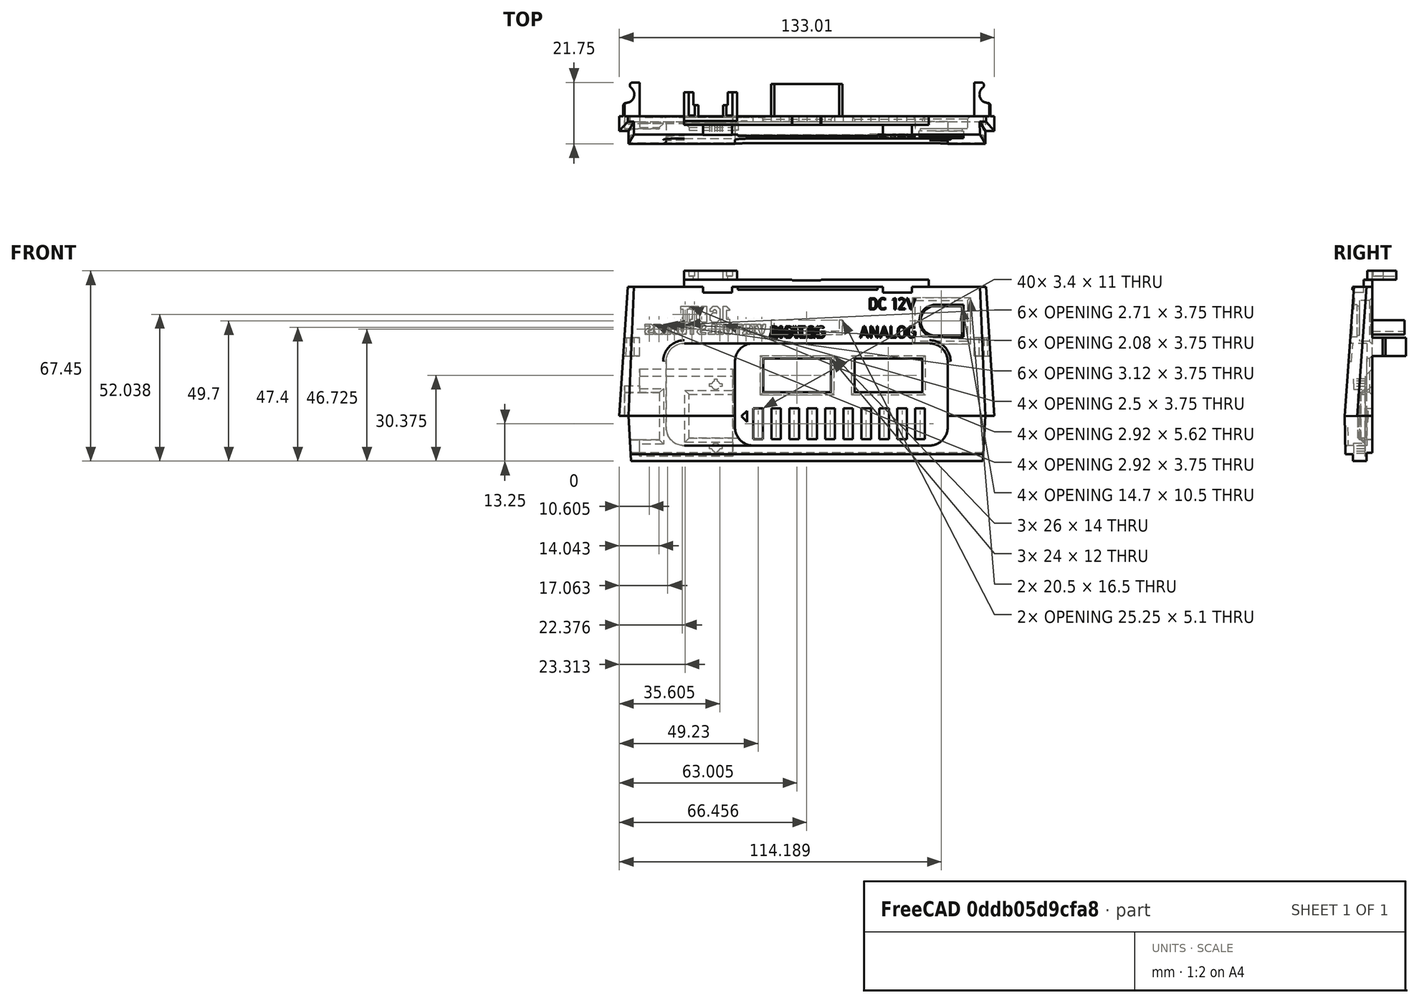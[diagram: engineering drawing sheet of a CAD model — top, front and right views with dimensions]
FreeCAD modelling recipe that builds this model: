
FCSTD DOCUMENT  (FreeCAD 1.0R39319 (Git))
Label: GameCube IO
License: Creative Commons Attribution-NonCommercial-ShareAlike 4.0
LicenseURL: https://creativecommons.org/licenses/by-nc-sa/4.0/
objects: PartDesign::Pocket×37, Sketcher::SketchObject×36, Part::Part2DObjectPython×13, PartDesign::Pad×12, PartDesign::Body×8, PartDesign::FeatureBase×7, PartDesign::Chamfer×3, PartDesign::Fillet×2, App::DocumentObjectGroup×2, PartDesign::LinearPattern×1, PartDesign::ShapeBinder×1
note: 272 computed .brp shape members not serialized (recipe doc carries the construction recipe); baked Part::Feature solids carry a one-line shape summary decoded from their .brp

FEATURE [Sketcher::SketchObject] Sketch
  ArcFitTolerance = 1e-06
  AttachmentSupport = -> [XZ_Plane]
  FullyConstrained = true
  MakeInternals = false
  MapMode = 5
  Placement = pos=(0,0,0) rot=(1,0,0;1.5708rad)
  sketch-geometry (11):
    g0: LineSegment StartX=0 StartY=0 StartZ=0 EndX=124.75 EndY=0 EndZ=0
    g1: LineSegment StartX=0 StartY=0 StartZ=0 EndX=-0.875 EndY=16 EndZ=0
    g2: LineSegment StartX=124.75 StartY=0 StartZ=0 EndX=125.625 EndY=16 EndZ=0
    g3: LineSegment [constr] StartX=-0.875 StartY=16 StartZ=0 EndX=125.625 EndY=16 EndZ=0
    g4: LineSegment [constr] StartX=62.375 StartY=0 StartZ=0 EndX=62.375 EndY=16 EndZ=0
    g5: LineSegment [constr] StartX=62.375 StartY=16 StartZ=0 EndX=62.375 EndY=61.75 EndZ=0
    g6: LineSegment StartX=-1.125 StartY=61.75 StartZ=0 EndX=125.875 EndY=61.75 EndZ=0
    g7: LineSegment StartX=-0.875 StartY=16 StartZ=0 EndX=-4.125 EndY=16 EndZ=0
    g8: LineSegment StartX=-4.125 StartY=16 StartZ=0 EndX=-1.125 EndY=61.75 EndZ=0
    g9: LineSegment StartX=125.625 StartY=16 StartZ=0 EndX=128.875 EndY=16 EndZ=0
    g10: LineSegment StartX=128.875 StartY=16 StartZ=0 EndX=125.875 EndY=61.75 EndZ=0
  constraints (29):
    c: Coincident(g0,g-1)
    c: PointOnObject(g0,g-1)
    c: Distance(g0) = 124.75
    c: Coincident(g1,g0)
    c: Coincident(g2,g0)
    c: Equal(g1,g2)
    c: Coincident(g3,g1)
    c: Distance(g3) = 126.5
    c: Vertical(g4)
    c: Symmetric(g0,g0,g4)
    c: Symmetric(g2,g1,g4)
    c: Coincident(g3,g2)
    c: Distance(g4) = 16
    c: Coincident(g5,g4)
    c: Vertical(g5)
    c: Distance(g5) = 45.75
    c: Horizontal(g6)
    c: Symmetric(g6,g6,g5)
    c: Coincident(g7,g1)
    c: Horizontal(g7)
    c: Coincident(g8,g7)
    c: Coincident(g8,g6)
    c: Coincident(g9,g2)
    c: Horizontal(g9)
    c: Coincident(g10,g9)
    c: Coincident(g10,g6)
    c: Equal(g8,g10)
    c: Distance(g9) = 3.25
    c: Distance(g6) = 127
FEATURE [PartDesign::Pad] Pad
  Direction = (0,-1,2e-16)
  Length = 3.1
  Length2 = 0.25
  Placement = pos=(0,0,0) rot=(1,0,0;1.5708rad)
  Profile = -> Sketch
  ReferenceAxis = -> Sketch [N_Axis]
  Refine = true
  Suppressed = false
  Type = 4
FEATURE [Sketcher::SketchObject] Sketch001
  ArcFitTolerance = 1e-06
  AttachmentSupport = -> [Pad]
  ExternalGeometry = -> [Pad]
  FullyConstrained = true
  MakeInternals = false
  MapMode = 5
  Placement = pos=(0,-3.1,0) rot=(1,0,0;1.5708rad)
  sketch-geometry (8):
    g0: LineSegment StartX=12.45 StartY=5.5 StartZ=0 EndX=112.3 EndY=5.5 EndZ=0
    g1: LineSegment StartX=112.3 StartY=5.5 StartZ=0 EndX=112.3 EndY=41.75 EndZ=0
    g2: LineSegment StartX=112.3 StartY=41.75 StartZ=0 EndX=12.45 EndY=41.75 EndZ=0
    g3: LineSegment StartX=12.45 StartY=41.75 StartZ=0 EndX=12.45 EndY=5.5 EndZ=0
    g4: GeomPoint [constr] X=62.375 Y=23.625 Z=0
    g5: LineSegment [constr] StartX=128.875 StartY=16 StartZ=0 EndX=112.3 EndY=16 EndZ=0
    g6: LineSegment [constr] StartX=-4.125 StartY=16 StartZ=0 EndX=12.45 EndY=16 EndZ=0
    g7: LineSegment [constr] StartX=12.45 StartY=5.5 StartZ=0 EndX=12.45 EndY=0 EndZ=0
  constraints (22):
    c: Coincident(g0,g1)
    c: Coincident(g1,g2)
    c: Coincident(g2,g3)
    c: Coincident(g3,g0)
    c: Horizontal(g0)
    c: Horizontal(g2)
    c: Vertical(g1)
    c: Vertical(g3)
    c: Symmetric(g2,g0,g4)
    c: Distance(g2) = 99.85
    c: Distance(g1) = 36.25
    c: Coincident(g5,g-4)
    c: PointOnObject(g5,g1)
    c: Horizontal(g5)
    c: Coincident(g6,g-3)
    c: PointOnObject(g6,g3)
    c: Horizontal(g6)
    c: Equal(g6,g5)
    c: Coincident(g7,g0)
    c: PointOnObject(g7,g-1)
    c: Vertical(g7)
    c: Distance(g7) = 5.5
FEATURE [PartDesign::Pocket] Pocket
  BaseFeature = -> Pad
  Direction = (0,1,-2e-16)
  Length = 0
  Length2 = 5
  Offset = -1.9
  Placement = pos=(0,0,0) rot=(1,0,0;1.5708rad)
  Profile = -> Sketch001
  ReferenceAxis = -> Sketch001 [N_Axis]
  Refine = true
  Suppressed = false
  Type = 3
  UpToFace = -> Pad [Face9]
FEATURE [Sketcher::SketchObject] Sketch002
  ArcFitTolerance = 1e-06
  AttachmentSupport = -> [Pocket]
  ExternalGeometry = -> [Pocket]
  FullyConstrained = true
  MakeInternals = false
  MapMode = 5
  Placement = pos=(0,-1.65,4e-16) rot=(1,0,0;1.5708rad)
  sketch-geometry (14):
    g0: LineSegment [constr] StartX=12.45 StartY=41.75 StartZ=0 EndX=112.3 EndY=41.75 EndZ=0
    g1: LineSegment [constr] StartX=112.3 StartY=5.5 StartZ=0 EndX=12.45 EndY=5.5 EndZ=0
    g2: ArcOfCircle CenterX=18.95 CenterY=35.25 CenterZ=0 NormalX=0 NormalY=0 NormalZ=1 AngleXU=0 Radius=6.5 StartAngle=1.5708 EndAngle=3.14159
    g3: ArcOfCircle CenterX=18.95 CenterY=12 CenterZ=0 NormalX=0 NormalY=0 NormalZ=1 AngleXU=0 Radius=6.5 StartAngle=3.14159 EndAngle=4.71239
    g4: ArcOfCircle CenterX=105.8 CenterY=35.25 CenterZ=0 NormalX=0 NormalY=0 NormalZ=1 AngleXU=0 Radius=6.5 StartAngle=-1.8e-15 EndAngle=1.5708
    g5: ArcOfCircle CenterX=105.8 CenterY=12 CenterZ=0 NormalX=0 NormalY=0 NormalZ=1 AngleXU=0 Radius=6.5 StartAngle=4.71239 EndAngle=6.28319
    g6: LineSegment StartX=105.8 StartY=41.75 StartZ=0 EndX=112.3 EndY=41.75 EndZ=0
    g7: LineSegment StartX=112.3 StartY=41.75 StartZ=0 EndX=112.3 EndY=35.25 EndZ=0
    g8: LineSegment StartX=112.3 StartY=12 StartZ=0 EndX=112.3 EndY=5.5 EndZ=0
    g9: LineSegment StartX=112.3 StartY=5.5 StartZ=0 EndX=105.8 EndY=5.5 EndZ=0
    g10: LineSegment StartX=18.95 StartY=5.5 StartZ=0 EndX=12.45 EndY=5.5 EndZ=0
    g11: LineSegment StartX=12.45 StartY=5.5 StartZ=0 EndX=12.45 EndY=12 EndZ=0
    g12: LineSegment StartX=12.45 StartY=35.25 StartZ=0 EndX=12.45 EndY=41.75 EndZ=0
    g13: LineSegment StartX=12.45 StartY=41.75 StartZ=0 EndX=18.95 EndY=41.75 EndZ=0
  constraints (32):
    c: Coincident(g0,g-3)
    c: Coincident(g0,g-4)
    c: Coincident(g1,g-4)
    c: Coincident(g1,g-3)
    c: PointOnObject(g2,g-3)
    c: PointOnObject(g2,g0)
    c: PointOnObject(g3,g-3)
    c: PointOnObject(g3,g1)
    c: PointOnObject(g4,g0)
    c: PointOnObject(g4,g-4)
    c: PointOnObject(g5,g-4)
    c: PointOnObject(g5,g1)
    c: Coincident(g6,g0)
    c: Coincident(g7,g0)
    c: Tangent(g7,g4) = 1.5708
    c: Coincident(g8,g1)
    c: Coincident(g9,g1)
    c: Tangent(g9,g5) = 1.5708
    c: Tangent(g10,g3) = 1.5708
    c: Coincident(g10,g1)
    c: Coincident(g11,g1)
    c: Tangent(g11,g3) = 1.5708
    c: Coincident(g12,g0)
    c: Coincident(g13,g0)
    c: Tangent(g13,g2) = 1.5708
    c: Tangent(g12,g2) = 1.5708
    c: Tangent(g8,g5) = 1.5708
    c: Tangent(g6,g4) = 1.5708
    c: Equal(g2,g3)
    c: Equal(g3,g5)
    c: Equal(g5,g4)
    c: Radius(g4) = 6.5
FEATURE [PartDesign::Pad] Pad001
  BaseFeature = -> Pocket
  Direction = (0,-1,2e-16)
  Length = 10
  Length2 = 10
  Placement = pos=(0,0,0) rot=(1,0,0;1.5708rad)
  Profile = -> Sketch002
  ReferenceAxis = -> Sketch002 [N_Axis]
  Refine = true
  Suppressed = false
  Type = 3
  UpToFace = -> Pocket [Face5]
FEATURE [PartDesign::Pad] Pad002
  BaseFeature = -> Pad001
  Direction = (0,-1,2e-16)
  Length = 10
  Length2 = 10
  Offset = -9.75
  Placement = pos=(0,0,0) rot=(1,0,0;1.5708rad)
  Profile = -> Pad001 [Face10]
  Refine = true
  Suppressed = false
  Type = 3
  UpToFace = -> Pad001 [Face4]
FEATURE [Sketcher::SketchObject] Sketch003
  ArcFitTolerance = 1e-06
  AttachmentSupport = -> [YZ_Plane]
  ExternalGeometry = -> [Pad002]
  FullyConstrained = true
  MakeInternals = false
  MapMode = 5
  Placement = pos=(0,0,0) rot=(0.57735,0.57735,0.57735;2.0944rad)
  sketch-geometry (13):
    g0: LineSegment [constr] StartX=0 StartY=0 StartZ=0 EndX=-6.5 EndY=0 EndZ=0
    g1: LineSegment StartX=-6.5 StartY=0 StartZ=0 EndX=-6.5 EndY=2.5 EndZ=0
    g2: LineSegment StartX=-6.5 StartY=2.5 StartZ=0 EndX=-9.25 EndY=2.5 EndZ=0
    g3: LineSegment StartX=-9.25 StartY=2.5 StartZ=0 EndX=-9.5 EndY=16 EndZ=0
    g4: LineSegment StartX=-9.5 StartY=16 StartZ=0 EndX=-6 EndY=64.25 EndZ=0
    g5: LineSegment StartX=-6 StartY=64.25 StartZ=0 EndX=-21.5 EndY=64.25 EndZ=0
    g6: LineSegment StartX=-21.5 StartY=64.25 StartZ=0 EndX=-21.5 EndY=0 EndZ=0
    g7: LineSegment StartX=-21.5 StartY=0 StartZ=0 EndX=-6.5 EndY=0 EndZ=0
    g8: LineSegment [constr] StartX=0.5 StartY=64.25 StartZ=0 EndX=-6 EndY=64.25 EndZ=0
    g9: LineSegment StartX=0.25 StartY=0 StartZ=0 EndX=0.25 EndY=3 EndZ=0
    g10: LineSegment StartX=0.25 StartY=3 StartZ=0 EndX=-1.75 EndY=3 EndZ=0
    g11: LineSegment StartX=-1.75 StartY=3 StartZ=0 EndX=-1.75 EndY=0 EndZ=0
    g12: LineSegment StartX=-1.75 StartY=0 StartZ=0 EndX=0.25 EndY=0 EndZ=0
  constraints (35):
    c: PointOnObject(g0,g-1)
    c: Coincident(g0,g1)
    c: Vertical(g1)
    c: Coincident(g1,g2)
    c: Horizontal(g2)
    c: Coincident(g2,g3)
    c: Coincident(g3,g4)
    c: Coincident(g4,g5)
    c: Horizontal(g5)
    c: Coincident(g5,g6)
    c: PointOnObject(g6,g-1)
    c: Vertical(g6)
    c: Coincident(g6,g7)
    c: Coincident(g7,g0)
    c: Coincident(g3,g-3)
    c: Coincident(g8,g-4)
    c: PointOnObject(g8,g-4)
    c: Coincident(g4,g8)
    c: Distance(g8) = 6.5
    c: Equal(g8,g0)
    c: Distance(g1) = 2.5
    c: Distance(g2) = 2.75
    c: Distance(g7) = 15
    c: Coincident(g9,g10)
    c: Coincident(g10,g11)
    c: Coincident(g11,g12)
    c: Coincident(g12,g9)
    c: Vertical(g9)
    c: Vertical(g11)
    c: Horizontal(g10)
    c: Horizontal(g12)
    c: Distance(g9) = 3
    c: Distance(g10) = 2
    c: Coincident(g-1,g0)
    c: Coincident(g-5,g9)
FEATURE [PartDesign::Pocket] Pocket001
  BaseFeature = -> Pad002
  Direction = (-1,0,0)
  Length = 150
  Length2 = 150
  Placement = pos=(0,0,0) rot=(1,0,0;1.5708rad)
  Profile = -> Sketch003
  ReferenceAxis = -> Sketch003 [N_Axis]
  Refine = true
  Suppressed = false
  Type = 4
FEATURE [Sketcher::SketchObject] Sketch004
  ArcFitTolerance = 1e-06
  AttachmentSupport = -> [Pocket001]
  ExternalGeometry = -> [Pocket001]
  FullyConstrained = true
  MakeInternals = false
  MapMode = 5
  Placement = pos=(0,-10.6048,0.769262) rot=(1,0,0;1.49838rad)
  sketch-geometry (16):
    g0: LineSegment [constr] StartX=128.917 StartY=14.0456 StartZ=0 EndX=125.677 EndY=14.0456 EndZ=0
    g1: LineSegment StartX=125.677 StartY=14.0456 StartZ=0 EndX=123.098 EndY=74.9911 EndZ=0
    g2: LineSegment [constr] StartX=123.098 StartY=74.9911 StartZ=0 EndX=126.338 EndY=74.9911 EndZ=0
    g3: LineSegment [constr] StartX=126.338 StartY=74.9911 StartZ=0 EndX=128.875 EndY=15.0447 EndZ=0
    g4: LineSegment [constr] StartX=-4.125 StartY=15.0447 StartZ=0 EndX=-1.58811 EndY=74.9911 EndZ=0
    g5: LineSegment [constr] StartX=-1.58811 StartY=74.9911 StartZ=0 EndX=1.65232 EndY=74.9911 EndZ=0
    g6: LineSegment StartX=1.65232 StartY=74.9911 StartZ=0 EndX=-0.926847 EndY=14.0456 EndZ=0
    g7: LineSegment [constr] StartX=-0.926847 StartY=14.0456 StartZ=0 EndX=-4.16728 EndY=14.0456 EndZ=0
    g8: LineSegment StartX=1.65232 StartY=74.9911 StartZ=0 EndX=-8.34768 EndY=74.9911 EndZ=0
    g9: LineSegment StartX=-8.34768 StartY=74.9911 StartZ=0 EndX=-10.9268 EndY=14.0456 EndZ=0
    g10: LineSegment StartX=-10.9268 StartY=14.0456 StartZ=0 EndX=-0.926847 EndY=14.0456 EndZ=0
    g11: LineSegment StartX=125.677 StartY=14.0456 StartZ=0 EndX=135.677 EndY=14.0456 EndZ=0
    g12: LineSegment StartX=135.677 StartY=14.0456 StartZ=0 EndX=133.098 EndY=74.9911 EndZ=0
    g13: LineSegment StartX=133.098 StartY=74.9911 StartZ=0 EndX=123.098 EndY=74.9911 EndZ=0
    g14: LineSegment [constr] StartX=128.875 StartY=15.0447 StartZ=0 EndX=128.917 EndY=14.0456 EndZ=0
    g15: LineSegment [constr] StartX=-4.125 StartY=15.0447 StartZ=0 EndX=-4.16728 EndY=14.0456 EndZ=0
  constraints (44):
    c: Horizontal(g0)
    c: Coincident(g1,g0)
    c: Coincident(g2,g1)
    c: Horizontal(g2)
    c: Coincident(g3,g2)
    c: PointOnObject(g-4,g3)
    c: Parallel(g1,g3)
    c: Distance(g3) = 60
    c: Coincident(g5,g4)
    c: Coincident(g6,g5)
    c: Coincident(g7,g6)
    c: Horizontal(g7)
    c: Horizontal(g5)
    c: Parallel(g4,g6)
    c: PointOnObject(g-3,g4)
    c: Equal(g5,g2)
    c: Equal(g3,g4)
    c: Coincident(g5,g8)
    c: Horizontal(g8)
    c: Coincident(g8,g9)
    c: Coincident(g9,g10)
    c: Coincident(g10,g6)
    c: Horizontal(g10)
    c: Coincident(g0,g11)
    c: Horizontal(g11)
    c: Coincident(g11,g12)
    c: Coincident(g12,g13)
    c: Coincident(g13,g1)
    c: Horizontal(g13)
    c: Parallel(g3,g12)
    c: Parallel(g6,g9)
    c: Equal(g10,g11)
    c: Distance(g11) = 10
    c: Coincident(g-4,g3)
    c: Coincident(g14,g3)
    c: Coincident(g14,g0)
    c: Parallel(g3,g14)
    c: PointOnObject(g-5,g1)
    c: Distance(g14) = 1
    c: Coincident(g4,g-3)
    c: Coincident(g15,g4)
    c: Coincident(g15,g7)
    c: Parallel(g4,g15)
    c: Equal(g15,g14)
FEATURE [PartDesign::Pocket] Pocket002
  BaseFeature = -> Pocket001
  Direction = (0,0.997379,-0.0723488)
  Length = 4.5
  Length2 = 5
  Placement = pos=(0,0,0) rot=(1,0,0;1.5708rad)
  Profile = -> Sketch004
  ReferenceAxis = -> Sketch004 [N_Axis]
  Refine = true
  Suppressed = false
  Type = 0
FEATURE [Sketcher::SketchObject] Sketch005
  ArcFitTolerance = 1e-06
  AttachmentSupport = -> [Pocket002]
  ExternalGeometry = -> [Pocket002]
  FullyConstrained = true
  MakeInternals = false
  MapMode = 5
  Placement = pos=(0,0,61.75) rot=(0,0,1;3.14159rad)
  sketch-geometry (6):
    g0: LineSegment StartX=-105.575 StartY=-0.25 StartZ=0 EndX=-18.875 EndY=-0.25 EndZ=0
    g1: LineSegment StartX=-18.875 StartY=-0.25 StartZ=0 EndX=-18.875 EndY=2.75 EndZ=0
    g2: LineSegment StartX=-18.875 StartY=2.75 StartZ=0 EndX=-105.575 EndY=2.75 EndZ=0
    g3: LineSegment StartX=-105.575 StartY=2.75 StartZ=0 EndX=-105.575 EndY=-0.25 EndZ=0
    g4: LineSegment [constr] StartX=-125.875 StartY=-0.25 StartZ=0 EndX=-105.575 EndY=-0.25 EndZ=0
    g5: LineSegment [constr] StartX=-18.875 StartY=-0.25 StartZ=0 EndX=1.125 EndY=-0.25 EndZ=0
  constraints (16):
    c: Coincident(g0,g1)
    c: Coincident(g1,g2)
    c: Coincident(g2,g3)
    c: Coincident(g3,g0)
    c: Horizontal(g0)
    c: Horizontal(g2)
    c: Vertical(g1)
    c: Vertical(g3)
    c: PointOnObject(g0,g-3)
    c: Coincident(g4,g-3)
    c: Coincident(g4,g0)
    c: Coincident(g5,g0)
    c: Coincident(g5,g-3)
    c: Distance(g5) = 20
    c: Distance(g4) = 20.3
    c: Distance(g1) = 3
FEATURE [PartDesign::Pad] Pad003
  BaseFeature = -> Pocket002
  Direction = (0,0,1)
  Length = 2.5
  Length2 = 10
  Placement = pos=(0,0,0) rot=(1,0,0;1.5708rad)
  Profile = -> Sketch005
  ReferenceAxis = -> Sketch005 [N_Axis]
  Refine = true
  Suppressed = false
  Type = 0
FEATURE [Sketcher::SketchObject] Sketch006
  ArcFitTolerance = 1e-06
  AttachmentSupport = -> [Pad003]
  FullyConstrained = true
  MakeInternals = false
  MapMode = 5
  Placement = pos=(0,-2.75,6e-16) rot=(1,0,0;1.5708rad)
  sketch-geometry (10):
    g0: LineSegment [constr] StartX=1.075 StartY=64.25 StartZ=0 EndX=25.575 EndY=64.25 EndZ=0
    g1: LineSegment [constr] StartX=123.675 StartY=64.25 StartZ=0 EndX=99.675 EndY=64.25 EndZ=0
    g2: LineSegment StartX=25.575 StartY=64.25 StartZ=0 EndX=25.575 EndY=59.75 EndZ=0
    g3: LineSegment StartX=25.575 StartY=59.75 StartZ=0 EndX=35.875 EndY=59.75 EndZ=0
    g4: LineSegment StartX=35.875 StartY=59.75 StartZ=0 EndX=35.875 EndY=64.25 EndZ=0
    g5: LineSegment StartX=35.875 StartY=64.25 StartZ=0 EndX=25.575 EndY=64.25 EndZ=0
    g6: LineSegment StartX=99.675 StartY=64.25 StartZ=0 EndX=89.375 EndY=64.25 EndZ=0
    g7: LineSegment StartX=89.375 StartY=64.25 StartZ=0 EndX=89.375 EndY=59.75 EndZ=0
    g8: LineSegment StartX=89.375 StartY=59.75 StartZ=0 EndX=99.675 EndY=59.75 EndZ=0
    g9: LineSegment StartX=99.675 StartY=59.75 StartZ=0 EndX=99.675 EndY=64.25 EndZ=0
  constraints (28):
    c: Coincident(g0,g-3)
    c: PointOnObject(g0,g-3)
    c: Coincident(g1,g-3)
    c: PointOnObject(g1,g-3)
    c: Coincident(g2,g3)
    c: Coincident(g3,g4)
    c: Coincident(g4,g5)
    c: Coincident(g5,g2)
    c: Vertical(g2)
    c: Vertical(g4)
    c: Horizontal(g3)
    c: Horizontal(g5)
    c: Coincident(g2,g0)
    c: Coincident(g6,g7)
    c: Coincident(g7,g8)
    c: Coincident(g8,g9)
    c: Coincident(g9,g6)
    c: Horizontal(g6)
    c: Horizontal(g8)
    c: Vertical(g7)
    c: Vertical(g9)
    c: Coincident(g6,g1)
    c: Distance(g0) = 24.5
    c: Distance(g5) = 10.3
    c: Equal(g5,g6)
    c: Equal(g7,g4)
    c: Distance(g2) = 4.5
    c: Distance(g1) = 24
FEATURE [PartDesign::Pocket] Pocket003
  BaseFeature = -> Pad003
  Direction = (0,1,-2e-16)
  Length = 5
  Length2 = 5
  Placement = pos=(0,0,0) rot=(1,0,0;1.5708rad)
  Profile = -> Sketch006
  ReferenceAxis = -> Sketch006 [N_Axis]
  Refine = true
  Reversed = true
  Suppressed = false
  Type = 1
FEATURE [Sketcher::SketchObject] Sketch007
  ArcFitTolerance = 1e-06
  AttachmentSupport = -> [Pocket003]
  ExternalGeometry = -> [Pocket003]
  FullyConstrained = true
  MakeInternals = false
  MapMode = 5
  Placement = pos=(0,-2.75,-5.1e-15) rot=(1,0,0;1.5708rad)
  sketch-geometry (6):
    g0: LineSegment [constr] StartX=35.875 StartY=61.75 StartZ=0 EndX=37.875 EndY=61.75 EndZ=0
    g1: LineSegment [constr] StartX=89.375 StartY=61.75 StartZ=0 EndX=87.375 EndY=61.75 EndZ=0
    g2: LineSegment StartX=37.875 StartY=61.75 StartZ=0 EndX=37.875 EndY=60.75 EndZ=0
    g3: LineSegment StartX=37.875 StartY=60.75 StartZ=0 EndX=87.375 EndY=60.75 EndZ=0
    g4: LineSegment StartX=87.375 StartY=60.75 StartZ=0 EndX=87.375 EndY=61.75 EndZ=0
    g5: LineSegment StartX=87.375 StartY=61.75 StartZ=0 EndX=37.875 EndY=61.75 EndZ=0
  constraints (16):
    c: Coincident(g2,g3)
    c: Coincident(g3,g4)
    c: Coincident(g4,g5)
    c: Coincident(g5,g2)
    c: Vertical(g2)
    c: Vertical(g4)
    c: Horizontal(g3)
    c: Coincident(g2,g0)
    c: Coincident(g4,g1)
    c: Equal(g1,g0)
    c: Distance(g0) = 2
    c: Distance(g2) = 1
    c: Coincident(g0,g-3)
    c: Coincident(g1,g-3)
    c: PointOnObject(g0,g-3)
    c: PointOnObject(g1,g-3)
FEATURE [PartDesign::Pad] Pad004
  BaseFeature = -> Pocket003
  Direction = (0,-1,-2.1e-15)
  Length = 10
  Length2 = 10
  Offset = 0.5
  Placement = pos=(0,0,0) rot=(1,0,0;1.5708rad)
  Profile = -> Sketch007
  ReferenceAxis = -> Sketch007 [N_Axis]
  Refine = true
  Suppressed = false
  Type = 3
  UpToFace = -> Pocket003 [Face11]
FEATURE [Sketcher::SketchObject] Sketch008
  ArcFitTolerance = 1e-06
  AttachmentSupport = -> [Pad004]
  FullyConstrained = true
  MakeInternals = false
  MapMode = 5
  Placement = pos=(0,-2.75,-5.1e-15) rot=(1,0,0;1.5708rad)
  sketch-geometry (7):
    g0: LineSegment [constr] StartX=17.925 StartY=64.75 StartZ=0 EndX=56.6 EndY=64.75 EndZ=0
    g1: LineSegment [constr] StartX=106.525 StartY=64.75 StartZ=0 EndX=67.85 EndY=64.75 EndZ=0
    g2: LineSegment StartX=56.6 StartY=64.75 StartZ=0 EndX=67.85 EndY=64.75 EndZ=0
    g3: LineSegment StartX=56.6 StartY=64.75 StartZ=0 EndX=57.225 EndY=64 EndZ=0
    g4: LineSegment StartX=57.225 StartY=64 StartZ=0 EndX=67.225 EndY=64 EndZ=0
    g5: LineSegment StartX=67.225 StartY=64 StartZ=0 EndX=67.85 EndY=64.75 EndZ=0
    g6: LineSegment [constr] StartX=57.225 StartY=64 StartZ=0 EndX=57.225 EndY=64.75 EndZ=0
  constraints (19):
    c: Coincident(g0,g-3)
    c: PointOnObject(g0,g-3)
    c: Coincident(g1,g-3)
    c: PointOnObject(g1,g-3)
    c: Coincident(g2,g0)
    c: Coincident(g2,g1)
    c: Distance(g2) = 11.25
    c: Equal(g1,g0)
    c: Coincident(g3,g0)
    c: Coincident(g4,g3)
    c: Coincident(g5,g4)
    c: Coincident(g5,g1)
    c: Horizontal(g4)
    c: Equal(g5,g3)
    c: Coincident(g6,g3)
    c: PointOnObject(g6,g2)
    c: Vertical(g6)
    c: Distance(g6) = 0.75
    c: Distance(g4) = 10
FEATURE [PartDesign::Pocket] Pocket004
  BaseFeature = -> Pad004
  Direction = (0,1,2.1e-15)
  Length = 5
  Length2 = 5
  Placement = pos=(0,0,0) rot=(1,0,0;1.5708rad)
  Profile = -> Sketch008
  ReferenceAxis = -> Sketch008 [N_Axis]
  Refine = true
  Suppressed = false
  Type = 1
FEATURE [Sketcher::SketchObject] Sketch009
  ArcFitTolerance = 1e-06
  AttachmentSupport = -> [Pocket004]
  ExternalGeometry = -> [Pocket004]
  FullyConstrained = true
  MakeInternals = false
  MapMode = 5
  Placement = pos=(0,0,64.25) rot=(0,0,1;3.14159rad)
  sketch-geometry (17):
    g0: LineSegment [constr] StartX=-18.875 StartY=-0.25 StartZ=0 EndX=-37.625 EndY=-0.25 EndZ=0
    g1: LineSegment StartX=-37.625 StartY=-0.25 StartZ=0 EndX=-37.625 EndY=-8.75 EndZ=0
    g2: LineSegment [constr] StartX=-37.625 StartY=-8.75 StartZ=0 EndX=-18.875 EndY=-8.75 EndZ=0
    g3: LineSegment StartX=-18.875 StartY=-8.75 StartZ=0 EndX=-18.875 EndY=-0.25 EndZ=0
    g4: LineSegment StartX=-37.625 StartY=-0.25 StartZ=0 EndX=-37.625 EndY=1.45 EndZ=0
    g5: LineSegment StartX=-37.625 StartY=1.45 StartZ=0 EndX=-18.875 EndY=1.45 EndZ=0
    g6: LineSegment StartX=-18.875 StartY=1.45 StartZ=0 EndX=-18.875 EndY=-0.25 EndZ=0
    g7: LineSegment [constr] StartX=-18.875 StartY=2.75 StartZ=0 EndX=-18.875 EndY=1.45 EndZ=0
    g8: LineSegment StartX=-37.625 StartY=-8.75 StartZ=0 EndX=-34.375 EndY=-8.75 EndZ=0
    g9: LineSegment StartX=-34.375 StartY=-8.75 StartZ=0 EndX=-34.375 EndY=-4.25 EndZ=0
    g10: LineSegment StartX=-34.375 StartY=-4.25 StartZ=0 EndX=-32.625 EndY=-4.25 EndZ=0
    g11: LineSegment StartX=-32.625 StartY=-4.25 StartZ=0 EndX=-32.625 EndY=-0.25 EndZ=0
    g12: LineSegment StartX=-32.625 StartY=-0.25 StartZ=0 EndX=-23.875 EndY=-0.25 EndZ=0
    g13: LineSegment StartX=-23.875 StartY=-0.25 StartZ=0 EndX=-23.875 EndY=-4.25 EndZ=0
    g14: LineSegment StartX=-23.875 StartY=-4.25 StartZ=0 EndX=-22.125 EndY=-4.25 EndZ=0
    g15: LineSegment StartX=-22.125 StartY=-4.25 StartZ=0 EndX=-22.125 EndY=-8.75 EndZ=0
    g16: LineSegment StartX=-22.125 StartY=-8.75 StartZ=0 EndX=-18.875 EndY=-8.75 EndZ=0
  constraints (47):
    c: Coincident(g0,g1)
    c: Coincident(g1,g2)
    c: Coincident(g2,g3)
    c: Coincident(g3,g0)
    c: Horizontal(g0)
    c: Horizontal(g2)
    c: Vertical(g1)
    c: Vertical(g3)
    c: Coincident(g0,g-3)
    c: Distance(g0) = 18.75
    c: Coincident(g0,g4)
    c: Vertical(g4)
    c: Coincident(g4,g5)
    c: Horizontal(g5)
    c: Coincident(g5,g6)
    c: Coincident(g6,g0)
    c: Vertical(g6)
    c: Coincident(g7,g5)
    c: Distance(g7) = 1.3
    c: Distance(g4,g1) = 10.2
    c: Coincident(g1,g8)
    c: PointOnObject(g8,g2)
    c: Coincident(g8,g9)
    c: Vertical(g9)
    c: Coincident(g9,g10)
    c: Horizontal(g10)
    c: Coincident(g10,g11)
    c: PointOnObject(g11,g0)
    c: Vertical(g11)
    c: Coincident(g11,g12)
    c: PointOnObject(g12,g0)
    c: Coincident(g12,g13)
    c: Vertical(g13)
    c: Coincident(g13,g14)
    c: Horizontal(g14)
    c: Coincident(g14,g15)
    c: PointOnObject(g15,g2)
    c: Vertical(g15)
    c: Coincident(g15,g16)
    c: Coincident(g16,g2)
    c: Equal(g8,g16)
    c: Equal(g14,g10)
    c: Distance(g8) = 3.25
    c: Distance(g9) = 4.5
    c: Distance(g10) = 1.75
    c: Equal(g9,g15)
    c: Coincident(g-4,g7)
FEATURE [PartDesign::Pad] Pad005
  BaseFeature = -> Pocket004
  Direction = (0,0,1)
  Length = 3.2
  Length2 = 10
  Placement = pos=(0,0,0) rot=(1,0,0;1.5708rad)
  Profile = -> Sketch009
  ReferenceAxis = -> Sketch009 [N_Axis]
  Refine = true
  Suppressed = false
  Type = 0
FEATURE [Sketcher::SketchObject] Sketch010
  ArcFitTolerance = 1e-06
  AttachmentSupport = -> [Pad005]
  ExternalGeometry = -> [Pad005]
  FullyConstrained = true
  MakeInternals = false
  MapMode = 5
  Placement = pos=(0,0,67.45) rot=(0,0,1;3.14159rad)
  sketch-geometry (12):
    g0: LineSegment [constr] StartX=-37.625 StartY=-8.75 StartZ=0 EndX=-36.025 EndY=-8.75 EndZ=0
    g1: LineSegment [constr] StartX=-18.875 StartY=-8.75 StartZ=0 EndX=-20.475 EndY=-8.75 EndZ=0
    g2: LineSegment [constr] StartX=-33.825 StartY=1.45 StartZ=0 EndX=-33.825 EndY=-0.55 EndZ=0
    g3: LineSegment [constr] StartX=-22.675 StartY=1.45 StartZ=0 EndX=-22.675 EndY=-0.55 EndZ=0
    g4: LineSegment StartX=-36.025 StartY=-8.75 StartZ=0 EndX=-33.825 EndY=-8.75 EndZ=0
    g5: LineSegment StartX=-33.825 StartY=-8.75 StartZ=0 EndX=-33.825 EndY=-0.55 EndZ=0
    g6: LineSegment StartX=-33.825 StartY=-0.55 StartZ=0 EndX=-36.025 EndY=-0.55 EndZ=0
    g7: LineSegment StartX=-36.025 StartY=-0.55 StartZ=0 EndX=-36.025 EndY=-8.75 EndZ=0
    g8: LineSegment StartX=-20.475 StartY=-8.75 StartZ=0 EndX=-20.475 EndY=-0.55 EndZ=0
    g9: LineSegment StartX=-20.475 StartY=-0.55 StartZ=0 EndX=-22.675 EndY=-0.55 EndZ=0
    g10: LineSegment StartX=-22.675 StartY=-0.55 StartZ=0 EndX=-22.675 EndY=-8.75 EndZ=0
    g11: LineSegment StartX=-22.675 StartY=-8.75 StartZ=0 EndX=-20.475 EndY=-8.75 EndZ=0
  constraints (34):
    c: Coincident(g0,g-3)
    c: PointOnObject(g0,g-3)
    c: Coincident(g1,g-4)
    c: PointOnObject(g1,g-4)
    c: Equal(g0,g1)
    c: PointOnObject(g2,g-5)
    c: Vertical(g2)
    c: PointOnObject(g3,g-5)
    c: Vertical(g3)
    c: Coincident(g4,g5)
    c: Coincident(g5,g6)
    c: Coincident(g6,g7)
    c: Coincident(g7,g4)
    c: Horizontal(g4)
    c: Horizontal(g6)
    c: Vertical(g5)
    c: Vertical(g7)
    c: Coincident(g4,g0)
    c: Coincident(g5,g2)
    c: Coincident(g8,g9)
    c: Coincident(g9,g10)
    c: Coincident(g10,g11)
    c: Coincident(g11,g8)
    c: Vertical(g8)
    c: Vertical(g10)
    c: Horizontal(g9)
    c: Horizontal(g11)
    c: Coincident(g8,g1)
    c: Coincident(g9,g3)
    c: Equal(g2,g3)
    c: Equal(g11,g4)
    c: Distance(g0) = 1.6
    c: Distance(g2) = 2
    c: Distance(g6) = 2.2
FEATURE [PartDesign::Pocket] Pocket005
  BaseFeature = -> Pad005
  Direction = (0,0,-1)
  Length = 0
  Length2 = 5
  Offset = 1.3
  Placement = pos=(0,0,0) rot=(1,0,0;1.5708rad)
  Profile = -> Sketch010
  ReferenceAxis = -> Sketch010 [N_Axis]
  Refine = true
  Suppressed = false
  Type = 3
  UpToFace = -> Pad005 [Face48]
FEATURE [Sketcher::SketchObject] Sketch011
  ArcFitTolerance = 1e-06
  AttachmentSupport = -> [Pocket005]
  ExternalGeometry = -> [Pocket005]
  FullyConstrained = true
  MakeInternals = false
  MapMode = 5
  Placement = pos=(0,0.25,-1e-16) rot=(-1,0,0;1.5708rad)
  sketch-geometry (14):
    g0: LineSegment StartX=49.7012 StartY=-49.95 StartZ=0 EndX=49.7012 EndY=-44.85 EndZ=0
    g1: LineSegment StartX=49.7012 StartY=-44.85 StartZ=0 EndX=74.9512 EndY=-44.85 EndZ=0
    g2: LineSegment StartX=74.9512 StartY=-44.85 StartZ=0 EndX=74.9512 EndY=-49.95 EndZ=0
    g3: LineSegment StartX=74.9512 StartY=-49.95 StartZ=0 EndX=73.8512 EndY=-49.95 EndZ=0
    g4: LineSegment StartX=73.8512 StartY=-49.95 StartZ=0 EndX=73.8512 EndY=-45.95 EndZ=0
    g5: LineSegment StartX=73.8512 StartY=-45.95 StartZ=0 EndX=50.8012 EndY=-45.95 EndZ=0
    g6: LineSegment StartX=50.8012 StartY=-45.95 StartZ=0 EndX=50.8012 EndY=-49.95 EndZ=0
    g7: LineSegment StartX=50.8012 StartY=-49.95 StartZ=0 EndX=49.7012 EndY=-49.95 EndZ=0
    g8: LineSegment [constr] StartX=50.8012 StartY=-49.95 StartZ=0 EndX=73.8512 EndY=-49.95 EndZ=0
    g9: LineSegment [constr] StartX=50.8012 StartY=-45.95 StartZ=0 EndX=50.8012 EndY=-44.85 EndZ=0
    g10: LineSegment [constr] StartX=57.0167 StartY=-64.25 StartZ=0 EndX=57.0167 EndY=-49.95 EndZ=0
    g11: LineSegment [constr] StartX=49.7012 StartY=-44.85 StartZ=0 EndX=49.7012 EndY=0 EndZ=0
    g12: LineSegment [constr] StartX=50.8012 StartY=-49.95 StartZ=0 EndX=-1.89877 EndY=-49.95 EndZ=0
    g13: LineSegment [constr] StartX=73.8512 StartY=-49.95 StartZ=0 EndX=126.649 EndY=-49.95 EndZ=0
  constraints (41):
    c: Vertical(g0)
    c: Coincident(g0,g1)
    c: Horizontal(g1)
    c: Coincident(g1,g2)
    c: Vertical(g2)
    c: Coincident(g2,g3)
    c: Horizontal(g3)
    c: Coincident(g3,g4)
    c: Vertical(g4)
    c: Coincident(g4,g5)
    c: Horizontal(g5)
    c: Coincident(g5,g6)
    c: Vertical(g6)
    c: Coincident(g6,g7)
    c: Coincident(g7,g0)
    c: Horizontal(g7)
    c: Coincident(g6,g8)
    c: Coincident(g8,g3)
    c: Horizontal(g8)
    c: Coincident(g9,g5)
    c: PointOnObject(g9,g1)
    c: Vertical(g9)
    c: Distance(g9) = 1.1
    c: Equal(g9,g7)
    c: Equal(g7,g3)
    c: Distance(g1) = 25.25
    c: Distance(g2) = 5.1
    c: Coincident(g10,g-3)
    c: PointOnObject(g10,g8)
    c: Vertical(g10)
    c: Coincident(g11,g0)
    c: PointOnObject(g11,g-4)
    c: Vertical(g11)
    c: Distance(g11) = 44.85
    c: Coincident(g12,g6)
    c: PointOnObject(g12,g-5)
    c: Horizontal(g12)
    c: Coincident(g13,g3)
    c: PointOnObject(g13,g-6)
    c: Horizontal(g13)
    c: Distance(g12) = 52.7
FEATURE [PartDesign::Pad] Pad006
  BaseFeature = -> Pocket005
  Direction = (0,1,2e-16)
  Length = 11.5
  Length2 = 10
  Placement = pos=(0,0,0) rot=(1,0,0;1.5708rad)
  Profile = -> Sketch011
  ReferenceAxis = -> Sketch011 [N_Axis]
  Refine = true
  Suppressed = false
  Type = 0
FEATURE [Sketcher::SketchObject] Sketch012
  ArcFitTolerance = 1e-06
  AttachmentSupport = -> [Pad006]
  FullyConstrained = true
  MakeInternals = false
  MapMode = 5
  Placement = pos=(0,-1.65,4e-16) rot=(1,0,0;1.5708rad)
  sketch-geometry (8):
    g0: LineSegment StartX=47.4 StartY=36.1 StartZ=0 EndX=47.4 EndY=24.65 EndZ=0
    g1: LineSegment StartX=47.4 StartY=24.65 StartZ=0 EndX=70.35 EndY=24.65 EndZ=0
    g2: LineSegment StartX=70.35 StartY=24.65 StartZ=0 EndX=70.35 EndY=36.1 EndZ=0
    g3: LineSegment StartX=70.35 StartY=36.1 StartZ=0 EndX=47.4 EndY=36.1 EndZ=0
    g4: LineSegment [constr] StartX=47.4 StartY=36.1 StartZ=0 EndX=112.3 EndY=36.1 EndZ=0
    g5: LineSegment [constr] StartX=70.35 StartY=24.65 StartZ=0 EndX=12.45 EndY=24.65 EndZ=0
    g6: LineSegment [constr] StartX=47.4 StartY=36.1 StartZ=0 EndX=47.4 EndY=5.5 EndZ=0
    g7: LineSegment [constr] StartX=70.35 StartY=24.65 StartZ=0 EndX=70.35 EndY=41.75 EndZ=0
  constraints (24):
    c: Coincident(g0,g1)
    c: Coincident(g1,g2)
    c: Coincident(g2,g3)
    c: Coincident(g3,g0)
    c: Vertical(g0)
    c: Vertical(g2)
    c: Horizontal(g1)
    c: Horizontal(g3)
    c: Coincident(g4,g0)
    c: PointOnObject(g4,g-5)
    c: Coincident(g5,g1)
    c: Horizontal(g5)
    c: Coincident(g6,g0)
    c: PointOnObject(g6,g-6)
    c: Vertical(g6)
    c: Horizontal(g4)
    c: Distance(g4) = 64.9
    c: Distance(g6) = 30.6
    c: Distance(g5) = 57.9
    c: Coincident(g7,g1)
    c: PointOnObject(g7,g-3)
    c: Vertical(g7)
    c: PointOnObject(g5,g-4)
    c: Distance(g7) = 17.1
FEATURE [PartDesign::Pocket] Pocket006
  BaseFeature = -> Pad006
  Direction = (0,1,-2e-16)
  Length = 5
  Length2 = 5
  Placement = pos=(0,0,0) rot=(1,0,0;1.5708rad)
  Profile = -> Sketch012
  ReferenceAxis = -> Sketch012 [N_Axis]
  Refine = true
  Suppressed = false
  Type = 1
FEATURE [Sketcher::SketchObject] Sketch013
  ArcFitTolerance = 1e-06
  AttachmentSupport = -> [Pocket006]
  ExternalGeometry = -> [Pocket006]
  FullyConstrained = true
  MakeInternals = false
  MapMode = 5
  Placement = pos=(0,0.25,-1e-16) rot=(-1,0,0;1.5708rad)
  sketch-geometry (20):
    g0: LineSegment [constr] StartX=107.959 StartY=-54.95 StartZ=0 EndX=117.409 EndY=-54.95 EndZ=0
    g1: LineSegment [constr] StartX=107.959 StartY=-44.45 StartZ=0 EndX=117.409 EndY=-44.45 EndZ=0
    g2: LineSegment [constr] StartX=102.709 StartY=-49.7 StartZ=0 EndX=117.409 EndY=-49.7 EndZ=0
    g3: LineSegment [constr] StartX=117.409 StartY=-44.45 StartZ=0 EndX=117.409 EndY=-54.95 EndZ=0
    g4: ArcOfCircle [constr] CenterX=107.959 CenterY=-49.7 CenterZ=0 NormalX=0 NormalY=0 NormalZ=1 AngleXU=0 Radius=5.25 StartAngle=1.5708 EndAngle=4.71239
    g5: LineSegment [constr] StartX=117.409 StartY=-44.45 StartZ=0 EndX=127.009 EndY=-44.45 EndZ=0
    g6: LineSegment [constr] StartX=117.409 StartY=-44.45 StartZ=0 EndX=117.909 EndY=-44.45 EndZ=0
    g7: LineSegment [constr] StartX=117.909 StartY=-44.45 StartZ=0 EndX=117.909 EndY=-43.95 EndZ=0
    g8: LineSegment [constr] StartX=117.909 StartY=-43.95 StartZ=0 EndX=117.409 EndY=-43.95 EndZ=0
    g9: LineSegment [constr] StartX=117.409 StartY=-43.95 StartZ=0 EndX=117.409 EndY=-44.45 EndZ=0
    g10: LineSegment [constr] StartX=102.709 StartY=-49.7 StartZ=0 EndX=102.209 EndY=-49.7 EndZ=0
    g11: LineSegment StartX=117.909 StartY=-43.95 StartZ=0 EndX=117.909 EndY=-55.45 EndZ=0
    g12: LineSegment StartX=117.909 StartY=-55.45 StartZ=0 EndX=107.959 EndY=-55.45 EndZ=0
    g13: LineSegment StartX=117.909 StartY=-43.95 StartZ=0 EndX=107.959 EndY=-43.95 EndZ=0
    g14: ArcOfCircle CenterX=107.959 CenterY=-49.7 CenterZ=0 NormalX=0 NormalY=0 NormalZ=1 AngleXU=0 Radius=5.75 StartAngle=1.5708 EndAngle=4.71239
    g15: LineSegment [constr] StartX=117.409 StartY=-54.95 StartZ=0 EndX=117.409 EndY=-55.45 EndZ=0
    g16: LineSegment [constr] StartX=117.409 StartY=-55.45 StartZ=0 EndX=117.909 EndY=-55.45 EndZ=0
    g17: LineSegment [constr] StartX=117.909 StartY=-55.45 StartZ=0 EndX=117.909 EndY=-54.95 EndZ=0
    g18: LineSegment [constr] StartX=117.909 StartY=-54.95 StartZ=0 EndX=117.409 EndY=-54.95 EndZ=0
    g19: LineSegment [constr] StartX=117.409 StartY=-54.95 StartZ=0 EndX=117.409 EndY=-61.75 EndZ=0
  constraints (54):
    c: Horizontal(g0)
    c: Horizontal(g1)
    c: Distance(g2) = 14.7
    c: Coincident(g3,g1)
    c: Symmetric(g1,g0,g2)
    c: PointOnObject(g2,g4)
    c: Tangent(g4,g1) = 1.5708
    c: Tangent(g4,g0) = -1.5708
    c: Perpendicular(g4,g2)
    c: Vertical(g3)
    c: Distance(g3) = 10.5
    c: Coincident(g5,g1)
    c: PointOnObject(g5,g-4)
    c: Horizontal(g5)
    c: Distance(g5) = 9.6
    c: Coincident(g6,g7)
    c: Coincident(g7,g8)
    c: Coincident(g8,g9)
    c: Coincident(g9,g6)
    c: Horizontal(g6)
    c: Horizontal(g8)
    c: Vertical(g7)
    c: Vertical(g9)
    c: Coincident(g6,g1)
    c: Equal(g8,g7)
    c: Coincident(g10,g2)
    c: Horizontal(g10)
    c: Equal(g8,g10)
    c: Coincident(g11,g7)
    c: Horizontal(g12)
    c: Coincident(g13,g7)
    c: Horizontal(g13)
    c: PointOnObject(g10,g14)
    c: Tangent(g14,g13) = -1.5708
    c: Tangent(g14,g12) = 1.5708
    c: Distance(g10) = 0.5
    c: Coincident(g12,g11)
    c: Coincident(g15,g16)
    c: Coincident(g16,g17)
    c: Coincident(g17,g18)
    c: Coincident(g18,g15)
    c: Vertical(g15)
    c: Vertical(g17)
    c: Horizontal(g16)
    c: Horizontal(g18)
    c: Coincident(g15,g0)
    c: Coincident(g16,g11)
    c: Equal(g9,g18)
    c: Equal(g18,g15)
    c: Coincident(g19,g3)
    c: PointOnObject(g19,g-3)
    c: Vertical(g19)
    c: Distance(g19) = 6.8
    c: Coincident(g3,g0)
FEATURE [PartDesign::Pocket] Pocket007
  BaseFeature = -> Pocket006
  Direction = (0,-1,-2e-16)
  Length = 5
  Length2 = 5
  Placement = pos=(0,0,0) rot=(1,0,0;1.5708rad)
  Profile = -> Sketch013
  ReferenceAxis = -> Sketch013 [N_Axis]
  Refine = true
  Suppressed = false
  Type = 1
FEATURE [Sketcher::SketchObject] Sketch014
  ArcFitTolerance = 1e-06
  AttachmentSupport = -> [Pocket007]
  ExternalGeometry = -> [Pocket007]
  FullyConstrained = true
  MakeInternals = false
  MapMode = 5
  Placement = pos=(0,0.25,-1e-16) rot=(-1,0,0;1.5708rad)
  sketch-geometry (17):
    g0: ArcOfCircle CenterX=107.959 CenterY=-49.7 CenterZ=0 NormalX=0 NormalY=0 NormalZ=1 AngleXU=0 Radius=5.25 StartAngle=1.5708 EndAngle=4.71239
    g1: LineSegment StartX=107.959 StartY=-44.45 StartZ=0 EndX=117.409 EndY=-44.45 EndZ=0
    g2: LineSegment StartX=117.409 StartY=-44.45 StartZ=0 EndX=117.409 EndY=-54.95 EndZ=0
    g3: LineSegment StartX=117.409 StartY=-54.95 StartZ=0 EndX=107.959 EndY=-54.95 EndZ=0
    g4: LineSegment [constr] StartX=117.909 StartY=-43.95 StartZ=0 EndX=117.409 EndY=-43.95 EndZ=0
    g5: LineSegment [constr] StartX=117.409 StartY=-43.95 StartZ=0 EndX=117.409 EndY=-44.45 EndZ=0
    g6: LineSegment [constr] StartX=117.409 StartY=-44.45 StartZ=0 EndX=117.909 EndY=-44.45 EndZ=0
    g7: LineSegment [constr] StartX=117.909 StartY=-44.45 StartZ=0 EndX=117.909 EndY=-43.95 EndZ=0
    g8: LineSegment [constr] StartX=117.909 StartY=-55.45 StartZ=0 EndX=117.909 EndY=-54.95 EndZ=0
    g9: LineSegment [constr] StartX=117.909 StartY=-54.95 StartZ=0 EndX=117.409 EndY=-54.95 EndZ=0
    g10: LineSegment [constr] StartX=117.409 StartY=-54.95 StartZ=0 EndX=117.409 EndY=-55.45 EndZ=0
    g11: LineSegment [constr] StartX=117.409 StartY=-55.45 StartZ=0 EndX=117.909 EndY=-55.45 EndZ=0
    g12: LineSegment [constr] StartX=102.209 StartY=-49.7 StartZ=0 EndX=102.709 EndY=-49.7 EndZ=0
    g13: ArcOfCircle CenterX=107.959 CenterY=-49.7 CenterZ=0 NormalX=0 NormalY=0 NormalZ=1 AngleXU=0 Radius=5.75 StartAngle=1.5708 EndAngle=4.71239
    g14: LineSegment StartX=107.959 StartY=-43.95 StartZ=0 EndX=117.909 EndY=-43.95 EndZ=0
    g15: LineSegment StartX=117.909 StartY=-43.95 StartZ=0 EndX=117.909 EndY=-55.45 EndZ=0
    g16: LineSegment StartX=117.909 StartY=-55.45 StartZ=0 EndX=107.959 EndY=-55.45 EndZ=0
  constraints (44):
    c: Horizontal(g1)
    c: Coincident(g2,g1)
    c: Vertical(g2)
    c: Coincident(g3,g2)
    c: Horizontal(g3)
    c: Tangent(g1,g0) = 1.5708
    c: Tangent(g3,g0) = 1.5708
    c: Coincident(g4,g5)
    c: Coincident(g5,g6)
    c: Coincident(g6,g7)
    c: Coincident(g7,g4)
    c: Horizontal(g4)
    c: Horizontal(g6)
    c: Vertical(g5)
    c: Vertical(g7)
    c: Coincident(g4,g-3)
    c: Coincident(g5,g1)
    c: Coincident(g8,g9)
    c: Coincident(g9,g10)
    c: Coincident(g10,g11)
    c: Coincident(g11,g8)
    c: Vertical(g8)
    c: Vertical(g10)
    c: Horizontal(g9)
    c: Horizontal(g11)
    c: Coincident(g8,g-3)
    c: Coincident(g9,g2)
    c: Equal(g5,g6)
    c: Equal(g9,g10)
    c: PointOnObject(g12,g-4)
    c: PointOnObject(g12,g0)
    c: Horizontal(g12)
    c: Coincident(g13,g-4)
    c: Coincident(g13,g-4)
    c: PointOnObject(g12,g13)
    c: Coincident(g14,g13)
    c: Coincident(g14,g4)
    c: Equal(g12,g6)
    c: Coincident(g15,g4)
    c: Coincident(g15,g8)
    c: Coincident(g16,g8)
    c: Coincident(g16,g13)
    c: Distance(g12) = 0.5
    c: Perpendicular(g0,g12)
FEATURE [PartDesign::Pad] Pad007
  BaseFeature = -> Pocket007
  Direction = (0,1,2e-16)
  Length = 5.26
  Length2 = 10
  Placement = pos=(0,0,0) rot=(1,0,0;1.5708rad)
  Profile = -> Sketch014
  ReferenceAxis = -> Sketch014 [N_Axis]
  Refine = true
  Reversed = true
  Suppressed = false
  Type = 0
FEATURE [Sketcher::SketchObject] Sketch015
  ArcFitTolerance = 1e-06
  AttachmentSupport = -> [Pad007]
  ExternalGeometry = -> [Pad007]
  FullyConstrained = true
  MakeInternals = false
  MapMode = 5
  Placement = pos=(0,0.25,-1e-16) rot=(-1,0,0;1.5708rad)
  sketch-geometry (8):
    g0: LineSegment StartX=100.809 StartY=-42.45 StartZ=0 EndX=100.809 EndY=-56.95 EndZ=0
    g1: LineSegment StartX=100.809 StartY=-56.95 StartZ=0 EndX=119.309 EndY=-56.95 EndZ=0
    g2: LineSegment StartX=119.309 StartY=-56.95 StartZ=0 EndX=119.309 EndY=-42.45 EndZ=0
    g3: LineSegment StartX=119.309 StartY=-42.45 StartZ=0 EndX=100.809 EndY=-42.45 EndZ=0
    g4: LineSegment [constr] StartX=102.709 StartY=-49.7 StartZ=0 EndX=100.809 EndY=-49.7 EndZ=0
    g5: LineSegment [constr] StartX=117.409 StartY=-44.45 StartZ=0 EndX=117.409 EndY=-42.45 EndZ=0
    g6: LineSegment [constr] StartX=117.409 StartY=-54.95 StartZ=0 EndX=117.409 EndY=-56.95 EndZ=0
    g7: LineSegment [constr] StartX=117.409 StartY=-54.95 StartZ=0 EndX=119.309 EndY=-54.95 EndZ=0
  constraints (25):
    c: Coincident(g0,g1)
    c: Coincident(g1,g2)
    c: Coincident(g2,g3)
    c: Coincident(g3,g0)
    c: Vertical(g0)
    c: Vertical(g2)
    c: Horizontal(g1)
    c: Horizontal(g3)
    c: PointOnObject(g4,g-4)
    c: PointOnObject(g4,g0)
    c: Horizontal(g4)
    c: Coincident(g5,g-3)
    c: PointOnObject(g5,g3)
    c: Vertical(g5)
    c: Coincident(g6,g-3)
    c: PointOnObject(g6,g1)
    c: Vertical(g6)
    c: Coincident(g7,g6)
    c: PointOnObject(g7,g2)
    c: Horizontal(g7)
    c: Distance(g3) = 18.5
    c: Distance(g2) = 14.5
    c: Equal(g5,g6)
    c: Equal(g7,g4)
    c: Perpendicular(g-4,g4)
FEATURE [PartDesign::Pocket] Pocket008
  BaseFeature = -> Pad007
  Direction = (0,-1,-2e-16)
  Length = 4.5
  Length2 = 5
  Placement = pos=(0,0,0) rot=(1,0,0;1.5708rad)
  Profile = -> Sketch015
  ReferenceAxis = -> Sketch015 [N_Axis]
  Refine = true
  Suppressed = false
  Type = 0
FEATURE [Sketcher::SketchObject] Sketch016
  ArcFitTolerance = 1e-06
  AttachmentSupport = -> [Pocket008]
  ExternalGeometry = -> [Pocket008]
  FullyConstrained = true
  MakeInternals = false
  MapMode = 5
  Placement = pos=(0,0.25,-1e-16) rot=(-1,0,0;1.5708rad)
  sketch-geometry (12):
    g0: LineSegment StartX=46.875 StartY=-24.375 StartZ=0 EndX=46.875 EndY=-36.375 EndZ=0
    g1: LineSegment StartX=46.875 StartY=-36.375 StartZ=0 EndX=70.875 EndY=-36.375 EndZ=0
    g2: LineSegment StartX=70.875 StartY=-36.375 StartZ=0 EndX=70.875 EndY=-24.375 EndZ=0
    g3: LineSegment StartX=70.875 StartY=-24.375 StartZ=0 EndX=46.875 EndY=-24.375 EndZ=0
    g4: LineSegment [constr] StartX=47.4 StartY=-24.65 StartZ=0 EndX=47.4 EndY=-24.375 EndZ=0
    g5: LineSegment [constr] StartX=47.4 StartY=-24.375 StartZ=0 EndX=46.875 EndY=-24.375 EndZ=0
    g6: LineSegment [constr] StartX=46.875 StartY=-24.375 StartZ=0 EndX=46.875 EndY=-24.65 EndZ=0
    g7: LineSegment [constr] StartX=46.875 StartY=-24.65 StartZ=0 EndX=47.4 EndY=-24.65 EndZ=0
    g8: LineSegment [constr] StartX=70.35 StartY=-36.1 StartZ=0 EndX=70.35 EndY=-36.375 EndZ=0
    g9: LineSegment [constr] StartX=70.35 StartY=-36.375 StartZ=0 EndX=70.875 EndY=-36.375 EndZ=0
    g10: LineSegment [constr] StartX=70.875 StartY=-36.375 StartZ=0 EndX=70.875 EndY=-36.1 EndZ=0
    g11: LineSegment [constr] StartX=70.875 StartY=-36.1 StartZ=0 EndX=70.35 EndY=-36.1 EndZ=0
  constraints (32):
    c: Coincident(g0,g1)
    c: Coincident(g1,g2)
    c: Coincident(g2,g3)
    c: Coincident(g3,g0)
    c: Vertical(g0)
    c: Vertical(g2)
    c: Horizontal(g1)
    c: Horizontal(g3)
    c: Coincident(g4,g5)
    c: Coincident(g5,g6)
    c: Coincident(g6,g7)
    c: Coincident(g7,g4)
    c: Vertical(g4)
    c: Vertical(g6)
    c: Horizontal(g5)
    c: Horizontal(g7)
    c: Coincident(g4,g-3)
    c: Coincident(g5,g0)
    c: Coincident(g8,g9)
    c: Coincident(g9,g10)
    c: Coincident(g10,g11)
    c: Coincident(g11,g8)
    c: Vertical(g8)
    c: Vertical(g10)
    c: Horizontal(g9)
    c: Horizontal(g11)
    c: Coincident(g8,g-4)
    c: Coincident(g9,g1)
    c: Equal(g8,g4)
    c: Equal(g7,g11)
    c: Distance(g2) = 12
    c: Distance(g1) = 24
FEATURE [PartDesign::Pocket] Pocket009
  BaseFeature = -> Pocket008
  Direction = (0,-1,-2e-16)
  Length = 5
  Length2 = 5
  Placement = pos=(0,0,0) rot=(1,0,0;1.5708rad)
  Profile = -> Sketch016
  ReferenceAxis = -> Sketch016 [N_Axis]
  Refine = true
  Suppressed = false
  Type = 1
FEATURE [Sketcher::SketchObject] Sketch017
  ArcFitTolerance = 1e-06
  AttachmentSupport = -> [Pocket009]
  FullyConstrained = true
  MakeInternals = false
  MapMode = 5
  Placement = pos=(0,-1.65,4e-16) rot=(1,0,0;1.5708rad)
  sketch-geometry (6):
    g0: LineSegment StartX=100.8 StartY=7.75 StartZ=0 EndX=104.2 EndY=7.75 EndZ=0
    g1: LineSegment StartX=104.2 StartY=7.75 StartZ=0 EndX=104.2 EndY=18.75 EndZ=0
    g2: LineSegment StartX=104.2 StartY=18.75 StartZ=0 EndX=100.8 EndY=18.75 EndZ=0
    g3: LineSegment StartX=100.8 StartY=18.75 StartZ=0 EndX=100.8 EndY=7.75 EndZ=0
    g4: LineSegment [constr] StartX=104.2 StartY=18.75 StartZ=0 EndX=112.3 EndY=18.75 EndZ=0
    g5: LineSegment [constr] StartX=100.8 StartY=7.75 StartZ=0 EndX=100.8 EndY=5.5 EndZ=0
  constraints (18):
    c: Coincident(g0,g1)
    c: Coincident(g1,g2)
    c: Coincident(g2,g3)
    c: Coincident(g3,g0)
    c: Horizontal(g0)
    c: Horizontal(g2)
    c: Vertical(g1)
    c: Vertical(g3)
    c: Coincident(g4,g1)
    c: PointOnObject(g4,g-4)
    c: Horizontal(g4)
    c: Coincident(g5,g0)
    c: PointOnObject(g5,g-3)
    c: Vertical(g5)
    c: Distance(g2,g5) = 13.25
    c: Distance(g2,g4) = 11.5
    c: Distance(g2) = 3.4
    c: Distance(g1) = 11
FEATURE [PartDesign::Pocket] Pocket010
  BaseFeature = -> Pocket009
  Direction = (0,1,-2e-16)
  Length = 5
  Length2 = 5
  Placement = pos=(0,0,0) rot=(1,0,0;1.5708rad)
  Profile = -> Sketch017
  ReferenceAxis = -> Sketch017 [N_Axis]
  Refine = true
  Suppressed = false
  Type = 1
FEATURE [PartDesign::LinearPattern] LinearPattern
  BaseFeature = -> Pocket010
  Direction = -> Sketch017 [H_Axis]
  Length = 57.4
  Mode = 0
  Occurrences = 10
  Offset = 6.37778
  Originals = -> [Pocket010]
  Placement = pos=(0,0,0) rot=(1,0,0;1.5708rad)
  Refine = true
  Reversed = true
  Suppressed = false
  TransformMode = 0
FEATURE [Sketcher::SketchObject] Sketch018
  ArcFitTolerance = 1e-06
  AttachmentSupport = -> [LinearPattern]
  ExternalGeometry = -> [LinearPattern]
  FullyConstrained = true
  MakeInternals = false
  MapMode = 5
  Placement = pos=(0,0.25,-1e-16) rot=(-1,0,0;1.5708rad)
  sketch-geometry (5):
    g0: LineSegment [constr] StartX=70.875 StartY=-36.375 StartZ=0 EndX=79.275 EndY=-36.375 EndZ=0
    g1: LineSegment StartX=79.275 StartY=-36.375 StartZ=0 EndX=103.275 EndY=-36.375 EndZ=0
    g2: LineSegment StartX=103.275 StartY=-36.375 StartZ=0 EndX=103.275 EndY=-24.375 EndZ=0
    g3: LineSegment StartX=103.275 StartY=-24.375 StartZ=0 EndX=79.275 EndY=-24.375 EndZ=0
    g4: LineSegment StartX=79.275 StartY=-24.375 StartZ=0 EndX=79.275 EndY=-36.375 EndZ=0
  constraints (14):
    c: Coincident(g0,g-3)
    c: Horizontal(g0)
    c: Distance(g0) = 8.4
    c: Coincident(g1,g2)
    c: Coincident(g2,g3)
    c: Coincident(g3,g4)
    c: Coincident(g4,g1)
    c: Horizontal(g1)
    c: Horizontal(g3)
    c: Vertical(g2)
    c: Vertical(g4)
    c: Coincident(g1,g0)
    c: Equal(g4,g-3)
    c: Equal(g3,g-4)
FEATURE [PartDesign::Pocket] Pocket011
  BaseFeature = -> LinearPattern
  Direction = (0,-1,-2e-16)
  Length = 5
  Length2 = 5
  Placement = pos=(0,0,0) rot=(1,0,0;1.5708rad)
  Profile = -> Sketch018
  ReferenceAxis = -> Sketch018 [N_Axis]
  Refine = true
  Suppressed = false
  Type = 1
FEATURE [Sketcher::SketchObject] Sketch019
  ArcFitTolerance = 1e-06
  AttachmentSupport = -> [Pocket011]
  ExternalGeometry = -> [Pocket011]
  FullyConstrained = true
  MakeInternals = false
  MapMode = 5
  Placement = pos=(0,0,61.75) rot=(0,0,1;3.14159rad)
  sketch-geometry (11):
    g0: LineSegment StartX=-128.875 StartY=-0.25 StartZ=0 EndX=-128.875 EndY=-12.25 EndZ=0
    g1: LineSegment StartX=-128.875 StartY=-12.25 StartZ=0 EndX=-121.701 EndY=-12.25 EndZ=0
    g2: LineSegment StartX=-121.701 StartY=-12.25 StartZ=0 EndX=-121.701 EndY=-0.25 EndZ=0
    g3: LineSegment StartX=-121.701 StartY=-0.25 StartZ=0 EndX=-128.875 EndY=-0.25 EndZ=0
    g4: LineSegment StartX=4.125 StartY=-0.25 StartZ=0 EndX=-3.04877 EndY=-0.25 EndZ=0
    g5: LineSegment StartX=-3.04877 StartY=-0.25 StartZ=0 EndX=-3.04877 EndY=-12.25 EndZ=0
    g6: LineSegment StartX=-3.04877 StartY=-12.25 StartZ=0 EndX=4.125 EndY=-12.25 EndZ=0
    g7: LineSegment StartX=4.125 StartY=-12.25 StartZ=0 EndX=4.125 EndY=-0.25 EndZ=0
    g8: LineSegment [constr] StartX=-121.701 StartY=-12.25 StartZ=0 EndX=-3.04877 EndY=-12.25 EndZ=0
    g9: LineSegment [constr] StartX=-128.875 StartY=7.13851 StartZ=0 EndX=-121.701 EndY=-0.25 EndZ=0
    g10: LineSegment [constr] StartX=-3.04877 StartY=-0.25 StartZ=0 EndX=4.125 EndY=7.13851 EndZ=0
  constraints (30):
    c: Coincident(g0,g1)
    c: Coincident(g1,g2)
    c: Coincident(g2,g3)
    c: Vertical(g0)
    c: Vertical(g2)
    c: Horizontal(g1)
    c: Horizontal(g3)
    c: Coincident(g4,g5)
    c: Coincident(g5,g6)
    c: Coincident(g6,g7)
    c: Horizontal(g4)
    c: Horizontal(g6)
    c: Vertical(g5)
    c: Vertical(g7)
    c: Coincident(g8,g1)
    c: Coincident(g8,g5)
    c: Horizontal(g8)
    c: Distance(g2) = 12
    c: Distance(g-8,g2) = 72
    c: Coincident(g9,g-4)
    c: Coincident(g9,g2)
    c: Coincident(g10,g4)
    c: Coincident(g10,g-5)
    c: Equal(g9,g10)
    c: Coincident(g4,g7)
    c: PointOnObject(g4,g-5)
    c: PointOnObject(g4,g-3)
    c: Coincident(g3,g0)
    c: PointOnObject(g0,g-4)
    c: PointOnObject(g-6,g3)
FEATURE [PartDesign::Pad] Pad008
  BaseFeature = -> Pocket011
  Direction = (0,0,1)
  Length = 24.5
  Length2 = -18
  Placement = pos=(0,0,0) rot=(1,0,0;1.5708rad)
  Profile = -> Sketch019
  ReferenceAxis = -> Sketch019 [N_Axis]
  Refine = true
  Reversed = true
  Suppressed = false
  Type = 4
FEATURE [PartDesign::ShapeBinder] ShapeBinder
  Support = -> [Pad008]
  TraceSupport = false
FEATURE [PartDesign::Pocket] Pocket012
  BaseFeature = -> Pad008
  Direction = (0,1,0)
  Length = 5
  Length2 = 5
  Placement = pos=(0,0,0) rot=(1,0,0;1.5708rad)
  Profile = -> ShapeBinder
  Refine = true
  Suppressed = false
  Type = 1
FEATURE [Sketcher::SketchObject] Sketch020
  ArcFitTolerance = 1e-06
  AttachmentSupport = -> [Pocket012]
  ExternalGeometry = -> [Pocket012]
  FullyConstrained = true
  MakeInternals = false
  MapMode = 5
  Placement = pos=(0,0,43.75) rot=(0,0,1;3.14159rad)
  sketch-geometry (21):
    g0: LineSegment [constr] StartX=-126.551 StartY=-12.25 StartZ=0 EndX=-126.551 EndY=-5 EndZ=0
    g1: ArcOfCircle CenterX=-126.551 CenterY=-8 CenterZ=0 NormalX=0 NormalY=0 NormalZ=1 AngleXU=0 Radius=3 StartAngle=-3.6e-15 EndAngle=2.83362
    g2: LineSegment [constr] StartX=-123.551 StartY=-8 StartZ=0 EndX=-121.701 EndY=-8 EndZ=0
    g3: LineSegment [constr] StartX=-121.701 StartY=-12.25 StartZ=0 EndX=-123.551 EndY=-12.25 EndZ=0
    g4: LineSegment [constr] StartX=-123.551 StartY=-8 StartZ=0 EndX=-123.551 EndY=-12.25 EndZ=0
    g5: LineSegment [constr] StartX=-123.551 StartY=-12.25 StartZ=0 EndX=-131.051 EndY=-12.25 EndZ=0
    g6: LineSegment StartX=-131.051 StartY=-12.25 StartZ=0 EndX=-129.41 EndY=-7.09063 EndZ=0
    g7: LineSegment [constr] StartX=-121.701 StartY=-8 StartZ=0 EndX=-3.04877 EndY=-8 EndZ=0
    g8: LineSegment [constr] StartX=-3.04877 StartY=-12.25 StartZ=0 EndX=-1.19877 EndY=-12.25 EndZ=0
    g9: LineSegment [constr] StartX=-3.04877 StartY=-8 StartZ=0 EndX=-1.19877 EndY=-8 EndZ=0
    g10: LineSegment [constr] StartX=-126.551 StartY=-5 StartZ=0 EndX=1.80124 EndY=-5 EndZ=0
    g11: LineSegment [constr] StartX=-1.19877 StartY=-12.25 StartZ=0 EndX=6.30123 EndY=-12.25 EndZ=0
    g12: ArcOfCircle CenterX=1.80124 CenterY=-8.00001 CenterZ=0 NormalX=0 NormalY=0 NormalZ=1 AngleXU=0 Radius=3.00001 StartAngle=0.307967 EndAngle=3.14159
    g13: LineSegment [constr] StartX=-1.19877 StartY=-8 StartZ=0 EndX=-1.19877 EndY=-12.25 EndZ=0
    g14: LineSegment StartX=4.6601 StartY=-7.09064 StartZ=0 EndX=6.30123 EndY=-12.25 EndZ=0
    g15: ArcOfCircle CenterX=-126.551 CenterY=-8 CenterZ=0 NormalX=0 NormalY=0 NormalZ=1 AngleXU=0 Radius=3 StartAngle=5.49952 EndAngle=6.28319
    g16: LineSegment StartX=-124.426 StartY=-10.1176 StartZ=0 EndX=-126.551 EndY=-12.25 EndZ=0
    g17: LineSegment StartX=-126.551 StartY=-12.25 StartZ=0 EndX=-131.051 EndY=-12.25 EndZ=0
    g18: ArcOfCircle CenterX=1.80124 CenterY=-8.00001 CenterZ=0 NormalX=0 NormalY=0 NormalZ=1 AngleXU=0 Radius=3.00001 StartAngle=3.14159 EndAngle=3.92526
    g19: LineSegment StartX=-0.323748 StartY=-10.1177 StartZ=0 EndX=1.80123 EndY=-12.25 EndZ=0
    g20: LineSegment StartX=1.80123 StartY=-12.25 StartZ=0 EndX=6.30123 EndY=-12.25 EndZ=0
  constraints (54):
    c: PointOnObject(g0,g-3)
    c: Vertical(g0)
    c: Distance(g0) = 7.25
    c: PointOnObject(g0,g1)
    c: Perpendicular(g1,g0)
    c: Coincident(g2,g1)
    c: PointOnObject(g2,g-4)
    c: Horizontal(g2)
    c: Distance(g2) = 1.85
    c: Coincident(g3,g-4)
    c: PointOnObject(g3,g-3)
    c: Distance(g3) = 1.85
    c: Coincident(g4,g3)
    c: Tangent(g4,g1) = 1.5708
    c: Coincident(g5,g3)
    c: Horizontal(g5)
    c: Distance(g5) = 7.5
    c: Coincident(g6,g5)
    c: Tangent(g6,g1) = 1.5708
    c: Diameter(g1) = 6
    c: Coincident(g7,g2)
    c: PointOnObject(g7,g-5)
    c: Horizontal(g7)
    c: Coincident(g8,g-6)
    c: PointOnObject(g8,g-6)
    c: Coincident(g9,g7)
    c: Horizontal(g9)
    c: Equal(g9,g2)
    c: Equal(g3,g8)
    c: Coincident(g10,g0)
    c: Horizontal(g10)
    c: Equal(g11,g5)
    c: Coincident(g12,g9)
    c: Tangent(g10,g12) = 1.5708
    c: Coincident(g13,g9)
    c: Coincident(g13,g11)
    c: Coincident(g11,g8)
    c: Tangent(g12,g13)
    c: Coincident(g14,g11)
    c: Horizontal(g11)
    c: Tangent(g12,g14) = 1.5708
    c: Coincident(g15,g1)
    c: Coincident(g15,g1)
    c: Coincident(g17,g5)
    c: Coincident(g18,g12)
    c: Coincident(g18,g9)
    c: Coincident(g20,g11)
    c: Tangent(g16,g15) = 1.5708
    c: Coincident(g16,g0)
    c: Coincident(g17,g0)
    c: Equal(g20,g17)
    c: Tangent(g18,g19) = -1.5708
    c: Coincident(g19,g20)
    c: Horizontal(g20)
FEATURE [PartDesign::Pocket] Pocket013
  BaseFeature = -> Pocket012
  Direction = (0,0,-1)
  Length = 5
  Length2 = 5
  Placement = pos=(0,0,0) rot=(1,0,0;1.5708rad)
  Profile = -> Sketch020
  ReferenceAxis = -> Sketch020 [N_Axis]
  Refine = true
  Suppressed = false
  Type = 1
FEATURE [PartDesign::Chamfer] Chamfer
  Angle = 45
  Base = -> Pocket013 [Edge225,Edge224,Edge226,Edge227,Edge166,Edge163,Edge168,Edge170,Edge122,Edge120,Edge115,Edge118]
  BaseFeature = -> Pocket013
  ChamferType = 0
  FlipDirection = false
  Placement = pos=(0,0,0) rot=(1,0,0;1.5708rad)
  Refine = true
  Size = 1
  Size2 = 1
  SupportTransform = false
  Suppressed = false
  UseAllEdges = false
FEATURE [PartDesign::Fillet] Fillet
  Base = -> Chamfer [Edge175,Edge159,Edge394,Edge432,Edge246,Edge316]
  BaseFeature = -> Chamfer
  Placement = pos=(0,0,0) rot=(1,0,0;1.5708rad)
  Radius = 1
  Refine = true
  SupportTransform = false
  Suppressed = false
  UseAllEdges = false
FEATURE [PartDesign::Body] Body  label="GameCube IO DOL-001"
  AllowCompound = false
  Group = -> [Sketch,Pad,Sketch001,Pocket,Sketch002,Pad001,Pad002,Sketch003,Pocket001,Sketch004,Pocket002,Sketch005,Pad003,Sketch006,Pocket003,Sketch007,Pad004,Sketch008,Pocket004,Sketch009,Pad005,Sketch010,Pocket005,Sketch011,Pad006,Sketch012,Pocket006,Sketch013,Pocket007,Sketch014,Pad007,Sketch015,Pocket008,Sketch016,Pocket009,Sketch017,Pocket010,LinearPattern,Sketch018,Pocket011,Sketch019,Pad008,ShapeBinder,+5 more]
  Origin = -> Origin
  Tip = -> Fillet
FEATURE [PartDesign::FeatureBase] Clone
  BaseFeature = -> Body
  Suppressed = false
FEATURE [Sketcher::SketchObject] Sketch021
  ArcFitTolerance = 1e-06
  AttachmentSupport = -> [Clone]
  ExternalGeometry = -> [Clone]
  FullyConstrained = true
  MakeInternals = false
  MapMode = 5
  Placement = pos=(0,0.25,-1e-16) rot=(0,0.707107,0.707107;3.14159rad)
  sketch-geometry (4):
    g0: LineSegment StartX=-104.275 StartY=23.375 StartZ=0 EndX=-104.275 EndY=37.375 EndZ=0
    g1: LineSegment StartX=-104.275 StartY=37.375 StartZ=0 EndX=-78.275 EndY=37.375 EndZ=0
    g2: LineSegment StartX=-78.275 StartY=37.375 StartZ=0 EndX=-78.275 EndY=23.375 EndZ=0
    g3: LineSegment StartX=-78.275 StartY=23.375 StartZ=0 EndX=-104.275 EndY=23.375 EndZ=0
  constraints (10):
    c: Coincident(g0,g1)
    c: Coincident(g1,g2)
    c: Coincident(g2,g3)
    c: Coincident(g3,g0)
    c: Vertical(g0)
    c: Vertical(g2)
    c: Horizontal(g1)
    c: Horizontal(g3)
    c: Coincident(g0,g-3)
    c: Coincident(g1,g-4)
FEATURE [PartDesign::Pad] Pad009
  BaseFeature = -> Clone
  Direction = (0,1,-2e-16)
  Length = 10
  Length2 = 10
  Profile = -> Sketch021
  ReferenceAxis = -> Sketch021 [N_Axis]
  Refine = true
  Suppressed = false
  Type = 3
  UpToFace = -> Clone [Face4]
FEATURE [PartDesign::Body] Body001  label="GameCube IO DOL-101"
  AllowCompound = false
  Group = -> [Clone,Sketch021,Pad009]
  Origin = -> Origin001
  Tip = -> Pad009
FEATURE [PartDesign::FeatureBase] Clone001
  BaseFeature = -> Body
  Suppressed = false
FEATURE [Sketcher::SketchObject] Sketch022
  ArcFitTolerance = 1e-06
  AttachmentSupport = -> [Clone001]
  ExternalGeometry = -> [Clone001]
  FullyConstrained = true
  MakeInternals = false
  MapMode = 5
  Placement = pos=(0,-1.65,0) rot=(1,0,0;1.5708rad)
  sketch-geometry (16):
    g0: LineSegment StartX=11.45 StartY=42.8223 StartZ=0 EndX=11.45 EndY=4.48148 EndZ=0
    g1: LineSegment StartX=11.45 StartY=4.48148 StartZ=0 EndX=113.3 EndY=4.48148 EndZ=0
    g2: LineSegment StartX=113.3 StartY=4.48148 StartZ=0 EndX=113.3 EndY=42.8223 EndZ=0
    g3: LineSegment StartX=113.3 StartY=42.8223 StartZ=0 EndX=11.45 EndY=42.8223 EndZ=0
    g4: LineSegment [constr] StartX=36.875 StartY=41.75 StartZ=0 EndX=36.875 EndY=5.5 EndZ=0
    g5: LineSegment [constr] StartX=36.875 StartY=5.5 StartZ=0 EndX=105.8 EndY=5.5 EndZ=0
    g6: LineSegment [constr] StartX=105.8 StartY=41.75 StartZ=0 EndX=36.875 EndY=41.75 EndZ=0
    g7: LineSegment [constr] StartX=46.875 StartY=36.375 StartZ=0 EndX=36.875 EndY=36.375 EndZ=0
    g8: ArcOfCircle CenterX=105.8 CenterY=35.25 CenterZ=0 NormalX=0 NormalY=0 NormalZ=1 AngleXU=0 Radius=6.5 StartAngle=9.7762e-12 EndAngle=1.5708
    g9: ArcOfCircle CenterX=105.8 CenterY=12 CenterZ=0 NormalX=0 NormalY=0 NormalZ=1 AngleXU=0 Radius=6.5 StartAngle=4.71239 EndAngle=6.28319
    g10: LineSegment StartX=112.3 StartY=35.25 StartZ=0 EndX=112.3 EndY=12 EndZ=0
    g11: ArcOfCircle CenterX=43.375 CenterY=35.25 CenterZ=0 NormalX=0 NormalY=0 NormalZ=1 AngleXU=0 Radius=6.5 StartAngle=1.5708 EndAngle=3.14159
    g12: ArcOfCircle CenterX=43.375 CenterY=12 CenterZ=0 NormalX=0 NormalY=0 NormalZ=1 AngleXU=0 Radius=6.5 StartAngle=3.14159 EndAngle=4.71239
    g13: LineSegment StartX=43.375 StartY=5.5 StartZ=0 EndX=105.8 EndY=5.5 EndZ=0
    g14: LineSegment StartX=36.875 StartY=12 StartZ=0 EndX=36.875 EndY=35.25 EndZ=0
    g15: LineSegment StartX=43.375 StartY=41.75 StartZ=0 EndX=105.8 EndY=41.75 EndZ=0
  constraints (41):
    c: Coincident(g0,g1)
    c: Coincident(g1,g2)
    c: Coincident(g2,g3)
    c: Coincident(g3,g0)
    c: Vertical(g0)
    c: Vertical(g2)
    c: Horizontal(g1)
    c: Horizontal(g3)
    c: Coincident(g4,g5)
    c: Coincident(g6,g4)
    c: Vertical(g4)
    c: Horizontal(g5)
    c: PointOnObject(g-5,g3)
    c: PointOnObject(g-3,g0)
    c: PointOnObject(g-6,g1)
    c: PointOnObject(g4,g-7)
    c: Coincident(g7,g-10)
    c: PointOnObject(g7,g4)
    c: Horizontal(g7)
    c: Distance(g7,g7) = 10
    c: Coincident(g-7,g6)
    c: Coincident(g5,g-8)
    c: PointOnObject(g-4,g2)
    c: Coincident(g8,g-9) = -1.5708
    c: Coincident(g10,g8)
    c: Vertical(g10)
    c: Tangent(g10,g9) = 1.5708
    c: Tangent(g9,g5) = -1.5708
    c: Tangent(g8,g6) = -1.5708
    c: Equal(g11,g8)
    c: Equal(g9,g12)
    c: Tangent(g11,g6) = -1.5708
    c: Tangent(g12,g4) = -1.5708
    c: Tangent(g12,g5) = -1.5708
    c: Coincident(g13,g12)
    c: Coincident(g13,g5)
    c: Coincident(g14,g12)
    c: Tangent(g14,g11) = 1.5708
    c: Vertical(g14)
    c: Coincident(g11,g15)
    c: Coincident(g15,g6)
FEATURE [PartDesign::Pad] Pad010
  BaseFeature = -> Clone001
  Direction = (0,-1,2e-16)
  Length = 10
  Length2 = 10
  Profile = -> Sketch022
  ReferenceAxis = -> Sketch022 [N_Axis]
  Refine = true
  Suppressed = false
  Type = 0
FEATURE [PartDesign::Pocket] Pocket014
  BaseFeature = -> Pad010
  Direction = (1,0,0)
  Length = 5
  Length2 = 5
  Profile = -> Pad010 [Face54]
  Refine = true
  Suppressed = false
  Type = 1
FEATURE [PartDesign::Pocket] Pocket015
  BaseFeature = -> Pocket014
  Direction = (0,-2e-16,-1)
  Length = 0
  Length2 = 5
  Profile = -> Pocket014 [Face158]
  Refine = true
  Suppressed = false
  Type = 3
  UpToFace = -> Pocket014 [Face124]
FEATURE [Sketcher::SketchObject] Sketch023
  ArcFitTolerance = 1e-06
  AttachmentSupport = -> [Pocket015]
  FullyConstrained = true
  MakeInternals = false
  MapMode = 5
  Placement = pos=(0,0.25,-1e-16) rot=(0,0.707107,0.707107;3.14159rad)
  sketch-geometry (9):
    g0: LineSegment [constr] StartX=-46.875 StartY=24.375 StartZ=0 EndX=-46.875 EndY=23.375 EndZ=0
    g1: LineSegment [constr] StartX=-36.875 StartY=23.375 StartZ=0 EndX=-36.075 EndY=23.375 EndZ=0
    g2: LineSegment [constr] StartX=-36.075 StartY=23.375 StartZ=0 EndX=-36.075 EndY=8.375 EndZ=0
    g3: GeomPoint [constr] X=-36.075 Y=15.875 Z=0
    g4: LineSegment StartX=-36.075 StartY=30.125 StartZ=0 EndX=-36.075 EndY=1.625 EndZ=0
    g5: LineSegment StartX=-36.075 StartY=1.625 StartZ=0 EndX=-3.075 EndY=1.625 EndZ=0
    g6: LineSegment StartX=-3.075 StartY=1.625 StartZ=0 EndX=-3.075 EndY=30.125 EndZ=0
    g7: LineSegment StartX=-3.075 StartY=30.125 StartZ=0 EndX=-36.075 EndY=30.125 EndZ=0
    g8: LineSegment [constr] StartX=-46.875 StartY=23.375 StartZ=0 EndX=-36.875 EndY=23.375 EndZ=0
  constraints (24):
    c: Distance(g0) = 1
    c: Coincident(g0,g-4)
    c: Vertical(g0)
    c: Horizontal(g1)
    c: Coincident(g2,g1)
    c: Vertical(g2)
    c: DistanceY(g2,g2) = 15
    c: Symmetric(g1,g2,g3)
    c: Coincident(g4,g5)
    c: Coincident(g5,g6)
    c: Coincident(g6,g7)
    c: Coincident(g7,g4)
    c: Vertical(g4)
    c: Vertical(g6)
    c: Horizontal(g5)
    c: Horizontal(g7)
    c: DistanceY(g4,g4) = 28.5
    c: Symmetric(g4,g4,g3)
    c: DistanceX(g7,g7) = 33
    c: DistanceX(g1,g1) = 0.8
    c: PointOnObject(g1,g-3)
    c: Coincident(g8,g0)
    c: Coincident(g8,g1)
    c: Horizontal(g8)
FEATURE [PartDesign::Pocket] Pocket016
  BaseFeature = -> Pocket015
  Direction = (0,-1,2e-16)
  Length = 2.5
  Length2 = 5
  Profile = -> Sketch023
  ReferenceAxis = -> Sketch023 [N_Axis]
  Refine = true
  Suppressed = false
  Type = 0
FEATURE [Sketcher::SketchObject] Sketch024
  ArcFitTolerance = 1e-06
  AttachmentSupport = -> [Pocket016]
  ExternalGeometry = -> [Sketch023]
  FullyConstrained = true
  MakeInternals = false
  MapMode = 5
  Placement = pos=(0,-2.25,0) rot=(0,0.707107,0.707107;3.14159rad)
  sketch-geometry (5):
    g0: GeomPoint X=-36.075 Y=15.875 Z=0
    g1: LineSegment StartX=-36.075 StartY=23.625 StartZ=0 EndX=-36.075 EndY=8.125 EndZ=0
    g2: LineSegment StartX=-36.075 StartY=8.125 StartZ=0 EndX=-20.575 EndY=8.125 EndZ=0
    g3: LineSegment StartX=-20.575 StartY=8.125 StartZ=0 EndX=-20.575 EndY=23.625 EndZ=0
    g4: LineSegment StartX=-20.575 StartY=23.625 StartZ=0 EndX=-36.075 EndY=23.625 EndZ=0
  constraints (12):
    c: Symmetric(g-3,g-3,g0)
    c: Coincident(g1,g2)
    c: Coincident(g2,g3)
    c: Coincident(g3,g4)
    c: Coincident(g4,g1)
    c: Vertical(g1)
    c: Vertical(g3)
    c: Horizontal(g2)
    c: Horizontal(g4)
    c: Symmetric(g1,g1,g0)
    c: Distance(g1,g1) = 15.5
    c: Equal(g4,g1)
FEATURE [PartDesign::Pocket] Pocket017
  BaseFeature = -> Pocket016
  Direction = (0,-1,2e-16)
  Length = 2.5
  Length2 = 5
  Profile = -> Sketch024
  ReferenceAxis = -> Sketch024 [N_Axis]
  Refine = true
  Suppressed = false
  Type = 0
FEATURE [Sketcher::SketchObject] Sketch025
  ArcFitTolerance = 1e-06
  AttachmentSupport = -> [Pocket017]
  ExternalGeometry = -> [Pocket017]
  FullyConstrained = true
  MakeInternals = false
  MapMode = 5
  Placement = pos=(36.075,4.91e-14,0) rot=(0.57735,-0.57735,-0.57735;2.0944rad)
  sketch-geometry (4):
    g0: LineSegment StartX=2.25 StartY=23.625 StartZ=0 EndX=2.25 EndY=8.125 EndZ=0
    g1: LineSegment StartX=2.25 StartY=8.125 StartZ=0 EndX=4.75 EndY=8.125 EndZ=0
    g2: LineSegment StartX=4.75 StartY=8.125 StartZ=0 EndX=4.75 EndY=23.625 EndZ=0
    g3: LineSegment StartX=4.75 StartY=23.625 StartZ=0 EndX=2.25 EndY=23.625 EndZ=0
  constraints (10):
    c: Coincident(g0,g1)
    c: Coincident(g1,g2)
    c: Coincident(g2,g3)
    c: Coincident(g3,g0)
    c: Vertical(g0)
    c: Vertical(g2)
    c: Horizontal(g1)
    c: Horizontal(g3)
    c: Coincident(g0,g-4)
    c: Coincident(g1,g-3)
FEATURE [PartDesign::Pocket] Pocket018
  BaseFeature = -> Pocket017
  Direction = (1,1.3e-15,0)
  Length = 5
  Length2 = 5
  Profile = -> Sketch025
  ReferenceAxis = -> Sketch025 [N_Axis]
  Refine = true
  Suppressed = false
  Type = 0
FEATURE [Sketcher::SketchObject] Sketch026
  ArcFitTolerance = 1e-06
  AttachmentSupport = -> [Pocket018]
  ExternalGeometry = -> [Pocket018]
  FullyConstrained = true
  MakeInternals = false
  MapMode = 5
  Placement = pos=(0,0.25,-1e-16) rot=(0,0.707107,0.707107;3.14159rad)
  sketch-geometry (8):
    g0: GeomPoint X=-3.075 Y=15.875 Z=0
    g1: LineSegment StartX=-10.075 StartY=24.25 StartZ=0 EndX=-10.075 EndY=7.5 EndZ=0
    g2: LineSegment StartX=-10.075 StartY=7.5 StartZ=0 EndX=2.255 EndY=7.5 EndZ=0
    g3: LineSegment StartX=2.255 StartY=7.5 StartZ=0 EndX=2.255 EndY=24.25 EndZ=0
    g4: LineSegment StartX=2.255 StartY=24.25 StartZ=0 EndX=-10.075 EndY=24.25 EndZ=0
    g5: LineSegment [constr] StartX=-3.075 StartY=24.25 StartZ=0 EndX=-3.075 EndY=7.5 EndZ=0
    g6: LineSegment [constr] StartX=-3.075 StartY=15.875 StartZ=0 EndX=-10.075 EndY=15.875 EndZ=0
    g7: LineSegment [constr] StartX=-3.075 StartY=15.875 StartZ=0 EndX=2.255 EndY=15.875 EndZ=0
  constraints (20):
    c: Symmetric(g-3,g-3,g0)
    c: Coincident(g1,g2)
    c: Coincident(g2,g3)
    c: Coincident(g3,g4)
    c: Coincident(g4,g1)
    c: Vertical(g1)
    c: Vertical(g3)
    c: Horizontal(g2)
    c: Horizontal(g4)
    c: PointOnObject(g5,g4)
    c: PointOnObject(g5,g2)
    c: Vertical(g5)
    c: Symmetric(g5,g5,g0)
    c: DistanceY(g1,g1) = 16.75
    c: Coincident(g6,g0)
    c: Symmetric(g1,g1,g6)
    c: DistanceX(g6,g6) = 7
    c: Coincident(g7,g0)
    c: Symmetric(g3,g3,g7)
    c: Distance(g7,g7) = 5.33
FEATURE [PartDesign::Pocket] Pocket019
  BaseFeature = -> Pocket018
  Direction = (0,-1,2e-16)
  Length = 0
  Length2 = 5
  Offset = 2
  Profile = -> Sketch026
  ReferenceAxis = -> Sketch026 [N_Axis]
  Refine = true
  Suppressed = false
  Type = 3
  UpToFace = -> Pocket018 [Face101]
FEATURE [Sketcher::SketchObject] Sketch027
  ArcFitTolerance = 1e-06
  AttachmentSupport = -> [Pocket019]
  ExternalGeometry = -> [Pocket019]
  FullyConstrained = true
  MakeInternals = false
  MapMode = 5
  Placement = pos=(0,-2.25,0) rot=(0,0.707107,0.707107;3.14159rad)
  sketch-geometry (4):
    g0: Circle CenterX=-30.075 CenterY=4.825 CenterZ=0 NormalX=0 NormalY=0 NormalZ=1 AngleXU=0 Radius=1.5
    g1: Circle CenterX=-30.075 CenterY=26.925 CenterZ=0 NormalX=0 NormalY=0 NormalZ=1 AngleXU=0 Radius=1.5
    g2: LineSegment [constr] StartX=-30.075 StartY=26.925 StartZ=0 EndX=-30.075 EndY=4.825 EndZ=0
    g3: LineSegment [constr] StartX=-30.075 StartY=15.875 StartZ=0 EndX=-36.075 EndY=15.875 EndZ=0
  constraints (10):
    c: Coincident(g2,g1)
    c: Coincident(g2,g0)
    c: Vertical(g2)
    c: Symmetric(g2,g2,g3)
    c: Horizontal(g3)
    c: Symmetric(g-3,g-4,g3)
    c: Distance(g3,g3) = 6
    c: DistanceY(g2,g2) = 22.1
    c: Diameter(g1) = 3
    c: Equal(g1,g0)
FEATURE [PartDesign::Pocket] Pocket020
  BaseFeature = -> Pocket019
  Direction = (0,-1,2e-16)
  Length = 4
  Length2 = 5
  Profile = -> Sketch027
  ReferenceAxis = -> Sketch027 [N_Axis]
  Refine = true
  Suppressed = false
  Type = 0
FEATURE [PartDesign::Chamfer] Chamfer001
  Angle = 45
  Base = -> Pocket020 [Edge279,Edge277]
  BaseFeature = -> Pocket020
  ChamferType = 0
  FlipDirection = false
  Refine = true
  Size = 2.49
  Size2 = 1
  SupportTransform = false
  Suppressed = false
  UseAllEdges = false
FEATURE [PartDesign::Fillet] Fillet001
  Base = -> Chamfer001 [Edge396]
  BaseFeature = -> Chamfer001
  Radius = 1
  Refine = true
  SupportTransform = false
  Suppressed = false
  UseAllEdges = false
FEATURE [PartDesign::Chamfer] Chamfer002
  Angle = 45
  Base = -> Chamfer001 [Edge20,Edge22,Edge24,Edge17,Edge18,Edge19]
  BaseFeature = -> Chamfer001
  ChamferType = 0
  FlipDirection = false
  Refine = true
  Size = 1.49
  Size2 = 1
  SupportTransform = false
  Suppressed = false
  UseAllEdges = false
FEATURE [Sketcher::SketchObject] Sketch029
  ArcFitTolerance = 1e-06
  AttachmentSupport = -> [Chamfer002]
  ExternalGeometry = -> [Chamfer002]
  FullyConstrained = true
  MakeInternals = false
  MapMode = 5
  Placement = pos=(0,-2.25,0) rot=(0,0.707107,0.707107;3.14159rad)
  sketch-geometry (24):
    g0: LineSegment StartX=-32.2392 StartY=27.425 StartZ=0 EndX=-32.2392 EndY=26.425 EndZ=0
    g1: LineSegment StartX=-32.2392 StartY=26.425 StartZ=0 EndX=-31.4892 EndY=26.425 EndZ=0
    g2: LineSegment StartX=-31.4892 StartY=26.425 StartZ=0 EndX=-31.4892 EndY=27.425 EndZ=0
    g3: LineSegment StartX=-31.4892 StartY=27.425 StartZ=0 EndX=-32.2392 EndY=27.425 EndZ=0
    g4: LineSegment StartX=-30.575 StartY=29.0892 StartZ=0 EndX=-30.575 EndY=28.3392 EndZ=0
    g5: LineSegment StartX=-30.575 StartY=28.3392 StartZ=0 EndX=-29.575 EndY=28.3392 EndZ=0
    g6: LineSegment StartX=-29.575 StartY=28.3392 StartZ=0 EndX=-29.575 EndY=29.0892 EndZ=0
    g7: LineSegment StartX=-29.575 StartY=29.0892 StartZ=0 EndX=-30.575 EndY=29.0892 EndZ=0
    g8: LineSegment StartX=-27.9108 StartY=27.425 StartZ=0 EndX=-28.6608 EndY=27.425 EndZ=0
    g9: LineSegment StartX=-28.6608 StartY=27.425 StartZ=0 EndX=-28.6608 EndY=26.425 EndZ=0
    g10: LineSegment StartX=-28.6608 StartY=26.425 StartZ=0 EndX=-27.9108 EndY=26.425 EndZ=0
    g11: LineSegment StartX=-27.9108 StartY=26.425 StartZ=0 EndX=-27.9108 EndY=27.425 EndZ=0
    g12: LineSegment StartX=-28.6608 StartY=5.325 StartZ=0 EndX=-28.6608 EndY=4.325 EndZ=0
    g13: LineSegment StartX=-28.6608 StartY=4.325 StartZ=0 EndX=-27.9108 EndY=4.325 EndZ=0
    g14: LineSegment StartX=-27.9108 StartY=4.325 StartZ=0 EndX=-27.9108 EndY=5.325 EndZ=0
    g15: LineSegment StartX=-27.9108 StartY=5.325 StartZ=0 EndX=-28.6608 EndY=5.325 EndZ=0
    g16: LineSegment StartX=-29.575 StartY=3.41079 StartZ=0 EndX=-30.575 EndY=3.41079 EndZ=0
    g17: LineSegment StartX=-30.575 StartY=3.41079 StartZ=0 EndX=-30.575 EndY=2.66079 EndZ=0
    g18: LineSegment StartX=-30.575 StartY=2.66079 StartZ=0 EndX=-29.575 EndY=2.66079 EndZ=0
    g19: LineSegment StartX=-29.575 StartY=2.66079 StartZ=0 EndX=-29.575 EndY=3.41079 EndZ=0
    g20: LineSegment StartX=-31.4892 StartY=4.325 StartZ=0 EndX=-31.4892 EndY=5.325 EndZ=0
    g21: LineSegment StartX=-31.4892 StartY=5.325 StartZ=0 EndX=-32.2392 EndY=5.325 EndZ=0
    g22: LineSegment StartX=-32.2392 StartY=5.325 StartZ=0 EndX=-32.2392 EndY=4.325 EndZ=0
    g23: LineSegment StartX=-32.2392 StartY=4.325 StartZ=0 EndX=-31.4892 EndY=4.325 EndZ=0
  constraints (72):
    c: Coincident(g0,g1)
    c: Coincident(g1,g2)
    c: Coincident(g2,g3)
    c: Coincident(g3,g0)
    c: Vertical(g0)
    c: Vertical(g2)
    c: Horizontal(g1)
    c: Horizontal(g3)
    c: PointOnObject(g1,g-3)
    c: Coincident(g4,g5)
    c: Coincident(g5,g6)
    c: Coincident(g6,g7)
    c: Coincident(g7,g4)
    c: Vertical(g4)
    c: Vertical(g6)
    c: Horizontal(g5)
    c: Horizontal(g7)
    c: PointOnObject(g5,g-3)
    c: Coincident(g8,g9)
    c: Coincident(g9,g10)
    c: Coincident(g10,g11)
    c: Coincident(g11,g8)
    c: Horizontal(g8)
    c: Horizontal(g10)
    c: Vertical(g9)
    c: Vertical(g11)
    c: PointOnObject(g9,g-3)
    c: PointOnObject(g8,g-3)
    c: PointOnObject(g2,g-3)
    c: PointOnObject(g4,g-3)
    c: Equal(g4,g3)
    c: Equal(g6,g8)
    c: Equal(g9,g5)
    c: Equal(g7,g2)
    c: Distance(g5,g5) = 1
    c: Distance(g3,g3) = 0.75
    c: Coincident(g12,g13)
    c: Coincident(g13,g14)
    c: Coincident(g14,g15)
    c: Coincident(g15,g12)
    c: Vertical(g12)
    c: Vertical(g14)
    c: Horizontal(g13)
    c: Horizontal(g15)
    c: PointOnObject(g12,g-4)
    c: Coincident(g16,g17)
    c: Coincident(g17,g18)
    c: Coincident(g18,g19)
    c: Coincident(g19,g16)
    c: Horizontal(g16)
    c: Horizontal(g18)
    c: Vertical(g17)
    c: Vertical(g19)
    c: PointOnObject(g16,g-4)
    c: Coincident(g20,g21)
    c: Coincident(g21,g22)
    c: Coincident(g22,g23)
    c: Coincident(g23,g20)
    c: Vertical(g20)
    c: Vertical(g22)
    c: Horizontal(g21)
    c: Horizontal(g23)
    c: PointOnObject(g20,g-4)
    c: PointOnObject(g20,g-4)
    c: PointOnObject(g12,g-4)
    c: PointOnObject(g16,g-4)
    c: Equal(g23,g17)
    c: Equal(g19,g13)
    c: Equal(g20,g16)
    c: Equal(g18,g12)
    c: Equal(g14,g11)
    c: Equal(g15,g10)
FEATURE [PartDesign::Pocket] Pocket021
  BaseFeature = -> Chamfer002
  Direction = (0,-1,2e-16)
  Length = 4
  Length2 = 5
  Profile = -> Sketch029
  ReferenceAxis = -> Sketch029 [N_Axis]
  Refine = true
  Suppressed = false
  Type = 0
FEATURE [Part::Part2DObjectPython] ShapeString  label="ANALOG"  # Draft 2D object (typed FeaturePython)
  FontFile = <userpath>/Documents/FreeCad/Font/Gidole-Regular.ttf
  Fuse = false
  Justification = 6
  JustificationReference = 0
  KeepLeftMargin = false
  MakeFace = true
  ObliqueAngle = 0
  Placement = pos=(81.15,-22,44.8) rot=(1,0,0;1.49836rad)
  ScaleToSize = true
  Size = 4
  String = ANALOG
  Tracking = 0
FEATURE [Part::Part2DObjectPython] ShapeString001  label="DIGITAL"  # Draft 2D object (typed FeaturePython)
  FontFile = <userpath>/Documents/FreeCad/Font/Gidole-Regular.ttf
  Fuse = false
  Justification = 6
  JustificationReference = 0
  KeepLeftMargin = false
  MakeFace = true
  ObliqueAngle = 0
  Placement = pos=(49.755,-22,44.8) rot=(1,0,0;1.49836rad)
  ScaleToSize = true
  Size = 4
  String = DIGITAL
  Tracking = 0
FEATURE [Part::Part2DObjectPython] ShapeString002  label="DC"  # Draft 2D object (typed FeaturePython)
  FontFile = <userpath>/Documents/FreeCad/Font/Gidole-Regular.ttf
  Fuse = false
  Justification = 6
  JustificationReference = 0
  KeepLeftMargin = false
  MakeFace = true
  ObliqueAngle = 0
  Placement = pos=(84.6,-15,53.75) rot=(1,0,0;1.5708rad)
  ScaleToSize = true
  Size = 4
  String = DC 12V
  Tracking = 0
FEATURE [Part::Part2DObjectPython] ShapeString003  label="DC001"  # Draft 2D object (typed FeaturePython)
  FontFile = <userpath>/Documents/FreeCad/Font/Gidole-Regular.ttf
  Fuse = false
  Justification = 6
  JustificationReference = 0
  KeepLeftMargin = false
  MakeFace = true
  ObliqueAngle = 0
  Placement = pos=(84.6,-15,53.75) rot=(1,0,0;1.5708rad)
  ScaleToSize = true
  Size = 4
  String = DC 12V
  Tracking = 0
FEATURE [Part::Part2DObjectPython] ShapeString004  label="ANALOG001"  # Draft 2D object (typed FeaturePython)
  FontFile = <userpath>/Documents/FreeCad/Font/Gidole-Regular.ttf
  Fuse = false
  Justification = 6
  JustificationReference = 0
  KeepLeftMargin = false
  MakeFace = true
  ObliqueAngle = 0
  Placement = pos=(81.15,-22,44.8) rot=(1,0,0;1.49836rad)
  ScaleToSize = true
  Size = 4
  String = ANALOG
  Tracking = 0
FEATURE [Part::Part2DObjectPython] ShapeString005  label="DIGITAL001"  # Draft 2D object (typed FeaturePython)
  FontFile = <userpath>/Documents/FreeCad/Font/Gidole-Regular.ttf
  Fuse = false
  Justification = 6
  JustificationReference = 0
  KeepLeftMargin = false
  MakeFace = true
  ObliqueAngle = 0
  Placement = pos=(49.755,-22,44.8) rot=(1,0,0;1.49836rad)
  ScaleToSize = true
  Size = 4
  String = DIGITAL
  Tracking = 0
FEATURE [Sketcher::SketchObject] Sketch030
  ArcFitTolerance = 1e-06
  AttachmentSupport = -> [Pocket021]
  ExternalGeometry = -> [Pocket021]
  FullyConstrained = true
  MakeInternals = false
  MapMode = 5
  Placement = pos=(0,-1.65,0) rot=(1,0,0;1.5708rad)
  sketch-geometry (7):
    g0: LineSegment [constr] StartX=36.075 StartY=15.875 StartZ=0 EndX=36.875 EndY=15.875 EndZ=0
    g1: LineSegment [constr] StartX=36.875 StartY=15.875 StartZ=0 EndX=43.4 EndY=15.875 EndZ=0
    g2: LineSegment StartX=39.1375 StartY=15.875 StartZ=0 EndX=41.1375 EndY=17.875 EndZ=0
    g3: LineSegment StartX=41.1375 StartY=17.875 StartZ=0 EndX=41.1375 EndY=13.875 EndZ=0
    g4: LineSegment StartX=41.1375 StartY=13.875 StartZ=0 EndX=39.1375 EndY=15.875 EndZ=0
    g5: GeomPoint X=40.1375 Y=15.875 Z=0
    g6: GeomPoint X=41.1375 Y=15.875 Z=0
  constraints (16):
    c: Symmetric(g-3,g-3,g0)
    c: PointOnObject(g0,g-5)
    c: Horizontal(g0)
    c: Coincident(g1,g0)
    c: PointOnObject(g1,g-4)
    c: Horizontal(g1)
    c: Coincident(g2,g3)
    c: Coincident(g3,g4)
    c: Coincident(g4,g2)
    c: Symmetric(g3,g3,g6)
    c: Symmetric(g2,g6,g5)
    c: Symmetric(g1,g0,g5)
    c: PointOnObject(g2,g1)
    c: Vertical(g3)
    c: DistanceY(g3,g3) = 4
    c: DistanceX(g2,g2) = 2
FEATURE [PartDesign::Pocket] Pocket025
  BaseFeature = -> Pocket021
  Direction = (0,1,-2e-16)
  Length = 0.4
  Length2 = 5
  Profile = -> Sketch030
  ReferenceAxis = -> Sketch030 [N_Axis]
  Refine = true
  Suppressed = false
  Type = 0
FEATURE [PartDesign::Body] Body002  label="SD Card IO DOL-001"
  AllowCompound = false
  Group = -> [Clone001,Sketch022,Pad010,Pocket014,Sketch023,Pocket015,Pocket016,Sketch024,Pocket017,Sketch025,Pocket018,Sketch026,Pocket019,Sketch027,Pocket020,Chamfer001,Fillet001,Chamfer002,Sketch029,Pocket021,Sketch030,Pocket025]
  Origin = -> Origin002
  Tip = -> Pocket025
FEATURE [PartDesign::FeatureBase] Clone002
  BaseFeature = -> Body002
  Suppressed = false
FEATURE [Sketcher::SketchObject] Sketch028
  ArcFitTolerance = 1e-06
  AttachmentSupport = -> [Clone002]
  ExternalGeometry = -> [Clone002]
  FullyConstrained = true
  MakeInternals = false
  MapMode = 5
  Placement = pos=(0,0.25,-1e-16) rot=(0,0.707107,0.707107;3.14159rad)
  sketch-geometry (4):
    g0: LineSegment StartX=-104.275 StartY=37.375 StartZ=0 EndX=-104.275 EndY=23.375 EndZ=0
    g1: LineSegment StartX=-104.275 StartY=23.375 StartZ=0 EndX=-78.275 EndY=23.375 EndZ=0
    g2: LineSegment StartX=-78.275 StartY=23.375 StartZ=0 EndX=-78.275 EndY=37.375 EndZ=0
    g3: LineSegment StartX=-78.275 StartY=37.375 StartZ=0 EndX=-104.275 EndY=37.375 EndZ=0
  constraints (10):
    c: Coincident(g0,g1)
    c: Coincident(g1,g2)
    c: Coincident(g2,g3)
    c: Coincident(g3,g0)
    c: Vertical(g0)
    c: Vertical(g2)
    c: Horizontal(g1)
    c: Horizontal(g3)
    c: Coincident(g0,g-3)
    c: Coincident(g1,g-4)
FEATURE [PartDesign::Pad] Pad011
  BaseFeature = -> Clone002
  Direction = (0,1,-2e-16)
  Length = 10
  Length2 = 10
  Profile = -> Sketch028
  ReferenceAxis = -> Sketch028 [N_Axis]
  Refine = true
  Suppressed = false
  Type = 3
  UpToFace = -> Clone002 [Face144]
FEATURE [PartDesign::Body] Body003  label="SD Card IO DOL-101"
  AllowCompound = false
  Group = -> [Clone002,Sketch028,Pad011]
  Origin = -> Origin003
  Tip = -> Pad011
FEATURE [App::DocumentObjectGroup] Group  label="Template"
  Group = -> [Body002,Body,Body003,Body001]
FEATURE [PartDesign::FeatureBase] Clone003
  BaseFeature = -> Body002
  Suppressed = false
FEATURE [PartDesign::Pocket] Pocket022
  BaseFeature = -> Clone003
  Direction = (0,1,-2e-16)
  Length = 0
  Length2 = 5
  Offset = 0.4
  Profile = -> ShapeString003
  ReferenceAxis = -> ShapeString003 [N_Axis]
  Refine = true
  Suppressed = false
  Type = 3
  UpToFace = -> Clone003 [Face146]
FEATURE [PartDesign::Pocket] Pocket023
  BaseFeature = -> Pocket022
  Direction = (0,0.997378,-0.0723678)
  Length = 0
  Length2 = 5
  Offset = 0.4
  Profile = -> ShapeString004
  ReferenceAxis = -> ShapeString004 [N_Axis]
  Refine = true
  Suppressed = false
  Type = 3
  UpToFace = -> Pocket022 [Face146]
FEATURE [PartDesign::Pocket] Pocket024
  BaseFeature = -> Pocket023
  Direction = (0,0.997378,-0.0723678)
  Length = 0
  Length2 = 5
  Offset = 0.4
  Profile = -> ShapeString005
  ReferenceAxis = -> ShapeString005 [N_Axis]
  Refine = true
  Suppressed = false
  Type = 3
  UpToFace = -> Pocket023 [Face146]
FEATURE [PartDesign::FeatureBase] Clone004
  BaseFeature = -> Body
  Suppressed = false
FEATURE [Part::Part2DObjectPython] ShapeString006  label="ANALOG002"  # Draft 2D object (typed FeaturePython)
  FontFile = <userpath>/Documents/FreeCad/Font/Gidole-Regular.ttf
  Fuse = false
  Justification = 6
  JustificationReference = 0
  KeepLeftMargin = false
  MakeFace = true
  ObliqueAngle = 0
  Placement = pos=(81.15,-22,44.8) rot=(1,0,0;1.49836rad)
  ScaleToSize = true
  Size = 4
  String = ANALOG
  Tracking = 0
FEATURE [Part::Part2DObjectPython] ShapeString007  label="DIGITAL002"  # Draft 2D object (typed FeaturePython)
  FontFile = <userpath>/Documents/FreeCad/Font/Gidole-Regular.ttf
  Fuse = false
  Justification = 6
  JustificationReference = 0
  KeepLeftMargin = false
  MakeFace = true
  ObliqueAngle = 0
  Placement = pos=(49.755,-22,44.8) rot=(1,0,0;1.49836rad)
  ScaleToSize = true
  Size = 4
  String = DIGITAL
  Tracking = 0
FEATURE [Part::Part2DObjectPython] ShapeString008  label="DC002"  # Draft 2D object (typed FeaturePython)
  FontFile = <userpath>/Documents/FreeCad/Font/Gidole-Regular.ttf
  Fuse = false
  Justification = 6
  JustificationReference = 0
  KeepLeftMargin = false
  MakeFace = true
  ObliqueAngle = 0
  Placement = pos=(84.6,-15,53.75) rot=(1,0,0;1.5708rad)
  ScaleToSize = true
  Size = 4
  String = DC 12V
  Tracking = 0
FEATURE [PartDesign::Pocket] Pocket026
  BaseFeature = -> Clone004
  Direction = (0,0.997378,-0.0723678)
  Length = 0
  Length2 = 5
  Offset = 0.4
  Profile = -> ShapeString006
  ReferenceAxis = -> ShapeString006 [N_Axis]
  Refine = true
  Suppressed = false
  Type = 3
  UpToFace = -> Clone004 [Face64]
FEATURE [PartDesign::Pocket] Pocket027
  BaseFeature = -> Pocket026
  Direction = (0,0.997378,-0.0723678)
  Length = 0
  Length2 = 5
  Offset = 0.4
  Profile = -> ShapeString007
  ReferenceAxis = -> ShapeString007 [N_Axis]
  Refine = true
  Suppressed = false
  Type = 3
  UpToFace = -> Pocket026 [Face64]
FEATURE [PartDesign::Pocket] Pocket028
  BaseFeature = -> Pocket027
  Direction = (0,1,-2e-16)
  Length = 0
  Length2 = 5
  Offset = 0.4
  Profile = -> ShapeString008
  ReferenceAxis = -> ShapeString008 [N_Axis]
  Refine = true
  Suppressed = false
  Type = 3
  UpToFace = -> Pocket027 [Face64]
FEATURE [PartDesign::FeatureBase] Clone005
  BaseFeature = -> Body003
  Suppressed = false
FEATURE [Part::Part2DObjectPython] ShapeString009  label="ANALOG003"  # Draft 2D object (typed FeaturePython)
  FontFile = <userpath>/Documents/FreeCad/Font/Gidole-Regular.ttf
  Fuse = false
  Justification = 6
  JustificationReference = 0
  KeepLeftMargin = false
  MakeFace = true
  ObliqueAngle = 0
  Placement = pos=(49.01,-22,44.8) rot=(1,0,0;1.49836rad)
  ScaleToSize = true
  Size = 4
  String = ANALOG
  Tracking = 0
FEATURE [Part::Part2DObjectPython] ShapeString011  label="DC003"  # Draft 2D object (typed FeaturePython)
  FontFile = <userpath>/Documents/FreeCad/Font/Gidole-Regular.ttf
  Fuse = false
  Justification = 6
  JustificationReference = 0
  KeepLeftMargin = false
  MakeFace = true
  ObliqueAngle = 0
  Placement = pos=(84.6,-15,53.75) rot=(1,0,0;1.5708rad)
  ScaleToSize = true
  Size = 4
  String = DC 12V
  Tracking = 0
FEATURE [PartDesign::Pocket] Pocket029
  BaseFeature = -> Clone005
  Direction = (0,0.997378,-0.0723678)
  Length = 0
  Length2 = 5
  Offset = 0.4
  Profile = -> ShapeString009
  ReferenceAxis = -> ShapeString009 [N_Axis]
  Refine = true
  Suppressed = false
  Type = 3
  UpToFace = -> Clone005 [Face94]
FEATURE [PartDesign::Pocket] Pocket031
  BaseFeature = -> Pocket029
  Direction = (0,1,-2e-16)
  Length = 0
  Length2 = 5
  Offset = 0.4
  Profile = -> ShapeString011
  ReferenceAxis = -> ShapeString011 [N_Axis]
  Refine = true
  Suppressed = false
  Type = 3
  UpToFace = -> Pocket029 [Face105]
FEATURE [PartDesign::FeatureBase] Clone006
  BaseFeature = -> Body001
  Suppressed = false
FEATURE [Part::Part2DObjectPython] ShapeString012  label="ANALOG004"  # Draft 2D object (typed FeaturePython)
  FontFile = <userpath>/Documents/FreeCad/Font/Gidole-Regular.ttf
  Fuse = false
  Justification = 6
  JustificationReference = 0
  KeepLeftMargin = false
  MakeFace = true
  ObliqueAngle = 0
  Placement = pos=(49.01,-22,44.8) rot=(1,0,0;1.49836rad)
  ScaleToSize = true
  Size = 4
  String = ANALOG
  Tracking = 0
FEATURE [Part::Part2DObjectPython] ShapeString014  label="DC004"  # Draft 2D object (typed FeaturePython)
  FontFile = <userpath>/Documents/FreeCad/Font/Gidole-Regular.ttf
  Fuse = false
  Justification = 6
  JustificationReference = 0
  KeepLeftMargin = false
  MakeFace = true
  ObliqueAngle = 0
  Placement = pos=(84.6,-15,53.75) rot=(1,0,0;1.5708rad)
  ScaleToSize = true
  Size = 4
  String = DC 12V
  Tracking = 0
FEATURE [PartDesign::Pocket] Pocket032
  BaseFeature = -> Clone006
  Direction = (0,0.997378,-0.0723678)
  Length = 0
  Length2 = 5
  Offset = 0.4
  Profile = -> ShapeString012
  ReferenceAxis = -> ShapeString012 [N_Axis]
  Refine = true
  Suppressed = false
  Type = 3
  UpToFace = -> Clone006 [Face24]
FEATURE [PartDesign::Pocket] Pocket033
  BaseFeature = -> Pocket032
  Direction = (0,1,-2e-16)
  Length = 0
  Length2 = 5
  Offset = 0.4
  Profile = -> ShapeString014
  ReferenceAxis = -> ShapeString014 [N_Axis]
  Refine = true
  Suppressed = false
  Type = 3
  UpToFace = -> Pocket032 [Face106]
FEATURE [Sketcher::SketchObject] Sketch031  label="VS"
  ArcFitTolerance = 1e-06
  FullyConstrained = false
  MakeInternals = false
  Placement = pos=(48.725,7,55.85) rot=(0,1,1;3.14159rad)
  sketch-geometry (860):
    g0: BSplineCurve PolesCount=2 KnotsCount=2 Degree=1 IsPeriodic=0
    g1: BSplineCurve PolesCount=2 KnotsCount=2 Degree=1 IsPeriodic=0
    g2: BSplineCurve PolesCount=2 KnotsCount=2 Degree=1 IsPeriodic=0
    g3: BSplineCurve PolesCount=2 KnotsCount=2 Degree=1 IsPeriodic=0
    g4: BSplineCurve PolesCount=2 KnotsCount=2 Degree=1 IsPeriodic=0
    g5: BSplineCurve PolesCount=2 KnotsCount=2 Degree=1 IsPeriodic=0
    g6: BSplineCurve PolesCount=2 KnotsCount=2 Degree=1 IsPeriodic=0
    g7: BSplineCurve PolesCount=2 KnotsCount=2 Degree=1 IsPeriodic=0
    g8: BSplineCurve PolesCount=2 KnotsCount=2 Degree=1 IsPeriodic=0
    g9: BSplineCurve PolesCount=2 KnotsCount=2 Degree=1 IsPeriodic=0
    g10: BSplineCurve PolesCount=2 KnotsCount=2 Degree=1 IsPeriodic=0
    g11: BSplineCurve PolesCount=2 KnotsCount=2 Degree=1 IsPeriodic=0
    g12: BSplineCurve PolesCount=2 KnotsCount=2 Degree=1 IsPeriodic=0
    g13: BSplineCurve PolesCount=2 KnotsCount=2 Degree=1 IsPeriodic=0
    g14: BSplineCurve PolesCount=2 KnotsCount=2 Degree=1 IsPeriodic=0
    g15: BSplineCurve PolesCount=2 KnotsCount=2 Degree=1 IsPeriodic=0
    g16: BSplineCurve PolesCount=2 KnotsCount=2 Degree=1 IsPeriodic=0
    g17: BSplineCurve PolesCount=2 KnotsCount=2 Degree=1 IsPeriodic=0
    g18: BSplineCurve PolesCount=2 KnotsCount=2 Degree=1 IsPeriodic=0
    g19: BSplineCurve PolesCount=2 KnotsCount=2 Degree=1 IsPeriodic=0
    g20: BSplineCurve PolesCount=2 KnotsCount=2 Degree=1 IsPeriodic=0
    g21: BSplineCurve PolesCount=2 KnotsCount=2 Degree=1 IsPeriodic=0
    g22: BSplineCurve PolesCount=2 KnotsCount=2 Degree=1 IsPeriodic=0
    g23: BSplineCurve PolesCount=2 KnotsCount=2 Degree=1 IsPeriodic=0
    g24: BSplineCurve PolesCount=2 KnotsCount=2 Degree=1 IsPeriodic=0
    g25: BSplineCurve PolesCount=2 KnotsCount=2 Degree=1 IsPeriodic=0
    g26: BSplineCurve PolesCount=2 KnotsCount=2 Degree=1 IsPeriodic=0
    g27: BSplineCurve PolesCount=2 KnotsCount=2 Degree=1 IsPeriodic=0
    g28: BSplineCurve PolesCount=2 KnotsCount=2 Degree=1 IsPeriodic=0
    g29: BSplineCurve PolesCount=2 KnotsCount=2 Degree=1 IsPeriodic=0
    g30: BSplineCurve PolesCount=2 KnotsCount=2 Degree=1 IsPeriodic=0
    g31: BSplineCurve PolesCount=2 KnotsCount=2 Degree=1 IsPeriodic=0
    g32: BSplineCurve PolesCount=2 KnotsCount=2 Degree=1 IsPeriodic=0
    g33: BSplineCurve PolesCount=2 KnotsCount=2 Degree=1 IsPeriodic=0
    g34: BSplineCurve PolesCount=2 KnotsCount=2 Degree=1 IsPeriodic=0
    g35: BSplineCurve PolesCount=2 KnotsCount=2 Degree=1 IsPeriodic=0
    g36: BSplineCurve PolesCount=2 KnotsCount=2 Degree=1 IsPeriodic=0
    g37: BSplineCurve PolesCount=2 KnotsCount=2 Degree=1 IsPeriodic=0
    g38: BSplineCurve PolesCount=2 KnotsCount=2 Degree=1 IsPeriodic=0
    g39: BSplineCurve PolesCount=2 KnotsCount=2 Degree=1 IsPeriodic=0
    g40: BSplineCurve PolesCount=2 KnotsCount=2 Degree=1 IsPeriodic=0
    g41: BSplineCurve PolesCount=2 KnotsCount=2 Degree=1 IsPeriodic=0
    g42: BSplineCurve PolesCount=2 KnotsCount=2 Degree=1 IsPeriodic=0
    g43: BSplineCurve PolesCount=2 KnotsCount=2 Degree=1 IsPeriodic=0
    g44: BSplineCurve PolesCount=2 KnotsCount=2 Degree=1 IsPeriodic=0
    g45: BSplineCurve PolesCount=2 KnotsCount=2 Degree=1 IsPeriodic=0
    g46: BSplineCurve PolesCount=2 KnotsCount=2 Degree=1 IsPeriodic=0
    g47: BSplineCurve PolesCount=2 KnotsCount=2 Degree=1 IsPeriodic=0
    g48: BSplineCurve PolesCount=2 KnotsCount=2 Degree=1 IsPeriodic=0
    g49: BSplineCurve PolesCount=2 KnotsCount=2 Degree=1 IsPeriodic=0
    g50: BSplineCurve PolesCount=2 KnotsCount=2 Degree=1 IsPeriodic=0
    g51: BSplineCurve PolesCount=2 KnotsCount=2 Degree=1 IsPeriodic=0
    g52: BSplineCurve PolesCount=2 KnotsCount=2 Degree=1 IsPeriodic=0
    g53: BSplineCurve PolesCount=2 KnotsCount=2 Degree=1 IsPeriodic=0
    g54: BSplineCurve PolesCount=2 KnotsCount=2 Degree=1 IsPeriodic=0
    g55: BSplineCurve PolesCount=2 KnotsCount=2 Degree=1 IsPeriodic=0
    g56: BSplineCurve PolesCount=2 KnotsCount=2 Degree=1 IsPeriodic=0
    g57: BSplineCurve PolesCount=2 KnotsCount=2 Degree=1 IsPeriodic=0
    g58: BSplineCurve PolesCount=2 KnotsCount=2 Degree=1 IsPeriodic=0
    g59: BSplineCurve PolesCount=2 KnotsCount=2 Degree=1 IsPeriodic=0
    g60: BSplineCurve PolesCount=2 KnotsCount=2 Degree=1 IsPeriodic=0
    g61: BSplineCurve PolesCount=2 KnotsCount=2 Degree=1 IsPeriodic=0
    g62: BSplineCurve PolesCount=2 KnotsCount=2 Degree=1 IsPeriodic=0
    g63: BSplineCurve PolesCount=2 KnotsCount=2 Degree=1 IsPeriodic=0
    g64: BSplineCurve PolesCount=2 KnotsCount=2 Degree=1 IsPeriodic=0
    g65: BSplineCurve PolesCount=2 KnotsCount=2 Degree=1 IsPeriodic=0
    g66: BSplineCurve PolesCount=2 KnotsCount=2 Degree=1 IsPeriodic=0
    g67: BSplineCurve PolesCount=2 KnotsCount=2 Degree=1 IsPeriodic=0
    g68: BSplineCurve PolesCount=2 KnotsCount=2 Degree=1 IsPeriodic=0
    g69: BSplineCurve PolesCount=2 KnotsCount=2 Degree=1 IsPeriodic=0
    g70: BSplineCurve PolesCount=2 KnotsCount=2 Degree=1 IsPeriodic=0
    g71: BSplineCurve PolesCount=2 KnotsCount=2 Degree=1 IsPeriodic=0
    g72: BSplineCurve PolesCount=2 KnotsCount=2 Degree=1 IsPeriodic=0
    g73: BSplineCurve PolesCount=2 KnotsCount=2 Degree=1 IsPeriodic=0
    g74: BSplineCurve PolesCount=2 KnotsCount=2 Degree=1 IsPeriodic=0
    g75: BSplineCurve PolesCount=2 KnotsCount=2 Degree=1 IsPeriodic=0
    g76: BSplineCurve PolesCount=2 KnotsCount=2 Degree=1 IsPeriodic=0
    g77: BSplineCurve PolesCount=2 KnotsCount=2 Degree=1 IsPeriodic=0
    g78: BSplineCurve PolesCount=2 KnotsCount=2 Degree=1 IsPeriodic=0
    g79: BSplineCurve PolesCount=2 KnotsCount=2 Degree=1 IsPeriodic=0
    g80: BSplineCurve PolesCount=2 KnotsCount=2 Degree=1 IsPeriodic=0
    g81: BSplineCurve PolesCount=2 KnotsCount=2 Degree=1 IsPeriodic=0
    g82: BSplineCurve PolesCount=2 KnotsCount=2 Degree=1 IsPeriodic=0
    g83: BSplineCurve PolesCount=2 KnotsCount=2 Degree=1 IsPeriodic=0
    g84: BSplineCurve PolesCount=2 KnotsCount=2 Degree=1 IsPeriodic=0
    g85: BSplineCurve PolesCount=2 KnotsCount=2 Degree=1 IsPeriodic=0
    g86: BSplineCurve PolesCount=2 KnotsCount=2 Degree=1 IsPeriodic=0
    g87: BSplineCurve PolesCount=2 KnotsCount=2 Degree=1 IsPeriodic=0
    g88: BSplineCurve PolesCount=2 KnotsCount=2 Degree=1 IsPeriodic=0
    g89: BSplineCurve PolesCount=2 KnotsCount=2 Degree=1 IsPeriodic=0
    g90: BSplineCurve PolesCount=2 KnotsCount=2 Degree=1 IsPeriodic=0
    g91: BSplineCurve PolesCount=2 KnotsCount=2 Degree=1 IsPeriodic=0
    g92: BSplineCurve PolesCount=2 KnotsCount=2 Degree=1 IsPeriodic=0
    g93: BSplineCurve PolesCount=2 KnotsCount=2 Degree=1 IsPeriodic=0
    g94: BSplineCurve PolesCount=2 KnotsCount=2 Degree=1 IsPeriodic=0
    g95: BSplineCurve PolesCount=2 KnotsCount=2 Degree=1 IsPeriodic=0
    g96: BSplineCurve PolesCount=2 KnotsCount=2 Degree=1 IsPeriodic=0
    g97: BSplineCurve PolesCount=2 KnotsCount=2 Degree=1 IsPeriodic=0
    g98: BSplineCurve PolesCount=2 KnotsCount=2 Degree=1 IsPeriodic=0
    g99: BSplineCurve PolesCount=2 KnotsCount=2 Degree=1 IsPeriodic=0
    g100: BSplineCurve PolesCount=2 KnotsCount=2 Degree=1 IsPeriodic=0
    g101: BSplineCurve PolesCount=2 KnotsCount=2 Degree=1 IsPeriodic=0
    g102: BSplineCurve PolesCount=2 KnotsCount=2 Degree=1 IsPeriodic=0
    g103: BSplineCurve PolesCount=2 KnotsCount=2 Degree=1 IsPeriodic=0
    g104: BSplineCurve PolesCount=2 KnotsCount=2 Degree=1 IsPeriodic=0
    g105: BSplineCurve PolesCount=2 KnotsCount=2 Degree=1 IsPeriodic=0
    g106: BSplineCurve PolesCount=2 KnotsCount=2 Degree=1 IsPeriodic=0
    g107: BSplineCurve PolesCount=2 KnotsCount=2 Degree=1 IsPeriodic=0
    g108: BSplineCurve PolesCount=2 KnotsCount=2 Degree=1 IsPeriodic=0
    g109: BSplineCurve PolesCount=2 KnotsCount=2 Degree=1 IsPeriodic=0
    g110: BSplineCurve PolesCount=2 KnotsCount=2 Degree=1 IsPeriodic=0
    g111: BSplineCurve PolesCount=2 KnotsCount=2 Degree=1 IsPeriodic=0
    g112: BSplineCurve PolesCount=2 KnotsCount=2 Degree=1 IsPeriodic=0
    g113: BSplineCurve PolesCount=2 KnotsCount=2 Degree=1 IsPeriodic=0
    g114: BSplineCurve PolesCount=2 KnotsCount=2 Degree=1 IsPeriodic=0
    g115: BSplineCurve PolesCount=2 KnotsCount=2 Degree=1 IsPeriodic=0
    g116: BSplineCurve PolesCount=2 KnotsCount=2 Degree=1 IsPeriodic=0
    g117: BSplineCurve PolesCount=2 KnotsCount=2 Degree=1 IsPeriodic=0
    g118: BSplineCurve PolesCount=2 KnotsCount=2 Degree=1 IsPeriodic=0
    g119: BSplineCurve PolesCount=2 KnotsCount=2 Degree=1 IsPeriodic=0
    g120: BSplineCurve PolesCount=2 KnotsCount=2 Degree=1 IsPeriodic=0
    g121: BSplineCurve PolesCount=2 KnotsCount=2 Degree=1 IsPeriodic=0
    g122: BSplineCurve PolesCount=2 KnotsCount=2 Degree=1 IsPeriodic=0
    g123: BSplineCurve PolesCount=2 KnotsCount=2 Degree=1 IsPeriodic=0
    g124: BSplineCurve PolesCount=2 KnotsCount=2 Degree=1 IsPeriodic=0
    g125: BSplineCurve PolesCount=2 KnotsCount=2 Degree=1 IsPeriodic=0
    g126: BSplineCurve PolesCount=2 KnotsCount=2 Degree=1 IsPeriodic=0
    g127: BSplineCurve PolesCount=2 KnotsCount=2 Degree=1 IsPeriodic=0
    g128: BSplineCurve PolesCount=2 KnotsCount=2 Degree=1 IsPeriodic=0
    g129: BSplineCurve PolesCount=2 KnotsCount=2 Degree=1 IsPeriodic=0
    g130: BSplineCurve PolesCount=2 KnotsCount=2 Degree=1 IsPeriodic=0
    g131: BSplineCurve PolesCount=2 KnotsCount=2 Degree=1 IsPeriodic=0
    g132: BSplineCurve PolesCount=2 KnotsCount=2 Degree=1 IsPeriodic=0
    g133: BSplineCurve PolesCount=2 KnotsCount=2 Degree=1 IsPeriodic=0
    g134: BSplineCurve PolesCount=2 KnotsCount=2 Degree=1 IsPeriodic=0
    g135: BSplineCurve PolesCount=2 KnotsCount=2 Degree=1 IsPeriodic=0
    g136: BSplineCurve PolesCount=2 KnotsCount=2 Degree=1 IsPeriodic=0
    g137: BSplineCurve PolesCount=2 KnotsCount=2 Degree=1 IsPeriodic=0
    g138: BSplineCurve PolesCount=2 KnotsCount=2 Degree=1 IsPeriodic=0
    g139: BSplineCurve PolesCount=2 KnotsCount=2 Degree=1 IsPeriodic=0
    g140: BSplineCurve PolesCount=2 KnotsCount=2 Degree=1 IsPeriodic=0
    g141: BSplineCurve PolesCount=2 KnotsCount=2 Degree=1 IsPeriodic=0
    g142: BSplineCurve PolesCount=2 KnotsCount=2 Degree=1 IsPeriodic=0
    g143: BSplineCurve PolesCount=2 KnotsCount=2 Degree=1 IsPeriodic=0
    g144: BSplineCurve PolesCount=2 KnotsCount=2 Degree=1 IsPeriodic=0
    g145: BSplineCurve PolesCount=2 KnotsCount=2 Degree=1 IsPeriodic=0
    g146: BSplineCurve PolesCount=2 KnotsCount=2 Degree=1 IsPeriodic=0
    g147: BSplineCurve PolesCount=2 KnotsCount=2 Degree=1 IsPeriodic=0
    g148: BSplineCurve PolesCount=2 KnotsCount=2 Degree=1 IsPeriodic=0
    g149: BSplineCurve PolesCount=2 KnotsCount=2 Degree=1 IsPeriodic=0
    g150: BSplineCurve PolesCount=2 KnotsCount=2 Degree=1 IsPeriodic=0
    g151: BSplineCurve PolesCount=2 KnotsCount=2 Degree=1 IsPeriodic=0
    g152: BSplineCurve PolesCount=2 KnotsCount=2 Degree=1 IsPeriodic=0
    g153: BSplineCurve PolesCount=2 KnotsCount=2 Degree=1 IsPeriodic=0
    g154: BSplineCurve PolesCount=2 KnotsCount=2 Degree=1 IsPeriodic=0
    g155: BSplineCurve PolesCount=2 KnotsCount=2 Degree=1 IsPeriodic=0
    g156: BSplineCurve PolesCount=2 KnotsCount=2 Degree=1 IsPeriodic=0
    g157: BSplineCurve PolesCount=2 KnotsCount=2 Degree=1 IsPeriodic=0
    g158: BSplineCurve PolesCount=2 KnotsCount=2 Degree=1 IsPeriodic=0
    g159: BSplineCurve PolesCount=2 KnotsCount=2 Degree=1 IsPeriodic=0
    g160: BSplineCurve PolesCount=2 KnotsCount=2 Degree=1 IsPeriodic=0
    g161: BSplineCurve PolesCount=2 KnotsCount=2 Degree=1 IsPeriodic=0
    g162: BSplineCurve PolesCount=2 KnotsCount=2 Degree=1 IsPeriodic=0
    g163: BSplineCurve PolesCount=2 KnotsCount=2 Degree=1 IsPeriodic=0
    g164: BSplineCurve PolesCount=2 KnotsCount=2 Degree=1 IsPeriodic=0
    g165: BSplineCurve PolesCount=2 KnotsCount=2 Degree=1 IsPeriodic=0
    g166: BSplineCurve PolesCount=2 KnotsCount=2 Degree=1 IsPeriodic=0
    g167: BSplineCurve PolesCount=2 KnotsCount=2 Degree=1 IsPeriodic=0
    g168: BSplineCurve PolesCount=2 KnotsCount=2 Degree=1 IsPeriodic=0
    g169: BSplineCurve PolesCount=2 KnotsCount=2 Degree=1 IsPeriodic=0
    g170: BSplineCurve PolesCount=2 KnotsCount=2 Degree=1 IsPeriodic=0
    g171: BSplineCurve PolesCount=2 KnotsCount=2 Degree=1 IsPeriodic=0
    g172: BSplineCurve PolesCount=2 KnotsCount=2 Degree=1 IsPeriodic=0
    g173: BSplineCurve PolesCount=2 KnotsCount=2 Degree=1 IsPeriodic=0
    g174: BSplineCurve PolesCount=2 KnotsCount=2 Degree=1 IsPeriodic=0
    g175: BSplineCurve PolesCount=2 KnotsCount=2 Degree=1 IsPeriodic=0
    g176: BSplineCurve PolesCount=2 KnotsCount=2 Degree=1 IsPeriodic=0
    g177: BSplineCurve PolesCount=2 KnotsCount=2 Degree=1 IsPeriodic=0
    g178: BSplineCurve PolesCount=2 KnotsCount=2 Degree=1 IsPeriodic=0
    g179: BSplineCurve PolesCount=2 KnotsCount=2 Degree=1 IsPeriodic=0
    g180: BSplineCurve PolesCount=2 KnotsCount=2 Degree=1 IsPeriodic=0
    g181: BSplineCurve PolesCount=2 KnotsCount=2 Degree=1 IsPeriodic=0
    g182: BSplineCurve PolesCount=2 KnotsCount=2 Degree=1 IsPeriodic=0
    g183: BSplineCurve PolesCount=2 KnotsCount=2 Degree=1 IsPeriodic=0
    g184: BSplineCurve PolesCount=2 KnotsCount=2 Degree=1 IsPeriodic=0
    g185: BSplineCurve PolesCount=2 KnotsCount=2 Degree=1 IsPeriodic=0
    g186: BSplineCurve PolesCount=2 KnotsCount=2 Degree=1 IsPeriodic=0
    g187: BSplineCurve PolesCount=2 KnotsCount=2 Degree=1 IsPeriodic=0
    g188: BSplineCurve PolesCount=2 KnotsCount=2 Degree=1 IsPeriodic=0
    g189: BSplineCurve PolesCount=2 KnotsCount=2 Degree=1 IsPeriodic=0
    g190: BSplineCurve PolesCount=2 KnotsCount=2 Degree=1 IsPeriodic=0
    g191: BSplineCurve PolesCount=2 KnotsCount=2 Degree=1 IsPeriodic=0
    g192: BSplineCurve PolesCount=2 KnotsCount=2 Degree=1 IsPeriodic=0
    g193: BSplineCurve PolesCount=2 KnotsCount=2 Degree=1 IsPeriodic=0
    g194: BSplineCurve PolesCount=2 KnotsCount=2 Degree=1 IsPeriodic=0
    g195: BSplineCurve PolesCount=2 KnotsCount=2 Degree=1 IsPeriodic=0
    g196: BSplineCurve PolesCount=2 KnotsCount=2 Degree=1 IsPeriodic=0
    g197: BSplineCurve PolesCount=2 KnotsCount=2 Degree=1 IsPeriodic=0
    g198: BSplineCurve PolesCount=2 KnotsCount=2 Degree=1 IsPeriodic=0
    g199: BSplineCurve PolesCount=2 KnotsCount=2 Degree=1 IsPeriodic=0
    g200: BSplineCurve PolesCount=2 KnotsCount=2 Degree=1 IsPeriodic=0
    g201: BSplineCurve PolesCount=2 KnotsCount=2 Degree=1 IsPeriodic=0
    g202: BSplineCurve PolesCount=2 KnotsCount=2 Degree=1 IsPeriodic=0
    g203: BSplineCurve PolesCount=2 KnotsCount=2 Degree=1 IsPeriodic=0
    g204: BSplineCurve PolesCount=2 KnotsCount=2 Degree=1 IsPeriodic=0
    g205: BSplineCurve PolesCount=2 KnotsCount=2 Degree=1 IsPeriodic=0
    g206: BSplineCurve PolesCount=2 KnotsCount=2 Degree=1 IsPeriodic=0
    g207: BSplineCurve PolesCount=2 KnotsCount=2 Degree=1 IsPeriodic=0
    g208: BSplineCurve PolesCount=2 KnotsCount=2 Degree=1 IsPeriodic=0
    g209: BSplineCurve PolesCount=2 KnotsCount=2 Degree=1 IsPeriodic=0
    g210: BSplineCurve PolesCount=2 KnotsCount=2 Degree=1 IsPeriodic=0
    g211: BSplineCurve PolesCount=2 KnotsCount=2 Degree=1 IsPeriodic=0
    g212: BSplineCurve PolesCount=2 KnotsCount=2 Degree=1 IsPeriodic=0
    g213: BSplineCurve PolesCount=2 KnotsCount=2 Degree=1 IsPeriodic=0
    g214: BSplineCurve PolesCount=2 KnotsCount=2 Degree=1 IsPeriodic=0
    g215: BSplineCurve PolesCount=2 KnotsCount=2 Degree=1 IsPeriodic=0
    g216: BSplineCurve PolesCount=2 KnotsCount=2 Degree=1 IsPeriodic=0
    g217: BSplineCurve PolesCount=2 KnotsCount=2 Degree=1 IsPeriodic=0
    g218: BSplineCurve PolesCount=2 KnotsCount=2 Degree=1 IsPeriodic=0
    g219: BSplineCurve PolesCount=2 KnotsCount=2 Degree=1 IsPeriodic=0
    g220: BSplineCurve PolesCount=2 KnotsCount=2 Degree=1 IsPeriodic=0
    g221: BSplineCurve PolesCount=2 KnotsCount=2 Degree=1 IsPeriodic=0
    g222: BSplineCurve PolesCount=2 KnotsCount=2 Degree=1 IsPeriodic=0
    g223: BSplineCurve PolesCount=2 KnotsCount=2 Degree=1 IsPeriodic=0
    g224: BSplineCurve PolesCount=2 KnotsCount=2 Degree=1 IsPeriodic=0
    g225: BSplineCurve PolesCount=2 KnotsCount=2 Degree=1 IsPeriodic=0
    g226: BSplineCurve PolesCount=2 KnotsCount=2 Degree=1 IsPeriodic=0
    g227: BSplineCurve PolesCount=2 KnotsCount=2 Degree=1 IsPeriodic=0
    g228: BSplineCurve PolesCount=2 KnotsCount=2 Degree=1 IsPeriodic=0
    g229: BSplineCurve PolesCount=2 KnotsCount=2 Degree=1 IsPeriodic=0
    g230: BSplineCurve PolesCount=2 KnotsCount=2 Degree=1 IsPeriodic=0
    g231: BSplineCurve PolesCount=2 KnotsCount=2 Degree=1 IsPeriodic=0
    g232: BSplineCurve PolesCount=2 KnotsCount=2 Degree=1 IsPeriodic=0
    g233: BSplineCurve PolesCount=2 KnotsCount=2 Degree=1 IsPeriodic=0
    g234: BSplineCurve PolesCount=2 KnotsCount=2 Degree=1 IsPeriodic=0
    g235: BSplineCurve PolesCount=2 KnotsCount=2 Degree=1 IsPeriodic=0
    g236: BSplineCurve PolesCount=2 KnotsCount=2 Degree=1 IsPeriodic=0
    g237: BSplineCurve PolesCount=2 KnotsCount=2 Degree=1 IsPeriodic=0
    g238: BSplineCurve PolesCount=2 KnotsCount=2 Degree=1 IsPeriodic=0
    g239: BSplineCurve PolesCount=2 KnotsCount=2 Degree=1 IsPeriodic=0
    g240: BSplineCurve PolesCount=2 KnotsCount=2 Degree=1 IsPeriodic=0
    g241: BSplineCurve PolesCount=2 KnotsCount=2 Degree=1 IsPeriodic=0
    g242: BSplineCurve PolesCount=2 KnotsCount=2 Degree=1 IsPeriodic=0
    g243: BSplineCurve PolesCount=2 KnotsCount=2 Degree=1 IsPeriodic=0
    g244: BSplineCurve PolesCount=2 KnotsCount=2 Degree=1 IsPeriodic=0
    g245: BSplineCurve PolesCount=2 KnotsCount=2 Degree=1 IsPeriodic=0
    g246: BSplineCurve PolesCount=2 KnotsCount=2 Degree=1 IsPeriodic=0
    g247: BSplineCurve PolesCount=2 KnotsCount=2 Degree=1 IsPeriodic=0
    g248: BSplineCurve PolesCount=2 KnotsCount=2 Degree=1 IsPeriodic=0
    g249: BSplineCurve PolesCount=2 KnotsCount=2 Degree=1 IsPeriodic=0
    g250: BSplineCurve PolesCount=2 KnotsCount=2 Degree=1 IsPeriodic=0
    g251: BSplineCurve PolesCount=2 KnotsCount=2 Degree=1 IsPeriodic=0
    g252: BSplineCurve PolesCount=2 KnotsCount=2 Degree=1 IsPeriodic=0
    g253: BSplineCurve PolesCount=2 KnotsCount=2 Degree=1 IsPeriodic=0
    g254: BSplineCurve PolesCount=2 KnotsCount=2 Degree=1 IsPeriodic=0
    g255: BSplineCurve PolesCount=2 KnotsCount=2 Degree=1 IsPeriodic=0
    g256: BSplineCurve PolesCount=2 KnotsCount=2 Degree=1 IsPeriodic=0
    g257: BSplineCurve PolesCount=2 KnotsCount=2 Degree=1 IsPeriodic=0
    g258: BSplineCurve PolesCount=2 KnotsCount=2 Degree=1 IsPeriodic=0
    g259: BSplineCurve PolesCount=2 KnotsCount=2 Degree=1 IsPeriodic=0
    g260: BSplineCurve PolesCount=2 KnotsCount=2 Degree=1 IsPeriodic=0
    g261: BSplineCurve PolesCount=2 KnotsCount=2 Degree=1 IsPeriodic=0
    g262: BSplineCurve PolesCount=2 KnotsCount=2 Degree=1 IsPeriodic=0
    g263: BSplineCurve PolesCount=2 KnotsCount=2 Degree=1 IsPeriodic=0
    g264: BSplineCurve PolesCount=2 KnotsCount=2 Degree=1 IsPeriodic=0
    g265: BSplineCurve PolesCount=2 KnotsCount=2 Degree=1 IsPeriodic=0
    g266: BSplineCurve PolesCount=2 KnotsCount=2 Degree=1 IsPeriodic=0
    g267: BSplineCurve PolesCount=2 KnotsCount=2 Degree=1 IsPeriodic=0
    g268: BSplineCurve PolesCount=2 KnotsCount=2 Degree=1 IsPeriodic=0
    g269: BSplineCurve PolesCount=2 KnotsCount=2 Degree=1 IsPeriodic=0
    g270: BSplineCurve PolesCount=2 KnotsCount=2 Degree=1 IsPeriodic=0
    g271: BSplineCurve PolesCount=2 KnotsCount=2 Degree=1 IsPeriodic=0
    g272: BSplineCurve PolesCount=2 KnotsCount=2 Degree=1 IsPeriodic=0
    g273: BSplineCurve PolesCount=2 KnotsCount=2 Degree=1 IsPeriodic=0
    g274: BSplineCurve PolesCount=2 KnotsCount=2 Degree=1 IsPeriodic=0
    g275: BSplineCurve PolesCount=2 KnotsCount=2 Degree=1 IsPeriodic=0
    g276: BSplineCurve PolesCount=2 KnotsCount=2 Degree=1 IsPeriodic=0
    g277: BSplineCurve PolesCount=2 KnotsCount=2 Degree=1 IsPeriodic=0
    g278: BSplineCurve PolesCount=2 KnotsCount=2 Degree=1 IsPeriodic=0
    g279: BSplineCurve PolesCount=2 KnotsCount=2 Degree=1 IsPeriodic=0
    g280: BSplineCurve PolesCount=2 KnotsCount=2 Degree=1 IsPeriodic=0
    g281: BSplineCurve PolesCount=2 KnotsCount=2 Degree=1 IsPeriodic=0
    g282: BSplineCurve PolesCount=2 KnotsCount=2 Degree=1 IsPeriodic=0
    g283: BSplineCurve PolesCount=2 KnotsCount=2 Degree=1 IsPeriodic=0
    g284: BSplineCurve PolesCount=2 KnotsCount=2 Degree=1 IsPeriodic=0
    g285: BSplineCurve PolesCount=2 KnotsCount=2 Degree=1 IsPeriodic=0
    g286: BSplineCurve PolesCount=2 KnotsCount=2 Degree=1 IsPeriodic=0
    g287: BSplineCurve PolesCount=2 KnotsCount=2 Degree=1 IsPeriodic=0
    g288: BSplineCurve PolesCount=2 KnotsCount=2 Degree=1 IsPeriodic=0
    g289: BSplineCurve PolesCount=2 KnotsCount=2 Degree=1 IsPeriodic=0
    g290: BSplineCurve PolesCount=2 KnotsCount=2 Degree=1 IsPeriodic=0
    g291: BSplineCurve PolesCount=2 KnotsCount=2 Degree=1 IsPeriodic=0
    g292: BSplineCurve PolesCount=2 KnotsCount=2 Degree=1 IsPeriodic=0
    g293: BSplineCurve PolesCount=2 KnotsCount=2 Degree=1 IsPeriodic=0
    g294: BSplineCurve PolesCount=2 KnotsCount=2 Degree=1 IsPeriodic=0
    g295: BSplineCurve PolesCount=2 KnotsCount=2 Degree=1 IsPeriodic=0
    g296: BSplineCurve PolesCount=2 KnotsCount=2 Degree=1 IsPeriodic=0
    g297: BSplineCurve PolesCount=2 KnotsCount=2 Degree=1 IsPeriodic=0
    g298: BSplineCurve PolesCount=2 KnotsCount=2 Degree=1 IsPeriodic=0
    g299: BSplineCurve PolesCount=2 KnotsCount=2 Degree=1 IsPeriodic=0
    g300: BSplineCurve PolesCount=2 KnotsCount=2 Degree=1 IsPeriodic=0
    g301: BSplineCurve PolesCount=2 KnotsCount=2 Degree=1 IsPeriodic=0
    g302: BSplineCurve PolesCount=2 KnotsCount=2 Degree=1 IsPeriodic=0
    g303: BSplineCurve PolesCount=2 KnotsCount=2 Degree=1 IsPeriodic=0
    g304: BSplineCurve PolesCount=2 KnotsCount=2 Degree=1 IsPeriodic=0
    g305: BSplineCurve PolesCount=2 KnotsCount=2 Degree=1 IsPeriodic=0
    g306: BSplineCurve PolesCount=2 KnotsCount=2 Degree=1 IsPeriodic=0
    g307: BSplineCurve PolesCount=2 KnotsCount=2 Degree=1 IsPeriodic=0
    g308: BSplineCurve PolesCount=2 KnotsCount=2 Degree=1 IsPeriodic=0
    g309: BSplineCurve PolesCount=2 KnotsCount=2 Degree=1 IsPeriodic=0
    g310: BSplineCurve PolesCount=2 KnotsCount=2 Degree=1 IsPeriodic=0
    g311: BSplineCurve PolesCount=2 KnotsCount=2 Degree=1 IsPeriodic=0
    g312: BSplineCurve PolesCount=2 KnotsCount=2 Degree=1 IsPeriodic=0
    g313: BSplineCurve PolesCount=2 KnotsCount=2 Degree=1 IsPeriodic=0
    g314: BSplineCurve PolesCount=2 KnotsCount=2 Degree=1 IsPeriodic=0
    g315: BSplineCurve PolesCount=2 KnotsCount=2 Degree=1 IsPeriodic=0
    g316: BSplineCurve PolesCount=2 KnotsCount=2 Degree=1 IsPeriodic=0
    g317: BSplineCurve PolesCount=2 KnotsCount=2 Degree=1 IsPeriodic=0
    g318: BSplineCurve PolesCount=2 KnotsCount=2 Degree=1 IsPeriodic=0
    g319: BSplineCurve PolesCount=2 KnotsCount=2 Degree=1 IsPeriodic=0
    g320: BSplineCurve PolesCount=2 KnotsCount=2 Degree=1 IsPeriodic=0
    g321: BSplineCurve PolesCount=2 KnotsCount=2 Degree=1 IsPeriodic=0
    g322: BSplineCurve PolesCount=2 KnotsCount=2 Degree=1 IsPeriodic=0
    g323: BSplineCurve PolesCount=2 KnotsCount=2 Degree=1 IsPeriodic=0
    g324: BSplineCurve PolesCount=2 KnotsCount=2 Degree=1 IsPeriodic=0
    g325: BSplineCurve PolesCount=2 KnotsCount=2 Degree=1 IsPeriodic=0
    g326: BSplineCurve PolesCount=2 KnotsCount=2 Degree=1 IsPeriodic=0
    g327: BSplineCurve PolesCount=2 KnotsCount=2 Degree=1 IsPeriodic=0
    g328: BSplineCurve PolesCount=2 KnotsCount=2 Degree=1 IsPeriodic=0
    g329: BSplineCurve PolesCount=2 KnotsCount=2 Degree=1 IsPeriodic=0
    g330: BSplineCurve PolesCount=2 KnotsCount=2 Degree=1 IsPeriodic=0
    g331: BSplineCurve PolesCount=2 KnotsCount=2 Degree=1 IsPeriodic=0
    g332: BSplineCurve PolesCount=2 KnotsCount=2 Degree=1 IsPeriodic=0
    g333: BSplineCurve PolesCount=2 KnotsCount=2 Degree=1 IsPeriodic=0
    g334: BSplineCurve PolesCount=2 KnotsCount=2 Degree=1 IsPeriodic=0
    g335: BSplineCurve PolesCount=2 KnotsCount=2 Degree=1 IsPeriodic=0
    g336: BSplineCurve PolesCount=2 KnotsCount=2 Degree=1 IsPeriodic=0
    g337: BSplineCurve PolesCount=2 KnotsCount=2 Degree=1 IsPeriodic=0
    g338: BSplineCurve PolesCount=2 KnotsCount=2 Degree=1 IsPeriodic=0
    g339: BSplineCurve PolesCount=2 KnotsCount=2 Degree=1 IsPeriodic=0
    g340: BSplineCurve PolesCount=2 KnotsCount=2 Degree=1 IsPeriodic=0
    g341: BSplineCurve PolesCount=2 KnotsCount=2 Degree=1 IsPeriodic=0
    g342: BSplineCurve PolesCount=2 KnotsCount=2 Degree=1 IsPeriodic=0
    g343: BSplineCurve PolesCount=2 KnotsCount=2 Degree=1 IsPeriodic=0
    g344: BSplineCurve PolesCount=2 KnotsCount=2 Degree=1 IsPeriodic=0
    g345: BSplineCurve PolesCount=2 KnotsCount=2 Degree=1 IsPeriodic=0
    g346: BSplineCurve PolesCount=2 KnotsCount=2 Degree=1 IsPeriodic=0
    g347: BSplineCurve PolesCount=2 KnotsCount=2 Degree=1 IsPeriodic=0
    g348: BSplineCurve PolesCount=2 KnotsCount=2 Degree=1 IsPeriodic=0
    g349: BSplineCurve PolesCount=2 KnotsCount=2 Degree=1 IsPeriodic=0
    g350: BSplineCurve PolesCount=2 KnotsCount=2 Degree=1 IsPeriodic=0
    g351: BSplineCurve PolesCount=2 KnotsCount=2 Degree=1 IsPeriodic=0
    g352: BSplineCurve PolesCount=2 KnotsCount=2 Degree=1 IsPeriodic=0
    g353: BSplineCurve PolesCount=2 KnotsCount=2 Degree=1 IsPeriodic=0
    g354: BSplineCurve PolesCount=2 KnotsCount=2 Degree=1 IsPeriodic=0
    g355: BSplineCurve PolesCount=2 KnotsCount=2 Degree=1 IsPeriodic=0
    g356: BSplineCurve PolesCount=2 KnotsCount=2 Degree=1 IsPeriodic=0
    g357: BSplineCurve PolesCount=2 KnotsCount=2 Degree=1 IsPeriodic=0
    g358: BSplineCurve PolesCount=2 KnotsCount=2 Degree=1 IsPeriodic=0
    g359: BSplineCurve PolesCount=2 KnotsCount=2 Degree=1 IsPeriodic=0
    g360: BSplineCurve PolesCount=2 KnotsCount=2 Degree=1 IsPeriodic=0
    g361: BSplineCurve PolesCount=2 KnotsCount=2 Degree=1 IsPeriodic=0
    g362: BSplineCurve PolesCount=2 KnotsCount=2 Degree=1 IsPeriodic=0
    g363: BSplineCurve PolesCount=2 KnotsCount=2 Degree=1 IsPeriodic=0
    g364: BSplineCurve PolesCount=2 KnotsCount=2 Degree=1 IsPeriodic=0
    g365: BSplineCurve PolesCount=2 KnotsCount=2 Degree=1 IsPeriodic=0
    g366: BSplineCurve PolesCount=2 KnotsCount=2 Degree=1 IsPeriodic=0
    g367: BSplineCurve PolesCount=2 KnotsCount=2 Degree=1 IsPeriodic=0
    g368: BSplineCurve PolesCount=2 KnotsCount=2 Degree=1 IsPeriodic=0
    g369: BSplineCurve PolesCount=2 KnotsCount=2 Degree=1 IsPeriodic=0
    g370: BSplineCurve PolesCount=2 KnotsCount=2 Degree=1 IsPeriodic=0
    g371: BSplineCurve PolesCount=2 KnotsCount=2 Degree=1 IsPeriodic=0
    g372: BSplineCurve PolesCount=2 KnotsCount=2 Degree=1 IsPeriodic=0
    g373: BSplineCurve PolesCount=2 KnotsCount=2 Degree=1 IsPeriodic=0
    g374: BSplineCurve PolesCount=2 KnotsCount=2 Degree=1 IsPeriodic=0
    g375: BSplineCurve PolesCount=2 KnotsCount=2 Degree=1 IsPeriodic=0
    g376: BSplineCurve PolesCount=2 KnotsCount=2 Degree=1 IsPeriodic=0
    g377: BSplineCurve PolesCount=2 KnotsCount=2 Degree=1 IsPeriodic=0
    g378: BSplineCurve PolesCount=2 KnotsCount=2 Degree=1 IsPeriodic=0
    g379: BSplineCurve PolesCount=2 KnotsCount=2 Degree=1 IsPeriodic=0
    g380: BSplineCurve PolesCount=2 KnotsCount=2 Degree=1 IsPeriodic=0
    g381: BSplineCurve PolesCount=2 KnotsCount=2 Degree=1 IsPeriodic=0
    g382: BSplineCurve PolesCount=2 KnotsCount=2 Degree=1 IsPeriodic=0
    g383: BSplineCurve PolesCount=2 KnotsCount=2 Degree=1 IsPeriodic=0
    g384: BSplineCurve PolesCount=2 KnotsCount=2 Degree=1 IsPeriodic=0
    g385: BSplineCurve PolesCount=2 KnotsCount=2 Degree=1 IsPeriodic=0
    g386: BSplineCurve PolesCount=2 KnotsCount=2 Degree=1 IsPeriodic=0
    g387: BSplineCurve PolesCount=2 KnotsCount=2 Degree=1 IsPeriodic=0
    g388: BSplineCurve PolesCount=2 KnotsCount=2 Degree=1 IsPeriodic=0
    g389: BSplineCurve PolesCount=2 KnotsCount=2 Degree=1 IsPeriodic=0
    g390: BSplineCurve PolesCount=2 KnotsCount=2 Degree=1 IsPeriodic=0
    g391: BSplineCurve PolesCount=2 KnotsCount=2 Degree=1 IsPeriodic=0
    g392: BSplineCurve PolesCount=2 KnotsCount=2 Degree=1 IsPeriodic=0
    g393: BSplineCurve PolesCount=2 KnotsCount=2 Degree=1 IsPeriodic=0
    g394: BSplineCurve PolesCount=2 KnotsCount=2 Degree=1 IsPeriodic=0
    g395: BSplineCurve PolesCount=2 KnotsCount=2 Degree=1 IsPeriodic=0
    g396: BSplineCurve PolesCount=2 KnotsCount=2 Degree=1 IsPeriodic=0
    g397: BSplineCurve PolesCount=2 KnotsCount=2 Degree=1 IsPeriodic=0
    g398: BSplineCurve PolesCount=2 KnotsCount=2 Degree=1 IsPeriodic=0
    g399: BSplineCurve PolesCount=2 KnotsCount=2 Degree=1 IsPeriodic=0
    ... +460 more geometry lines
  constraints (860):
    c: Coincident(g0,g1)
    c: Coincident(g1,g2)
    c: Coincident(g2,g3)
    c: Coincident(g3,g4)
    c: Coincident(g4,g5)
    c: Coincident(g5,g6)
    c: Coincident(g6,g7)
    c: Coincident(g7,g8)
    c: Coincident(g8,g9)
    c: Coincident(g9,g10)
    c: Coincident(g10,g11)
    c: Coincident(g11,g12)
    c: Coincident(g12,g13)
    c: Coincident(g13,g14)
    c: Coincident(g14,g15)
    c: Coincident(g15,g16)
    c: Coincident(g16,g17)
    c: Coincident(g17,g18)
    c: Coincident(g18,g19)
    c: Coincident(g19,g20)
    c: Coincident(g20,g21)
    c: Coincident(g21,g22)
    c: Coincident(g22,g23)
    c: Coincident(g23,g24)
    c: Coincident(g24,g25)
    c: Coincident(g25,g26)
    c: Coincident(g26,g27)
    c: Coincident(g27,g28)
    c: Coincident(g28,g29)
    c: Coincident(g29,g30)
    c: Coincident(g30,g31)
    c: Coincident(g31,g32)
    c: Coincident(g32,g33)
    c: Coincident(g33,g34)
    c: Coincident(g34,g35)
    c: Coincident(g35,g36)
    c: Coincident(g36,g37)
    c: Coincident(g37,g38)
    c: Coincident(g38,g39)
    c: Coincident(g39,g40)
    c: Coincident(g40,g41)
    c: Coincident(g41,g42)
    c: Coincident(g42,g43)
    c: Coincident(g43,g44)
    c: Coincident(g44,g45)
    c: Coincident(g45,g46)
    c: Coincident(g46,g47)
    c: Coincident(g47,g48)
    c: Coincident(g48,g49)
    c: Coincident(g49,g50)
    c: Coincident(g50,g51)
    c: Coincident(g51,g52)
    c: Coincident(g52,g53)
    c: Coincident(g53,g54)
    c: Coincident(g54,g55)
    c: Coincident(g55,g56)
    c: Coincident(g56,g57)
    c: Coincident(g57,g58)
    c: Coincident(g58,g59)
    c: Coincident(g59,g60)
    c: Coincident(g60,g61)
    c: Coincident(g61,g62)
    c: Coincident(g62,g63)
    c: Coincident(g63,g64)
    c: Coincident(g64,g65)
    c: Coincident(g65,g66)
    c: Coincident(g66,g67)
    c: Coincident(g67,g68)
    c: Coincident(g68,g69)
    c: Coincident(g69,g70)
    c: Coincident(g70,g71)
    c: Coincident(g71,g72)
    c: Coincident(g72,g73)
    c: Coincident(g73,g74)
    c: Coincident(g74,g75)
    c: Coincident(g75,g76)
    c: Coincident(g76,g77)
    c: Coincident(g77,g78)
    c: Coincident(g78,g79)
    c: Coincident(g79,g80)
    c: Coincident(g80,g81)
    c: Coincident(g81,g82)
    c: Coincident(g82,g83)
    c: Coincident(g83,g84)
    c: Coincident(g84,g85)
    c: Coincident(g85,g86)
    c: Coincident(g86,g87)
    c: Coincident(g87,g0)
    c: Coincident(g88,g89)
    c: Coincident(g89,g90)
    c: Coincident(g90,g91)
    c: Coincident(g91,g92)
    c: Coincident(g92,g93)
    c: Coincident(g93,g94)
    c: Coincident(g94,g95)
    c: Coincident(g95,g96)
    c: Coincident(g96,g97)
    c: Coincident(g97,g98)
    c: Coincident(g98,g99)
    c: Coincident(g99,g100)
    c: Coincident(g100,g101)
    c: Coincident(g101,g102)
    c: Coincident(g102,g103)
    c: Coincident(g103,g104)
    c: Coincident(g104,g105)
    c: Coincident(g105,g106)
    c: Coincident(g106,g107)
    c: Coincident(g107,g108)
    c: Coincident(g108,g109)
    c: Coincident(g109,g110)
    c: Coincident(g110,g111)
    c: Coincident(g111,g112)
    c: Coincident(g112,g113)
    c: Coincident(g113,g114)
    c: Coincident(g114,g115)
    c: Coincident(g115,g116)
    c: Coincident(g116,g117)
    c: Coincident(g117,g118)
    c: Coincident(g118,g119)
    c: Coincident(g119,g120)
    c: Coincident(g120,g121)
    c: Coincident(g121,g122)
    c: Coincident(g122,g123)
    c: Coincident(g123,g124)
    c: Coincident(g124,g125)
    c: Coincident(g125,g126)
    c: Coincident(g126,g127)
    c: Coincident(g127,g88)
    c: Coincident(g128,g129)
    c: Coincident(g129,g130)
    c: Coincident(g130,g131)
    c: Coincident(g131,g132)
    c: Coincident(g132,g133)
    c: Coincident(g133,g134)
    c: Coincident(g134,g135)
    c: Coincident(g135,g136)
    c: Coincident(g136,g137)
    c: Coincident(g137,g138)
    c: Coincident(g138,g139)
    c: Coincident(g139,g140)
    c: Coincident(g140,g141)
    c: Coincident(g141,g142)
    c: Coincident(g142,g143)
    c: Coincident(g143,g144)
    c: Coincident(g144,g145)
    c: Coincident(g145,g146)
    c: Coincident(g146,g147)
    c: Coincident(g147,g148)
    c: Coincident(g148,g149)
    c: Coincident(g149,g150)
    c: Coincident(g150,g151)
    c: Coincident(g151,g152)
    c: Coincident(g152,g153)
    c: Coincident(g153,g154)
    c: Coincident(g154,g155)
    c: Coincident(g155,g156)
    c: Coincident(g156,g157)
    c: Coincident(g157,g158)
    c: Coincident(g158,g159)
    c: Coincident(g159,g160)
    c: Coincident(g160,g161)
    c: Coincident(g161,g162)
    c: Coincident(g162,g163)
    c: Coincident(g163,g164)
    c: Coincident(g164,g165)
    c: Coincident(g165,g166)
    c: Coincident(g166,g167)
    c: Coincident(g167,g168)
    c: Coincident(g168,g169)
    c: Coincident(g169,g170)
    c: Coincident(g170,g171)
    c: Coincident(g171,g172)
    c: Coincident(g172,g173)
    c: Coincident(g173,g174)
    c: Coincident(g174,g175)
    c: Coincident(g175,g176)
    c: Coincident(g176,g177)
    c: Coincident(g177,g178)
    c: Coincident(g178,g179)
    c: Coincident(g179,g180)
    c: Coincident(g180,g181)
    c: Coincident(g181,g182)
    c: Coincident(g182,g183)
    c: Coincident(g183,g184)
    c: Coincident(g184,g185)
    c: Coincident(g185,g186)
    c: Coincident(g186,g187)
    c: Coincident(g187,g188)
    c: Coincident(g188,g189)
    c: Coincident(g189,g190)
    c: Coincident(g190,g191)
    c: Coincident(g191,g192)
    c: Coincident(g192,g193)
    c: Coincident(g193,g194)
    c: Coincident(g194,g195)
    c: Coincident(g195,g196)
    c: Coincident(g196,g197)
    c: Coincident(g197,g198)
    c: Coincident(g198,g199)
    c: Coincident(g199,g200)
    c: Coincident(g200,g201)
    c: Coincident(g201,g202)
    c: Coincident(g202,g203)
    c: Coincident(g203,g204)
    c: Coincident(g204,g205)
    c: Coincident(g205,g206)
    c: Coincident(g206,g207)
    c: Coincident(g207,g208)
    c: Coincident(g208,g209)
    c: Coincident(g209,g210)
    c: Coincident(g210,g211)
    c: Coincident(g211,g212)
    c: Coincident(g212,g213)
    c: Coincident(g213,g214)
    c: Coincident(g214,g215)
    c: Coincident(g215,g216)
    c: Coincident(g216,g217)
    c: Coincident(g217,g218)
    c: Coincident(g218,g219)
    c: Coincident(g219,g220)
    c: Coincident(g220,g221)
    c: Coincident(g221,g222)
    c: Coincident(g222,g223)
    c: Coincident(g223,g224)
    c: Coincident(g224,g225)
    c: Coincident(g225,g226)
    c: Coincident(g226,g227)
    c: Coincident(g227,g228)
    c: Coincident(g228,g229)
    c: Coincident(g229,g230)
    c: Coincident(g230,g231)
    c: Coincident(g231,g232)
    c: Coincident(g232,g233)
    c: Coincident(g233,g234)
    c: Coincident(g234,g235)
    c: Coincident(g235,g236)
    c: Coincident(g236,g237)
    c: Coincident(g237,g238)
    c: Coincident(g238,g239)
    c: Coincident(g239,g128)
    c: Coincident(g240,g241)
    c: Coincident(g241,g242)
    c: Coincident(g242,g243)
    c: Coincident(g243,g244)
    c: Coincident(g244,g245)
    c: Coincident(g245,g246)
    c: Coincident(g246,g247)
    c: Coincident(g247,g248)
    c: Coincident(g248,g249)
    c: Coincident(g249,g250)
    c: Coincident(g250,g251)
    c: Coincident(g251,g252)
    c: Coincident(g252,g253)
    c: Coincident(g253,g254)
    c: Coincident(g254,g255)
    c: Coincident(g255,g256)
    c: Coincident(g256,g257)
    c: Coincident(g257,g258)
    c: Coincident(g258,g259)
    c: Coincident(g259,g260)
    c: Coincident(g260,g261)
    c: Coincident(g261,g262)
    c: Coincident(g262,g263)
    c: Coincident(g263,g264)
    c: Coincident(g264,g265)
    c: Coincident(g265,g266)
    c: Coincident(g266,g267)
    c: Coincident(g267,g268)
    c: Coincident(g268,g269)
    c: Coincident(g269,g270)
    c: Coincident(g270,g271)
    c: Coincident(g271,g272)
    c: Coincident(g272,g273)
    c: Coincident(g273,g274)
    c: Coincident(g274,g275)
    c: Coincident(g275,g276)
    c: Coincident(g276,g277)
    c: Coincident(g277,g278)
    c: Coincident(g278,g279)
    c: Coincident(g279,g280)
    c: Coincident(g280,g281)
    c: Coincident(g281,g282)
    c: Coincident(g282,g283)
    c: Coincident(g283,g284)
    c: Coincident(g284,g285)
    c: Coincident(g285,g286)
    c: Coincident(g286,g287)
    c: Coincident(g287,g240)
    c: Coincident(g288,g289)
    c: Coincident(g289,g290)
    c: Coincident(g290,g291)
    c: Coincident(g291,g292)
    c: Coincident(g292,g293)
    c: Coincident(g293,g294)
    c: Coincident(g294,g295)
    c: Coincident(g295,g296)
    c: Coincident(g296,g297)
    c: Coincident(g297,g298)
    c: Coincident(g298,g299)
    c: Coincident(g299,g300)
    c: Coincident(g300,g301)
    c: Coincident(g301,g302)
    c: Coincident(g302,g303)
    c: Coincident(g303,g304)
    c: Coincident(g304,g305)
    c: Coincident(g305,g306)
    c: Coincident(g306,g307)
    c: Coincident(g307,g308)
    c: Coincident(g308,g309)
    c: Coincident(g309,g310)
    c: Coincident(g310,g311)
    c: Coincident(g311,g288)
    c: Coincident(g312,g313)
    c: Coincident(g313,g314)
    c: Coincident(g314,g315)
    c: Coincident(g315,g316)
    c: Coincident(g316,g317)
    c: Coincident(g317,g318)
    c: Coincident(g318,g319)
    c: Coincident(g319,g320)
    c: Coincident(g320,g321)
    c: Coincident(g321,g322)
    c: Coincident(g322,g323)
    c: Coincident(g323,g324)
    c: Coincident(g324,g325)
    c: Coincident(g325,g326)
    c: Coincident(g326,g327)
    c: Coincident(g327,g312)
    c: Coincident(g328,g329)
    c: Coincident(g329,g330)
    c: Coincident(g330,g331)
    c: Coincident(g331,g332)
    c: Coincident(g332,g333)
    c: Coincident(g333,g334)
    c: Coincident(g334,g335)
    c: Coincident(g335,g336)
    c: Coincident(g336,g337)
    c: Coincident(g337,g338)
    c: Coincident(g338,g339)
    c: Coincident(g339,g340)
    c: Coincident(g340,g341)
    c: Coincident(g341,g342)
    c: Coincident(g342,g343)
    c: Coincident(g343,g344)
    c: Coincident(g344,g345)
    c: Coincident(g345,g346)
    c: Coincident(g346,g347)
    c: Coincident(g347,g348)
    c: Coincident(g348,g349)
    c: Coincident(g349,g350)
    c: Coincident(g350,g351)
    c: Coincident(g351,g352)
    c: Coincident(g352,g353)
    c: Coincident(g353,g354)
    c: Coincident(g354,g355)
    c: Coincident(g355,g356)
    c: Coincident(g356,g357)
    c: Coincident(g357,g358)
    c: Coincident(g358,g359)
    c: Coincident(g359,g360)
    c: Coincident(g360,g361)
    c: Coincident(g361,g362)
    c: Coincident(g362,g363)
    c: Coincident(g363,g364)
    c: Coincident(g364,g365)
    c: Coincident(g365,g366)
    c: Coincident(g366,g367)
    c: Coincident(g367,g368)
    c: Coincident(g368,g369)
    c: Coincident(g369,g370)
    c: Coincident(g370,g371)
    c: Coincident(g371,g372)
    c: Coincident(g372,g373)
    c: Coincident(g373,g374)
    c: Coincident(g374,g375)
    c: Coincident(g375,g376)
    c: Coincident(g376,g377)
    c: Coincident(g377,g378)
    c: Coincident(g378,g379)
    c: Coincident(g379,g380)
    c: Coincident(g380,g381)
    c: Coincident(g381,g382)
    c: Coincident(g382,g383)
    c: Coincident(g383,g384)
    c: Coincident(g384,g385)
    c: Coincident(g385,g386)
    c: Coincident(g386,g387)
    c: Coincident(g387,g388)
    c: Coincident(g388,g389)
    c: Coincident(g389,g390)
    c: Coincident(g390,g391)
    c: Coincident(g391,g392)
    c: Coincident(g392,g393)
    c: Coincident(g393,g394)
    c: Coincident(g394,g395)
    c: Coincident(g395,g396)
    c: Coincident(g396,g397)
    c: Coincident(g397,g398)
    c: Coincident(g398,g399)
    c: Coincident(g399,g328)
    c: Coincident(g400,g401)
    c: Coincident(g401,g402)
    c: Coincident(g402,g403)
    c: Coincident(g403,g404)
    c: Coincident(g404,g405)
    c: Coincident(g405,g406)
    c: Coincident(g406,g407)
    c: Coincident(g407,g408)
    c: Coincident(g408,g409)
    c: Coincident(g409,g410)
    c: Coincident(g410,g411)
    c: Coincident(g411,g412)
    c: Coincident(g412,g413)
    c: Coincident(g413,g414)
    c: Coincident(g414,g415)
    c: Coincident(g415,g416)
    c: Coincident(g416,g417)
    c: Coincident(g417,g418)
    c: Coincident(g418,g419)
    c: Coincident(g419,g420)
    c: Coincident(g420,g421)
    c: Coincident(g421,g422)
    c: Coincident(g422,g423)
    c: Coincident(g423,g400)
    c: Coincident(g424,g425)
    c: Coincident(g425,g426)
    c: Coincident(g426,g427)
    c: Coincident(g427,g428)
    c: Coincident(g428,g429)
    c: Coincident(g429,g430)
    c: Coincident(g430,g431)
    c: Coincident(g431,g432)
    c: Coincident(g432,g433)
    c: Coincident(g433,g434)
    c: Coincident(g434,g435)
    c: Coincident(g435,g436)
    c: Coincident(g436,g437)
    c: Coincident(g437,g438)
    c: Coincident(g438,g439)
    c: Coincident(g439,g440)
    c: Coincident(g440,g441)
    c: Coincident(g441,g442)
    c: Coincident(g442,g443)
    c: Coincident(g443,g444)
    c: Coincident(g444,g445)
    c: Coincident(g445,g446)
    c: Coincident(g446,g447)
    c: Coincident(g447,g448)
    c: Coincident(g448,g449)
    c: Coincident(g449,g450)
    c: Coincident(g450,g451)
    c: Coincident(g451,g452)
    c: Coincident(g452,g453)
    c: Coincident(g453,g454)
    c: Coincident(g454,g455)
    c: Coincident(g455,g456)
    c: Coincident(g456,g457)
    c: Coincident(g457,g458)
    c: Coincident(g458,g459)
    c: Coincident(g459,g460)
    c: Coincident(g460,g461)
    c: Coincident(g461,g462)
    c: Coincident(g462,g463)
    c: Coincident(g463,g464)
    c: Coincident(g464,g465)
    c: Coincident(g465,g466)
    c: Coincident(g466,g467)
    c: Coincident(g467,g468)
    c: Coincident(g468,g469)
    c: Coincident(g469,g470)
    c: Coincident(g470,g471)
    c: Coincident(g471,g472)
    c: Coincident(g472,g473)
    c: Coincident(g473,g474)
    c: Coincident(g474,g475)
    c: Coincident(g475,g476)
    c: Coincident(g476,g477)
    c: Coincident(g477,g478)
    c: Coincident(g478,g479)
    c: Coincident(g479,g424)
    c: Coincident(g480,g481)
    c: Coincident(g481,g482)
    c: Coincident(g482,g483)
    c: Coincident(g483,g484)
    c: Coincident(g484,g485)
    c: Coincident(g485,g486)
    c: Coincident(g486,g487)
    c: Coincident(g487,g488)
    c: Coincident(g488,g489)
    c: Coincident(g489,g490)
    c: Coincident(g490,g491)
    c: Coincident(g491,g492)
    c: Coincident(g492,g493)
    c: Coincident(g493,g494)
    c: Coincident(g494,g495)
    c: Coincident(g495,g480)
    c: Coincident(g496,g497)
    c: Coincident(g497,g498)
    c: Coincident(g498,g499)
    c: Coincident(g499,g500)
    c: Coincident(g500,g501)
    c: Coincident(g501,g502)
    c: Coincident(g502,g503)
    c: Coincident(g503,g504)
    c: Coincident(g504,g505)
    c: Coincident(g505,g506)
    c: Coincident(g506,g507)
    c: Coincident(g507,g508)
    c: Coincident(g508,g509)
    c: Coincident(g509,g510)
    c: Coincident(g510,g511)
    c: Coincident(g511,g512)
    c: Coincident(g512,g513)
    c: Coincident(g513,g514)
    c: Coincident(g514,g515)
    c: Coincident(g515,g516)
    c: Coincident(g516,g517)
    c: Coincident(g517,g518)
    c: Coincident(g518,g519)
    c: Coincident(g519,g520)
    c: Coincident(g520,g521)
    c: Coincident(g521,g522)
    c: Coincident(g522,g523)
    c: Coincident(g523,g524)
    c: Coincident(g524,g525)
    c: Coincident(g525,g526)
    c: Coincident(g526,g527)
    c: Coincident(g527,g528)
    c: Coincident(g528,g529)
    c: Coincident(g529,g530)
    c: Coincident(g530,g531)
    c: Coincident(g531,g532)
    c: Coincident(g532,g533)
    c: Coincident(g533,g534)
    c: Coincident(g534,g535)
    c: Coincident(g535,g496)
    c: Coincident(g536,g537)
    c: Coincident(g537,g538)
    c: Coincident(g538,g539)
    c: Coincident(g539,g540)
    c: Coincident(g540,g541)
    c: Coincident(g541,g542)
    c: Coincident(g542,g543)
    c: Coincident(g543,g544)
    c: Coincident(g544,g545)
    c: Coincident(g545,g546)
    c: Coincident(g546,g547)
    c: Coincident(g547,g548)
    c: Coincident(g548,g549)
    c: Coincident(g549,g550)
    c: Coincident(g550,g551)
    c: Coincident(g551,g552)
    c: Coincident(g552,g553)
    c: Coincident(g553,g554)
    c: Coincident(g554,g555)
    c: Coincident(g555,g556)
    c: Coincident(g556,g557)
    c: Coincident(g557,g558)
    c: Coincident(g558,g559)
    c: Coincident(g559,g560)
    c: Coincident(g560,g561)
    c: Coincident(g561,g562)
    c: Coincident(g562,g563)
    c: Coincident(g563,g564)
    c: Coincident(g564,g565)
    c: Coincident(g565,g566)
    c: Coincident(g566,g567)
    c: Coincident(g567,g568)
    c: Coincident(g568,g569)
    c: Coincident(g569,g570)
    c: Coincident(g570,g571)
    c: Coincident(g571,g572)
    c: Coincident(g572,g573)
    c: Coincident(g573,g574)
    c: Coincident(g574,g575)
    c: Coincident(g575,g536)
    c: Coincident(g576,g577)
    c: Coincident(g577,g578)
    c: Coincident(g578,g579)
    c: Coincident(g579,g580)
    c: Coincident(g580,g581)
    c: Coincident(g581,g582)
    c: Coincident(g582,g583)
    c: Coincident(g583,g584)
    c: Coincident(g584,g585)
    c: Coincident(g585,g586)
    c: Coincident(g586,g587)
    c: Coincident(g587,g576)
    c: Coincident(g588,g589)
    c: Coincident(g589,g590)
    c: Coincident(g590,g591)
    c: Coincident(g591,g592)
    c: Coincident(g592,g593)
    c: Coincident(g593,g594)
    c: Coincident(g594,g595)
    c: Coincident(g595,g596)
    c: Coincident(g596,g597)
    c: Coincident(g597,g598)
    c: Coincident(g598,g599)
    c: Coincident(g599,g600)
    c: Coincident(g600,g601)
    c: Coincident(g601,g602)
    c: Coincident(g602,g603)
    c: Coincident(g603,g604)
    c: Coincident(g604,g605)
    c: Coincident(g605,g606)
    c: Coincident(g606,g607)
    c: Coincident(g607,g608)
    c: Coincident(g608,g609)
    c: Coincident(g609,g610)
    c: Coincident(g610,g611)
    c: Coincident(g611,g612)
    c: Coincident(g612,g613)
    c: Coincident(g613,g614)
    c: Coincident(g614,g615)
    c: Coincident(g615,g616)
    c: Coincident(g616,g617)
    c: Coincident(g617,g618)
    c: Coincident(g618,g619)
    c: Coincident(g619,g620)
    c: Coincident(g620,g621)
    c: Coincident(g621,g622)
    c: Coincident(g622,g623)
    c: Coincident(g623,g624)
    c: Coincident(g624,g625)
    c: Coincident(g625,g626)
    c: Coincident(g626,g627)
    c: Coincident(g627,g628)
    c: Coincident(g628,g629)
    c: Coincident(g629,g630)
    c: Coincident(g630,g631)
    c: Coincident(g631,g632)
    c: Coincident(g632,g633)
    c: Coincident(g633,g634)
    c: Coincident(g634,g635)
    c: Coincident(g635,g636)
    c: Coincident(g636,g637)
    c: Coincident(g637,g638)
    c: Coincident(g638,g639)
    c: Coincident(g639,g640)
    c: Coincident(g640,g641)
    c: Coincident(g641,g642)
    c: Coincident(g642,g643)
    c: Coincident(g643,g644)
    c: Coincident(g644,g645)
    c: Coincident(g645,g646)
    c: Coincident(g646,g647)
    c: Coincident(g647,g648)
    c: Coincident(g648,g649)
    c: Coincident(g649,g650)
    c: Coincident(g650,g651)
    c: Coincident(g651,g652)
    c: Coincident(g652,g653)
    c: Coincident(g653,g654)
    c: Coincident(g654,g655)
    c: Coincident(g655,g656)
    c: Coincident(g656,g657)
    c: Coincident(g657,g658)
    c: Coincident(g658,g659)
    c: Coincident(g659,g660)
    c: Coincident(g660,g661)
    c: Coincident(g661,g662)
    c: Coincident(g662,g663)
    c: Coincident(g663,g664)
    c: Coincident(g664,g665)
    c: Coincident(g665,g666)
    c: Coincident(g666,g667)
    c: Coincident(g667,g668)
    c: Coincident(g668,g669)
    c: Coincident(g669,g670)
    c: Coincident(g670,g671)
    c: Coincident(g671,g672)
    c: Coincident(g672,g673)
    c: Coincident(g673,g674)
    c: Coincident(g674,g675)
    c: Coincident(g675,g588)
    c: Coincident(g676,g677)
    c: Coincident(g677,g678)
    c: Coincident(g678,g679)
    c: Coincident(g679,g680)
    c: Coincident(g680,g681)
    c: Coincident(g681,g682)
    c: Coincident(g682,g683)
    c: Coincident(g683,g684)
    c: Coincident(g684,g685)
    c: Coincident(g685,g686)
    c: Coincident(g686,g687)
    c: Coincident(g687,g688)
    c: Coincident(g688,g689)
    c: Coincident(g689,g690)
    c: Coincident(g690,g691)
    c: Coincident(g691,g676)
    c: Coincident(g692,g693)
    c: Coincident(g693,g694)
    c: Coincident(g694,g695)
    c: Coincident(g695,g696)
    c: Coincident(g696,g697)
    c: Coincident(g697,g698)
    c: Coincident(g698,g699)
    c: Coincident(g699,g700)
    c: Coincident(g700,g701)
    c: Coincident(g701,g702)
    c: Coincident(g702,g703)
    c: Coincident(g703,g704)
    c: Coincident(g704,g705)
    c: Coincident(g705,g706)
    c: Coincident(g706,g707)
    c: Coincident(g707,g708)
    c: Coincident(g708,g709)
    c: Coincident(g709,g710)
    c: Coincident(g710,g711)
    c: Coincident(g711,g712)
    c: Coincident(g712,g713)
    c: Coincident(g713,g714)
    c: Coincident(g714,g715)
    c: Coincident(g715,g716)
    c: Coincident(g716,g717)
    c: Coincident(g717,g718)
    c: Coincident(g718,g719)
    c: Coincident(g719,g720)
    c: Coincident(g720,g721)
    c: Coincident(g721,g722)
    c: Coincident(g722,g723)
    c: Coincident(g723,g724)
    c: Coincident(g724,g725)
    c: Coincident(g725,g726)
    c: Coincident(g726,g727)
    c: Coincident(g727,g728)
    c: Coincident(g728,g729)
    c: Coincident(g729,g730)
    c: Coincident(g730,g731)
    c: Coincident(g731,g692)
    c: Coincident(g732,g733)
    c: Coincident(g733,g734)
    c: Coincident(g734,g735)
    c: Coincident(g735,g736)
    c: Coincident(g736,g737)
    c: Coincident(g737,g738)
    c: Coincident(g738,g739)
    c: Coincident(g739,g740)
    c: Coincident(g740,g741)
    c: Coincident(g741,g742)
    c: Coincident(g742,g743)
    c: Coincident(g743,g744)
    c: Coincident(g744,g745)
    c: Coincident(g745,g746)
    c: Coincident(g746,g747)
    c: Coincident(g747,g748)
    c: Coincident(g748,g749)
    c: Coincident(g749,g750)
    c: Coincident(g750,g751)
    c: Coincident(g751,g752)
    c: Coincident(g752,g753)
    c: Coincident(g753,g754)
    c: Coincident(g754,g755)
    c: Coincident(g755,g756)
    c: Coincident(g756,g757)
    c: Coincident(g757,g758)
    c: Coincident(g758,g759)
    c: Coincident(g759,g760)
    c: Coincident(g760,g761)
    c: Coincident(g761,g762)
    c: Coincident(g762,g763)
    c: Coincident(g763,g732)
    c: Coincident(g764,g765)
    c: Coincident(g765,g766)
    c: Coincident(g766,g767)
    c: Coincident(g767,g768)
    c: Coincident(g768,g769)
    c: Coincident(g769,g770)
    c: Coincident(g770,g771)
    c: Coincident(g771,g772)
    c: Coincident(g772,g773)
    c: Coincident(g773,g774)
    c: Coincident(g774,g775)
    c: Coincident(g775,g776)
    c: Coincident(g776,g777)
    c: Coincident(g777,g778)
    c: Coincident(g778,g779)
    c: Coincident(g779,g780)
    c: Coincident(g780,g781)
    c: Coincident(g781,g782)
    c: Coincident(g782,g783)
    c: Coincident(g783,g784)
    c: Coincident(g784,g785)
    c: Coincident(g785,g786)
    c: Coincident(g786,g787)
    c: Coincident(g787,g764)
    c: Coincident(g788,g789)
    c: Coincident(g789,g790)
    c: Coincident(g790,g791)
    c: Coincident(g791,g792)
    c: Coincident(g792,g793)
    c: Coincident(g793,g794)
    c: Coincident(g794,g795)
    c: Coincident(g795,g796)
    c: Coincident(g796,g797)
    c: Coincident(g797,g798)
    c: Coincident(g798,g799)
    c: Coincident(g799,g800)
    c: Coincident(g800,g801)
    c: Coincident(g801,g802)
    c: Coincident(g802,g803)
    c: Coincident(g803,g804)
    c: Coincident(g804,g805)
    c: Coincident(g805,g806)
    c: Coincident(g806,g807)
    c: Coincident(g807,g808)
    c: Coincident(g808,g809)
    c: Coincident(g809,g810)
    c: Coincident(g810,g811)
    c: Coincident(g811,g812)
    c: Coincident(g812,g813)
    c: Coincident(g813,g814)
    c: Coincident(g814,g815)
    c: Coincident(g815,g816)
    c: Coincident(g816,g817)
    c: Coincident(g817,g818)
    c: Coincident(g818,g819)
    c: Coincident(g819,g820)
    c: Coincident(g820,g821)
    c: Coincident(g821,g822)
    c: Coincident(g822,g823)
    c: Coincident(g823,g824)
    c: Coincident(g824,g825)
    c: Coincident(g825,g826)
    c: Coincident(g826,g827)
    c: Coincident(g827,g828)
    c: Coincident(g828,g829)
    c: Coincident(g829,g830)
    c: Coincident(g830,g831)
    c: Coincident(g831,g832)
    c: Coincident(g832,g833)
    c: Coincident(g833,g834)
    c: Coincident(g834,g835)
    c: Coincident(g835,g836)
    c: Coincident(g836,g837)
    c: Coincident(g837,g838)
    c: Coincident(g838,g839)
    c: Coincident(g839,g840)
    c: Coincident(g840,g841)
    c: Coincident(g841,g842)
    c: Coincident(g842,g843)
    c: Coincident(g843,g844)
    c: Coincident(g844,g845)
    c: Coincident(g845,g846)
    c: Coincident(g846,g847)
    c: Coincident(g847,g848)
    c: Coincident(g848,g849)
    c: Coincident(g849,g850)
    c: Coincident(g850,g851)
    c: Coincident(g851,g852)
    c: Coincident(g852,g853)
    c: Coincident(g853,g854)
    c: Coincident(g854,g855)
    c: Coincident(g855,g856)
    c: Coincident(g856,g857)
    c: Coincident(g857,g858)
    c: Coincident(g858,g859)
    c: Coincident(g859,g788)
FEATURE [Sketcher::SketchObject] Sketch032  label="VS001"
  ArcFitTolerance = 1e-06
  FullyConstrained = false
  MakeInternals = false
  Placement = pos=(48.725,7,55.85) rot=(0,1,1;3.14159rad)
  sketch-geometry (860):
    g0: BSplineCurve PolesCount=2 KnotsCount=2 Degree=1 IsPeriodic=0
    g1: BSplineCurve PolesCount=2 KnotsCount=2 Degree=1 IsPeriodic=0
    g2: BSplineCurve PolesCount=2 KnotsCount=2 Degree=1 IsPeriodic=0
    g3: BSplineCurve PolesCount=2 KnotsCount=2 Degree=1 IsPeriodic=0
    g4: BSplineCurve PolesCount=2 KnotsCount=2 Degree=1 IsPeriodic=0
    g5: BSplineCurve PolesCount=2 KnotsCount=2 Degree=1 IsPeriodic=0
    g6: BSplineCurve PolesCount=2 KnotsCount=2 Degree=1 IsPeriodic=0
    g7: BSplineCurve PolesCount=2 KnotsCount=2 Degree=1 IsPeriodic=0
    g8: BSplineCurve PolesCount=2 KnotsCount=2 Degree=1 IsPeriodic=0
    g9: BSplineCurve PolesCount=2 KnotsCount=2 Degree=1 IsPeriodic=0
    g10: BSplineCurve PolesCount=2 KnotsCount=2 Degree=1 IsPeriodic=0
    g11: BSplineCurve PolesCount=2 KnotsCount=2 Degree=1 IsPeriodic=0
    g12: BSplineCurve PolesCount=2 KnotsCount=2 Degree=1 IsPeriodic=0
    g13: BSplineCurve PolesCount=2 KnotsCount=2 Degree=1 IsPeriodic=0
    g14: BSplineCurve PolesCount=2 KnotsCount=2 Degree=1 IsPeriodic=0
    g15: BSplineCurve PolesCount=2 KnotsCount=2 Degree=1 IsPeriodic=0
    g16: BSplineCurve PolesCount=2 KnotsCount=2 Degree=1 IsPeriodic=0
    g17: BSplineCurve PolesCount=2 KnotsCount=2 Degree=1 IsPeriodic=0
    g18: BSplineCurve PolesCount=2 KnotsCount=2 Degree=1 IsPeriodic=0
    g19: BSplineCurve PolesCount=2 KnotsCount=2 Degree=1 IsPeriodic=0
    g20: BSplineCurve PolesCount=2 KnotsCount=2 Degree=1 IsPeriodic=0
    g21: BSplineCurve PolesCount=2 KnotsCount=2 Degree=1 IsPeriodic=0
    g22: BSplineCurve PolesCount=2 KnotsCount=2 Degree=1 IsPeriodic=0
    g23: BSplineCurve PolesCount=2 KnotsCount=2 Degree=1 IsPeriodic=0
    g24: BSplineCurve PolesCount=2 KnotsCount=2 Degree=1 IsPeriodic=0
    g25: BSplineCurve PolesCount=2 KnotsCount=2 Degree=1 IsPeriodic=0
    g26: BSplineCurve PolesCount=2 KnotsCount=2 Degree=1 IsPeriodic=0
    g27: BSplineCurve PolesCount=2 KnotsCount=2 Degree=1 IsPeriodic=0
    g28: BSplineCurve PolesCount=2 KnotsCount=2 Degree=1 IsPeriodic=0
    g29: BSplineCurve PolesCount=2 KnotsCount=2 Degree=1 IsPeriodic=0
    g30: BSplineCurve PolesCount=2 KnotsCount=2 Degree=1 IsPeriodic=0
    g31: BSplineCurve PolesCount=2 KnotsCount=2 Degree=1 IsPeriodic=0
    g32: BSplineCurve PolesCount=2 KnotsCount=2 Degree=1 IsPeriodic=0
    g33: BSplineCurve PolesCount=2 KnotsCount=2 Degree=1 IsPeriodic=0
    g34: BSplineCurve PolesCount=2 KnotsCount=2 Degree=1 IsPeriodic=0
    g35: BSplineCurve PolesCount=2 KnotsCount=2 Degree=1 IsPeriodic=0
    g36: BSplineCurve PolesCount=2 KnotsCount=2 Degree=1 IsPeriodic=0
    g37: BSplineCurve PolesCount=2 KnotsCount=2 Degree=1 IsPeriodic=0
    g38: BSplineCurve PolesCount=2 KnotsCount=2 Degree=1 IsPeriodic=0
    g39: BSplineCurve PolesCount=2 KnotsCount=2 Degree=1 IsPeriodic=0
    g40: BSplineCurve PolesCount=2 KnotsCount=2 Degree=1 IsPeriodic=0
    g41: BSplineCurve PolesCount=2 KnotsCount=2 Degree=1 IsPeriodic=0
    g42: BSplineCurve PolesCount=2 KnotsCount=2 Degree=1 IsPeriodic=0
    g43: BSplineCurve PolesCount=2 KnotsCount=2 Degree=1 IsPeriodic=0
    g44: BSplineCurve PolesCount=2 KnotsCount=2 Degree=1 IsPeriodic=0
    g45: BSplineCurve PolesCount=2 KnotsCount=2 Degree=1 IsPeriodic=0
    g46: BSplineCurve PolesCount=2 KnotsCount=2 Degree=1 IsPeriodic=0
    g47: BSplineCurve PolesCount=2 KnotsCount=2 Degree=1 IsPeriodic=0
    g48: BSplineCurve PolesCount=2 KnotsCount=2 Degree=1 IsPeriodic=0
    g49: BSplineCurve PolesCount=2 KnotsCount=2 Degree=1 IsPeriodic=0
    g50: BSplineCurve PolesCount=2 KnotsCount=2 Degree=1 IsPeriodic=0
    g51: BSplineCurve PolesCount=2 KnotsCount=2 Degree=1 IsPeriodic=0
    g52: BSplineCurve PolesCount=2 KnotsCount=2 Degree=1 IsPeriodic=0
    g53: BSplineCurve PolesCount=2 KnotsCount=2 Degree=1 IsPeriodic=0
    g54: BSplineCurve PolesCount=2 KnotsCount=2 Degree=1 IsPeriodic=0
    g55: BSplineCurve PolesCount=2 KnotsCount=2 Degree=1 IsPeriodic=0
    g56: BSplineCurve PolesCount=2 KnotsCount=2 Degree=1 IsPeriodic=0
    g57: BSplineCurve PolesCount=2 KnotsCount=2 Degree=1 IsPeriodic=0
    g58: BSplineCurve PolesCount=2 KnotsCount=2 Degree=1 IsPeriodic=0
    g59: BSplineCurve PolesCount=2 KnotsCount=2 Degree=1 IsPeriodic=0
    g60: BSplineCurve PolesCount=2 KnotsCount=2 Degree=1 IsPeriodic=0
    g61: BSplineCurve PolesCount=2 KnotsCount=2 Degree=1 IsPeriodic=0
    g62: BSplineCurve PolesCount=2 KnotsCount=2 Degree=1 IsPeriodic=0
    g63: BSplineCurve PolesCount=2 KnotsCount=2 Degree=1 IsPeriodic=0
    g64: BSplineCurve PolesCount=2 KnotsCount=2 Degree=1 IsPeriodic=0
    g65: BSplineCurve PolesCount=2 KnotsCount=2 Degree=1 IsPeriodic=0
    g66: BSplineCurve PolesCount=2 KnotsCount=2 Degree=1 IsPeriodic=0
    g67: BSplineCurve PolesCount=2 KnotsCount=2 Degree=1 IsPeriodic=0
    g68: BSplineCurve PolesCount=2 KnotsCount=2 Degree=1 IsPeriodic=0
    g69: BSplineCurve PolesCount=2 KnotsCount=2 Degree=1 IsPeriodic=0
    g70: BSplineCurve PolesCount=2 KnotsCount=2 Degree=1 IsPeriodic=0
    g71: BSplineCurve PolesCount=2 KnotsCount=2 Degree=1 IsPeriodic=0
    g72: BSplineCurve PolesCount=2 KnotsCount=2 Degree=1 IsPeriodic=0
    g73: BSplineCurve PolesCount=2 KnotsCount=2 Degree=1 IsPeriodic=0
    g74: BSplineCurve PolesCount=2 KnotsCount=2 Degree=1 IsPeriodic=0
    g75: BSplineCurve PolesCount=2 KnotsCount=2 Degree=1 IsPeriodic=0
    g76: BSplineCurve PolesCount=2 KnotsCount=2 Degree=1 IsPeriodic=0
    g77: BSplineCurve PolesCount=2 KnotsCount=2 Degree=1 IsPeriodic=0
    g78: BSplineCurve PolesCount=2 KnotsCount=2 Degree=1 IsPeriodic=0
    g79: BSplineCurve PolesCount=2 KnotsCount=2 Degree=1 IsPeriodic=0
    g80: BSplineCurve PolesCount=2 KnotsCount=2 Degree=1 IsPeriodic=0
    g81: BSplineCurve PolesCount=2 KnotsCount=2 Degree=1 IsPeriodic=0
    g82: BSplineCurve PolesCount=2 KnotsCount=2 Degree=1 IsPeriodic=0
    g83: BSplineCurve PolesCount=2 KnotsCount=2 Degree=1 IsPeriodic=0
    g84: BSplineCurve PolesCount=2 KnotsCount=2 Degree=1 IsPeriodic=0
    g85: BSplineCurve PolesCount=2 KnotsCount=2 Degree=1 IsPeriodic=0
    g86: BSplineCurve PolesCount=2 KnotsCount=2 Degree=1 IsPeriodic=0
    g87: BSplineCurve PolesCount=2 KnotsCount=2 Degree=1 IsPeriodic=0
    g88: BSplineCurve PolesCount=2 KnotsCount=2 Degree=1 IsPeriodic=0
    g89: BSplineCurve PolesCount=2 KnotsCount=2 Degree=1 IsPeriodic=0
    g90: BSplineCurve PolesCount=2 KnotsCount=2 Degree=1 IsPeriodic=0
    g91: BSplineCurve PolesCount=2 KnotsCount=2 Degree=1 IsPeriodic=0
    g92: BSplineCurve PolesCount=2 KnotsCount=2 Degree=1 IsPeriodic=0
    g93: BSplineCurve PolesCount=2 KnotsCount=2 Degree=1 IsPeriodic=0
    g94: BSplineCurve PolesCount=2 KnotsCount=2 Degree=1 IsPeriodic=0
    g95: BSplineCurve PolesCount=2 KnotsCount=2 Degree=1 IsPeriodic=0
    g96: BSplineCurve PolesCount=2 KnotsCount=2 Degree=1 IsPeriodic=0
    g97: BSplineCurve PolesCount=2 KnotsCount=2 Degree=1 IsPeriodic=0
    g98: BSplineCurve PolesCount=2 KnotsCount=2 Degree=1 IsPeriodic=0
    g99: BSplineCurve PolesCount=2 KnotsCount=2 Degree=1 IsPeriodic=0
    g100: BSplineCurve PolesCount=2 KnotsCount=2 Degree=1 IsPeriodic=0
    g101: BSplineCurve PolesCount=2 KnotsCount=2 Degree=1 IsPeriodic=0
    g102: BSplineCurve PolesCount=2 KnotsCount=2 Degree=1 IsPeriodic=0
    g103: BSplineCurve PolesCount=2 KnotsCount=2 Degree=1 IsPeriodic=0
    g104: BSplineCurve PolesCount=2 KnotsCount=2 Degree=1 IsPeriodic=0
    g105: BSplineCurve PolesCount=2 KnotsCount=2 Degree=1 IsPeriodic=0
    g106: BSplineCurve PolesCount=2 KnotsCount=2 Degree=1 IsPeriodic=0
    g107: BSplineCurve PolesCount=2 KnotsCount=2 Degree=1 IsPeriodic=0
    g108: BSplineCurve PolesCount=2 KnotsCount=2 Degree=1 IsPeriodic=0
    g109: BSplineCurve PolesCount=2 KnotsCount=2 Degree=1 IsPeriodic=0
    g110: BSplineCurve PolesCount=2 KnotsCount=2 Degree=1 IsPeriodic=0
    g111: BSplineCurve PolesCount=2 KnotsCount=2 Degree=1 IsPeriodic=0
    g112: BSplineCurve PolesCount=2 KnotsCount=2 Degree=1 IsPeriodic=0
    g113: BSplineCurve PolesCount=2 KnotsCount=2 Degree=1 IsPeriodic=0
    g114: BSplineCurve PolesCount=2 KnotsCount=2 Degree=1 IsPeriodic=0
    g115: BSplineCurve PolesCount=2 KnotsCount=2 Degree=1 IsPeriodic=0
    g116: BSplineCurve PolesCount=2 KnotsCount=2 Degree=1 IsPeriodic=0
    g117: BSplineCurve PolesCount=2 KnotsCount=2 Degree=1 IsPeriodic=0
    g118: BSplineCurve PolesCount=2 KnotsCount=2 Degree=1 IsPeriodic=0
    g119: BSplineCurve PolesCount=2 KnotsCount=2 Degree=1 IsPeriodic=0
    g120: BSplineCurve PolesCount=2 KnotsCount=2 Degree=1 IsPeriodic=0
    g121: BSplineCurve PolesCount=2 KnotsCount=2 Degree=1 IsPeriodic=0
    g122: BSplineCurve PolesCount=2 KnotsCount=2 Degree=1 IsPeriodic=0
    g123: BSplineCurve PolesCount=2 KnotsCount=2 Degree=1 IsPeriodic=0
    g124: BSplineCurve PolesCount=2 KnotsCount=2 Degree=1 IsPeriodic=0
    g125: BSplineCurve PolesCount=2 KnotsCount=2 Degree=1 IsPeriodic=0
    g126: BSplineCurve PolesCount=2 KnotsCount=2 Degree=1 IsPeriodic=0
    g127: BSplineCurve PolesCount=2 KnotsCount=2 Degree=1 IsPeriodic=0
    g128: BSplineCurve PolesCount=2 KnotsCount=2 Degree=1 IsPeriodic=0
    g129: BSplineCurve PolesCount=2 KnotsCount=2 Degree=1 IsPeriodic=0
    g130: BSplineCurve PolesCount=2 KnotsCount=2 Degree=1 IsPeriodic=0
    g131: BSplineCurve PolesCount=2 KnotsCount=2 Degree=1 IsPeriodic=0
    g132: BSplineCurve PolesCount=2 KnotsCount=2 Degree=1 IsPeriodic=0
    g133: BSplineCurve PolesCount=2 KnotsCount=2 Degree=1 IsPeriodic=0
    g134: BSplineCurve PolesCount=2 KnotsCount=2 Degree=1 IsPeriodic=0
    g135: BSplineCurve PolesCount=2 KnotsCount=2 Degree=1 IsPeriodic=0
    g136: BSplineCurve PolesCount=2 KnotsCount=2 Degree=1 IsPeriodic=0
    g137: BSplineCurve PolesCount=2 KnotsCount=2 Degree=1 IsPeriodic=0
    g138: BSplineCurve PolesCount=2 KnotsCount=2 Degree=1 IsPeriodic=0
    g139: BSplineCurve PolesCount=2 KnotsCount=2 Degree=1 IsPeriodic=0
    g140: BSplineCurve PolesCount=2 KnotsCount=2 Degree=1 IsPeriodic=0
    g141: BSplineCurve PolesCount=2 KnotsCount=2 Degree=1 IsPeriodic=0
    g142: BSplineCurve PolesCount=2 KnotsCount=2 Degree=1 IsPeriodic=0
    g143: BSplineCurve PolesCount=2 KnotsCount=2 Degree=1 IsPeriodic=0
    g144: BSplineCurve PolesCount=2 KnotsCount=2 Degree=1 IsPeriodic=0
    g145: BSplineCurve PolesCount=2 KnotsCount=2 Degree=1 IsPeriodic=0
    g146: BSplineCurve PolesCount=2 KnotsCount=2 Degree=1 IsPeriodic=0
    g147: BSplineCurve PolesCount=2 KnotsCount=2 Degree=1 IsPeriodic=0
    g148: BSplineCurve PolesCount=2 KnotsCount=2 Degree=1 IsPeriodic=0
    g149: BSplineCurve PolesCount=2 KnotsCount=2 Degree=1 IsPeriodic=0
    g150: BSplineCurve PolesCount=2 KnotsCount=2 Degree=1 IsPeriodic=0
    g151: BSplineCurve PolesCount=2 KnotsCount=2 Degree=1 IsPeriodic=0
    g152: BSplineCurve PolesCount=2 KnotsCount=2 Degree=1 IsPeriodic=0
    g153: BSplineCurve PolesCount=2 KnotsCount=2 Degree=1 IsPeriodic=0
    g154: BSplineCurve PolesCount=2 KnotsCount=2 Degree=1 IsPeriodic=0
    g155: BSplineCurve PolesCount=2 KnotsCount=2 Degree=1 IsPeriodic=0
    g156: BSplineCurve PolesCount=2 KnotsCount=2 Degree=1 IsPeriodic=0
    g157: BSplineCurve PolesCount=2 KnotsCount=2 Degree=1 IsPeriodic=0
    g158: BSplineCurve PolesCount=2 KnotsCount=2 Degree=1 IsPeriodic=0
    g159: BSplineCurve PolesCount=2 KnotsCount=2 Degree=1 IsPeriodic=0
    g160: BSplineCurve PolesCount=2 KnotsCount=2 Degree=1 IsPeriodic=0
    g161: BSplineCurve PolesCount=2 KnotsCount=2 Degree=1 IsPeriodic=0
    g162: BSplineCurve PolesCount=2 KnotsCount=2 Degree=1 IsPeriodic=0
    g163: BSplineCurve PolesCount=2 KnotsCount=2 Degree=1 IsPeriodic=0
    g164: BSplineCurve PolesCount=2 KnotsCount=2 Degree=1 IsPeriodic=0
    g165: BSplineCurve PolesCount=2 KnotsCount=2 Degree=1 IsPeriodic=0
    g166: BSplineCurve PolesCount=2 KnotsCount=2 Degree=1 IsPeriodic=0
    g167: BSplineCurve PolesCount=2 KnotsCount=2 Degree=1 IsPeriodic=0
    g168: BSplineCurve PolesCount=2 KnotsCount=2 Degree=1 IsPeriodic=0
    g169: BSplineCurve PolesCount=2 KnotsCount=2 Degree=1 IsPeriodic=0
    g170: BSplineCurve PolesCount=2 KnotsCount=2 Degree=1 IsPeriodic=0
    g171: BSplineCurve PolesCount=2 KnotsCount=2 Degree=1 IsPeriodic=0
    g172: BSplineCurve PolesCount=2 KnotsCount=2 Degree=1 IsPeriodic=0
    g173: BSplineCurve PolesCount=2 KnotsCount=2 Degree=1 IsPeriodic=0
    g174: BSplineCurve PolesCount=2 KnotsCount=2 Degree=1 IsPeriodic=0
    g175: BSplineCurve PolesCount=2 KnotsCount=2 Degree=1 IsPeriodic=0
    g176: BSplineCurve PolesCount=2 KnotsCount=2 Degree=1 IsPeriodic=0
    g177: BSplineCurve PolesCount=2 KnotsCount=2 Degree=1 IsPeriodic=0
    g178: BSplineCurve PolesCount=2 KnotsCount=2 Degree=1 IsPeriodic=0
    g179: BSplineCurve PolesCount=2 KnotsCount=2 Degree=1 IsPeriodic=0
    g180: BSplineCurve PolesCount=2 KnotsCount=2 Degree=1 IsPeriodic=0
    g181: BSplineCurve PolesCount=2 KnotsCount=2 Degree=1 IsPeriodic=0
    g182: BSplineCurve PolesCount=2 KnotsCount=2 Degree=1 IsPeriodic=0
    g183: BSplineCurve PolesCount=2 KnotsCount=2 Degree=1 IsPeriodic=0
    g184: BSplineCurve PolesCount=2 KnotsCount=2 Degree=1 IsPeriodic=0
    g185: BSplineCurve PolesCount=2 KnotsCount=2 Degree=1 IsPeriodic=0
    g186: BSplineCurve PolesCount=2 KnotsCount=2 Degree=1 IsPeriodic=0
    g187: BSplineCurve PolesCount=2 KnotsCount=2 Degree=1 IsPeriodic=0
    g188: BSplineCurve PolesCount=2 KnotsCount=2 Degree=1 IsPeriodic=0
    g189: BSplineCurve PolesCount=2 KnotsCount=2 Degree=1 IsPeriodic=0
    g190: BSplineCurve PolesCount=2 KnotsCount=2 Degree=1 IsPeriodic=0
    g191: BSplineCurve PolesCount=2 KnotsCount=2 Degree=1 IsPeriodic=0
    g192: BSplineCurve PolesCount=2 KnotsCount=2 Degree=1 IsPeriodic=0
    g193: BSplineCurve PolesCount=2 KnotsCount=2 Degree=1 IsPeriodic=0
    g194: BSplineCurve PolesCount=2 KnotsCount=2 Degree=1 IsPeriodic=0
    g195: BSplineCurve PolesCount=2 KnotsCount=2 Degree=1 IsPeriodic=0
    g196: BSplineCurve PolesCount=2 KnotsCount=2 Degree=1 IsPeriodic=0
    g197: BSplineCurve PolesCount=2 KnotsCount=2 Degree=1 IsPeriodic=0
    g198: BSplineCurve PolesCount=2 KnotsCount=2 Degree=1 IsPeriodic=0
    g199: BSplineCurve PolesCount=2 KnotsCount=2 Degree=1 IsPeriodic=0
    g200: BSplineCurve PolesCount=2 KnotsCount=2 Degree=1 IsPeriodic=0
    g201: BSplineCurve PolesCount=2 KnotsCount=2 Degree=1 IsPeriodic=0
    g202: BSplineCurve PolesCount=2 KnotsCount=2 Degree=1 IsPeriodic=0
    g203: BSplineCurve PolesCount=2 KnotsCount=2 Degree=1 IsPeriodic=0
    g204: BSplineCurve PolesCount=2 KnotsCount=2 Degree=1 IsPeriodic=0
    g205: BSplineCurve PolesCount=2 KnotsCount=2 Degree=1 IsPeriodic=0
    g206: BSplineCurve PolesCount=2 KnotsCount=2 Degree=1 IsPeriodic=0
    g207: BSplineCurve PolesCount=2 KnotsCount=2 Degree=1 IsPeriodic=0
    g208: BSplineCurve PolesCount=2 KnotsCount=2 Degree=1 IsPeriodic=0
    g209: BSplineCurve PolesCount=2 KnotsCount=2 Degree=1 IsPeriodic=0
    g210: BSplineCurve PolesCount=2 KnotsCount=2 Degree=1 IsPeriodic=0
    g211: BSplineCurve PolesCount=2 KnotsCount=2 Degree=1 IsPeriodic=0
    g212: BSplineCurve PolesCount=2 KnotsCount=2 Degree=1 IsPeriodic=0
    g213: BSplineCurve PolesCount=2 KnotsCount=2 Degree=1 IsPeriodic=0
    g214: BSplineCurve PolesCount=2 KnotsCount=2 Degree=1 IsPeriodic=0
    g215: BSplineCurve PolesCount=2 KnotsCount=2 Degree=1 IsPeriodic=0
    g216: BSplineCurve PolesCount=2 KnotsCount=2 Degree=1 IsPeriodic=0
    g217: BSplineCurve PolesCount=2 KnotsCount=2 Degree=1 IsPeriodic=0
    g218: BSplineCurve PolesCount=2 KnotsCount=2 Degree=1 IsPeriodic=0
    g219: BSplineCurve PolesCount=2 KnotsCount=2 Degree=1 IsPeriodic=0
    g220: BSplineCurve PolesCount=2 KnotsCount=2 Degree=1 IsPeriodic=0
    g221: BSplineCurve PolesCount=2 KnotsCount=2 Degree=1 IsPeriodic=0
    g222: BSplineCurve PolesCount=2 KnotsCount=2 Degree=1 IsPeriodic=0
    g223: BSplineCurve PolesCount=2 KnotsCount=2 Degree=1 IsPeriodic=0
    g224: BSplineCurve PolesCount=2 KnotsCount=2 Degree=1 IsPeriodic=0
    g225: BSplineCurve PolesCount=2 KnotsCount=2 Degree=1 IsPeriodic=0
    g226: BSplineCurve PolesCount=2 KnotsCount=2 Degree=1 IsPeriodic=0
    g227: BSplineCurve PolesCount=2 KnotsCount=2 Degree=1 IsPeriodic=0
    g228: BSplineCurve PolesCount=2 KnotsCount=2 Degree=1 IsPeriodic=0
    g229: BSplineCurve PolesCount=2 KnotsCount=2 Degree=1 IsPeriodic=0
    g230: BSplineCurve PolesCount=2 KnotsCount=2 Degree=1 IsPeriodic=0
    g231: BSplineCurve PolesCount=2 KnotsCount=2 Degree=1 IsPeriodic=0
    g232: BSplineCurve PolesCount=2 KnotsCount=2 Degree=1 IsPeriodic=0
    g233: BSplineCurve PolesCount=2 KnotsCount=2 Degree=1 IsPeriodic=0
    g234: BSplineCurve PolesCount=2 KnotsCount=2 Degree=1 IsPeriodic=0
    g235: BSplineCurve PolesCount=2 KnotsCount=2 Degree=1 IsPeriodic=0
    g236: BSplineCurve PolesCount=2 KnotsCount=2 Degree=1 IsPeriodic=0
    g237: BSplineCurve PolesCount=2 KnotsCount=2 Degree=1 IsPeriodic=0
    g238: BSplineCurve PolesCount=2 KnotsCount=2 Degree=1 IsPeriodic=0
    g239: BSplineCurve PolesCount=2 KnotsCount=2 Degree=1 IsPeriodic=0
    g240: BSplineCurve PolesCount=2 KnotsCount=2 Degree=1 IsPeriodic=0
    g241: BSplineCurve PolesCount=2 KnotsCount=2 Degree=1 IsPeriodic=0
    g242: BSplineCurve PolesCount=2 KnotsCount=2 Degree=1 IsPeriodic=0
    g243: BSplineCurve PolesCount=2 KnotsCount=2 Degree=1 IsPeriodic=0
    g244: BSplineCurve PolesCount=2 KnotsCount=2 Degree=1 IsPeriodic=0
    g245: BSplineCurve PolesCount=2 KnotsCount=2 Degree=1 IsPeriodic=0
    g246: BSplineCurve PolesCount=2 KnotsCount=2 Degree=1 IsPeriodic=0
    g247: BSplineCurve PolesCount=2 KnotsCount=2 Degree=1 IsPeriodic=0
    g248: BSplineCurve PolesCount=2 KnotsCount=2 Degree=1 IsPeriodic=0
    g249: BSplineCurve PolesCount=2 KnotsCount=2 Degree=1 IsPeriodic=0
    g250: BSplineCurve PolesCount=2 KnotsCount=2 Degree=1 IsPeriodic=0
    g251: BSplineCurve PolesCount=2 KnotsCount=2 Degree=1 IsPeriodic=0
    g252: BSplineCurve PolesCount=2 KnotsCount=2 Degree=1 IsPeriodic=0
    g253: BSplineCurve PolesCount=2 KnotsCount=2 Degree=1 IsPeriodic=0
    g254: BSplineCurve PolesCount=2 KnotsCount=2 Degree=1 IsPeriodic=0
    g255: BSplineCurve PolesCount=2 KnotsCount=2 Degree=1 IsPeriodic=0
    g256: BSplineCurve PolesCount=2 KnotsCount=2 Degree=1 IsPeriodic=0
    g257: BSplineCurve PolesCount=2 KnotsCount=2 Degree=1 IsPeriodic=0
    g258: BSplineCurve PolesCount=2 KnotsCount=2 Degree=1 IsPeriodic=0
    g259: BSplineCurve PolesCount=2 KnotsCount=2 Degree=1 IsPeriodic=0
    g260: BSplineCurve PolesCount=2 KnotsCount=2 Degree=1 IsPeriodic=0
    g261: BSplineCurve PolesCount=2 KnotsCount=2 Degree=1 IsPeriodic=0
    g262: BSplineCurve PolesCount=2 KnotsCount=2 Degree=1 IsPeriodic=0
    g263: BSplineCurve PolesCount=2 KnotsCount=2 Degree=1 IsPeriodic=0
    g264: BSplineCurve PolesCount=2 KnotsCount=2 Degree=1 IsPeriodic=0
    g265: BSplineCurve PolesCount=2 KnotsCount=2 Degree=1 IsPeriodic=0
    g266: BSplineCurve PolesCount=2 KnotsCount=2 Degree=1 IsPeriodic=0
    g267: BSplineCurve PolesCount=2 KnotsCount=2 Degree=1 IsPeriodic=0
    g268: BSplineCurve PolesCount=2 KnotsCount=2 Degree=1 IsPeriodic=0
    g269: BSplineCurve PolesCount=2 KnotsCount=2 Degree=1 IsPeriodic=0
    g270: BSplineCurve PolesCount=2 KnotsCount=2 Degree=1 IsPeriodic=0
    g271: BSplineCurve PolesCount=2 KnotsCount=2 Degree=1 IsPeriodic=0
    g272: BSplineCurve PolesCount=2 KnotsCount=2 Degree=1 IsPeriodic=0
    g273: BSplineCurve PolesCount=2 KnotsCount=2 Degree=1 IsPeriodic=0
    g274: BSplineCurve PolesCount=2 KnotsCount=2 Degree=1 IsPeriodic=0
    g275: BSplineCurve PolesCount=2 KnotsCount=2 Degree=1 IsPeriodic=0
    g276: BSplineCurve PolesCount=2 KnotsCount=2 Degree=1 IsPeriodic=0
    g277: BSplineCurve PolesCount=2 KnotsCount=2 Degree=1 IsPeriodic=0
    g278: BSplineCurve PolesCount=2 KnotsCount=2 Degree=1 IsPeriodic=0
    g279: BSplineCurve PolesCount=2 KnotsCount=2 Degree=1 IsPeriodic=0
    g280: BSplineCurve PolesCount=2 KnotsCount=2 Degree=1 IsPeriodic=0
    g281: BSplineCurve PolesCount=2 KnotsCount=2 Degree=1 IsPeriodic=0
    g282: BSplineCurve PolesCount=2 KnotsCount=2 Degree=1 IsPeriodic=0
    g283: BSplineCurve PolesCount=2 KnotsCount=2 Degree=1 IsPeriodic=0
    g284: BSplineCurve PolesCount=2 KnotsCount=2 Degree=1 IsPeriodic=0
    g285: BSplineCurve PolesCount=2 KnotsCount=2 Degree=1 IsPeriodic=0
    g286: BSplineCurve PolesCount=2 KnotsCount=2 Degree=1 IsPeriodic=0
    g287: BSplineCurve PolesCount=2 KnotsCount=2 Degree=1 IsPeriodic=0
    g288: BSplineCurve PolesCount=2 KnotsCount=2 Degree=1 IsPeriodic=0
    g289: BSplineCurve PolesCount=2 KnotsCount=2 Degree=1 IsPeriodic=0
    g290: BSplineCurve PolesCount=2 KnotsCount=2 Degree=1 IsPeriodic=0
    g291: BSplineCurve PolesCount=2 KnotsCount=2 Degree=1 IsPeriodic=0
    g292: BSplineCurve PolesCount=2 KnotsCount=2 Degree=1 IsPeriodic=0
    g293: BSplineCurve PolesCount=2 KnotsCount=2 Degree=1 IsPeriodic=0
    g294: BSplineCurve PolesCount=2 KnotsCount=2 Degree=1 IsPeriodic=0
    g295: BSplineCurve PolesCount=2 KnotsCount=2 Degree=1 IsPeriodic=0
    g296: BSplineCurve PolesCount=2 KnotsCount=2 Degree=1 IsPeriodic=0
    g297: BSplineCurve PolesCount=2 KnotsCount=2 Degree=1 IsPeriodic=0
    g298: BSplineCurve PolesCount=2 KnotsCount=2 Degree=1 IsPeriodic=0
    g299: BSplineCurve PolesCount=2 KnotsCount=2 Degree=1 IsPeriodic=0
    g300: BSplineCurve PolesCount=2 KnotsCount=2 Degree=1 IsPeriodic=0
    g301: BSplineCurve PolesCount=2 KnotsCount=2 Degree=1 IsPeriodic=0
    g302: BSplineCurve PolesCount=2 KnotsCount=2 Degree=1 IsPeriodic=0
    g303: BSplineCurve PolesCount=2 KnotsCount=2 Degree=1 IsPeriodic=0
    g304: BSplineCurve PolesCount=2 KnotsCount=2 Degree=1 IsPeriodic=0
    g305: BSplineCurve PolesCount=2 KnotsCount=2 Degree=1 IsPeriodic=0
    g306: BSplineCurve PolesCount=2 KnotsCount=2 Degree=1 IsPeriodic=0
    g307: BSplineCurve PolesCount=2 KnotsCount=2 Degree=1 IsPeriodic=0
    g308: BSplineCurve PolesCount=2 KnotsCount=2 Degree=1 IsPeriodic=0
    g309: BSplineCurve PolesCount=2 KnotsCount=2 Degree=1 IsPeriodic=0
    g310: BSplineCurve PolesCount=2 KnotsCount=2 Degree=1 IsPeriodic=0
    g311: BSplineCurve PolesCount=2 KnotsCount=2 Degree=1 IsPeriodic=0
    g312: BSplineCurve PolesCount=2 KnotsCount=2 Degree=1 IsPeriodic=0
    g313: BSplineCurve PolesCount=2 KnotsCount=2 Degree=1 IsPeriodic=0
    g314: BSplineCurve PolesCount=2 KnotsCount=2 Degree=1 IsPeriodic=0
    g315: BSplineCurve PolesCount=2 KnotsCount=2 Degree=1 IsPeriodic=0
    g316: BSplineCurve PolesCount=2 KnotsCount=2 Degree=1 IsPeriodic=0
    g317: BSplineCurve PolesCount=2 KnotsCount=2 Degree=1 IsPeriodic=0
    g318: BSplineCurve PolesCount=2 KnotsCount=2 Degree=1 IsPeriodic=0
    g319: BSplineCurve PolesCount=2 KnotsCount=2 Degree=1 IsPeriodic=0
    g320: BSplineCurve PolesCount=2 KnotsCount=2 Degree=1 IsPeriodic=0
    g321: BSplineCurve PolesCount=2 KnotsCount=2 Degree=1 IsPeriodic=0
    g322: BSplineCurve PolesCount=2 KnotsCount=2 Degree=1 IsPeriodic=0
    g323: BSplineCurve PolesCount=2 KnotsCount=2 Degree=1 IsPeriodic=0
    g324: BSplineCurve PolesCount=2 KnotsCount=2 Degree=1 IsPeriodic=0
    g325: BSplineCurve PolesCount=2 KnotsCount=2 Degree=1 IsPeriodic=0
    g326: BSplineCurve PolesCount=2 KnotsCount=2 Degree=1 IsPeriodic=0
    g327: BSplineCurve PolesCount=2 KnotsCount=2 Degree=1 IsPeriodic=0
    g328: BSplineCurve PolesCount=2 KnotsCount=2 Degree=1 IsPeriodic=0
    g329: BSplineCurve PolesCount=2 KnotsCount=2 Degree=1 IsPeriodic=0
    g330: BSplineCurve PolesCount=2 KnotsCount=2 Degree=1 IsPeriodic=0
    g331: BSplineCurve PolesCount=2 KnotsCount=2 Degree=1 IsPeriodic=0
    g332: BSplineCurve PolesCount=2 KnotsCount=2 Degree=1 IsPeriodic=0
    g333: BSplineCurve PolesCount=2 KnotsCount=2 Degree=1 IsPeriodic=0
    g334: BSplineCurve PolesCount=2 KnotsCount=2 Degree=1 IsPeriodic=0
    g335: BSplineCurve PolesCount=2 KnotsCount=2 Degree=1 IsPeriodic=0
    g336: BSplineCurve PolesCount=2 KnotsCount=2 Degree=1 IsPeriodic=0
    g337: BSplineCurve PolesCount=2 KnotsCount=2 Degree=1 IsPeriodic=0
    g338: BSplineCurve PolesCount=2 KnotsCount=2 Degree=1 IsPeriodic=0
    g339: BSplineCurve PolesCount=2 KnotsCount=2 Degree=1 IsPeriodic=0
    g340: BSplineCurve PolesCount=2 KnotsCount=2 Degree=1 IsPeriodic=0
    g341: BSplineCurve PolesCount=2 KnotsCount=2 Degree=1 IsPeriodic=0
    g342: BSplineCurve PolesCount=2 KnotsCount=2 Degree=1 IsPeriodic=0
    g343: BSplineCurve PolesCount=2 KnotsCount=2 Degree=1 IsPeriodic=0
    g344: BSplineCurve PolesCount=2 KnotsCount=2 Degree=1 IsPeriodic=0
    g345: BSplineCurve PolesCount=2 KnotsCount=2 Degree=1 IsPeriodic=0
    g346: BSplineCurve PolesCount=2 KnotsCount=2 Degree=1 IsPeriodic=0
    g347: BSplineCurve PolesCount=2 KnotsCount=2 Degree=1 IsPeriodic=0
    g348: BSplineCurve PolesCount=2 KnotsCount=2 Degree=1 IsPeriodic=0
    g349: BSplineCurve PolesCount=2 KnotsCount=2 Degree=1 IsPeriodic=0
    g350: BSplineCurve PolesCount=2 KnotsCount=2 Degree=1 IsPeriodic=0
    g351: BSplineCurve PolesCount=2 KnotsCount=2 Degree=1 IsPeriodic=0
    g352: BSplineCurve PolesCount=2 KnotsCount=2 Degree=1 IsPeriodic=0
    g353: BSplineCurve PolesCount=2 KnotsCount=2 Degree=1 IsPeriodic=0
    g354: BSplineCurve PolesCount=2 KnotsCount=2 Degree=1 IsPeriodic=0
    g355: BSplineCurve PolesCount=2 KnotsCount=2 Degree=1 IsPeriodic=0
    g356: BSplineCurve PolesCount=2 KnotsCount=2 Degree=1 IsPeriodic=0
    g357: BSplineCurve PolesCount=2 KnotsCount=2 Degree=1 IsPeriodic=0
    g358: BSplineCurve PolesCount=2 KnotsCount=2 Degree=1 IsPeriodic=0
    g359: BSplineCurve PolesCount=2 KnotsCount=2 Degree=1 IsPeriodic=0
    g360: BSplineCurve PolesCount=2 KnotsCount=2 Degree=1 IsPeriodic=0
    g361: BSplineCurve PolesCount=2 KnotsCount=2 Degree=1 IsPeriodic=0
    g362: BSplineCurve PolesCount=2 KnotsCount=2 Degree=1 IsPeriodic=0
    g363: BSplineCurve PolesCount=2 KnotsCount=2 Degree=1 IsPeriodic=0
    g364: BSplineCurve PolesCount=2 KnotsCount=2 Degree=1 IsPeriodic=0
    g365: BSplineCurve PolesCount=2 KnotsCount=2 Degree=1 IsPeriodic=0
    g366: BSplineCurve PolesCount=2 KnotsCount=2 Degree=1 IsPeriodic=0
    g367: BSplineCurve PolesCount=2 KnotsCount=2 Degree=1 IsPeriodic=0
    g368: BSplineCurve PolesCount=2 KnotsCount=2 Degree=1 IsPeriodic=0
    g369: BSplineCurve PolesCount=2 KnotsCount=2 Degree=1 IsPeriodic=0
    g370: BSplineCurve PolesCount=2 KnotsCount=2 Degree=1 IsPeriodic=0
    g371: BSplineCurve PolesCount=2 KnotsCount=2 Degree=1 IsPeriodic=0
    g372: BSplineCurve PolesCount=2 KnotsCount=2 Degree=1 IsPeriodic=0
    g373: BSplineCurve PolesCount=2 KnotsCount=2 Degree=1 IsPeriodic=0
    g374: BSplineCurve PolesCount=2 KnotsCount=2 Degree=1 IsPeriodic=0
    g375: BSplineCurve PolesCount=2 KnotsCount=2 Degree=1 IsPeriodic=0
    g376: BSplineCurve PolesCount=2 KnotsCount=2 Degree=1 IsPeriodic=0
    g377: BSplineCurve PolesCount=2 KnotsCount=2 Degree=1 IsPeriodic=0
    g378: BSplineCurve PolesCount=2 KnotsCount=2 Degree=1 IsPeriodic=0
    g379: BSplineCurve PolesCount=2 KnotsCount=2 Degree=1 IsPeriodic=0
    g380: BSplineCurve PolesCount=2 KnotsCount=2 Degree=1 IsPeriodic=0
    g381: BSplineCurve PolesCount=2 KnotsCount=2 Degree=1 IsPeriodic=0
    g382: BSplineCurve PolesCount=2 KnotsCount=2 Degree=1 IsPeriodic=0
    g383: BSplineCurve PolesCount=2 KnotsCount=2 Degree=1 IsPeriodic=0
    g384: BSplineCurve PolesCount=2 KnotsCount=2 Degree=1 IsPeriodic=0
    g385: BSplineCurve PolesCount=2 KnotsCount=2 Degree=1 IsPeriodic=0
    g386: BSplineCurve PolesCount=2 KnotsCount=2 Degree=1 IsPeriodic=0
    g387: BSplineCurve PolesCount=2 KnotsCount=2 Degree=1 IsPeriodic=0
    g388: BSplineCurve PolesCount=2 KnotsCount=2 Degree=1 IsPeriodic=0
    g389: BSplineCurve PolesCount=2 KnotsCount=2 Degree=1 IsPeriodic=0
    g390: BSplineCurve PolesCount=2 KnotsCount=2 Degree=1 IsPeriodic=0
    g391: BSplineCurve PolesCount=2 KnotsCount=2 Degree=1 IsPeriodic=0
    g392: BSplineCurve PolesCount=2 KnotsCount=2 Degree=1 IsPeriodic=0
    g393: BSplineCurve PolesCount=2 KnotsCount=2 Degree=1 IsPeriodic=0
    g394: BSplineCurve PolesCount=2 KnotsCount=2 Degree=1 IsPeriodic=0
    g395: BSplineCurve PolesCount=2 KnotsCount=2 Degree=1 IsPeriodic=0
    g396: BSplineCurve PolesCount=2 KnotsCount=2 Degree=1 IsPeriodic=0
    g397: BSplineCurve PolesCount=2 KnotsCount=2 Degree=1 IsPeriodic=0
    g398: BSplineCurve PolesCount=2 KnotsCount=2 Degree=1 IsPeriodic=0
    g399: BSplineCurve PolesCount=2 KnotsCount=2 Degree=1 IsPeriodic=0
    ... +460 more geometry lines
  constraints (860):
    c: Coincident(g0,g1)
    c: Coincident(g1,g2)
    c: Coincident(g2,g3)
    c: Coincident(g3,g4)
    c: Coincident(g4,g5)
    c: Coincident(g5,g6)
    c: Coincident(g6,g7)
    c: Coincident(g7,g8)
    c: Coincident(g8,g9)
    c: Coincident(g9,g10)
    c: Coincident(g10,g11)
    c: Coincident(g11,g12)
    c: Coincident(g12,g13)
    c: Coincident(g13,g14)
    c: Coincident(g14,g15)
    c: Coincident(g15,g16)
    c: Coincident(g16,g17)
    c: Coincident(g17,g18)
    c: Coincident(g18,g19)
    c: Coincident(g19,g20)
    c: Coincident(g20,g21)
    c: Coincident(g21,g22)
    c: Coincident(g22,g23)
    c: Coincident(g23,g24)
    c: Coincident(g24,g25)
    c: Coincident(g25,g26)
    c: Coincident(g26,g27)
    c: Coincident(g27,g28)
    c: Coincident(g28,g29)
    c: Coincident(g29,g30)
    c: Coincident(g30,g31)
    c: Coincident(g31,g32)
    c: Coincident(g32,g33)
    c: Coincident(g33,g34)
    c: Coincident(g34,g35)
    c: Coincident(g35,g36)
    c: Coincident(g36,g37)
    c: Coincident(g37,g38)
    c: Coincident(g38,g39)
    c: Coincident(g39,g40)
    c: Coincident(g40,g41)
    c: Coincident(g41,g42)
    c: Coincident(g42,g43)
    c: Coincident(g43,g44)
    c: Coincident(g44,g45)
    c: Coincident(g45,g46)
    c: Coincident(g46,g47)
    c: Coincident(g47,g48)
    c: Coincident(g48,g49)
    c: Coincident(g49,g50)
    c: Coincident(g50,g51)
    c: Coincident(g51,g52)
    c: Coincident(g52,g53)
    c: Coincident(g53,g54)
    c: Coincident(g54,g55)
    c: Coincident(g55,g56)
    c: Coincident(g56,g57)
    c: Coincident(g57,g58)
    c: Coincident(g58,g59)
    c: Coincident(g59,g60)
    c: Coincident(g60,g61)
    c: Coincident(g61,g62)
    c: Coincident(g62,g63)
    c: Coincident(g63,g64)
    c: Coincident(g64,g65)
    c: Coincident(g65,g66)
    c: Coincident(g66,g67)
    c: Coincident(g67,g68)
    c: Coincident(g68,g69)
    c: Coincident(g69,g70)
    c: Coincident(g70,g71)
    c: Coincident(g71,g72)
    c: Coincident(g72,g73)
    c: Coincident(g73,g74)
    c: Coincident(g74,g75)
    c: Coincident(g75,g76)
    c: Coincident(g76,g77)
    c: Coincident(g77,g78)
    c: Coincident(g78,g79)
    c: Coincident(g79,g80)
    c: Coincident(g80,g81)
    c: Coincident(g81,g82)
    c: Coincident(g82,g83)
    c: Coincident(g83,g84)
    c: Coincident(g84,g85)
    c: Coincident(g85,g86)
    c: Coincident(g86,g87)
    c: Coincident(g87,g0)
    c: Coincident(g88,g89)
    c: Coincident(g89,g90)
    c: Coincident(g90,g91)
    c: Coincident(g91,g92)
    c: Coincident(g92,g93)
    c: Coincident(g93,g94)
    c: Coincident(g94,g95)
    c: Coincident(g95,g96)
    c: Coincident(g96,g97)
    c: Coincident(g97,g98)
    c: Coincident(g98,g99)
    c: Coincident(g99,g100)
    c: Coincident(g100,g101)
    c: Coincident(g101,g102)
    c: Coincident(g102,g103)
    c: Coincident(g103,g104)
    c: Coincident(g104,g105)
    c: Coincident(g105,g106)
    c: Coincident(g106,g107)
    c: Coincident(g107,g108)
    c: Coincident(g108,g109)
    c: Coincident(g109,g110)
    c: Coincident(g110,g111)
    c: Coincident(g111,g112)
    c: Coincident(g112,g113)
    c: Coincident(g113,g114)
    c: Coincident(g114,g115)
    c: Coincident(g115,g116)
    c: Coincident(g116,g117)
    c: Coincident(g117,g118)
    c: Coincident(g118,g119)
    c: Coincident(g119,g120)
    c: Coincident(g120,g121)
    c: Coincident(g121,g122)
    c: Coincident(g122,g123)
    c: Coincident(g123,g124)
    c: Coincident(g124,g125)
    c: Coincident(g125,g126)
    c: Coincident(g126,g127)
    c: Coincident(g127,g88)
    c: Coincident(g128,g129)
    c: Coincident(g129,g130)
    c: Coincident(g130,g131)
    c: Coincident(g131,g132)
    c: Coincident(g132,g133)
    c: Coincident(g133,g134)
    c: Coincident(g134,g135)
    c: Coincident(g135,g136)
    c: Coincident(g136,g137)
    c: Coincident(g137,g138)
    c: Coincident(g138,g139)
    c: Coincident(g139,g140)
    c: Coincident(g140,g141)
    c: Coincident(g141,g142)
    c: Coincident(g142,g143)
    c: Coincident(g143,g144)
    c: Coincident(g144,g145)
    c: Coincident(g145,g146)
    c: Coincident(g146,g147)
    c: Coincident(g147,g148)
    c: Coincident(g148,g149)
    c: Coincident(g149,g150)
    c: Coincident(g150,g151)
    c: Coincident(g151,g152)
    c: Coincident(g152,g153)
    c: Coincident(g153,g154)
    c: Coincident(g154,g155)
    c: Coincident(g155,g156)
    c: Coincident(g156,g157)
    c: Coincident(g157,g158)
    c: Coincident(g158,g159)
    c: Coincident(g159,g160)
    c: Coincident(g160,g161)
    c: Coincident(g161,g162)
    c: Coincident(g162,g163)
    c: Coincident(g163,g164)
    c: Coincident(g164,g165)
    c: Coincident(g165,g166)
    c: Coincident(g166,g167)
    c: Coincident(g167,g168)
    c: Coincident(g168,g169)
    c: Coincident(g169,g170)
    c: Coincident(g170,g171)
    c: Coincident(g171,g172)
    c: Coincident(g172,g173)
    c: Coincident(g173,g174)
    c: Coincident(g174,g175)
    c: Coincident(g175,g176)
    c: Coincident(g176,g177)
    c: Coincident(g177,g178)
    c: Coincident(g178,g179)
    c: Coincident(g179,g180)
    c: Coincident(g180,g181)
    c: Coincident(g181,g182)
    c: Coincident(g182,g183)
    c: Coincident(g183,g184)
    c: Coincident(g184,g185)
    c: Coincident(g185,g186)
    c: Coincident(g186,g187)
    c: Coincident(g187,g188)
    c: Coincident(g188,g189)
    c: Coincident(g189,g190)
    c: Coincident(g190,g191)
    c: Coincident(g191,g192)
    c: Coincident(g192,g193)
    c: Coincident(g193,g194)
    c: Coincident(g194,g195)
    c: Coincident(g195,g196)
    c: Coincident(g196,g197)
    c: Coincident(g197,g198)
    c: Coincident(g198,g199)
    c: Coincident(g199,g200)
    c: Coincident(g200,g201)
    c: Coincident(g201,g202)
    c: Coincident(g202,g203)
    c: Coincident(g203,g204)
    c: Coincident(g204,g205)
    c: Coincident(g205,g206)
    c: Coincident(g206,g207)
    c: Coincident(g207,g208)
    c: Coincident(g208,g209)
    c: Coincident(g209,g210)
    c: Coincident(g210,g211)
    c: Coincident(g211,g212)
    c: Coincident(g212,g213)
    c: Coincident(g213,g214)
    c: Coincident(g214,g215)
    c: Coincident(g215,g216)
    c: Coincident(g216,g217)
    c: Coincident(g217,g218)
    c: Coincident(g218,g219)
    c: Coincident(g219,g220)
    c: Coincident(g220,g221)
    c: Coincident(g221,g222)
    c: Coincident(g222,g223)
    c: Coincident(g223,g224)
    c: Coincident(g224,g225)
    c: Coincident(g225,g226)
    c: Coincident(g226,g227)
    c: Coincident(g227,g228)
    c: Coincident(g228,g229)
    c: Coincident(g229,g230)
    c: Coincident(g230,g231)
    c: Coincident(g231,g232)
    c: Coincident(g232,g233)
    c: Coincident(g233,g234)
    c: Coincident(g234,g235)
    c: Coincident(g235,g236)
    c: Coincident(g236,g237)
    c: Coincident(g237,g238)
    c: Coincident(g238,g239)
    c: Coincident(g239,g128)
    c: Coincident(g240,g241)
    c: Coincident(g241,g242)
    c: Coincident(g242,g243)
    c: Coincident(g243,g244)
    c: Coincident(g244,g245)
    c: Coincident(g245,g246)
    c: Coincident(g246,g247)
    c: Coincident(g247,g248)
    c: Coincident(g248,g249)
    c: Coincident(g249,g250)
    c: Coincident(g250,g251)
    c: Coincident(g251,g252)
    c: Coincident(g252,g253)
    c: Coincident(g253,g254)
    c: Coincident(g254,g255)
    c: Coincident(g255,g256)
    c: Coincident(g256,g257)
    c: Coincident(g257,g258)
    c: Coincident(g258,g259)
    c: Coincident(g259,g260)
    c: Coincident(g260,g261)
    c: Coincident(g261,g262)
    c: Coincident(g262,g263)
    c: Coincident(g263,g264)
    c: Coincident(g264,g265)
    c: Coincident(g265,g266)
    c: Coincident(g266,g267)
    c: Coincident(g267,g268)
    c: Coincident(g268,g269)
    c: Coincident(g269,g270)
    c: Coincident(g270,g271)
    c: Coincident(g271,g272)
    c: Coincident(g272,g273)
    c: Coincident(g273,g274)
    c: Coincident(g274,g275)
    c: Coincident(g275,g276)
    c: Coincident(g276,g277)
    c: Coincident(g277,g278)
    c: Coincident(g278,g279)
    c: Coincident(g279,g280)
    c: Coincident(g280,g281)
    c: Coincident(g281,g282)
    c: Coincident(g282,g283)
    c: Coincident(g283,g284)
    c: Coincident(g284,g285)
    c: Coincident(g285,g286)
    c: Coincident(g286,g287)
    c: Coincident(g287,g240)
    c: Coincident(g288,g289)
    c: Coincident(g289,g290)
    c: Coincident(g290,g291)
    c: Coincident(g291,g292)
    c: Coincident(g292,g293)
    c: Coincident(g293,g294)
    c: Coincident(g294,g295)
    c: Coincident(g295,g296)
    c: Coincident(g296,g297)
    c: Coincident(g297,g298)
    c: Coincident(g298,g299)
    c: Coincident(g299,g300)
    c: Coincident(g300,g301)
    c: Coincident(g301,g302)
    c: Coincident(g302,g303)
    c: Coincident(g303,g304)
    c: Coincident(g304,g305)
    c: Coincident(g305,g306)
    c: Coincident(g306,g307)
    c: Coincident(g307,g308)
    c: Coincident(g308,g309)
    c: Coincident(g309,g310)
    c: Coincident(g310,g311)
    c: Coincident(g311,g288)
    c: Coincident(g312,g313)
    c: Coincident(g313,g314)
    c: Coincident(g314,g315)
    c: Coincident(g315,g316)
    c: Coincident(g316,g317)
    c: Coincident(g317,g318)
    c: Coincident(g318,g319)
    c: Coincident(g319,g320)
    c: Coincident(g320,g321)
    c: Coincident(g321,g322)
    c: Coincident(g322,g323)
    c: Coincident(g323,g324)
    c: Coincident(g324,g325)
    c: Coincident(g325,g326)
    c: Coincident(g326,g327)
    c: Coincident(g327,g312)
    c: Coincident(g328,g329)
    c: Coincident(g329,g330)
    c: Coincident(g330,g331)
    c: Coincident(g331,g332)
    c: Coincident(g332,g333)
    c: Coincident(g333,g334)
    c: Coincident(g334,g335)
    c: Coincident(g335,g336)
    c: Coincident(g336,g337)
    c: Coincident(g337,g338)
    c: Coincident(g338,g339)
    c: Coincident(g339,g340)
    c: Coincident(g340,g341)
    c: Coincident(g341,g342)
    c: Coincident(g342,g343)
    c: Coincident(g343,g344)
    c: Coincident(g344,g345)
    c: Coincident(g345,g346)
    c: Coincident(g346,g347)
    c: Coincident(g347,g348)
    c: Coincident(g348,g349)
    c: Coincident(g349,g350)
    c: Coincident(g350,g351)
    c: Coincident(g351,g352)
    c: Coincident(g352,g353)
    c: Coincident(g353,g354)
    c: Coincident(g354,g355)
    c: Coincident(g355,g356)
    c: Coincident(g356,g357)
    c: Coincident(g357,g358)
    c: Coincident(g358,g359)
    c: Coincident(g359,g360)
    c: Coincident(g360,g361)
    c: Coincident(g361,g362)
    c: Coincident(g362,g363)
    c: Coincident(g363,g364)
    c: Coincident(g364,g365)
    c: Coincident(g365,g366)
    c: Coincident(g366,g367)
    c: Coincident(g367,g368)
    c: Coincident(g368,g369)
    c: Coincident(g369,g370)
    c: Coincident(g370,g371)
    c: Coincident(g371,g372)
    c: Coincident(g372,g373)
    c: Coincident(g373,g374)
    c: Coincident(g374,g375)
    c: Coincident(g375,g376)
    c: Coincident(g376,g377)
    c: Coincident(g377,g378)
    c: Coincident(g378,g379)
    c: Coincident(g379,g380)
    c: Coincident(g380,g381)
    c: Coincident(g381,g382)
    c: Coincident(g382,g383)
    c: Coincident(g383,g384)
    c: Coincident(g384,g385)
    c: Coincident(g385,g386)
    c: Coincident(g386,g387)
    c: Coincident(g387,g388)
    c: Coincident(g388,g389)
    c: Coincident(g389,g390)
    c: Coincident(g390,g391)
    c: Coincident(g391,g392)
    c: Coincident(g392,g393)
    c: Coincident(g393,g394)
    c: Coincident(g394,g395)
    c: Coincident(g395,g396)
    c: Coincident(g396,g397)
    c: Coincident(g397,g398)
    c: Coincident(g398,g399)
    c: Coincident(g399,g328)
    c: Coincident(g400,g401)
    c: Coincident(g401,g402)
    c: Coincident(g402,g403)
    c: Coincident(g403,g404)
    c: Coincident(g404,g405)
    c: Coincident(g405,g406)
    c: Coincident(g406,g407)
    c: Coincident(g407,g408)
    c: Coincident(g408,g409)
    c: Coincident(g409,g410)
    c: Coincident(g410,g411)
    c: Coincident(g411,g412)
    c: Coincident(g412,g413)
    c: Coincident(g413,g414)
    c: Coincident(g414,g415)
    c: Coincident(g415,g416)
    c: Coincident(g416,g417)
    c: Coincident(g417,g418)
    c: Coincident(g418,g419)
    c: Coincident(g419,g420)
    c: Coincident(g420,g421)
    c: Coincident(g421,g422)
    c: Coincident(g422,g423)
    c: Coincident(g423,g400)
    c: Coincident(g424,g425)
    c: Coincident(g425,g426)
    c: Coincident(g426,g427)
    c: Coincident(g427,g428)
    c: Coincident(g428,g429)
    c: Coincident(g429,g430)
    c: Coincident(g430,g431)
    c: Coincident(g431,g432)
    c: Coincident(g432,g433)
    c: Coincident(g433,g434)
    c: Coincident(g434,g435)
    c: Coincident(g435,g436)
    c: Coincident(g436,g437)
    c: Coincident(g437,g438)
    c: Coincident(g438,g439)
    c: Coincident(g439,g440)
    c: Coincident(g440,g441)
    c: Coincident(g441,g442)
    c: Coincident(g442,g443)
    c: Coincident(g443,g444)
    c: Coincident(g444,g445)
    c: Coincident(g445,g446)
    c: Coincident(g446,g447)
    c: Coincident(g447,g448)
    c: Coincident(g448,g449)
    c: Coincident(g449,g450)
    c: Coincident(g450,g451)
    c: Coincident(g451,g452)
    c: Coincident(g452,g453)
    c: Coincident(g453,g454)
    c: Coincident(g454,g455)
    c: Coincident(g455,g456)
    c: Coincident(g456,g457)
    c: Coincident(g457,g458)
    c: Coincident(g458,g459)
    c: Coincident(g459,g460)
    c: Coincident(g460,g461)
    c: Coincident(g461,g462)
    c: Coincident(g462,g463)
    c: Coincident(g463,g464)
    c: Coincident(g464,g465)
    c: Coincident(g465,g466)
    c: Coincident(g466,g467)
    c: Coincident(g467,g468)
    c: Coincident(g468,g469)
    c: Coincident(g469,g470)
    c: Coincident(g470,g471)
    c: Coincident(g471,g472)
    c: Coincident(g472,g473)
    c: Coincident(g473,g474)
    c: Coincident(g474,g475)
    c: Coincident(g475,g476)
    c: Coincident(g476,g477)
    c: Coincident(g477,g478)
    c: Coincident(g478,g479)
    c: Coincident(g479,g424)
    c: Coincident(g480,g481)
    c: Coincident(g481,g482)
    c: Coincident(g482,g483)
    c: Coincident(g483,g484)
    c: Coincident(g484,g485)
    c: Coincident(g485,g486)
    c: Coincident(g486,g487)
    c: Coincident(g487,g488)
    c: Coincident(g488,g489)
    c: Coincident(g489,g490)
    c: Coincident(g490,g491)
    c: Coincident(g491,g492)
    c: Coincident(g492,g493)
    c: Coincident(g493,g494)
    c: Coincident(g494,g495)
    c: Coincident(g495,g480)
    c: Coincident(g496,g497)
    c: Coincident(g497,g498)
    c: Coincident(g498,g499)
    c: Coincident(g499,g500)
    c: Coincident(g500,g501)
    c: Coincident(g501,g502)
    c: Coincident(g502,g503)
    c: Coincident(g503,g504)
    c: Coincident(g504,g505)
    c: Coincident(g505,g506)
    c: Coincident(g506,g507)
    c: Coincident(g507,g508)
    c: Coincident(g508,g509)
    c: Coincident(g509,g510)
    c: Coincident(g510,g511)
    c: Coincident(g511,g512)
    c: Coincident(g512,g513)
    c: Coincident(g513,g514)
    c: Coincident(g514,g515)
    c: Coincident(g515,g516)
    c: Coincident(g516,g517)
    c: Coincident(g517,g518)
    c: Coincident(g518,g519)
    c: Coincident(g519,g520)
    c: Coincident(g520,g521)
    c: Coincident(g521,g522)
    c: Coincident(g522,g523)
    c: Coincident(g523,g524)
    c: Coincident(g524,g525)
    c: Coincident(g525,g526)
    c: Coincident(g526,g527)
    c: Coincident(g527,g528)
    c: Coincident(g528,g529)
    c: Coincident(g529,g530)
    c: Coincident(g530,g531)
    c: Coincident(g531,g532)
    c: Coincident(g532,g533)
    c: Coincident(g533,g534)
    c: Coincident(g534,g535)
    c: Coincident(g535,g496)
    c: Coincident(g536,g537)
    c: Coincident(g537,g538)
    c: Coincident(g538,g539)
    c: Coincident(g539,g540)
    c: Coincident(g540,g541)
    c: Coincident(g541,g542)
    c: Coincident(g542,g543)
    c: Coincident(g543,g544)
    c: Coincident(g544,g545)
    c: Coincident(g545,g546)
    c: Coincident(g546,g547)
    c: Coincident(g547,g548)
    c: Coincident(g548,g549)
    c: Coincident(g549,g550)
    c: Coincident(g550,g551)
    c: Coincident(g551,g552)
    c: Coincident(g552,g553)
    c: Coincident(g553,g554)
    c: Coincident(g554,g555)
    c: Coincident(g555,g556)
    c: Coincident(g556,g557)
    c: Coincident(g557,g558)
    c: Coincident(g558,g559)
    c: Coincident(g559,g560)
    c: Coincident(g560,g561)
    c: Coincident(g561,g562)
    c: Coincident(g562,g563)
    c: Coincident(g563,g564)
    c: Coincident(g564,g565)
    c: Coincident(g565,g566)
    c: Coincident(g566,g567)
    c: Coincident(g567,g568)
    c: Coincident(g568,g569)
    c: Coincident(g569,g570)
    c: Coincident(g570,g571)
    c: Coincident(g571,g572)
    c: Coincident(g572,g573)
    c: Coincident(g573,g574)
    c: Coincident(g574,g575)
    c: Coincident(g575,g536)
    c: Coincident(g576,g577)
    c: Coincident(g577,g578)
    c: Coincident(g578,g579)
    c: Coincident(g579,g580)
    c: Coincident(g580,g581)
    c: Coincident(g581,g582)
    c: Coincident(g582,g583)
    c: Coincident(g583,g584)
    c: Coincident(g584,g585)
    c: Coincident(g585,g586)
    c: Coincident(g586,g587)
    c: Coincident(g587,g576)
    c: Coincident(g588,g589)
    c: Coincident(g589,g590)
    c: Coincident(g590,g591)
    c: Coincident(g591,g592)
    c: Coincident(g592,g593)
    c: Coincident(g593,g594)
    c: Coincident(g594,g595)
    c: Coincident(g595,g596)
    c: Coincident(g596,g597)
    c: Coincident(g597,g598)
    c: Coincident(g598,g599)
    c: Coincident(g599,g600)
    c: Coincident(g600,g601)
    c: Coincident(g601,g602)
    c: Coincident(g602,g603)
    c: Coincident(g603,g604)
    c: Coincident(g604,g605)
    c: Coincident(g605,g606)
    c: Coincident(g606,g607)
    c: Coincident(g607,g608)
    c: Coincident(g608,g609)
    c: Coincident(g609,g610)
    c: Coincident(g610,g611)
    c: Coincident(g611,g612)
    c: Coincident(g612,g613)
    c: Coincident(g613,g614)
    c: Coincident(g614,g615)
    c: Coincident(g615,g616)
    c: Coincident(g616,g617)
    c: Coincident(g617,g618)
    c: Coincident(g618,g619)
    c: Coincident(g619,g620)
    c: Coincident(g620,g621)
    c: Coincident(g621,g622)
    c: Coincident(g622,g623)
    c: Coincident(g623,g624)
    c: Coincident(g624,g625)
    c: Coincident(g625,g626)
    c: Coincident(g626,g627)
    c: Coincident(g627,g628)
    c: Coincident(g628,g629)
    c: Coincident(g629,g630)
    c: Coincident(g630,g631)
    c: Coincident(g631,g632)
    c: Coincident(g632,g633)
    c: Coincident(g633,g634)
    c: Coincident(g634,g635)
    c: Coincident(g635,g636)
    c: Coincident(g636,g637)
    c: Coincident(g637,g638)
    c: Coincident(g638,g639)
    c: Coincident(g639,g640)
    c: Coincident(g640,g641)
    c: Coincident(g641,g642)
    c: Coincident(g642,g643)
    c: Coincident(g643,g644)
    c: Coincident(g644,g645)
    c: Coincident(g645,g646)
    c: Coincident(g646,g647)
    c: Coincident(g647,g648)
    c: Coincident(g648,g649)
    c: Coincident(g649,g650)
    c: Coincident(g650,g651)
    c: Coincident(g651,g652)
    c: Coincident(g652,g653)
    c: Coincident(g653,g654)
    c: Coincident(g654,g655)
    c: Coincident(g655,g656)
    c: Coincident(g656,g657)
    c: Coincident(g657,g658)
    c: Coincident(g658,g659)
    c: Coincident(g659,g660)
    c: Coincident(g660,g661)
    c: Coincident(g661,g662)
    c: Coincident(g662,g663)
    c: Coincident(g663,g664)
    c: Coincident(g664,g665)
    c: Coincident(g665,g666)
    c: Coincident(g666,g667)
    c: Coincident(g667,g668)
    c: Coincident(g668,g669)
    c: Coincident(g669,g670)
    c: Coincident(g670,g671)
    c: Coincident(g671,g672)
    c: Coincident(g672,g673)
    c: Coincident(g673,g674)
    c: Coincident(g674,g675)
    c: Coincident(g675,g588)
    c: Coincident(g676,g677)
    c: Coincident(g677,g678)
    c: Coincident(g678,g679)
    c: Coincident(g679,g680)
    c: Coincident(g680,g681)
    c: Coincident(g681,g682)
    c: Coincident(g682,g683)
    c: Coincident(g683,g684)
    c: Coincident(g684,g685)
    c: Coincident(g685,g686)
    c: Coincident(g686,g687)
    c: Coincident(g687,g688)
    c: Coincident(g688,g689)
    c: Coincident(g689,g690)
    c: Coincident(g690,g691)
    c: Coincident(g691,g676)
    c: Coincident(g692,g693)
    c: Coincident(g693,g694)
    c: Coincident(g694,g695)
    c: Coincident(g695,g696)
    c: Coincident(g696,g697)
    c: Coincident(g697,g698)
    c: Coincident(g698,g699)
    c: Coincident(g699,g700)
    c: Coincident(g700,g701)
    c: Coincident(g701,g702)
    c: Coincident(g702,g703)
    c: Coincident(g703,g704)
    c: Coincident(g704,g705)
    c: Coincident(g705,g706)
    c: Coincident(g706,g707)
    c: Coincident(g707,g708)
    c: Coincident(g708,g709)
    c: Coincident(g709,g710)
    c: Coincident(g710,g711)
    c: Coincident(g711,g712)
    c: Coincident(g712,g713)
    c: Coincident(g713,g714)
    c: Coincident(g714,g715)
    c: Coincident(g715,g716)
    c: Coincident(g716,g717)
    c: Coincident(g717,g718)
    c: Coincident(g718,g719)
    c: Coincident(g719,g720)
    c: Coincident(g720,g721)
    c: Coincident(g721,g722)
    c: Coincident(g722,g723)
    c: Coincident(g723,g724)
    c: Coincident(g724,g725)
    c: Coincident(g725,g726)
    c: Coincident(g726,g727)
    c: Coincident(g727,g728)
    c: Coincident(g728,g729)
    c: Coincident(g729,g730)
    c: Coincident(g730,g731)
    c: Coincident(g731,g692)
    c: Coincident(g732,g733)
    c: Coincident(g733,g734)
    c: Coincident(g734,g735)
    c: Coincident(g735,g736)
    c: Coincident(g736,g737)
    c: Coincident(g737,g738)
    c: Coincident(g738,g739)
    c: Coincident(g739,g740)
    c: Coincident(g740,g741)
    c: Coincident(g741,g742)
    c: Coincident(g742,g743)
    c: Coincident(g743,g744)
    c: Coincident(g744,g745)
    c: Coincident(g745,g746)
    c: Coincident(g746,g747)
    c: Coincident(g747,g748)
    c: Coincident(g748,g749)
    c: Coincident(g749,g750)
    c: Coincident(g750,g751)
    c: Coincident(g751,g752)
    c: Coincident(g752,g753)
    c: Coincident(g753,g754)
    c: Coincident(g754,g755)
    c: Coincident(g755,g756)
    c: Coincident(g756,g757)
    c: Coincident(g757,g758)
    c: Coincident(g758,g759)
    c: Coincident(g759,g760)
    c: Coincident(g760,g761)
    c: Coincident(g761,g762)
    c: Coincident(g762,g763)
    c: Coincident(g763,g732)
    c: Coincident(g764,g765)
    c: Coincident(g765,g766)
    c: Coincident(g766,g767)
    c: Coincident(g767,g768)
    c: Coincident(g768,g769)
    c: Coincident(g769,g770)
    c: Coincident(g770,g771)
    c: Coincident(g771,g772)
    c: Coincident(g772,g773)
    c: Coincident(g773,g774)
    c: Coincident(g774,g775)
    c: Coincident(g775,g776)
    c: Coincident(g776,g777)
    c: Coincident(g777,g778)
    c: Coincident(g778,g779)
    c: Coincident(g779,g780)
    c: Coincident(g780,g781)
    c: Coincident(g781,g782)
    c: Coincident(g782,g783)
    c: Coincident(g783,g784)
    c: Coincident(g784,g785)
    c: Coincident(g785,g786)
    c: Coincident(g786,g787)
    c: Coincident(g787,g764)
    c: Coincident(g788,g789)
    c: Coincident(g789,g790)
    c: Coincident(g790,g791)
    c: Coincident(g791,g792)
    c: Coincident(g792,g793)
    c: Coincident(g793,g794)
    c: Coincident(g794,g795)
    c: Coincident(g795,g796)
    c: Coincident(g796,g797)
    c: Coincident(g797,g798)
    c: Coincident(g798,g799)
    c: Coincident(g799,g800)
    c: Coincident(g800,g801)
    c: Coincident(g801,g802)
    c: Coincident(g802,g803)
    c: Coincident(g803,g804)
    c: Coincident(g804,g805)
    c: Coincident(g805,g806)
    c: Coincident(g806,g807)
    c: Coincident(g807,g808)
    c: Coincident(g808,g809)
    c: Coincident(g809,g810)
    c: Coincident(g810,g811)
    c: Coincident(g811,g812)
    c: Coincident(g812,g813)
    c: Coincident(g813,g814)
    c: Coincident(g814,g815)
    c: Coincident(g815,g816)
    c: Coincident(g816,g817)
    c: Coincident(g817,g818)
    c: Coincident(g818,g819)
    c: Coincident(g819,g820)
    c: Coincident(g820,g821)
    c: Coincident(g821,g822)
    c: Coincident(g822,g823)
    c: Coincident(g823,g824)
    c: Coincident(g824,g825)
    c: Coincident(g825,g826)
    c: Coincident(g826,g827)
    c: Coincident(g827,g828)
    c: Coincident(g828,g829)
    c: Coincident(g829,g830)
    c: Coincident(g830,g831)
    c: Coincident(g831,g832)
    c: Coincident(g832,g833)
    c: Coincident(g833,g834)
    c: Coincident(g834,g835)
    c: Coincident(g835,g836)
    c: Coincident(g836,g837)
    c: Coincident(g837,g838)
    c: Coincident(g838,g839)
    c: Coincident(g839,g840)
    c: Coincident(g840,g841)
    c: Coincident(g841,g842)
    c: Coincident(g842,g843)
    c: Coincident(g843,g844)
    c: Coincident(g844,g845)
    c: Coincident(g845,g846)
    c: Coincident(g846,g847)
    c: Coincident(g847,g848)
    c: Coincident(g848,g849)
    c: Coincident(g849,g850)
    c: Coincident(g850,g851)
    c: Coincident(g851,g852)
    c: Coincident(g852,g853)
    c: Coincident(g853,g854)
    c: Coincident(g854,g855)
    c: Coincident(g855,g856)
    c: Coincident(g856,g857)
    c: Coincident(g857,g858)
    c: Coincident(g858,g859)
    c: Coincident(g859,g788)
FEATURE [Sketcher::SketchObject] Sketch033  label="VS002"
  ArcFitTolerance = 1e-06
  FullyConstrained = false
  MakeInternals = false
  Placement = pos=(48.725,7,55.85) rot=(0,1,1;3.14159rad)
  sketch-geometry (860):
    g0: BSplineCurve PolesCount=2 KnotsCount=2 Degree=1 IsPeriodic=0
    g1: BSplineCurve PolesCount=2 KnotsCount=2 Degree=1 IsPeriodic=0
    g2: BSplineCurve PolesCount=2 KnotsCount=2 Degree=1 IsPeriodic=0
    g3: BSplineCurve PolesCount=2 KnotsCount=2 Degree=1 IsPeriodic=0
    g4: BSplineCurve PolesCount=2 KnotsCount=2 Degree=1 IsPeriodic=0
    g5: BSplineCurve PolesCount=2 KnotsCount=2 Degree=1 IsPeriodic=0
    g6: BSplineCurve PolesCount=2 KnotsCount=2 Degree=1 IsPeriodic=0
    g7: BSplineCurve PolesCount=2 KnotsCount=2 Degree=1 IsPeriodic=0
    g8: BSplineCurve PolesCount=2 KnotsCount=2 Degree=1 IsPeriodic=0
    g9: BSplineCurve PolesCount=2 KnotsCount=2 Degree=1 IsPeriodic=0
    g10: BSplineCurve PolesCount=2 KnotsCount=2 Degree=1 IsPeriodic=0
    g11: BSplineCurve PolesCount=2 KnotsCount=2 Degree=1 IsPeriodic=0
    g12: BSplineCurve PolesCount=2 KnotsCount=2 Degree=1 IsPeriodic=0
    g13: BSplineCurve PolesCount=2 KnotsCount=2 Degree=1 IsPeriodic=0
    g14: BSplineCurve PolesCount=2 KnotsCount=2 Degree=1 IsPeriodic=0
    g15: BSplineCurve PolesCount=2 KnotsCount=2 Degree=1 IsPeriodic=0
    g16: BSplineCurve PolesCount=2 KnotsCount=2 Degree=1 IsPeriodic=0
    g17: BSplineCurve PolesCount=2 KnotsCount=2 Degree=1 IsPeriodic=0
    g18: BSplineCurve PolesCount=2 KnotsCount=2 Degree=1 IsPeriodic=0
    g19: BSplineCurve PolesCount=2 KnotsCount=2 Degree=1 IsPeriodic=0
    g20: BSplineCurve PolesCount=2 KnotsCount=2 Degree=1 IsPeriodic=0
    g21: BSplineCurve PolesCount=2 KnotsCount=2 Degree=1 IsPeriodic=0
    g22: BSplineCurve PolesCount=2 KnotsCount=2 Degree=1 IsPeriodic=0
    g23: BSplineCurve PolesCount=2 KnotsCount=2 Degree=1 IsPeriodic=0
    g24: BSplineCurve PolesCount=2 KnotsCount=2 Degree=1 IsPeriodic=0
    g25: BSplineCurve PolesCount=2 KnotsCount=2 Degree=1 IsPeriodic=0
    g26: BSplineCurve PolesCount=2 KnotsCount=2 Degree=1 IsPeriodic=0
    g27: BSplineCurve PolesCount=2 KnotsCount=2 Degree=1 IsPeriodic=0
    g28: BSplineCurve PolesCount=2 KnotsCount=2 Degree=1 IsPeriodic=0
    g29: BSplineCurve PolesCount=2 KnotsCount=2 Degree=1 IsPeriodic=0
    g30: BSplineCurve PolesCount=2 KnotsCount=2 Degree=1 IsPeriodic=0
    g31: BSplineCurve PolesCount=2 KnotsCount=2 Degree=1 IsPeriodic=0
    g32: BSplineCurve PolesCount=2 KnotsCount=2 Degree=1 IsPeriodic=0
    g33: BSplineCurve PolesCount=2 KnotsCount=2 Degree=1 IsPeriodic=0
    g34: BSplineCurve PolesCount=2 KnotsCount=2 Degree=1 IsPeriodic=0
    g35: BSplineCurve PolesCount=2 KnotsCount=2 Degree=1 IsPeriodic=0
    g36: BSplineCurve PolesCount=2 KnotsCount=2 Degree=1 IsPeriodic=0
    g37: BSplineCurve PolesCount=2 KnotsCount=2 Degree=1 IsPeriodic=0
    g38: BSplineCurve PolesCount=2 KnotsCount=2 Degree=1 IsPeriodic=0
    g39: BSplineCurve PolesCount=2 KnotsCount=2 Degree=1 IsPeriodic=0
    g40: BSplineCurve PolesCount=2 KnotsCount=2 Degree=1 IsPeriodic=0
    g41: BSplineCurve PolesCount=2 KnotsCount=2 Degree=1 IsPeriodic=0
    g42: BSplineCurve PolesCount=2 KnotsCount=2 Degree=1 IsPeriodic=0
    g43: BSplineCurve PolesCount=2 KnotsCount=2 Degree=1 IsPeriodic=0
    g44: BSplineCurve PolesCount=2 KnotsCount=2 Degree=1 IsPeriodic=0
    g45: BSplineCurve PolesCount=2 KnotsCount=2 Degree=1 IsPeriodic=0
    g46: BSplineCurve PolesCount=2 KnotsCount=2 Degree=1 IsPeriodic=0
    g47: BSplineCurve PolesCount=2 KnotsCount=2 Degree=1 IsPeriodic=0
    g48: BSplineCurve PolesCount=2 KnotsCount=2 Degree=1 IsPeriodic=0
    g49: BSplineCurve PolesCount=2 KnotsCount=2 Degree=1 IsPeriodic=0
    g50: BSplineCurve PolesCount=2 KnotsCount=2 Degree=1 IsPeriodic=0
    g51: BSplineCurve PolesCount=2 KnotsCount=2 Degree=1 IsPeriodic=0
    g52: BSplineCurve PolesCount=2 KnotsCount=2 Degree=1 IsPeriodic=0
    g53: BSplineCurve PolesCount=2 KnotsCount=2 Degree=1 IsPeriodic=0
    g54: BSplineCurve PolesCount=2 KnotsCount=2 Degree=1 IsPeriodic=0
    g55: BSplineCurve PolesCount=2 KnotsCount=2 Degree=1 IsPeriodic=0
    g56: BSplineCurve PolesCount=2 KnotsCount=2 Degree=1 IsPeriodic=0
    g57: BSplineCurve PolesCount=2 KnotsCount=2 Degree=1 IsPeriodic=0
    g58: BSplineCurve PolesCount=2 KnotsCount=2 Degree=1 IsPeriodic=0
    g59: BSplineCurve PolesCount=2 KnotsCount=2 Degree=1 IsPeriodic=0
    g60: BSplineCurve PolesCount=2 KnotsCount=2 Degree=1 IsPeriodic=0
    g61: BSplineCurve PolesCount=2 KnotsCount=2 Degree=1 IsPeriodic=0
    g62: BSplineCurve PolesCount=2 KnotsCount=2 Degree=1 IsPeriodic=0
    g63: BSplineCurve PolesCount=2 KnotsCount=2 Degree=1 IsPeriodic=0
    g64: BSplineCurve PolesCount=2 KnotsCount=2 Degree=1 IsPeriodic=0
    g65: BSplineCurve PolesCount=2 KnotsCount=2 Degree=1 IsPeriodic=0
    g66: BSplineCurve PolesCount=2 KnotsCount=2 Degree=1 IsPeriodic=0
    g67: BSplineCurve PolesCount=2 KnotsCount=2 Degree=1 IsPeriodic=0
    g68: BSplineCurve PolesCount=2 KnotsCount=2 Degree=1 IsPeriodic=0
    g69: BSplineCurve PolesCount=2 KnotsCount=2 Degree=1 IsPeriodic=0
    g70: BSplineCurve PolesCount=2 KnotsCount=2 Degree=1 IsPeriodic=0
    g71: BSplineCurve PolesCount=2 KnotsCount=2 Degree=1 IsPeriodic=0
    g72: BSplineCurve PolesCount=2 KnotsCount=2 Degree=1 IsPeriodic=0
    g73: BSplineCurve PolesCount=2 KnotsCount=2 Degree=1 IsPeriodic=0
    g74: BSplineCurve PolesCount=2 KnotsCount=2 Degree=1 IsPeriodic=0
    g75: BSplineCurve PolesCount=2 KnotsCount=2 Degree=1 IsPeriodic=0
    g76: BSplineCurve PolesCount=2 KnotsCount=2 Degree=1 IsPeriodic=0
    g77: BSplineCurve PolesCount=2 KnotsCount=2 Degree=1 IsPeriodic=0
    g78: BSplineCurve PolesCount=2 KnotsCount=2 Degree=1 IsPeriodic=0
    g79: BSplineCurve PolesCount=2 KnotsCount=2 Degree=1 IsPeriodic=0
    g80: BSplineCurve PolesCount=2 KnotsCount=2 Degree=1 IsPeriodic=0
    g81: BSplineCurve PolesCount=2 KnotsCount=2 Degree=1 IsPeriodic=0
    g82: BSplineCurve PolesCount=2 KnotsCount=2 Degree=1 IsPeriodic=0
    g83: BSplineCurve PolesCount=2 KnotsCount=2 Degree=1 IsPeriodic=0
    g84: BSplineCurve PolesCount=2 KnotsCount=2 Degree=1 IsPeriodic=0
    g85: BSplineCurve PolesCount=2 KnotsCount=2 Degree=1 IsPeriodic=0
    g86: BSplineCurve PolesCount=2 KnotsCount=2 Degree=1 IsPeriodic=0
    g87: BSplineCurve PolesCount=2 KnotsCount=2 Degree=1 IsPeriodic=0
    g88: BSplineCurve PolesCount=2 KnotsCount=2 Degree=1 IsPeriodic=0
    g89: BSplineCurve PolesCount=2 KnotsCount=2 Degree=1 IsPeriodic=0
    g90: BSplineCurve PolesCount=2 KnotsCount=2 Degree=1 IsPeriodic=0
    g91: BSplineCurve PolesCount=2 KnotsCount=2 Degree=1 IsPeriodic=0
    g92: BSplineCurve PolesCount=2 KnotsCount=2 Degree=1 IsPeriodic=0
    g93: BSplineCurve PolesCount=2 KnotsCount=2 Degree=1 IsPeriodic=0
    g94: BSplineCurve PolesCount=2 KnotsCount=2 Degree=1 IsPeriodic=0
    g95: BSplineCurve PolesCount=2 KnotsCount=2 Degree=1 IsPeriodic=0
    g96: BSplineCurve PolesCount=2 KnotsCount=2 Degree=1 IsPeriodic=0
    g97: BSplineCurve PolesCount=2 KnotsCount=2 Degree=1 IsPeriodic=0
    g98: BSplineCurve PolesCount=2 KnotsCount=2 Degree=1 IsPeriodic=0
    g99: BSplineCurve PolesCount=2 KnotsCount=2 Degree=1 IsPeriodic=0
    g100: BSplineCurve PolesCount=2 KnotsCount=2 Degree=1 IsPeriodic=0
    g101: BSplineCurve PolesCount=2 KnotsCount=2 Degree=1 IsPeriodic=0
    g102: BSplineCurve PolesCount=2 KnotsCount=2 Degree=1 IsPeriodic=0
    g103: BSplineCurve PolesCount=2 KnotsCount=2 Degree=1 IsPeriodic=0
    g104: BSplineCurve PolesCount=2 KnotsCount=2 Degree=1 IsPeriodic=0
    g105: BSplineCurve PolesCount=2 KnotsCount=2 Degree=1 IsPeriodic=0
    g106: BSplineCurve PolesCount=2 KnotsCount=2 Degree=1 IsPeriodic=0
    g107: BSplineCurve PolesCount=2 KnotsCount=2 Degree=1 IsPeriodic=0
    g108: BSplineCurve PolesCount=2 KnotsCount=2 Degree=1 IsPeriodic=0
    g109: BSplineCurve PolesCount=2 KnotsCount=2 Degree=1 IsPeriodic=0
    g110: BSplineCurve PolesCount=2 KnotsCount=2 Degree=1 IsPeriodic=0
    g111: BSplineCurve PolesCount=2 KnotsCount=2 Degree=1 IsPeriodic=0
    g112: BSplineCurve PolesCount=2 KnotsCount=2 Degree=1 IsPeriodic=0
    g113: BSplineCurve PolesCount=2 KnotsCount=2 Degree=1 IsPeriodic=0
    g114: BSplineCurve PolesCount=2 KnotsCount=2 Degree=1 IsPeriodic=0
    g115: BSplineCurve PolesCount=2 KnotsCount=2 Degree=1 IsPeriodic=0
    g116: BSplineCurve PolesCount=2 KnotsCount=2 Degree=1 IsPeriodic=0
    g117: BSplineCurve PolesCount=2 KnotsCount=2 Degree=1 IsPeriodic=0
    g118: BSplineCurve PolesCount=2 KnotsCount=2 Degree=1 IsPeriodic=0
    g119: BSplineCurve PolesCount=2 KnotsCount=2 Degree=1 IsPeriodic=0
    g120: BSplineCurve PolesCount=2 KnotsCount=2 Degree=1 IsPeriodic=0
    g121: BSplineCurve PolesCount=2 KnotsCount=2 Degree=1 IsPeriodic=0
    g122: BSplineCurve PolesCount=2 KnotsCount=2 Degree=1 IsPeriodic=0
    g123: BSplineCurve PolesCount=2 KnotsCount=2 Degree=1 IsPeriodic=0
    g124: BSplineCurve PolesCount=2 KnotsCount=2 Degree=1 IsPeriodic=0
    g125: BSplineCurve PolesCount=2 KnotsCount=2 Degree=1 IsPeriodic=0
    g126: BSplineCurve PolesCount=2 KnotsCount=2 Degree=1 IsPeriodic=0
    g127: BSplineCurve PolesCount=2 KnotsCount=2 Degree=1 IsPeriodic=0
    g128: BSplineCurve PolesCount=2 KnotsCount=2 Degree=1 IsPeriodic=0
    g129: BSplineCurve PolesCount=2 KnotsCount=2 Degree=1 IsPeriodic=0
    g130: BSplineCurve PolesCount=2 KnotsCount=2 Degree=1 IsPeriodic=0
    g131: BSplineCurve PolesCount=2 KnotsCount=2 Degree=1 IsPeriodic=0
    g132: BSplineCurve PolesCount=2 KnotsCount=2 Degree=1 IsPeriodic=0
    g133: BSplineCurve PolesCount=2 KnotsCount=2 Degree=1 IsPeriodic=0
    g134: BSplineCurve PolesCount=2 KnotsCount=2 Degree=1 IsPeriodic=0
    g135: BSplineCurve PolesCount=2 KnotsCount=2 Degree=1 IsPeriodic=0
    g136: BSplineCurve PolesCount=2 KnotsCount=2 Degree=1 IsPeriodic=0
    g137: BSplineCurve PolesCount=2 KnotsCount=2 Degree=1 IsPeriodic=0
    g138: BSplineCurve PolesCount=2 KnotsCount=2 Degree=1 IsPeriodic=0
    g139: BSplineCurve PolesCount=2 KnotsCount=2 Degree=1 IsPeriodic=0
    g140: BSplineCurve PolesCount=2 KnotsCount=2 Degree=1 IsPeriodic=0
    g141: BSplineCurve PolesCount=2 KnotsCount=2 Degree=1 IsPeriodic=0
    g142: BSplineCurve PolesCount=2 KnotsCount=2 Degree=1 IsPeriodic=0
    g143: BSplineCurve PolesCount=2 KnotsCount=2 Degree=1 IsPeriodic=0
    g144: BSplineCurve PolesCount=2 KnotsCount=2 Degree=1 IsPeriodic=0
    g145: BSplineCurve PolesCount=2 KnotsCount=2 Degree=1 IsPeriodic=0
    g146: BSplineCurve PolesCount=2 KnotsCount=2 Degree=1 IsPeriodic=0
    g147: BSplineCurve PolesCount=2 KnotsCount=2 Degree=1 IsPeriodic=0
    g148: BSplineCurve PolesCount=2 KnotsCount=2 Degree=1 IsPeriodic=0
    g149: BSplineCurve PolesCount=2 KnotsCount=2 Degree=1 IsPeriodic=0
    g150: BSplineCurve PolesCount=2 KnotsCount=2 Degree=1 IsPeriodic=0
    g151: BSplineCurve PolesCount=2 KnotsCount=2 Degree=1 IsPeriodic=0
    g152: BSplineCurve PolesCount=2 KnotsCount=2 Degree=1 IsPeriodic=0
    g153: BSplineCurve PolesCount=2 KnotsCount=2 Degree=1 IsPeriodic=0
    g154: BSplineCurve PolesCount=2 KnotsCount=2 Degree=1 IsPeriodic=0
    g155: BSplineCurve PolesCount=2 KnotsCount=2 Degree=1 IsPeriodic=0
    g156: BSplineCurve PolesCount=2 KnotsCount=2 Degree=1 IsPeriodic=0
    g157: BSplineCurve PolesCount=2 KnotsCount=2 Degree=1 IsPeriodic=0
    g158: BSplineCurve PolesCount=2 KnotsCount=2 Degree=1 IsPeriodic=0
    g159: BSplineCurve PolesCount=2 KnotsCount=2 Degree=1 IsPeriodic=0
    g160: BSplineCurve PolesCount=2 KnotsCount=2 Degree=1 IsPeriodic=0
    g161: BSplineCurve PolesCount=2 KnotsCount=2 Degree=1 IsPeriodic=0
    g162: BSplineCurve PolesCount=2 KnotsCount=2 Degree=1 IsPeriodic=0
    g163: BSplineCurve PolesCount=2 KnotsCount=2 Degree=1 IsPeriodic=0
    g164: BSplineCurve PolesCount=2 KnotsCount=2 Degree=1 IsPeriodic=0
    g165: BSplineCurve PolesCount=2 KnotsCount=2 Degree=1 IsPeriodic=0
    g166: BSplineCurve PolesCount=2 KnotsCount=2 Degree=1 IsPeriodic=0
    g167: BSplineCurve PolesCount=2 KnotsCount=2 Degree=1 IsPeriodic=0
    g168: BSplineCurve PolesCount=2 KnotsCount=2 Degree=1 IsPeriodic=0
    g169: BSplineCurve PolesCount=2 KnotsCount=2 Degree=1 IsPeriodic=0
    g170: BSplineCurve PolesCount=2 KnotsCount=2 Degree=1 IsPeriodic=0
    g171: BSplineCurve PolesCount=2 KnotsCount=2 Degree=1 IsPeriodic=0
    g172: BSplineCurve PolesCount=2 KnotsCount=2 Degree=1 IsPeriodic=0
    g173: BSplineCurve PolesCount=2 KnotsCount=2 Degree=1 IsPeriodic=0
    g174: BSplineCurve PolesCount=2 KnotsCount=2 Degree=1 IsPeriodic=0
    g175: BSplineCurve PolesCount=2 KnotsCount=2 Degree=1 IsPeriodic=0
    g176: BSplineCurve PolesCount=2 KnotsCount=2 Degree=1 IsPeriodic=0
    g177: BSplineCurve PolesCount=2 KnotsCount=2 Degree=1 IsPeriodic=0
    g178: BSplineCurve PolesCount=2 KnotsCount=2 Degree=1 IsPeriodic=0
    g179: BSplineCurve PolesCount=2 KnotsCount=2 Degree=1 IsPeriodic=0
    g180: BSplineCurve PolesCount=2 KnotsCount=2 Degree=1 IsPeriodic=0
    g181: BSplineCurve PolesCount=2 KnotsCount=2 Degree=1 IsPeriodic=0
    g182: BSplineCurve PolesCount=2 KnotsCount=2 Degree=1 IsPeriodic=0
    g183: BSplineCurve PolesCount=2 KnotsCount=2 Degree=1 IsPeriodic=0
    g184: BSplineCurve PolesCount=2 KnotsCount=2 Degree=1 IsPeriodic=0
    g185: BSplineCurve PolesCount=2 KnotsCount=2 Degree=1 IsPeriodic=0
    g186: BSplineCurve PolesCount=2 KnotsCount=2 Degree=1 IsPeriodic=0
    g187: BSplineCurve PolesCount=2 KnotsCount=2 Degree=1 IsPeriodic=0
    g188: BSplineCurve PolesCount=2 KnotsCount=2 Degree=1 IsPeriodic=0
    g189: BSplineCurve PolesCount=2 KnotsCount=2 Degree=1 IsPeriodic=0
    g190: BSplineCurve PolesCount=2 KnotsCount=2 Degree=1 IsPeriodic=0
    g191: BSplineCurve PolesCount=2 KnotsCount=2 Degree=1 IsPeriodic=0
    g192: BSplineCurve PolesCount=2 KnotsCount=2 Degree=1 IsPeriodic=0
    g193: BSplineCurve PolesCount=2 KnotsCount=2 Degree=1 IsPeriodic=0
    g194: BSplineCurve PolesCount=2 KnotsCount=2 Degree=1 IsPeriodic=0
    g195: BSplineCurve PolesCount=2 KnotsCount=2 Degree=1 IsPeriodic=0
    g196: BSplineCurve PolesCount=2 KnotsCount=2 Degree=1 IsPeriodic=0
    g197: BSplineCurve PolesCount=2 KnotsCount=2 Degree=1 IsPeriodic=0
    g198: BSplineCurve PolesCount=2 KnotsCount=2 Degree=1 IsPeriodic=0
    g199: BSplineCurve PolesCount=2 KnotsCount=2 Degree=1 IsPeriodic=0
    g200: BSplineCurve PolesCount=2 KnotsCount=2 Degree=1 IsPeriodic=0
    g201: BSplineCurve PolesCount=2 KnotsCount=2 Degree=1 IsPeriodic=0
    g202: BSplineCurve PolesCount=2 KnotsCount=2 Degree=1 IsPeriodic=0
    g203: BSplineCurve PolesCount=2 KnotsCount=2 Degree=1 IsPeriodic=0
    g204: BSplineCurve PolesCount=2 KnotsCount=2 Degree=1 IsPeriodic=0
    g205: BSplineCurve PolesCount=2 KnotsCount=2 Degree=1 IsPeriodic=0
    g206: BSplineCurve PolesCount=2 KnotsCount=2 Degree=1 IsPeriodic=0
    g207: BSplineCurve PolesCount=2 KnotsCount=2 Degree=1 IsPeriodic=0
    g208: BSplineCurve PolesCount=2 KnotsCount=2 Degree=1 IsPeriodic=0
    g209: BSplineCurve PolesCount=2 KnotsCount=2 Degree=1 IsPeriodic=0
    g210: BSplineCurve PolesCount=2 KnotsCount=2 Degree=1 IsPeriodic=0
    g211: BSplineCurve PolesCount=2 KnotsCount=2 Degree=1 IsPeriodic=0
    g212: BSplineCurve PolesCount=2 KnotsCount=2 Degree=1 IsPeriodic=0
    g213: BSplineCurve PolesCount=2 KnotsCount=2 Degree=1 IsPeriodic=0
    g214: BSplineCurve PolesCount=2 KnotsCount=2 Degree=1 IsPeriodic=0
    g215: BSplineCurve PolesCount=2 KnotsCount=2 Degree=1 IsPeriodic=0
    g216: BSplineCurve PolesCount=2 KnotsCount=2 Degree=1 IsPeriodic=0
    g217: BSplineCurve PolesCount=2 KnotsCount=2 Degree=1 IsPeriodic=0
    g218: BSplineCurve PolesCount=2 KnotsCount=2 Degree=1 IsPeriodic=0
    g219: BSplineCurve PolesCount=2 KnotsCount=2 Degree=1 IsPeriodic=0
    g220: BSplineCurve PolesCount=2 KnotsCount=2 Degree=1 IsPeriodic=0
    g221: BSplineCurve PolesCount=2 KnotsCount=2 Degree=1 IsPeriodic=0
    g222: BSplineCurve PolesCount=2 KnotsCount=2 Degree=1 IsPeriodic=0
    g223: BSplineCurve PolesCount=2 KnotsCount=2 Degree=1 IsPeriodic=0
    g224: BSplineCurve PolesCount=2 KnotsCount=2 Degree=1 IsPeriodic=0
    g225: BSplineCurve PolesCount=2 KnotsCount=2 Degree=1 IsPeriodic=0
    g226: BSplineCurve PolesCount=2 KnotsCount=2 Degree=1 IsPeriodic=0
    g227: BSplineCurve PolesCount=2 KnotsCount=2 Degree=1 IsPeriodic=0
    g228: BSplineCurve PolesCount=2 KnotsCount=2 Degree=1 IsPeriodic=0
    g229: BSplineCurve PolesCount=2 KnotsCount=2 Degree=1 IsPeriodic=0
    g230: BSplineCurve PolesCount=2 KnotsCount=2 Degree=1 IsPeriodic=0
    g231: BSplineCurve PolesCount=2 KnotsCount=2 Degree=1 IsPeriodic=0
    g232: BSplineCurve PolesCount=2 KnotsCount=2 Degree=1 IsPeriodic=0
    g233: BSplineCurve PolesCount=2 KnotsCount=2 Degree=1 IsPeriodic=0
    g234: BSplineCurve PolesCount=2 KnotsCount=2 Degree=1 IsPeriodic=0
    g235: BSplineCurve PolesCount=2 KnotsCount=2 Degree=1 IsPeriodic=0
    g236: BSplineCurve PolesCount=2 KnotsCount=2 Degree=1 IsPeriodic=0
    g237: BSplineCurve PolesCount=2 KnotsCount=2 Degree=1 IsPeriodic=0
    g238: BSplineCurve PolesCount=2 KnotsCount=2 Degree=1 IsPeriodic=0
    g239: BSplineCurve PolesCount=2 KnotsCount=2 Degree=1 IsPeriodic=0
    g240: BSplineCurve PolesCount=2 KnotsCount=2 Degree=1 IsPeriodic=0
    g241: BSplineCurve PolesCount=2 KnotsCount=2 Degree=1 IsPeriodic=0
    g242: BSplineCurve PolesCount=2 KnotsCount=2 Degree=1 IsPeriodic=0
    g243: BSplineCurve PolesCount=2 KnotsCount=2 Degree=1 IsPeriodic=0
    g244: BSplineCurve PolesCount=2 KnotsCount=2 Degree=1 IsPeriodic=0
    g245: BSplineCurve PolesCount=2 KnotsCount=2 Degree=1 IsPeriodic=0
    g246: BSplineCurve PolesCount=2 KnotsCount=2 Degree=1 IsPeriodic=0
    g247: BSplineCurve PolesCount=2 KnotsCount=2 Degree=1 IsPeriodic=0
    g248: BSplineCurve PolesCount=2 KnotsCount=2 Degree=1 IsPeriodic=0
    g249: BSplineCurve PolesCount=2 KnotsCount=2 Degree=1 IsPeriodic=0
    g250: BSplineCurve PolesCount=2 KnotsCount=2 Degree=1 IsPeriodic=0
    g251: BSplineCurve PolesCount=2 KnotsCount=2 Degree=1 IsPeriodic=0
    g252: BSplineCurve PolesCount=2 KnotsCount=2 Degree=1 IsPeriodic=0
    g253: BSplineCurve PolesCount=2 KnotsCount=2 Degree=1 IsPeriodic=0
    g254: BSplineCurve PolesCount=2 KnotsCount=2 Degree=1 IsPeriodic=0
    g255: BSplineCurve PolesCount=2 KnotsCount=2 Degree=1 IsPeriodic=0
    g256: BSplineCurve PolesCount=2 KnotsCount=2 Degree=1 IsPeriodic=0
    g257: BSplineCurve PolesCount=2 KnotsCount=2 Degree=1 IsPeriodic=0
    g258: BSplineCurve PolesCount=2 KnotsCount=2 Degree=1 IsPeriodic=0
    g259: BSplineCurve PolesCount=2 KnotsCount=2 Degree=1 IsPeriodic=0
    g260: BSplineCurve PolesCount=2 KnotsCount=2 Degree=1 IsPeriodic=0
    g261: BSplineCurve PolesCount=2 KnotsCount=2 Degree=1 IsPeriodic=0
    g262: BSplineCurve PolesCount=2 KnotsCount=2 Degree=1 IsPeriodic=0
    g263: BSplineCurve PolesCount=2 KnotsCount=2 Degree=1 IsPeriodic=0
    g264: BSplineCurve PolesCount=2 KnotsCount=2 Degree=1 IsPeriodic=0
    g265: BSplineCurve PolesCount=2 KnotsCount=2 Degree=1 IsPeriodic=0
    g266: BSplineCurve PolesCount=2 KnotsCount=2 Degree=1 IsPeriodic=0
    g267: BSplineCurve PolesCount=2 KnotsCount=2 Degree=1 IsPeriodic=0
    g268: BSplineCurve PolesCount=2 KnotsCount=2 Degree=1 IsPeriodic=0
    g269: BSplineCurve PolesCount=2 KnotsCount=2 Degree=1 IsPeriodic=0
    g270: BSplineCurve PolesCount=2 KnotsCount=2 Degree=1 IsPeriodic=0
    g271: BSplineCurve PolesCount=2 KnotsCount=2 Degree=1 IsPeriodic=0
    g272: BSplineCurve PolesCount=2 KnotsCount=2 Degree=1 IsPeriodic=0
    g273: BSplineCurve PolesCount=2 KnotsCount=2 Degree=1 IsPeriodic=0
    g274: BSplineCurve PolesCount=2 KnotsCount=2 Degree=1 IsPeriodic=0
    g275: BSplineCurve PolesCount=2 KnotsCount=2 Degree=1 IsPeriodic=0
    g276: BSplineCurve PolesCount=2 KnotsCount=2 Degree=1 IsPeriodic=0
    g277: BSplineCurve PolesCount=2 KnotsCount=2 Degree=1 IsPeriodic=0
    g278: BSplineCurve PolesCount=2 KnotsCount=2 Degree=1 IsPeriodic=0
    g279: BSplineCurve PolesCount=2 KnotsCount=2 Degree=1 IsPeriodic=0
    g280: BSplineCurve PolesCount=2 KnotsCount=2 Degree=1 IsPeriodic=0
    g281: BSplineCurve PolesCount=2 KnotsCount=2 Degree=1 IsPeriodic=0
    g282: BSplineCurve PolesCount=2 KnotsCount=2 Degree=1 IsPeriodic=0
    g283: BSplineCurve PolesCount=2 KnotsCount=2 Degree=1 IsPeriodic=0
    g284: BSplineCurve PolesCount=2 KnotsCount=2 Degree=1 IsPeriodic=0
    g285: BSplineCurve PolesCount=2 KnotsCount=2 Degree=1 IsPeriodic=0
    g286: BSplineCurve PolesCount=2 KnotsCount=2 Degree=1 IsPeriodic=0
    g287: BSplineCurve PolesCount=2 KnotsCount=2 Degree=1 IsPeriodic=0
    g288: BSplineCurve PolesCount=2 KnotsCount=2 Degree=1 IsPeriodic=0
    g289: BSplineCurve PolesCount=2 KnotsCount=2 Degree=1 IsPeriodic=0
    g290: BSplineCurve PolesCount=2 KnotsCount=2 Degree=1 IsPeriodic=0
    g291: BSplineCurve PolesCount=2 KnotsCount=2 Degree=1 IsPeriodic=0
    g292: BSplineCurve PolesCount=2 KnotsCount=2 Degree=1 IsPeriodic=0
    g293: BSplineCurve PolesCount=2 KnotsCount=2 Degree=1 IsPeriodic=0
    g294: BSplineCurve PolesCount=2 KnotsCount=2 Degree=1 IsPeriodic=0
    g295: BSplineCurve PolesCount=2 KnotsCount=2 Degree=1 IsPeriodic=0
    g296: BSplineCurve PolesCount=2 KnotsCount=2 Degree=1 IsPeriodic=0
    g297: BSplineCurve PolesCount=2 KnotsCount=2 Degree=1 IsPeriodic=0
    g298: BSplineCurve PolesCount=2 KnotsCount=2 Degree=1 IsPeriodic=0
    g299: BSplineCurve PolesCount=2 KnotsCount=2 Degree=1 IsPeriodic=0
    g300: BSplineCurve PolesCount=2 KnotsCount=2 Degree=1 IsPeriodic=0
    g301: BSplineCurve PolesCount=2 KnotsCount=2 Degree=1 IsPeriodic=0
    g302: BSplineCurve PolesCount=2 KnotsCount=2 Degree=1 IsPeriodic=0
    g303: BSplineCurve PolesCount=2 KnotsCount=2 Degree=1 IsPeriodic=0
    g304: BSplineCurve PolesCount=2 KnotsCount=2 Degree=1 IsPeriodic=0
    g305: BSplineCurve PolesCount=2 KnotsCount=2 Degree=1 IsPeriodic=0
    g306: BSplineCurve PolesCount=2 KnotsCount=2 Degree=1 IsPeriodic=0
    g307: BSplineCurve PolesCount=2 KnotsCount=2 Degree=1 IsPeriodic=0
    g308: BSplineCurve PolesCount=2 KnotsCount=2 Degree=1 IsPeriodic=0
    g309: BSplineCurve PolesCount=2 KnotsCount=2 Degree=1 IsPeriodic=0
    g310: BSplineCurve PolesCount=2 KnotsCount=2 Degree=1 IsPeriodic=0
    g311: BSplineCurve PolesCount=2 KnotsCount=2 Degree=1 IsPeriodic=0
    g312: BSplineCurve PolesCount=2 KnotsCount=2 Degree=1 IsPeriodic=0
    g313: BSplineCurve PolesCount=2 KnotsCount=2 Degree=1 IsPeriodic=0
    g314: BSplineCurve PolesCount=2 KnotsCount=2 Degree=1 IsPeriodic=0
    g315: BSplineCurve PolesCount=2 KnotsCount=2 Degree=1 IsPeriodic=0
    g316: BSplineCurve PolesCount=2 KnotsCount=2 Degree=1 IsPeriodic=0
    g317: BSplineCurve PolesCount=2 KnotsCount=2 Degree=1 IsPeriodic=0
    g318: BSplineCurve PolesCount=2 KnotsCount=2 Degree=1 IsPeriodic=0
    g319: BSplineCurve PolesCount=2 KnotsCount=2 Degree=1 IsPeriodic=0
    g320: BSplineCurve PolesCount=2 KnotsCount=2 Degree=1 IsPeriodic=0
    g321: BSplineCurve PolesCount=2 KnotsCount=2 Degree=1 IsPeriodic=0
    g322: BSplineCurve PolesCount=2 KnotsCount=2 Degree=1 IsPeriodic=0
    g323: BSplineCurve PolesCount=2 KnotsCount=2 Degree=1 IsPeriodic=0
    g324: BSplineCurve PolesCount=2 KnotsCount=2 Degree=1 IsPeriodic=0
    g325: BSplineCurve PolesCount=2 KnotsCount=2 Degree=1 IsPeriodic=0
    g326: BSplineCurve PolesCount=2 KnotsCount=2 Degree=1 IsPeriodic=0
    g327: BSplineCurve PolesCount=2 KnotsCount=2 Degree=1 IsPeriodic=0
    g328: BSplineCurve PolesCount=2 KnotsCount=2 Degree=1 IsPeriodic=0
    g329: BSplineCurve PolesCount=2 KnotsCount=2 Degree=1 IsPeriodic=0
    g330: BSplineCurve PolesCount=2 KnotsCount=2 Degree=1 IsPeriodic=0
    g331: BSplineCurve PolesCount=2 KnotsCount=2 Degree=1 IsPeriodic=0
    g332: BSplineCurve PolesCount=2 KnotsCount=2 Degree=1 IsPeriodic=0
    g333: BSplineCurve PolesCount=2 KnotsCount=2 Degree=1 IsPeriodic=0
    g334: BSplineCurve PolesCount=2 KnotsCount=2 Degree=1 IsPeriodic=0
    g335: BSplineCurve PolesCount=2 KnotsCount=2 Degree=1 IsPeriodic=0
    g336: BSplineCurve PolesCount=2 KnotsCount=2 Degree=1 IsPeriodic=0
    g337: BSplineCurve PolesCount=2 KnotsCount=2 Degree=1 IsPeriodic=0
    g338: BSplineCurve PolesCount=2 KnotsCount=2 Degree=1 IsPeriodic=0
    g339: BSplineCurve PolesCount=2 KnotsCount=2 Degree=1 IsPeriodic=0
    g340: BSplineCurve PolesCount=2 KnotsCount=2 Degree=1 IsPeriodic=0
    g341: BSplineCurve PolesCount=2 KnotsCount=2 Degree=1 IsPeriodic=0
    g342: BSplineCurve PolesCount=2 KnotsCount=2 Degree=1 IsPeriodic=0
    g343: BSplineCurve PolesCount=2 KnotsCount=2 Degree=1 IsPeriodic=0
    g344: BSplineCurve PolesCount=2 KnotsCount=2 Degree=1 IsPeriodic=0
    g345: BSplineCurve PolesCount=2 KnotsCount=2 Degree=1 IsPeriodic=0
    g346: BSplineCurve PolesCount=2 KnotsCount=2 Degree=1 IsPeriodic=0
    g347: BSplineCurve PolesCount=2 KnotsCount=2 Degree=1 IsPeriodic=0
    g348: BSplineCurve PolesCount=2 KnotsCount=2 Degree=1 IsPeriodic=0
    g349: BSplineCurve PolesCount=2 KnotsCount=2 Degree=1 IsPeriodic=0
    g350: BSplineCurve PolesCount=2 KnotsCount=2 Degree=1 IsPeriodic=0
    g351: BSplineCurve PolesCount=2 KnotsCount=2 Degree=1 IsPeriodic=0
    g352: BSplineCurve PolesCount=2 KnotsCount=2 Degree=1 IsPeriodic=0
    g353: BSplineCurve PolesCount=2 KnotsCount=2 Degree=1 IsPeriodic=0
    g354: BSplineCurve PolesCount=2 KnotsCount=2 Degree=1 IsPeriodic=0
    g355: BSplineCurve PolesCount=2 KnotsCount=2 Degree=1 IsPeriodic=0
    g356: BSplineCurve PolesCount=2 KnotsCount=2 Degree=1 IsPeriodic=0
    g357: BSplineCurve PolesCount=2 KnotsCount=2 Degree=1 IsPeriodic=0
    g358: BSplineCurve PolesCount=2 KnotsCount=2 Degree=1 IsPeriodic=0
    g359: BSplineCurve PolesCount=2 KnotsCount=2 Degree=1 IsPeriodic=0
    g360: BSplineCurve PolesCount=2 KnotsCount=2 Degree=1 IsPeriodic=0
    g361: BSplineCurve PolesCount=2 KnotsCount=2 Degree=1 IsPeriodic=0
    g362: BSplineCurve PolesCount=2 KnotsCount=2 Degree=1 IsPeriodic=0
    g363: BSplineCurve PolesCount=2 KnotsCount=2 Degree=1 IsPeriodic=0
    g364: BSplineCurve PolesCount=2 KnotsCount=2 Degree=1 IsPeriodic=0
    g365: BSplineCurve PolesCount=2 KnotsCount=2 Degree=1 IsPeriodic=0
    g366: BSplineCurve PolesCount=2 KnotsCount=2 Degree=1 IsPeriodic=0
    g367: BSplineCurve PolesCount=2 KnotsCount=2 Degree=1 IsPeriodic=0
    g368: BSplineCurve PolesCount=2 KnotsCount=2 Degree=1 IsPeriodic=0
    g369: BSplineCurve PolesCount=2 KnotsCount=2 Degree=1 IsPeriodic=0
    g370: BSplineCurve PolesCount=2 KnotsCount=2 Degree=1 IsPeriodic=0
    g371: BSplineCurve PolesCount=2 KnotsCount=2 Degree=1 IsPeriodic=0
    g372: BSplineCurve PolesCount=2 KnotsCount=2 Degree=1 IsPeriodic=0
    g373: BSplineCurve PolesCount=2 KnotsCount=2 Degree=1 IsPeriodic=0
    g374: BSplineCurve PolesCount=2 KnotsCount=2 Degree=1 IsPeriodic=0
    g375: BSplineCurve PolesCount=2 KnotsCount=2 Degree=1 IsPeriodic=0
    g376: BSplineCurve PolesCount=2 KnotsCount=2 Degree=1 IsPeriodic=0
    g377: BSplineCurve PolesCount=2 KnotsCount=2 Degree=1 IsPeriodic=0
    g378: BSplineCurve PolesCount=2 KnotsCount=2 Degree=1 IsPeriodic=0
    g379: BSplineCurve PolesCount=2 KnotsCount=2 Degree=1 IsPeriodic=0
    g380: BSplineCurve PolesCount=2 KnotsCount=2 Degree=1 IsPeriodic=0
    g381: BSplineCurve PolesCount=2 KnotsCount=2 Degree=1 IsPeriodic=0
    g382: BSplineCurve PolesCount=2 KnotsCount=2 Degree=1 IsPeriodic=0
    g383: BSplineCurve PolesCount=2 KnotsCount=2 Degree=1 IsPeriodic=0
    g384: BSplineCurve PolesCount=2 KnotsCount=2 Degree=1 IsPeriodic=0
    g385: BSplineCurve PolesCount=2 KnotsCount=2 Degree=1 IsPeriodic=0
    g386: BSplineCurve PolesCount=2 KnotsCount=2 Degree=1 IsPeriodic=0
    g387: BSplineCurve PolesCount=2 KnotsCount=2 Degree=1 IsPeriodic=0
    g388: BSplineCurve PolesCount=2 KnotsCount=2 Degree=1 IsPeriodic=0
    g389: BSplineCurve PolesCount=2 KnotsCount=2 Degree=1 IsPeriodic=0
    g390: BSplineCurve PolesCount=2 KnotsCount=2 Degree=1 IsPeriodic=0
    g391: BSplineCurve PolesCount=2 KnotsCount=2 Degree=1 IsPeriodic=0
    g392: BSplineCurve PolesCount=2 KnotsCount=2 Degree=1 IsPeriodic=0
    g393: BSplineCurve PolesCount=2 KnotsCount=2 Degree=1 IsPeriodic=0
    g394: BSplineCurve PolesCount=2 KnotsCount=2 Degree=1 IsPeriodic=0
    g395: BSplineCurve PolesCount=2 KnotsCount=2 Degree=1 IsPeriodic=0
    g396: BSplineCurve PolesCount=2 KnotsCount=2 Degree=1 IsPeriodic=0
    g397: BSplineCurve PolesCount=2 KnotsCount=2 Degree=1 IsPeriodic=0
    g398: BSplineCurve PolesCount=2 KnotsCount=2 Degree=1 IsPeriodic=0
    g399: BSplineCurve PolesCount=2 KnotsCount=2 Degree=1 IsPeriodic=0
    ... +460 more geometry lines
  constraints (860):
    c: Coincident(g0,g1)
    c: Coincident(g1,g2)
    c: Coincident(g2,g3)
    c: Coincident(g3,g4)
    c: Coincident(g4,g5)
    c: Coincident(g5,g6)
    c: Coincident(g6,g7)
    c: Coincident(g7,g8)
    c: Coincident(g8,g9)
    c: Coincident(g9,g10)
    c: Coincident(g10,g11)
    c: Coincident(g11,g12)
    c: Coincident(g12,g13)
    c: Coincident(g13,g14)
    c: Coincident(g14,g15)
    c: Coincident(g15,g16)
    c: Coincident(g16,g17)
    c: Coincident(g17,g18)
    c: Coincident(g18,g19)
    c: Coincident(g19,g20)
    c: Coincident(g20,g21)
    c: Coincident(g21,g22)
    c: Coincident(g22,g23)
    c: Coincident(g23,g24)
    c: Coincident(g24,g25)
    c: Coincident(g25,g26)
    c: Coincident(g26,g27)
    c: Coincident(g27,g28)
    c: Coincident(g28,g29)
    c: Coincident(g29,g30)
    c: Coincident(g30,g31)
    c: Coincident(g31,g32)
    c: Coincident(g32,g33)
    c: Coincident(g33,g34)
    c: Coincident(g34,g35)
    c: Coincident(g35,g36)
    c: Coincident(g36,g37)
    c: Coincident(g37,g38)
    c: Coincident(g38,g39)
    c: Coincident(g39,g40)
    c: Coincident(g40,g41)
    c: Coincident(g41,g42)
    c: Coincident(g42,g43)
    c: Coincident(g43,g44)
    c: Coincident(g44,g45)
    c: Coincident(g45,g46)
    c: Coincident(g46,g47)
    c: Coincident(g47,g48)
    c: Coincident(g48,g49)
    c: Coincident(g49,g50)
    c: Coincident(g50,g51)
    c: Coincident(g51,g52)
    c: Coincident(g52,g53)
    c: Coincident(g53,g54)
    c: Coincident(g54,g55)
    c: Coincident(g55,g56)
    c: Coincident(g56,g57)
    c: Coincident(g57,g58)
    c: Coincident(g58,g59)
    c: Coincident(g59,g60)
    c: Coincident(g60,g61)
    c: Coincident(g61,g62)
    c: Coincident(g62,g63)
    c: Coincident(g63,g64)
    c: Coincident(g64,g65)
    c: Coincident(g65,g66)
    c: Coincident(g66,g67)
    c: Coincident(g67,g68)
    c: Coincident(g68,g69)
    c: Coincident(g69,g70)
    c: Coincident(g70,g71)
    c: Coincident(g71,g72)
    c: Coincident(g72,g73)
    c: Coincident(g73,g74)
    c: Coincident(g74,g75)
    c: Coincident(g75,g76)
    c: Coincident(g76,g77)
    c: Coincident(g77,g78)
    c: Coincident(g78,g79)
    c: Coincident(g79,g80)
    c: Coincident(g80,g81)
    c: Coincident(g81,g82)
    c: Coincident(g82,g83)
    c: Coincident(g83,g84)
    c: Coincident(g84,g85)
    c: Coincident(g85,g86)
    c: Coincident(g86,g87)
    c: Coincident(g87,g0)
    c: Coincident(g88,g89)
    c: Coincident(g89,g90)
    c: Coincident(g90,g91)
    c: Coincident(g91,g92)
    c: Coincident(g92,g93)
    c: Coincident(g93,g94)
    c: Coincident(g94,g95)
    c: Coincident(g95,g96)
    c: Coincident(g96,g97)
    c: Coincident(g97,g98)
    c: Coincident(g98,g99)
    c: Coincident(g99,g100)
    c: Coincident(g100,g101)
    c: Coincident(g101,g102)
    c: Coincident(g102,g103)
    c: Coincident(g103,g104)
    c: Coincident(g104,g105)
    c: Coincident(g105,g106)
    c: Coincident(g106,g107)
    c: Coincident(g107,g108)
    c: Coincident(g108,g109)
    c: Coincident(g109,g110)
    c: Coincident(g110,g111)
    c: Coincident(g111,g112)
    c: Coincident(g112,g113)
    c: Coincident(g113,g114)
    c: Coincident(g114,g115)
    c: Coincident(g115,g116)
    c: Coincident(g116,g117)
    c: Coincident(g117,g118)
    c: Coincident(g118,g119)
    c: Coincident(g119,g120)
    c: Coincident(g120,g121)
    c: Coincident(g121,g122)
    c: Coincident(g122,g123)
    c: Coincident(g123,g124)
    c: Coincident(g124,g125)
    c: Coincident(g125,g126)
    c: Coincident(g126,g127)
    c: Coincident(g127,g88)
    c: Coincident(g128,g129)
    c: Coincident(g129,g130)
    c: Coincident(g130,g131)
    c: Coincident(g131,g132)
    c: Coincident(g132,g133)
    c: Coincident(g133,g134)
    c: Coincident(g134,g135)
    c: Coincident(g135,g136)
    c: Coincident(g136,g137)
    c: Coincident(g137,g138)
    c: Coincident(g138,g139)
    c: Coincident(g139,g140)
    c: Coincident(g140,g141)
    c: Coincident(g141,g142)
    c: Coincident(g142,g143)
    c: Coincident(g143,g144)
    c: Coincident(g144,g145)
    c: Coincident(g145,g146)
    c: Coincident(g146,g147)
    c: Coincident(g147,g148)
    c: Coincident(g148,g149)
    c: Coincident(g149,g150)
    c: Coincident(g150,g151)
    c: Coincident(g151,g152)
    c: Coincident(g152,g153)
    c: Coincident(g153,g154)
    c: Coincident(g154,g155)
    c: Coincident(g155,g156)
    c: Coincident(g156,g157)
    c: Coincident(g157,g158)
    c: Coincident(g158,g159)
    c: Coincident(g159,g160)
    c: Coincident(g160,g161)
    c: Coincident(g161,g162)
    c: Coincident(g162,g163)
    c: Coincident(g163,g164)
    c: Coincident(g164,g165)
    c: Coincident(g165,g166)
    c: Coincident(g166,g167)
    c: Coincident(g167,g168)
    c: Coincident(g168,g169)
    c: Coincident(g169,g170)
    c: Coincident(g170,g171)
    c: Coincident(g171,g172)
    c: Coincident(g172,g173)
    c: Coincident(g173,g174)
    c: Coincident(g174,g175)
    c: Coincident(g175,g176)
    c: Coincident(g176,g177)
    c: Coincident(g177,g178)
    c: Coincident(g178,g179)
    c: Coincident(g179,g180)
    c: Coincident(g180,g181)
    c: Coincident(g181,g182)
    c: Coincident(g182,g183)
    c: Coincident(g183,g184)
    c: Coincident(g184,g185)
    c: Coincident(g185,g186)
    c: Coincident(g186,g187)
    c: Coincident(g187,g188)
    c: Coincident(g188,g189)
    c: Coincident(g189,g190)
    c: Coincident(g190,g191)
    c: Coincident(g191,g192)
    c: Coincident(g192,g193)
    c: Coincident(g193,g194)
    c: Coincident(g194,g195)
    c: Coincident(g195,g196)
    c: Coincident(g196,g197)
    c: Coincident(g197,g198)
    c: Coincident(g198,g199)
    c: Coincident(g199,g200)
    c: Coincident(g200,g201)
    c: Coincident(g201,g202)
    c: Coincident(g202,g203)
    c: Coincident(g203,g204)
    c: Coincident(g204,g205)
    c: Coincident(g205,g206)
    c: Coincident(g206,g207)
    c: Coincident(g207,g208)
    c: Coincident(g208,g209)
    c: Coincident(g209,g210)
    c: Coincident(g210,g211)
    c: Coincident(g211,g212)
    c: Coincident(g212,g213)
    c: Coincident(g213,g214)
    c: Coincident(g214,g215)
    c: Coincident(g215,g216)
    c: Coincident(g216,g217)
    c: Coincident(g217,g218)
    c: Coincident(g218,g219)
    c: Coincident(g219,g220)
    c: Coincident(g220,g221)
    c: Coincident(g221,g222)
    c: Coincident(g222,g223)
    c: Coincident(g223,g224)
    c: Coincident(g224,g225)
    c: Coincident(g225,g226)
    c: Coincident(g226,g227)
    c: Coincident(g227,g228)
    c: Coincident(g228,g229)
    c: Coincident(g229,g230)
    c: Coincident(g230,g231)
    c: Coincident(g231,g232)
    c: Coincident(g232,g233)
    c: Coincident(g233,g234)
    c: Coincident(g234,g235)
    c: Coincident(g235,g236)
    c: Coincident(g236,g237)
    c: Coincident(g237,g238)
    c: Coincident(g238,g239)
    c: Coincident(g239,g128)
    c: Coincident(g240,g241)
    c: Coincident(g241,g242)
    c: Coincident(g242,g243)
    c: Coincident(g243,g244)
    c: Coincident(g244,g245)
    c: Coincident(g245,g246)
    c: Coincident(g246,g247)
    c: Coincident(g247,g248)
    c: Coincident(g248,g249)
    c: Coincident(g249,g250)
    c: Coincident(g250,g251)
    c: Coincident(g251,g252)
    c: Coincident(g252,g253)
    c: Coincident(g253,g254)
    c: Coincident(g254,g255)
    c: Coincident(g255,g256)
    c: Coincident(g256,g257)
    c: Coincident(g257,g258)
    c: Coincident(g258,g259)
    c: Coincident(g259,g260)
    c: Coincident(g260,g261)
    c: Coincident(g261,g262)
    c: Coincident(g262,g263)
    c: Coincident(g263,g264)
    c: Coincident(g264,g265)
    c: Coincident(g265,g266)
    c: Coincident(g266,g267)
    c: Coincident(g267,g268)
    c: Coincident(g268,g269)
    c: Coincident(g269,g270)
    c: Coincident(g270,g271)
    c: Coincident(g271,g272)
    c: Coincident(g272,g273)
    c: Coincident(g273,g274)
    c: Coincident(g274,g275)
    c: Coincident(g275,g276)
    c: Coincident(g276,g277)
    c: Coincident(g277,g278)
    c: Coincident(g278,g279)
    c: Coincident(g279,g280)
    c: Coincident(g280,g281)
    c: Coincident(g281,g282)
    c: Coincident(g282,g283)
    c: Coincident(g283,g284)
    c: Coincident(g284,g285)
    c: Coincident(g285,g286)
    c: Coincident(g286,g287)
    c: Coincident(g287,g240)
    c: Coincident(g288,g289)
    c: Coincident(g289,g290)
    c: Coincident(g290,g291)
    c: Coincident(g291,g292)
    c: Coincident(g292,g293)
    c: Coincident(g293,g294)
    c: Coincident(g294,g295)
    c: Coincident(g295,g296)
    c: Coincident(g296,g297)
    c: Coincident(g297,g298)
    c: Coincident(g298,g299)
    c: Coincident(g299,g300)
    c: Coincident(g300,g301)
    c: Coincident(g301,g302)
    c: Coincident(g302,g303)
    c: Coincident(g303,g304)
    c: Coincident(g304,g305)
    c: Coincident(g305,g306)
    c: Coincident(g306,g307)
    c: Coincident(g307,g308)
    c: Coincident(g308,g309)
    c: Coincident(g309,g310)
    c: Coincident(g310,g311)
    c: Coincident(g311,g288)
    c: Coincident(g312,g313)
    c: Coincident(g313,g314)
    c: Coincident(g314,g315)
    c: Coincident(g315,g316)
    c: Coincident(g316,g317)
    c: Coincident(g317,g318)
    c: Coincident(g318,g319)
    c: Coincident(g319,g320)
    c: Coincident(g320,g321)
    c: Coincident(g321,g322)
    c: Coincident(g322,g323)
    c: Coincident(g323,g324)
    c: Coincident(g324,g325)
    c: Coincident(g325,g326)
    c: Coincident(g326,g327)
    c: Coincident(g327,g312)
    c: Coincident(g328,g329)
    c: Coincident(g329,g330)
    c: Coincident(g330,g331)
    c: Coincident(g331,g332)
    c: Coincident(g332,g333)
    c: Coincident(g333,g334)
    c: Coincident(g334,g335)
    c: Coincident(g335,g336)
    c: Coincident(g336,g337)
    c: Coincident(g337,g338)
    c: Coincident(g338,g339)
    c: Coincident(g339,g340)
    c: Coincident(g340,g341)
    c: Coincident(g341,g342)
    c: Coincident(g342,g343)
    c: Coincident(g343,g344)
    c: Coincident(g344,g345)
    c: Coincident(g345,g346)
    c: Coincident(g346,g347)
    c: Coincident(g347,g348)
    c: Coincident(g348,g349)
    c: Coincident(g349,g350)
    c: Coincident(g350,g351)
    c: Coincident(g351,g352)
    c: Coincident(g352,g353)
    c: Coincident(g353,g354)
    c: Coincident(g354,g355)
    c: Coincident(g355,g356)
    c: Coincident(g356,g357)
    c: Coincident(g357,g358)
    c: Coincident(g358,g359)
    c: Coincident(g359,g360)
    c: Coincident(g360,g361)
    c: Coincident(g361,g362)
    c: Coincident(g362,g363)
    c: Coincident(g363,g364)
    c: Coincident(g364,g365)
    c: Coincident(g365,g366)
    c: Coincident(g366,g367)
    c: Coincident(g367,g368)
    c: Coincident(g368,g369)
    c: Coincident(g369,g370)
    c: Coincident(g370,g371)
    c: Coincident(g371,g372)
    c: Coincident(g372,g373)
    c: Coincident(g373,g374)
    c: Coincident(g374,g375)
    c: Coincident(g375,g376)
    c: Coincident(g376,g377)
    c: Coincident(g377,g378)
    c: Coincident(g378,g379)
    c: Coincident(g379,g380)
    c: Coincident(g380,g381)
    c: Coincident(g381,g382)
    c: Coincident(g382,g383)
    c: Coincident(g383,g384)
    c: Coincident(g384,g385)
    c: Coincident(g385,g386)
    c: Coincident(g386,g387)
    c: Coincident(g387,g388)
    c: Coincident(g388,g389)
    c: Coincident(g389,g390)
    c: Coincident(g390,g391)
    c: Coincident(g391,g392)
    c: Coincident(g392,g393)
    c: Coincident(g393,g394)
    c: Coincident(g394,g395)
    c: Coincident(g395,g396)
    c: Coincident(g396,g397)
    c: Coincident(g397,g398)
    c: Coincident(g398,g399)
    c: Coincident(g399,g328)
    c: Coincident(g400,g401)
    c: Coincident(g401,g402)
    c: Coincident(g402,g403)
    c: Coincident(g403,g404)
    c: Coincident(g404,g405)
    c: Coincident(g405,g406)
    c: Coincident(g406,g407)
    c: Coincident(g407,g408)
    c: Coincident(g408,g409)
    c: Coincident(g409,g410)
    c: Coincident(g410,g411)
    c: Coincident(g411,g412)
    c: Coincident(g412,g413)
    c: Coincident(g413,g414)
    c: Coincident(g414,g415)
    c: Coincident(g415,g416)
    c: Coincident(g416,g417)
    c: Coincident(g417,g418)
    c: Coincident(g418,g419)
    c: Coincident(g419,g420)
    c: Coincident(g420,g421)
    c: Coincident(g421,g422)
    c: Coincident(g422,g423)
    c: Coincident(g423,g400)
    c: Coincident(g424,g425)
    c: Coincident(g425,g426)
    c: Coincident(g426,g427)
    c: Coincident(g427,g428)
    c: Coincident(g428,g429)
    c: Coincident(g429,g430)
    c: Coincident(g430,g431)
    c: Coincident(g431,g432)
    c: Coincident(g432,g433)
    c: Coincident(g433,g434)
    c: Coincident(g434,g435)
    c: Coincident(g435,g436)
    c: Coincident(g436,g437)
    c: Coincident(g437,g438)
    c: Coincident(g438,g439)
    c: Coincident(g439,g440)
    c: Coincident(g440,g441)
    c: Coincident(g441,g442)
    c: Coincident(g442,g443)
    c: Coincident(g443,g444)
    c: Coincident(g444,g445)
    c: Coincident(g445,g446)
    c: Coincident(g446,g447)
    c: Coincident(g447,g448)
    c: Coincident(g448,g449)
    c: Coincident(g449,g450)
    c: Coincident(g450,g451)
    c: Coincident(g451,g452)
    c: Coincident(g452,g453)
    c: Coincident(g453,g454)
    c: Coincident(g454,g455)
    c: Coincident(g455,g456)
    c: Coincident(g456,g457)
    c: Coincident(g457,g458)
    c: Coincident(g458,g459)
    c: Coincident(g459,g460)
    c: Coincident(g460,g461)
    c: Coincident(g461,g462)
    c: Coincident(g462,g463)
    c: Coincident(g463,g464)
    c: Coincident(g464,g465)
    c: Coincident(g465,g466)
    c: Coincident(g466,g467)
    c: Coincident(g467,g468)
    c: Coincident(g468,g469)
    c: Coincident(g469,g470)
    c: Coincident(g470,g471)
    c: Coincident(g471,g472)
    c: Coincident(g472,g473)
    c: Coincident(g473,g474)
    c: Coincident(g474,g475)
    c: Coincident(g475,g476)
    c: Coincident(g476,g477)
    c: Coincident(g477,g478)
    c: Coincident(g478,g479)
    c: Coincident(g479,g424)
    c: Coincident(g480,g481)
    c: Coincident(g481,g482)
    c: Coincident(g482,g483)
    c: Coincident(g483,g484)
    c: Coincident(g484,g485)
    c: Coincident(g485,g486)
    c: Coincident(g486,g487)
    c: Coincident(g487,g488)
    c: Coincident(g488,g489)
    c: Coincident(g489,g490)
    c: Coincident(g490,g491)
    c: Coincident(g491,g492)
    c: Coincident(g492,g493)
    c: Coincident(g493,g494)
    c: Coincident(g494,g495)
    c: Coincident(g495,g480)
    c: Coincident(g496,g497)
    c: Coincident(g497,g498)
    c: Coincident(g498,g499)
    c: Coincident(g499,g500)
    c: Coincident(g500,g501)
    c: Coincident(g501,g502)
    c: Coincident(g502,g503)
    c: Coincident(g503,g504)
    c: Coincident(g504,g505)
    c: Coincident(g505,g506)
    c: Coincident(g506,g507)
    c: Coincident(g507,g508)
    c: Coincident(g508,g509)
    c: Coincident(g509,g510)
    c: Coincident(g510,g511)
    c: Coincident(g511,g512)
    c: Coincident(g512,g513)
    c: Coincident(g513,g514)
    c: Coincident(g514,g515)
    c: Coincident(g515,g516)
    c: Coincident(g516,g517)
    c: Coincident(g517,g518)
    c: Coincident(g518,g519)
    c: Coincident(g519,g520)
    c: Coincident(g520,g521)
    c: Coincident(g521,g522)
    c: Coincident(g522,g523)
    c: Coincident(g523,g524)
    c: Coincident(g524,g525)
    c: Coincident(g525,g526)
    c: Coincident(g526,g527)
    c: Coincident(g527,g528)
    c: Coincident(g528,g529)
    c: Coincident(g529,g530)
    c: Coincident(g530,g531)
    c: Coincident(g531,g532)
    c: Coincident(g532,g533)
    c: Coincident(g533,g534)
    c: Coincident(g534,g535)
    c: Coincident(g535,g496)
    c: Coincident(g536,g537)
    c: Coincident(g537,g538)
    c: Coincident(g538,g539)
    c: Coincident(g539,g540)
    c: Coincident(g540,g541)
    c: Coincident(g541,g542)
    c: Coincident(g542,g543)
    c: Coincident(g543,g544)
    c: Coincident(g544,g545)
    c: Coincident(g545,g546)
    c: Coincident(g546,g547)
    c: Coincident(g547,g548)
    c: Coincident(g548,g549)
    c: Coincident(g549,g550)
    c: Coincident(g550,g551)
    c: Coincident(g551,g552)
    c: Coincident(g552,g553)
    c: Coincident(g553,g554)
    c: Coincident(g554,g555)
    c: Coincident(g555,g556)
    c: Coincident(g556,g557)
    c: Coincident(g557,g558)
    c: Coincident(g558,g559)
    c: Coincident(g559,g560)
    c: Coincident(g560,g561)
    c: Coincident(g561,g562)
    c: Coincident(g562,g563)
    c: Coincident(g563,g564)
    c: Coincident(g564,g565)
    c: Coincident(g565,g566)
    c: Coincident(g566,g567)
    c: Coincident(g567,g568)
    c: Coincident(g568,g569)
    c: Coincident(g569,g570)
    c: Coincident(g570,g571)
    c: Coincident(g571,g572)
    c: Coincident(g572,g573)
    c: Coincident(g573,g574)
    c: Coincident(g574,g575)
    c: Coincident(g575,g536)
    c: Coincident(g576,g577)
    c: Coincident(g577,g578)
    c: Coincident(g578,g579)
    c: Coincident(g579,g580)
    c: Coincident(g580,g581)
    c: Coincident(g581,g582)
    c: Coincident(g582,g583)
    c: Coincident(g583,g584)
    c: Coincident(g584,g585)
    c: Coincident(g585,g586)
    c: Coincident(g586,g587)
    c: Coincident(g587,g576)
    c: Coincident(g588,g589)
    c: Coincident(g589,g590)
    c: Coincident(g590,g591)
    c: Coincident(g591,g592)
    c: Coincident(g592,g593)
    c: Coincident(g593,g594)
    c: Coincident(g594,g595)
    c: Coincident(g595,g596)
    c: Coincident(g596,g597)
    c: Coincident(g597,g598)
    c: Coincident(g598,g599)
    c: Coincident(g599,g600)
    c: Coincident(g600,g601)
    c: Coincident(g601,g602)
    c: Coincident(g602,g603)
    c: Coincident(g603,g604)
    c: Coincident(g604,g605)
    c: Coincident(g605,g606)
    c: Coincident(g606,g607)
    c: Coincident(g607,g608)
    c: Coincident(g608,g609)
    c: Coincident(g609,g610)
    c: Coincident(g610,g611)
    c: Coincident(g611,g612)
    c: Coincident(g612,g613)
    c: Coincident(g613,g614)
    c: Coincident(g614,g615)
    c: Coincident(g615,g616)
    c: Coincident(g616,g617)
    c: Coincident(g617,g618)
    c: Coincident(g618,g619)
    c: Coincident(g619,g620)
    c: Coincident(g620,g621)
    c: Coincident(g621,g622)
    c: Coincident(g622,g623)
    c: Coincident(g623,g624)
    c: Coincident(g624,g625)
    c: Coincident(g625,g626)
    c: Coincident(g626,g627)
    c: Coincident(g627,g628)
    c: Coincident(g628,g629)
    c: Coincident(g629,g630)
    c: Coincident(g630,g631)
    c: Coincident(g631,g632)
    c: Coincident(g632,g633)
    c: Coincident(g633,g634)
    c: Coincident(g634,g635)
    c: Coincident(g635,g636)
    c: Coincident(g636,g637)
    c: Coincident(g637,g638)
    c: Coincident(g638,g639)
    c: Coincident(g639,g640)
    c: Coincident(g640,g641)
    c: Coincident(g641,g642)
    c: Coincident(g642,g643)
    c: Coincident(g643,g644)
    c: Coincident(g644,g645)
    c: Coincident(g645,g646)
    c: Coincident(g646,g647)
    c: Coincident(g647,g648)
    c: Coincident(g648,g649)
    c: Coincident(g649,g650)
    c: Coincident(g650,g651)
    c: Coincident(g651,g652)
    c: Coincident(g652,g653)
    c: Coincident(g653,g654)
    c: Coincident(g654,g655)
    c: Coincident(g655,g656)
    c: Coincident(g656,g657)
    c: Coincident(g657,g658)
    c: Coincident(g658,g659)
    c: Coincident(g659,g660)
    c: Coincident(g660,g661)
    c: Coincident(g661,g662)
    c: Coincident(g662,g663)
    c: Coincident(g663,g664)
    c: Coincident(g664,g665)
    c: Coincident(g665,g666)
    c: Coincident(g666,g667)
    c: Coincident(g667,g668)
    c: Coincident(g668,g669)
    c: Coincident(g669,g670)
    c: Coincident(g670,g671)
    c: Coincident(g671,g672)
    c: Coincident(g672,g673)
    c: Coincident(g673,g674)
    c: Coincident(g674,g675)
    c: Coincident(g675,g588)
    c: Coincident(g676,g677)
    c: Coincident(g677,g678)
    c: Coincident(g678,g679)
    c: Coincident(g679,g680)
    c: Coincident(g680,g681)
    c: Coincident(g681,g682)
    c: Coincident(g682,g683)
    c: Coincident(g683,g684)
    c: Coincident(g684,g685)
    c: Coincident(g685,g686)
    c: Coincident(g686,g687)
    c: Coincident(g687,g688)
    c: Coincident(g688,g689)
    c: Coincident(g689,g690)
    c: Coincident(g690,g691)
    c: Coincident(g691,g676)
    c: Coincident(g692,g693)
    c: Coincident(g693,g694)
    c: Coincident(g694,g695)
    c: Coincident(g695,g696)
    c: Coincident(g696,g697)
    c: Coincident(g697,g698)
    c: Coincident(g698,g699)
    c: Coincident(g699,g700)
    c: Coincident(g700,g701)
    c: Coincident(g701,g702)
    c: Coincident(g702,g703)
    c: Coincident(g703,g704)
    c: Coincident(g704,g705)
    c: Coincident(g705,g706)
    c: Coincident(g706,g707)
    c: Coincident(g707,g708)
    c: Coincident(g708,g709)
    c: Coincident(g709,g710)
    c: Coincident(g710,g711)
    c: Coincident(g711,g712)
    c: Coincident(g712,g713)
    c: Coincident(g713,g714)
    c: Coincident(g714,g715)
    c: Coincident(g715,g716)
    c: Coincident(g716,g717)
    c: Coincident(g717,g718)
    c: Coincident(g718,g719)
    c: Coincident(g719,g720)
    c: Coincident(g720,g721)
    c: Coincident(g721,g722)
    c: Coincident(g722,g723)
    c: Coincident(g723,g724)
    c: Coincident(g724,g725)
    c: Coincident(g725,g726)
    c: Coincident(g726,g727)
    c: Coincident(g727,g728)
    c: Coincident(g728,g729)
    c: Coincident(g729,g730)
    c: Coincident(g730,g731)
    c: Coincident(g731,g692)
    c: Coincident(g732,g733)
    c: Coincident(g733,g734)
    c: Coincident(g734,g735)
    c: Coincident(g735,g736)
    c: Coincident(g736,g737)
    c: Coincident(g737,g738)
    c: Coincident(g738,g739)
    c: Coincident(g739,g740)
    c: Coincident(g740,g741)
    c: Coincident(g741,g742)
    c: Coincident(g742,g743)
    c: Coincident(g743,g744)
    c: Coincident(g744,g745)
    c: Coincident(g745,g746)
    c: Coincident(g746,g747)
    c: Coincident(g747,g748)
    c: Coincident(g748,g749)
    c: Coincident(g749,g750)
    c: Coincident(g750,g751)
    c: Coincident(g751,g752)
    c: Coincident(g752,g753)
    c: Coincident(g753,g754)
    c: Coincident(g754,g755)
    c: Coincident(g755,g756)
    c: Coincident(g756,g757)
    c: Coincident(g757,g758)
    c: Coincident(g758,g759)
    c: Coincident(g759,g760)
    c: Coincident(g760,g761)
    c: Coincident(g761,g762)
    c: Coincident(g762,g763)
    c: Coincident(g763,g732)
    c: Coincident(g764,g765)
    c: Coincident(g765,g766)
    c: Coincident(g766,g767)
    c: Coincident(g767,g768)
    c: Coincident(g768,g769)
    c: Coincident(g769,g770)
    c: Coincident(g770,g771)
    c: Coincident(g771,g772)
    c: Coincident(g772,g773)
    c: Coincident(g773,g774)
    c: Coincident(g774,g775)
    c: Coincident(g775,g776)
    c: Coincident(g776,g777)
    c: Coincident(g777,g778)
    c: Coincident(g778,g779)
    c: Coincident(g779,g780)
    c: Coincident(g780,g781)
    c: Coincident(g781,g782)
    c: Coincident(g782,g783)
    c: Coincident(g783,g784)
    c: Coincident(g784,g785)
    c: Coincident(g785,g786)
    c: Coincident(g786,g787)
    c: Coincident(g787,g764)
    c: Coincident(g788,g789)
    c: Coincident(g789,g790)
    c: Coincident(g790,g791)
    c: Coincident(g791,g792)
    c: Coincident(g792,g793)
    c: Coincident(g793,g794)
    c: Coincident(g794,g795)
    c: Coincident(g795,g796)
    c: Coincident(g796,g797)
    c: Coincident(g797,g798)
    c: Coincident(g798,g799)
    c: Coincident(g799,g800)
    c: Coincident(g800,g801)
    c: Coincident(g801,g802)
    c: Coincident(g802,g803)
    c: Coincident(g803,g804)
    c: Coincident(g804,g805)
    c: Coincident(g805,g806)
    c: Coincident(g806,g807)
    c: Coincident(g807,g808)
    c: Coincident(g808,g809)
    c: Coincident(g809,g810)
    c: Coincident(g810,g811)
    c: Coincident(g811,g812)
    c: Coincident(g812,g813)
    c: Coincident(g813,g814)
    c: Coincident(g814,g815)
    c: Coincident(g815,g816)
    c: Coincident(g816,g817)
    c: Coincident(g817,g818)
    c: Coincident(g818,g819)
    c: Coincident(g819,g820)
    c: Coincident(g820,g821)
    c: Coincident(g821,g822)
    c: Coincident(g822,g823)
    c: Coincident(g823,g824)
    c: Coincident(g824,g825)
    c: Coincident(g825,g826)
    c: Coincident(g826,g827)
    c: Coincident(g827,g828)
    c: Coincident(g828,g829)
    c: Coincident(g829,g830)
    c: Coincident(g830,g831)
    c: Coincident(g831,g832)
    c: Coincident(g832,g833)
    c: Coincident(g833,g834)
    c: Coincident(g834,g835)
    c: Coincident(g835,g836)
    c: Coincident(g836,g837)
    c: Coincident(g837,g838)
    c: Coincident(g838,g839)
    c: Coincident(g839,g840)
    c: Coincident(g840,g841)
    c: Coincident(g841,g842)
    c: Coincident(g842,g843)
    c: Coincident(g843,g844)
    c: Coincident(g844,g845)
    c: Coincident(g845,g846)
    c: Coincident(g846,g847)
    c: Coincident(g847,g848)
    c: Coincident(g848,g849)
    c: Coincident(g849,g850)
    c: Coincident(g850,g851)
    c: Coincident(g851,g852)
    c: Coincident(g852,g853)
    c: Coincident(g853,g854)
    c: Coincident(g854,g855)
    c: Coincident(g855,g856)
    c: Coincident(g856,g857)
    c: Coincident(g857,g858)
    c: Coincident(g858,g859)
    c: Coincident(g859,g788)
FEATURE [Sketcher::SketchObject] Sketch034  label="VS003"
  ArcFitTolerance = 1e-06
  FullyConstrained = false
  MakeInternals = false
  Placement = pos=(48.725,7,55.85) rot=(0,1,1;3.14159rad)
  sketch-geometry (860):
    g0: BSplineCurve PolesCount=2 KnotsCount=2 Degree=1 IsPeriodic=0
    g1: BSplineCurve PolesCount=2 KnotsCount=2 Degree=1 IsPeriodic=0
    g2: BSplineCurve PolesCount=2 KnotsCount=2 Degree=1 IsPeriodic=0
    g3: BSplineCurve PolesCount=2 KnotsCount=2 Degree=1 IsPeriodic=0
    g4: BSplineCurve PolesCount=2 KnotsCount=2 Degree=1 IsPeriodic=0
    g5: BSplineCurve PolesCount=2 KnotsCount=2 Degree=1 IsPeriodic=0
    g6: BSplineCurve PolesCount=2 KnotsCount=2 Degree=1 IsPeriodic=0
    g7: BSplineCurve PolesCount=2 KnotsCount=2 Degree=1 IsPeriodic=0
    g8: BSplineCurve PolesCount=2 KnotsCount=2 Degree=1 IsPeriodic=0
    g9: BSplineCurve PolesCount=2 KnotsCount=2 Degree=1 IsPeriodic=0
    g10: BSplineCurve PolesCount=2 KnotsCount=2 Degree=1 IsPeriodic=0
    g11: BSplineCurve PolesCount=2 KnotsCount=2 Degree=1 IsPeriodic=0
    g12: BSplineCurve PolesCount=2 KnotsCount=2 Degree=1 IsPeriodic=0
    g13: BSplineCurve PolesCount=2 KnotsCount=2 Degree=1 IsPeriodic=0
    g14: BSplineCurve PolesCount=2 KnotsCount=2 Degree=1 IsPeriodic=0
    g15: BSplineCurve PolesCount=2 KnotsCount=2 Degree=1 IsPeriodic=0
    g16: BSplineCurve PolesCount=2 KnotsCount=2 Degree=1 IsPeriodic=0
    g17: BSplineCurve PolesCount=2 KnotsCount=2 Degree=1 IsPeriodic=0
    g18: BSplineCurve PolesCount=2 KnotsCount=2 Degree=1 IsPeriodic=0
    g19: BSplineCurve PolesCount=2 KnotsCount=2 Degree=1 IsPeriodic=0
    g20: BSplineCurve PolesCount=2 KnotsCount=2 Degree=1 IsPeriodic=0
    g21: BSplineCurve PolesCount=2 KnotsCount=2 Degree=1 IsPeriodic=0
    g22: BSplineCurve PolesCount=2 KnotsCount=2 Degree=1 IsPeriodic=0
    g23: BSplineCurve PolesCount=2 KnotsCount=2 Degree=1 IsPeriodic=0
    g24: BSplineCurve PolesCount=2 KnotsCount=2 Degree=1 IsPeriodic=0
    g25: BSplineCurve PolesCount=2 KnotsCount=2 Degree=1 IsPeriodic=0
    g26: BSplineCurve PolesCount=2 KnotsCount=2 Degree=1 IsPeriodic=0
    g27: BSplineCurve PolesCount=2 KnotsCount=2 Degree=1 IsPeriodic=0
    g28: BSplineCurve PolesCount=2 KnotsCount=2 Degree=1 IsPeriodic=0
    g29: BSplineCurve PolesCount=2 KnotsCount=2 Degree=1 IsPeriodic=0
    g30: BSplineCurve PolesCount=2 KnotsCount=2 Degree=1 IsPeriodic=0
    g31: BSplineCurve PolesCount=2 KnotsCount=2 Degree=1 IsPeriodic=0
    g32: BSplineCurve PolesCount=2 KnotsCount=2 Degree=1 IsPeriodic=0
    g33: BSplineCurve PolesCount=2 KnotsCount=2 Degree=1 IsPeriodic=0
    g34: BSplineCurve PolesCount=2 KnotsCount=2 Degree=1 IsPeriodic=0
    g35: BSplineCurve PolesCount=2 KnotsCount=2 Degree=1 IsPeriodic=0
    g36: BSplineCurve PolesCount=2 KnotsCount=2 Degree=1 IsPeriodic=0
    g37: BSplineCurve PolesCount=2 KnotsCount=2 Degree=1 IsPeriodic=0
    g38: BSplineCurve PolesCount=2 KnotsCount=2 Degree=1 IsPeriodic=0
    g39: BSplineCurve PolesCount=2 KnotsCount=2 Degree=1 IsPeriodic=0
    g40: BSplineCurve PolesCount=2 KnotsCount=2 Degree=1 IsPeriodic=0
    g41: BSplineCurve PolesCount=2 KnotsCount=2 Degree=1 IsPeriodic=0
    g42: BSplineCurve PolesCount=2 KnotsCount=2 Degree=1 IsPeriodic=0
    g43: BSplineCurve PolesCount=2 KnotsCount=2 Degree=1 IsPeriodic=0
    g44: BSplineCurve PolesCount=2 KnotsCount=2 Degree=1 IsPeriodic=0
    g45: BSplineCurve PolesCount=2 KnotsCount=2 Degree=1 IsPeriodic=0
    g46: BSplineCurve PolesCount=2 KnotsCount=2 Degree=1 IsPeriodic=0
    g47: BSplineCurve PolesCount=2 KnotsCount=2 Degree=1 IsPeriodic=0
    g48: BSplineCurve PolesCount=2 KnotsCount=2 Degree=1 IsPeriodic=0
    g49: BSplineCurve PolesCount=2 KnotsCount=2 Degree=1 IsPeriodic=0
    g50: BSplineCurve PolesCount=2 KnotsCount=2 Degree=1 IsPeriodic=0
    g51: BSplineCurve PolesCount=2 KnotsCount=2 Degree=1 IsPeriodic=0
    g52: BSplineCurve PolesCount=2 KnotsCount=2 Degree=1 IsPeriodic=0
    g53: BSplineCurve PolesCount=2 KnotsCount=2 Degree=1 IsPeriodic=0
    g54: BSplineCurve PolesCount=2 KnotsCount=2 Degree=1 IsPeriodic=0
    g55: BSplineCurve PolesCount=2 KnotsCount=2 Degree=1 IsPeriodic=0
    g56: BSplineCurve PolesCount=2 KnotsCount=2 Degree=1 IsPeriodic=0
    g57: BSplineCurve PolesCount=2 KnotsCount=2 Degree=1 IsPeriodic=0
    g58: BSplineCurve PolesCount=2 KnotsCount=2 Degree=1 IsPeriodic=0
    g59: BSplineCurve PolesCount=2 KnotsCount=2 Degree=1 IsPeriodic=0
    g60: BSplineCurve PolesCount=2 KnotsCount=2 Degree=1 IsPeriodic=0
    g61: BSplineCurve PolesCount=2 KnotsCount=2 Degree=1 IsPeriodic=0
    g62: BSplineCurve PolesCount=2 KnotsCount=2 Degree=1 IsPeriodic=0
    g63: BSplineCurve PolesCount=2 KnotsCount=2 Degree=1 IsPeriodic=0
    g64: BSplineCurve PolesCount=2 KnotsCount=2 Degree=1 IsPeriodic=0
    g65: BSplineCurve PolesCount=2 KnotsCount=2 Degree=1 IsPeriodic=0
    g66: BSplineCurve PolesCount=2 KnotsCount=2 Degree=1 IsPeriodic=0
    g67: BSplineCurve PolesCount=2 KnotsCount=2 Degree=1 IsPeriodic=0
    g68: BSplineCurve PolesCount=2 KnotsCount=2 Degree=1 IsPeriodic=0
    g69: BSplineCurve PolesCount=2 KnotsCount=2 Degree=1 IsPeriodic=0
    g70: BSplineCurve PolesCount=2 KnotsCount=2 Degree=1 IsPeriodic=0
    g71: BSplineCurve PolesCount=2 KnotsCount=2 Degree=1 IsPeriodic=0
    g72: BSplineCurve PolesCount=2 KnotsCount=2 Degree=1 IsPeriodic=0
    g73: BSplineCurve PolesCount=2 KnotsCount=2 Degree=1 IsPeriodic=0
    g74: BSplineCurve PolesCount=2 KnotsCount=2 Degree=1 IsPeriodic=0
    g75: BSplineCurve PolesCount=2 KnotsCount=2 Degree=1 IsPeriodic=0
    g76: BSplineCurve PolesCount=2 KnotsCount=2 Degree=1 IsPeriodic=0
    g77: BSplineCurve PolesCount=2 KnotsCount=2 Degree=1 IsPeriodic=0
    g78: BSplineCurve PolesCount=2 KnotsCount=2 Degree=1 IsPeriodic=0
    g79: BSplineCurve PolesCount=2 KnotsCount=2 Degree=1 IsPeriodic=0
    g80: BSplineCurve PolesCount=2 KnotsCount=2 Degree=1 IsPeriodic=0
    g81: BSplineCurve PolesCount=2 KnotsCount=2 Degree=1 IsPeriodic=0
    g82: BSplineCurve PolesCount=2 KnotsCount=2 Degree=1 IsPeriodic=0
    g83: BSplineCurve PolesCount=2 KnotsCount=2 Degree=1 IsPeriodic=0
    g84: BSplineCurve PolesCount=2 KnotsCount=2 Degree=1 IsPeriodic=0
    g85: BSplineCurve PolesCount=2 KnotsCount=2 Degree=1 IsPeriodic=0
    g86: BSplineCurve PolesCount=2 KnotsCount=2 Degree=1 IsPeriodic=0
    g87: BSplineCurve PolesCount=2 KnotsCount=2 Degree=1 IsPeriodic=0
    g88: BSplineCurve PolesCount=2 KnotsCount=2 Degree=1 IsPeriodic=0
    g89: BSplineCurve PolesCount=2 KnotsCount=2 Degree=1 IsPeriodic=0
    g90: BSplineCurve PolesCount=2 KnotsCount=2 Degree=1 IsPeriodic=0
    g91: BSplineCurve PolesCount=2 KnotsCount=2 Degree=1 IsPeriodic=0
    g92: BSplineCurve PolesCount=2 KnotsCount=2 Degree=1 IsPeriodic=0
    g93: BSplineCurve PolesCount=2 KnotsCount=2 Degree=1 IsPeriodic=0
    g94: BSplineCurve PolesCount=2 KnotsCount=2 Degree=1 IsPeriodic=0
    g95: BSplineCurve PolesCount=2 KnotsCount=2 Degree=1 IsPeriodic=0
    g96: BSplineCurve PolesCount=2 KnotsCount=2 Degree=1 IsPeriodic=0
    g97: BSplineCurve PolesCount=2 KnotsCount=2 Degree=1 IsPeriodic=0
    g98: BSplineCurve PolesCount=2 KnotsCount=2 Degree=1 IsPeriodic=0
    g99: BSplineCurve PolesCount=2 KnotsCount=2 Degree=1 IsPeriodic=0
    g100: BSplineCurve PolesCount=2 KnotsCount=2 Degree=1 IsPeriodic=0
    g101: BSplineCurve PolesCount=2 KnotsCount=2 Degree=1 IsPeriodic=0
    g102: BSplineCurve PolesCount=2 KnotsCount=2 Degree=1 IsPeriodic=0
    g103: BSplineCurve PolesCount=2 KnotsCount=2 Degree=1 IsPeriodic=0
    g104: BSplineCurve PolesCount=2 KnotsCount=2 Degree=1 IsPeriodic=0
    g105: BSplineCurve PolesCount=2 KnotsCount=2 Degree=1 IsPeriodic=0
    g106: BSplineCurve PolesCount=2 KnotsCount=2 Degree=1 IsPeriodic=0
    g107: BSplineCurve PolesCount=2 KnotsCount=2 Degree=1 IsPeriodic=0
    g108: BSplineCurve PolesCount=2 KnotsCount=2 Degree=1 IsPeriodic=0
    g109: BSplineCurve PolesCount=2 KnotsCount=2 Degree=1 IsPeriodic=0
    g110: BSplineCurve PolesCount=2 KnotsCount=2 Degree=1 IsPeriodic=0
    g111: BSplineCurve PolesCount=2 KnotsCount=2 Degree=1 IsPeriodic=0
    g112: BSplineCurve PolesCount=2 KnotsCount=2 Degree=1 IsPeriodic=0
    g113: BSplineCurve PolesCount=2 KnotsCount=2 Degree=1 IsPeriodic=0
    g114: BSplineCurve PolesCount=2 KnotsCount=2 Degree=1 IsPeriodic=0
    g115: BSplineCurve PolesCount=2 KnotsCount=2 Degree=1 IsPeriodic=0
    g116: BSplineCurve PolesCount=2 KnotsCount=2 Degree=1 IsPeriodic=0
    g117: BSplineCurve PolesCount=2 KnotsCount=2 Degree=1 IsPeriodic=0
    g118: BSplineCurve PolesCount=2 KnotsCount=2 Degree=1 IsPeriodic=0
    g119: BSplineCurve PolesCount=2 KnotsCount=2 Degree=1 IsPeriodic=0
    g120: BSplineCurve PolesCount=2 KnotsCount=2 Degree=1 IsPeriodic=0
    g121: BSplineCurve PolesCount=2 KnotsCount=2 Degree=1 IsPeriodic=0
    g122: BSplineCurve PolesCount=2 KnotsCount=2 Degree=1 IsPeriodic=0
    g123: BSplineCurve PolesCount=2 KnotsCount=2 Degree=1 IsPeriodic=0
    g124: BSplineCurve PolesCount=2 KnotsCount=2 Degree=1 IsPeriodic=0
    g125: BSplineCurve PolesCount=2 KnotsCount=2 Degree=1 IsPeriodic=0
    g126: BSplineCurve PolesCount=2 KnotsCount=2 Degree=1 IsPeriodic=0
    g127: BSplineCurve PolesCount=2 KnotsCount=2 Degree=1 IsPeriodic=0
    g128: BSplineCurve PolesCount=2 KnotsCount=2 Degree=1 IsPeriodic=0
    g129: BSplineCurve PolesCount=2 KnotsCount=2 Degree=1 IsPeriodic=0
    g130: BSplineCurve PolesCount=2 KnotsCount=2 Degree=1 IsPeriodic=0
    g131: BSplineCurve PolesCount=2 KnotsCount=2 Degree=1 IsPeriodic=0
    g132: BSplineCurve PolesCount=2 KnotsCount=2 Degree=1 IsPeriodic=0
    g133: BSplineCurve PolesCount=2 KnotsCount=2 Degree=1 IsPeriodic=0
    g134: BSplineCurve PolesCount=2 KnotsCount=2 Degree=1 IsPeriodic=0
    g135: BSplineCurve PolesCount=2 KnotsCount=2 Degree=1 IsPeriodic=0
    g136: BSplineCurve PolesCount=2 KnotsCount=2 Degree=1 IsPeriodic=0
    g137: BSplineCurve PolesCount=2 KnotsCount=2 Degree=1 IsPeriodic=0
    g138: BSplineCurve PolesCount=2 KnotsCount=2 Degree=1 IsPeriodic=0
    g139: BSplineCurve PolesCount=2 KnotsCount=2 Degree=1 IsPeriodic=0
    g140: BSplineCurve PolesCount=2 KnotsCount=2 Degree=1 IsPeriodic=0
    g141: BSplineCurve PolesCount=2 KnotsCount=2 Degree=1 IsPeriodic=0
    g142: BSplineCurve PolesCount=2 KnotsCount=2 Degree=1 IsPeriodic=0
    g143: BSplineCurve PolesCount=2 KnotsCount=2 Degree=1 IsPeriodic=0
    g144: BSplineCurve PolesCount=2 KnotsCount=2 Degree=1 IsPeriodic=0
    g145: BSplineCurve PolesCount=2 KnotsCount=2 Degree=1 IsPeriodic=0
    g146: BSplineCurve PolesCount=2 KnotsCount=2 Degree=1 IsPeriodic=0
    g147: BSplineCurve PolesCount=2 KnotsCount=2 Degree=1 IsPeriodic=0
    g148: BSplineCurve PolesCount=2 KnotsCount=2 Degree=1 IsPeriodic=0
    g149: BSplineCurve PolesCount=2 KnotsCount=2 Degree=1 IsPeriodic=0
    g150: BSplineCurve PolesCount=2 KnotsCount=2 Degree=1 IsPeriodic=0
    g151: BSplineCurve PolesCount=2 KnotsCount=2 Degree=1 IsPeriodic=0
    g152: BSplineCurve PolesCount=2 KnotsCount=2 Degree=1 IsPeriodic=0
    g153: BSplineCurve PolesCount=2 KnotsCount=2 Degree=1 IsPeriodic=0
    g154: BSplineCurve PolesCount=2 KnotsCount=2 Degree=1 IsPeriodic=0
    g155: BSplineCurve PolesCount=2 KnotsCount=2 Degree=1 IsPeriodic=0
    g156: BSplineCurve PolesCount=2 KnotsCount=2 Degree=1 IsPeriodic=0
    g157: BSplineCurve PolesCount=2 KnotsCount=2 Degree=1 IsPeriodic=0
    g158: BSplineCurve PolesCount=2 KnotsCount=2 Degree=1 IsPeriodic=0
    g159: BSplineCurve PolesCount=2 KnotsCount=2 Degree=1 IsPeriodic=0
    g160: BSplineCurve PolesCount=2 KnotsCount=2 Degree=1 IsPeriodic=0
    g161: BSplineCurve PolesCount=2 KnotsCount=2 Degree=1 IsPeriodic=0
    g162: BSplineCurve PolesCount=2 KnotsCount=2 Degree=1 IsPeriodic=0
    g163: BSplineCurve PolesCount=2 KnotsCount=2 Degree=1 IsPeriodic=0
    g164: BSplineCurve PolesCount=2 KnotsCount=2 Degree=1 IsPeriodic=0
    g165: BSplineCurve PolesCount=2 KnotsCount=2 Degree=1 IsPeriodic=0
    g166: BSplineCurve PolesCount=2 KnotsCount=2 Degree=1 IsPeriodic=0
    g167: BSplineCurve PolesCount=2 KnotsCount=2 Degree=1 IsPeriodic=0
    g168: BSplineCurve PolesCount=2 KnotsCount=2 Degree=1 IsPeriodic=0
    g169: BSplineCurve PolesCount=2 KnotsCount=2 Degree=1 IsPeriodic=0
    g170: BSplineCurve PolesCount=2 KnotsCount=2 Degree=1 IsPeriodic=0
    g171: BSplineCurve PolesCount=2 KnotsCount=2 Degree=1 IsPeriodic=0
    g172: BSplineCurve PolesCount=2 KnotsCount=2 Degree=1 IsPeriodic=0
    g173: BSplineCurve PolesCount=2 KnotsCount=2 Degree=1 IsPeriodic=0
    g174: BSplineCurve PolesCount=2 KnotsCount=2 Degree=1 IsPeriodic=0
    g175: BSplineCurve PolesCount=2 KnotsCount=2 Degree=1 IsPeriodic=0
    g176: BSplineCurve PolesCount=2 KnotsCount=2 Degree=1 IsPeriodic=0
    g177: BSplineCurve PolesCount=2 KnotsCount=2 Degree=1 IsPeriodic=0
    g178: BSplineCurve PolesCount=2 KnotsCount=2 Degree=1 IsPeriodic=0
    g179: BSplineCurve PolesCount=2 KnotsCount=2 Degree=1 IsPeriodic=0
    g180: BSplineCurve PolesCount=2 KnotsCount=2 Degree=1 IsPeriodic=0
    g181: BSplineCurve PolesCount=2 KnotsCount=2 Degree=1 IsPeriodic=0
    g182: BSplineCurve PolesCount=2 KnotsCount=2 Degree=1 IsPeriodic=0
    g183: BSplineCurve PolesCount=2 KnotsCount=2 Degree=1 IsPeriodic=0
    g184: BSplineCurve PolesCount=2 KnotsCount=2 Degree=1 IsPeriodic=0
    g185: BSplineCurve PolesCount=2 KnotsCount=2 Degree=1 IsPeriodic=0
    g186: BSplineCurve PolesCount=2 KnotsCount=2 Degree=1 IsPeriodic=0
    g187: BSplineCurve PolesCount=2 KnotsCount=2 Degree=1 IsPeriodic=0
    g188: BSplineCurve PolesCount=2 KnotsCount=2 Degree=1 IsPeriodic=0
    g189: BSplineCurve PolesCount=2 KnotsCount=2 Degree=1 IsPeriodic=0
    g190: BSplineCurve PolesCount=2 KnotsCount=2 Degree=1 IsPeriodic=0
    g191: BSplineCurve PolesCount=2 KnotsCount=2 Degree=1 IsPeriodic=0
    g192: BSplineCurve PolesCount=2 KnotsCount=2 Degree=1 IsPeriodic=0
    g193: BSplineCurve PolesCount=2 KnotsCount=2 Degree=1 IsPeriodic=0
    g194: BSplineCurve PolesCount=2 KnotsCount=2 Degree=1 IsPeriodic=0
    g195: BSplineCurve PolesCount=2 KnotsCount=2 Degree=1 IsPeriodic=0
    g196: BSplineCurve PolesCount=2 KnotsCount=2 Degree=1 IsPeriodic=0
    g197: BSplineCurve PolesCount=2 KnotsCount=2 Degree=1 IsPeriodic=0
    g198: BSplineCurve PolesCount=2 KnotsCount=2 Degree=1 IsPeriodic=0
    g199: BSplineCurve PolesCount=2 KnotsCount=2 Degree=1 IsPeriodic=0
    g200: BSplineCurve PolesCount=2 KnotsCount=2 Degree=1 IsPeriodic=0
    g201: BSplineCurve PolesCount=2 KnotsCount=2 Degree=1 IsPeriodic=0
    g202: BSplineCurve PolesCount=2 KnotsCount=2 Degree=1 IsPeriodic=0
    g203: BSplineCurve PolesCount=2 KnotsCount=2 Degree=1 IsPeriodic=0
    g204: BSplineCurve PolesCount=2 KnotsCount=2 Degree=1 IsPeriodic=0
    g205: BSplineCurve PolesCount=2 KnotsCount=2 Degree=1 IsPeriodic=0
    g206: BSplineCurve PolesCount=2 KnotsCount=2 Degree=1 IsPeriodic=0
    g207: BSplineCurve PolesCount=2 KnotsCount=2 Degree=1 IsPeriodic=0
    g208: BSplineCurve PolesCount=2 KnotsCount=2 Degree=1 IsPeriodic=0
    g209: BSplineCurve PolesCount=2 KnotsCount=2 Degree=1 IsPeriodic=0
    g210: BSplineCurve PolesCount=2 KnotsCount=2 Degree=1 IsPeriodic=0
    g211: BSplineCurve PolesCount=2 KnotsCount=2 Degree=1 IsPeriodic=0
    g212: BSplineCurve PolesCount=2 KnotsCount=2 Degree=1 IsPeriodic=0
    g213: BSplineCurve PolesCount=2 KnotsCount=2 Degree=1 IsPeriodic=0
    g214: BSplineCurve PolesCount=2 KnotsCount=2 Degree=1 IsPeriodic=0
    g215: BSplineCurve PolesCount=2 KnotsCount=2 Degree=1 IsPeriodic=0
    g216: BSplineCurve PolesCount=2 KnotsCount=2 Degree=1 IsPeriodic=0
    g217: BSplineCurve PolesCount=2 KnotsCount=2 Degree=1 IsPeriodic=0
    g218: BSplineCurve PolesCount=2 KnotsCount=2 Degree=1 IsPeriodic=0
    g219: BSplineCurve PolesCount=2 KnotsCount=2 Degree=1 IsPeriodic=0
    g220: BSplineCurve PolesCount=2 KnotsCount=2 Degree=1 IsPeriodic=0
    g221: BSplineCurve PolesCount=2 KnotsCount=2 Degree=1 IsPeriodic=0
    g222: BSplineCurve PolesCount=2 KnotsCount=2 Degree=1 IsPeriodic=0
    g223: BSplineCurve PolesCount=2 KnotsCount=2 Degree=1 IsPeriodic=0
    g224: BSplineCurve PolesCount=2 KnotsCount=2 Degree=1 IsPeriodic=0
    g225: BSplineCurve PolesCount=2 KnotsCount=2 Degree=1 IsPeriodic=0
    g226: BSplineCurve PolesCount=2 KnotsCount=2 Degree=1 IsPeriodic=0
    g227: BSplineCurve PolesCount=2 KnotsCount=2 Degree=1 IsPeriodic=0
    g228: BSplineCurve PolesCount=2 KnotsCount=2 Degree=1 IsPeriodic=0
    g229: BSplineCurve PolesCount=2 KnotsCount=2 Degree=1 IsPeriodic=0
    g230: BSplineCurve PolesCount=2 KnotsCount=2 Degree=1 IsPeriodic=0
    g231: BSplineCurve PolesCount=2 KnotsCount=2 Degree=1 IsPeriodic=0
    g232: BSplineCurve PolesCount=2 KnotsCount=2 Degree=1 IsPeriodic=0
    g233: BSplineCurve PolesCount=2 KnotsCount=2 Degree=1 IsPeriodic=0
    g234: BSplineCurve PolesCount=2 KnotsCount=2 Degree=1 IsPeriodic=0
    g235: BSplineCurve PolesCount=2 KnotsCount=2 Degree=1 IsPeriodic=0
    g236: BSplineCurve PolesCount=2 KnotsCount=2 Degree=1 IsPeriodic=0
    g237: BSplineCurve PolesCount=2 KnotsCount=2 Degree=1 IsPeriodic=0
    g238: BSplineCurve PolesCount=2 KnotsCount=2 Degree=1 IsPeriodic=0
    g239: BSplineCurve PolesCount=2 KnotsCount=2 Degree=1 IsPeriodic=0
    g240: BSplineCurve PolesCount=2 KnotsCount=2 Degree=1 IsPeriodic=0
    g241: BSplineCurve PolesCount=2 KnotsCount=2 Degree=1 IsPeriodic=0
    g242: BSplineCurve PolesCount=2 KnotsCount=2 Degree=1 IsPeriodic=0
    g243: BSplineCurve PolesCount=2 KnotsCount=2 Degree=1 IsPeriodic=0
    g244: BSplineCurve PolesCount=2 KnotsCount=2 Degree=1 IsPeriodic=0
    g245: BSplineCurve PolesCount=2 KnotsCount=2 Degree=1 IsPeriodic=0
    g246: BSplineCurve PolesCount=2 KnotsCount=2 Degree=1 IsPeriodic=0
    g247: BSplineCurve PolesCount=2 KnotsCount=2 Degree=1 IsPeriodic=0
    g248: BSplineCurve PolesCount=2 KnotsCount=2 Degree=1 IsPeriodic=0
    g249: BSplineCurve PolesCount=2 KnotsCount=2 Degree=1 IsPeriodic=0
    g250: BSplineCurve PolesCount=2 KnotsCount=2 Degree=1 IsPeriodic=0
    g251: BSplineCurve PolesCount=2 KnotsCount=2 Degree=1 IsPeriodic=0
    g252: BSplineCurve PolesCount=2 KnotsCount=2 Degree=1 IsPeriodic=0
    g253: BSplineCurve PolesCount=2 KnotsCount=2 Degree=1 IsPeriodic=0
    g254: BSplineCurve PolesCount=2 KnotsCount=2 Degree=1 IsPeriodic=0
    g255: BSplineCurve PolesCount=2 KnotsCount=2 Degree=1 IsPeriodic=0
    g256: BSplineCurve PolesCount=2 KnotsCount=2 Degree=1 IsPeriodic=0
    g257: BSplineCurve PolesCount=2 KnotsCount=2 Degree=1 IsPeriodic=0
    g258: BSplineCurve PolesCount=2 KnotsCount=2 Degree=1 IsPeriodic=0
    g259: BSplineCurve PolesCount=2 KnotsCount=2 Degree=1 IsPeriodic=0
    g260: BSplineCurve PolesCount=2 KnotsCount=2 Degree=1 IsPeriodic=0
    g261: BSplineCurve PolesCount=2 KnotsCount=2 Degree=1 IsPeriodic=0
    g262: BSplineCurve PolesCount=2 KnotsCount=2 Degree=1 IsPeriodic=0
    g263: BSplineCurve PolesCount=2 KnotsCount=2 Degree=1 IsPeriodic=0
    g264: BSplineCurve PolesCount=2 KnotsCount=2 Degree=1 IsPeriodic=0
    g265: BSplineCurve PolesCount=2 KnotsCount=2 Degree=1 IsPeriodic=0
    g266: BSplineCurve PolesCount=2 KnotsCount=2 Degree=1 IsPeriodic=0
    g267: BSplineCurve PolesCount=2 KnotsCount=2 Degree=1 IsPeriodic=0
    g268: BSplineCurve PolesCount=2 KnotsCount=2 Degree=1 IsPeriodic=0
    g269: BSplineCurve PolesCount=2 KnotsCount=2 Degree=1 IsPeriodic=0
    g270: BSplineCurve PolesCount=2 KnotsCount=2 Degree=1 IsPeriodic=0
    g271: BSplineCurve PolesCount=2 KnotsCount=2 Degree=1 IsPeriodic=0
    g272: BSplineCurve PolesCount=2 KnotsCount=2 Degree=1 IsPeriodic=0
    g273: BSplineCurve PolesCount=2 KnotsCount=2 Degree=1 IsPeriodic=0
    g274: BSplineCurve PolesCount=2 KnotsCount=2 Degree=1 IsPeriodic=0
    g275: BSplineCurve PolesCount=2 KnotsCount=2 Degree=1 IsPeriodic=0
    g276: BSplineCurve PolesCount=2 KnotsCount=2 Degree=1 IsPeriodic=0
    g277: BSplineCurve PolesCount=2 KnotsCount=2 Degree=1 IsPeriodic=0
    g278: BSplineCurve PolesCount=2 KnotsCount=2 Degree=1 IsPeriodic=0
    g279: BSplineCurve PolesCount=2 KnotsCount=2 Degree=1 IsPeriodic=0
    g280: BSplineCurve PolesCount=2 KnotsCount=2 Degree=1 IsPeriodic=0
    g281: BSplineCurve PolesCount=2 KnotsCount=2 Degree=1 IsPeriodic=0
    g282: BSplineCurve PolesCount=2 KnotsCount=2 Degree=1 IsPeriodic=0
    g283: BSplineCurve PolesCount=2 KnotsCount=2 Degree=1 IsPeriodic=0
    g284: BSplineCurve PolesCount=2 KnotsCount=2 Degree=1 IsPeriodic=0
    g285: BSplineCurve PolesCount=2 KnotsCount=2 Degree=1 IsPeriodic=0
    g286: BSplineCurve PolesCount=2 KnotsCount=2 Degree=1 IsPeriodic=0
    g287: BSplineCurve PolesCount=2 KnotsCount=2 Degree=1 IsPeriodic=0
    g288: BSplineCurve PolesCount=2 KnotsCount=2 Degree=1 IsPeriodic=0
    g289: BSplineCurve PolesCount=2 KnotsCount=2 Degree=1 IsPeriodic=0
    g290: BSplineCurve PolesCount=2 KnotsCount=2 Degree=1 IsPeriodic=0
    g291: BSplineCurve PolesCount=2 KnotsCount=2 Degree=1 IsPeriodic=0
    g292: BSplineCurve PolesCount=2 KnotsCount=2 Degree=1 IsPeriodic=0
    g293: BSplineCurve PolesCount=2 KnotsCount=2 Degree=1 IsPeriodic=0
    g294: BSplineCurve PolesCount=2 KnotsCount=2 Degree=1 IsPeriodic=0
    g295: BSplineCurve PolesCount=2 KnotsCount=2 Degree=1 IsPeriodic=0
    g296: BSplineCurve PolesCount=2 KnotsCount=2 Degree=1 IsPeriodic=0
    g297: BSplineCurve PolesCount=2 KnotsCount=2 Degree=1 IsPeriodic=0
    g298: BSplineCurve PolesCount=2 KnotsCount=2 Degree=1 IsPeriodic=0
    g299: BSplineCurve PolesCount=2 KnotsCount=2 Degree=1 IsPeriodic=0
    g300: BSplineCurve PolesCount=2 KnotsCount=2 Degree=1 IsPeriodic=0
    g301: BSplineCurve PolesCount=2 KnotsCount=2 Degree=1 IsPeriodic=0
    g302: BSplineCurve PolesCount=2 KnotsCount=2 Degree=1 IsPeriodic=0
    g303: BSplineCurve PolesCount=2 KnotsCount=2 Degree=1 IsPeriodic=0
    g304: BSplineCurve PolesCount=2 KnotsCount=2 Degree=1 IsPeriodic=0
    g305: BSplineCurve PolesCount=2 KnotsCount=2 Degree=1 IsPeriodic=0
    g306: BSplineCurve PolesCount=2 KnotsCount=2 Degree=1 IsPeriodic=0
    g307: BSplineCurve PolesCount=2 KnotsCount=2 Degree=1 IsPeriodic=0
    g308: BSplineCurve PolesCount=2 KnotsCount=2 Degree=1 IsPeriodic=0
    g309: BSplineCurve PolesCount=2 KnotsCount=2 Degree=1 IsPeriodic=0
    g310: BSplineCurve PolesCount=2 KnotsCount=2 Degree=1 IsPeriodic=0
    g311: BSplineCurve PolesCount=2 KnotsCount=2 Degree=1 IsPeriodic=0
    g312: BSplineCurve PolesCount=2 KnotsCount=2 Degree=1 IsPeriodic=0
    g313: BSplineCurve PolesCount=2 KnotsCount=2 Degree=1 IsPeriodic=0
    g314: BSplineCurve PolesCount=2 KnotsCount=2 Degree=1 IsPeriodic=0
    g315: BSplineCurve PolesCount=2 KnotsCount=2 Degree=1 IsPeriodic=0
    g316: BSplineCurve PolesCount=2 KnotsCount=2 Degree=1 IsPeriodic=0
    g317: BSplineCurve PolesCount=2 KnotsCount=2 Degree=1 IsPeriodic=0
    g318: BSplineCurve PolesCount=2 KnotsCount=2 Degree=1 IsPeriodic=0
    g319: BSplineCurve PolesCount=2 KnotsCount=2 Degree=1 IsPeriodic=0
    g320: BSplineCurve PolesCount=2 KnotsCount=2 Degree=1 IsPeriodic=0
    g321: BSplineCurve PolesCount=2 KnotsCount=2 Degree=1 IsPeriodic=0
    g322: BSplineCurve PolesCount=2 KnotsCount=2 Degree=1 IsPeriodic=0
    g323: BSplineCurve PolesCount=2 KnotsCount=2 Degree=1 IsPeriodic=0
    g324: BSplineCurve PolesCount=2 KnotsCount=2 Degree=1 IsPeriodic=0
    g325: BSplineCurve PolesCount=2 KnotsCount=2 Degree=1 IsPeriodic=0
    g326: BSplineCurve PolesCount=2 KnotsCount=2 Degree=1 IsPeriodic=0
    g327: BSplineCurve PolesCount=2 KnotsCount=2 Degree=1 IsPeriodic=0
    g328: BSplineCurve PolesCount=2 KnotsCount=2 Degree=1 IsPeriodic=0
    g329: BSplineCurve PolesCount=2 KnotsCount=2 Degree=1 IsPeriodic=0
    g330: BSplineCurve PolesCount=2 KnotsCount=2 Degree=1 IsPeriodic=0
    g331: BSplineCurve PolesCount=2 KnotsCount=2 Degree=1 IsPeriodic=0
    g332: BSplineCurve PolesCount=2 KnotsCount=2 Degree=1 IsPeriodic=0
    g333: BSplineCurve PolesCount=2 KnotsCount=2 Degree=1 IsPeriodic=0
    g334: BSplineCurve PolesCount=2 KnotsCount=2 Degree=1 IsPeriodic=0
    g335: BSplineCurve PolesCount=2 KnotsCount=2 Degree=1 IsPeriodic=0
    g336: BSplineCurve PolesCount=2 KnotsCount=2 Degree=1 IsPeriodic=0
    g337: BSplineCurve PolesCount=2 KnotsCount=2 Degree=1 IsPeriodic=0
    g338: BSplineCurve PolesCount=2 KnotsCount=2 Degree=1 IsPeriodic=0
    g339: BSplineCurve PolesCount=2 KnotsCount=2 Degree=1 IsPeriodic=0
    g340: BSplineCurve PolesCount=2 KnotsCount=2 Degree=1 IsPeriodic=0
    g341: BSplineCurve PolesCount=2 KnotsCount=2 Degree=1 IsPeriodic=0
    g342: BSplineCurve PolesCount=2 KnotsCount=2 Degree=1 IsPeriodic=0
    g343: BSplineCurve PolesCount=2 KnotsCount=2 Degree=1 IsPeriodic=0
    g344: BSplineCurve PolesCount=2 KnotsCount=2 Degree=1 IsPeriodic=0
    g345: BSplineCurve PolesCount=2 KnotsCount=2 Degree=1 IsPeriodic=0
    g346: BSplineCurve PolesCount=2 KnotsCount=2 Degree=1 IsPeriodic=0
    g347: BSplineCurve PolesCount=2 KnotsCount=2 Degree=1 IsPeriodic=0
    g348: BSplineCurve PolesCount=2 KnotsCount=2 Degree=1 IsPeriodic=0
    g349: BSplineCurve PolesCount=2 KnotsCount=2 Degree=1 IsPeriodic=0
    g350: BSplineCurve PolesCount=2 KnotsCount=2 Degree=1 IsPeriodic=0
    g351: BSplineCurve PolesCount=2 KnotsCount=2 Degree=1 IsPeriodic=0
    g352: BSplineCurve PolesCount=2 KnotsCount=2 Degree=1 IsPeriodic=0
    g353: BSplineCurve PolesCount=2 KnotsCount=2 Degree=1 IsPeriodic=0
    g354: BSplineCurve PolesCount=2 KnotsCount=2 Degree=1 IsPeriodic=0
    g355: BSplineCurve PolesCount=2 KnotsCount=2 Degree=1 IsPeriodic=0
    g356: BSplineCurve PolesCount=2 KnotsCount=2 Degree=1 IsPeriodic=0
    g357: BSplineCurve PolesCount=2 KnotsCount=2 Degree=1 IsPeriodic=0
    g358: BSplineCurve PolesCount=2 KnotsCount=2 Degree=1 IsPeriodic=0
    g359: BSplineCurve PolesCount=2 KnotsCount=2 Degree=1 IsPeriodic=0
    g360: BSplineCurve PolesCount=2 KnotsCount=2 Degree=1 IsPeriodic=0
    g361: BSplineCurve PolesCount=2 KnotsCount=2 Degree=1 IsPeriodic=0
    g362: BSplineCurve PolesCount=2 KnotsCount=2 Degree=1 IsPeriodic=0
    g363: BSplineCurve PolesCount=2 KnotsCount=2 Degree=1 IsPeriodic=0
    g364: BSplineCurve PolesCount=2 KnotsCount=2 Degree=1 IsPeriodic=0
    g365: BSplineCurve PolesCount=2 KnotsCount=2 Degree=1 IsPeriodic=0
    g366: BSplineCurve PolesCount=2 KnotsCount=2 Degree=1 IsPeriodic=0
    g367: BSplineCurve PolesCount=2 KnotsCount=2 Degree=1 IsPeriodic=0
    g368: BSplineCurve PolesCount=2 KnotsCount=2 Degree=1 IsPeriodic=0
    g369: BSplineCurve PolesCount=2 KnotsCount=2 Degree=1 IsPeriodic=0
    g370: BSplineCurve PolesCount=2 KnotsCount=2 Degree=1 IsPeriodic=0
    g371: BSplineCurve PolesCount=2 KnotsCount=2 Degree=1 IsPeriodic=0
    g372: BSplineCurve PolesCount=2 KnotsCount=2 Degree=1 IsPeriodic=0
    g373: BSplineCurve PolesCount=2 KnotsCount=2 Degree=1 IsPeriodic=0
    g374: BSplineCurve PolesCount=2 KnotsCount=2 Degree=1 IsPeriodic=0
    g375: BSplineCurve PolesCount=2 KnotsCount=2 Degree=1 IsPeriodic=0
    g376: BSplineCurve PolesCount=2 KnotsCount=2 Degree=1 IsPeriodic=0
    g377: BSplineCurve PolesCount=2 KnotsCount=2 Degree=1 IsPeriodic=0
    g378: BSplineCurve PolesCount=2 KnotsCount=2 Degree=1 IsPeriodic=0
    g379: BSplineCurve PolesCount=2 KnotsCount=2 Degree=1 IsPeriodic=0
    g380: BSplineCurve PolesCount=2 KnotsCount=2 Degree=1 IsPeriodic=0
    g381: BSplineCurve PolesCount=2 KnotsCount=2 Degree=1 IsPeriodic=0
    g382: BSplineCurve PolesCount=2 KnotsCount=2 Degree=1 IsPeriodic=0
    g383: BSplineCurve PolesCount=2 KnotsCount=2 Degree=1 IsPeriodic=0
    g384: BSplineCurve PolesCount=2 KnotsCount=2 Degree=1 IsPeriodic=0
    g385: BSplineCurve PolesCount=2 KnotsCount=2 Degree=1 IsPeriodic=0
    g386: BSplineCurve PolesCount=2 KnotsCount=2 Degree=1 IsPeriodic=0
    g387: BSplineCurve PolesCount=2 KnotsCount=2 Degree=1 IsPeriodic=0
    g388: BSplineCurve PolesCount=2 KnotsCount=2 Degree=1 IsPeriodic=0
    g389: BSplineCurve PolesCount=2 KnotsCount=2 Degree=1 IsPeriodic=0
    g390: BSplineCurve PolesCount=2 KnotsCount=2 Degree=1 IsPeriodic=0
    g391: BSplineCurve PolesCount=2 KnotsCount=2 Degree=1 IsPeriodic=0
    g392: BSplineCurve PolesCount=2 KnotsCount=2 Degree=1 IsPeriodic=0
    g393: BSplineCurve PolesCount=2 KnotsCount=2 Degree=1 IsPeriodic=0
    g394: BSplineCurve PolesCount=2 KnotsCount=2 Degree=1 IsPeriodic=0
    g395: BSplineCurve PolesCount=2 KnotsCount=2 Degree=1 IsPeriodic=0
    g396: BSplineCurve PolesCount=2 KnotsCount=2 Degree=1 IsPeriodic=0
    g397: BSplineCurve PolesCount=2 KnotsCount=2 Degree=1 IsPeriodic=0
    g398: BSplineCurve PolesCount=2 KnotsCount=2 Degree=1 IsPeriodic=0
    g399: BSplineCurve PolesCount=2 KnotsCount=2 Degree=1 IsPeriodic=0
    ... +460 more geometry lines
  constraints (860):
    c: Coincident(g0,g1)
    c: Coincident(g1,g2)
    c: Coincident(g2,g3)
    c: Coincident(g3,g4)
    c: Coincident(g4,g5)
    c: Coincident(g5,g6)
    c: Coincident(g6,g7)
    c: Coincident(g7,g8)
    c: Coincident(g8,g9)
    c: Coincident(g9,g10)
    c: Coincident(g10,g11)
    c: Coincident(g11,g12)
    c: Coincident(g12,g13)
    c: Coincident(g13,g14)
    c: Coincident(g14,g15)
    c: Coincident(g15,g16)
    c: Coincident(g16,g17)
    c: Coincident(g17,g18)
    c: Coincident(g18,g19)
    c: Coincident(g19,g20)
    c: Coincident(g20,g21)
    c: Coincident(g21,g22)
    c: Coincident(g22,g23)
    c: Coincident(g23,g24)
    c: Coincident(g24,g25)
    c: Coincident(g25,g26)
    c: Coincident(g26,g27)
    c: Coincident(g27,g28)
    c: Coincident(g28,g29)
    c: Coincident(g29,g30)
    c: Coincident(g30,g31)
    c: Coincident(g31,g32)
    c: Coincident(g32,g33)
    c: Coincident(g33,g34)
    c: Coincident(g34,g35)
    c: Coincident(g35,g36)
    c: Coincident(g36,g37)
    c: Coincident(g37,g38)
    c: Coincident(g38,g39)
    c: Coincident(g39,g40)
    c: Coincident(g40,g41)
    c: Coincident(g41,g42)
    c: Coincident(g42,g43)
    c: Coincident(g43,g44)
    c: Coincident(g44,g45)
    c: Coincident(g45,g46)
    c: Coincident(g46,g47)
    c: Coincident(g47,g48)
    c: Coincident(g48,g49)
    c: Coincident(g49,g50)
    c: Coincident(g50,g51)
    c: Coincident(g51,g52)
    c: Coincident(g52,g53)
    c: Coincident(g53,g54)
    c: Coincident(g54,g55)
    c: Coincident(g55,g56)
    c: Coincident(g56,g57)
    c: Coincident(g57,g58)
    c: Coincident(g58,g59)
    c: Coincident(g59,g60)
    c: Coincident(g60,g61)
    c: Coincident(g61,g62)
    c: Coincident(g62,g63)
    c: Coincident(g63,g64)
    c: Coincident(g64,g65)
    c: Coincident(g65,g66)
    c: Coincident(g66,g67)
    c: Coincident(g67,g68)
    c: Coincident(g68,g69)
    c: Coincident(g69,g70)
    c: Coincident(g70,g71)
    c: Coincident(g71,g72)
    c: Coincident(g72,g73)
    c: Coincident(g73,g74)
    c: Coincident(g74,g75)
    c: Coincident(g75,g76)
    c: Coincident(g76,g77)
    c: Coincident(g77,g78)
    c: Coincident(g78,g79)
    c: Coincident(g79,g80)
    c: Coincident(g80,g81)
    c: Coincident(g81,g82)
    c: Coincident(g82,g83)
    c: Coincident(g83,g84)
    c: Coincident(g84,g85)
    c: Coincident(g85,g86)
    c: Coincident(g86,g87)
    c: Coincident(g87,g0)
    c: Coincident(g88,g89)
    c: Coincident(g89,g90)
    c: Coincident(g90,g91)
    c: Coincident(g91,g92)
    c: Coincident(g92,g93)
    c: Coincident(g93,g94)
    c: Coincident(g94,g95)
    c: Coincident(g95,g96)
    c: Coincident(g96,g97)
    c: Coincident(g97,g98)
    c: Coincident(g98,g99)
    c: Coincident(g99,g100)
    c: Coincident(g100,g101)
    c: Coincident(g101,g102)
    c: Coincident(g102,g103)
    c: Coincident(g103,g104)
    c: Coincident(g104,g105)
    c: Coincident(g105,g106)
    c: Coincident(g106,g107)
    c: Coincident(g107,g108)
    c: Coincident(g108,g109)
    c: Coincident(g109,g110)
    c: Coincident(g110,g111)
    c: Coincident(g111,g112)
    c: Coincident(g112,g113)
    c: Coincident(g113,g114)
    c: Coincident(g114,g115)
    c: Coincident(g115,g116)
    c: Coincident(g116,g117)
    c: Coincident(g117,g118)
    c: Coincident(g118,g119)
    c: Coincident(g119,g120)
    c: Coincident(g120,g121)
    c: Coincident(g121,g122)
    c: Coincident(g122,g123)
    c: Coincident(g123,g124)
    c: Coincident(g124,g125)
    c: Coincident(g125,g126)
    c: Coincident(g126,g127)
    c: Coincident(g127,g88)
    c: Coincident(g128,g129)
    c: Coincident(g129,g130)
    c: Coincident(g130,g131)
    c: Coincident(g131,g132)
    c: Coincident(g132,g133)
    c: Coincident(g133,g134)
    c: Coincident(g134,g135)
    c: Coincident(g135,g136)
    c: Coincident(g136,g137)
    c: Coincident(g137,g138)
    c: Coincident(g138,g139)
    c: Coincident(g139,g140)
    c: Coincident(g140,g141)
    c: Coincident(g141,g142)
    c: Coincident(g142,g143)
    c: Coincident(g143,g144)
    c: Coincident(g144,g145)
    c: Coincident(g145,g146)
    c: Coincident(g146,g147)
    c: Coincident(g147,g148)
    c: Coincident(g148,g149)
    c: Coincident(g149,g150)
    c: Coincident(g150,g151)
    c: Coincident(g151,g152)
    c: Coincident(g152,g153)
    c: Coincident(g153,g154)
    c: Coincident(g154,g155)
    c: Coincident(g155,g156)
    c: Coincident(g156,g157)
    c: Coincident(g157,g158)
    c: Coincident(g158,g159)
    c: Coincident(g159,g160)
    c: Coincident(g160,g161)
    c: Coincident(g161,g162)
    c: Coincident(g162,g163)
    c: Coincident(g163,g164)
    c: Coincident(g164,g165)
    c: Coincident(g165,g166)
    c: Coincident(g166,g167)
    c: Coincident(g167,g168)
    c: Coincident(g168,g169)
    c: Coincident(g169,g170)
    c: Coincident(g170,g171)
    c: Coincident(g171,g172)
    c: Coincident(g172,g173)
    c: Coincident(g173,g174)
    c: Coincident(g174,g175)
    c: Coincident(g175,g176)
    c: Coincident(g176,g177)
    c: Coincident(g177,g178)
    c: Coincident(g178,g179)
    c: Coincident(g179,g180)
    c: Coincident(g180,g181)
    c: Coincident(g181,g182)
    c: Coincident(g182,g183)
    c: Coincident(g183,g184)
    c: Coincident(g184,g185)
    c: Coincident(g185,g186)
    c: Coincident(g186,g187)
    c: Coincident(g187,g188)
    c: Coincident(g188,g189)
    c: Coincident(g189,g190)
    c: Coincident(g190,g191)
    c: Coincident(g191,g192)
    c: Coincident(g192,g193)
    c: Coincident(g193,g194)
    c: Coincident(g194,g195)
    c: Coincident(g195,g196)
    c: Coincident(g196,g197)
    c: Coincident(g197,g198)
    c: Coincident(g198,g199)
    c: Coincident(g199,g200)
    c: Coincident(g200,g201)
    c: Coincident(g201,g202)
    c: Coincident(g202,g203)
    c: Coincident(g203,g204)
    c: Coincident(g204,g205)
    c: Coincident(g205,g206)
    c: Coincident(g206,g207)
    c: Coincident(g207,g208)
    c: Coincident(g208,g209)
    c: Coincident(g209,g210)
    c: Coincident(g210,g211)
    c: Coincident(g211,g212)
    c: Coincident(g212,g213)
    c: Coincident(g213,g214)
    c: Coincident(g214,g215)
    c: Coincident(g215,g216)
    c: Coincident(g216,g217)
    c: Coincident(g217,g218)
    c: Coincident(g218,g219)
    c: Coincident(g219,g220)
    c: Coincident(g220,g221)
    c: Coincident(g221,g222)
    c: Coincident(g222,g223)
    c: Coincident(g223,g224)
    c: Coincident(g224,g225)
    c: Coincident(g225,g226)
    c: Coincident(g226,g227)
    c: Coincident(g227,g228)
    c: Coincident(g228,g229)
    c: Coincident(g229,g230)
    c: Coincident(g230,g231)
    c: Coincident(g231,g232)
    c: Coincident(g232,g233)
    c: Coincident(g233,g234)
    c: Coincident(g234,g235)
    c: Coincident(g235,g236)
    c: Coincident(g236,g237)
    c: Coincident(g237,g238)
    c: Coincident(g238,g239)
    c: Coincident(g239,g128)
    c: Coincident(g240,g241)
    c: Coincident(g241,g242)
    c: Coincident(g242,g243)
    c: Coincident(g243,g244)
    c: Coincident(g244,g245)
    c: Coincident(g245,g246)
    c: Coincident(g246,g247)
    c: Coincident(g247,g248)
    c: Coincident(g248,g249)
    c: Coincident(g249,g250)
    c: Coincident(g250,g251)
    c: Coincident(g251,g252)
    c: Coincident(g252,g253)
    c: Coincident(g253,g254)
    c: Coincident(g254,g255)
    c: Coincident(g255,g256)
    c: Coincident(g256,g257)
    c: Coincident(g257,g258)
    c: Coincident(g258,g259)
    c: Coincident(g259,g260)
    c: Coincident(g260,g261)
    c: Coincident(g261,g262)
    c: Coincident(g262,g263)
    c: Coincident(g263,g264)
    c: Coincident(g264,g265)
    c: Coincident(g265,g266)
    c: Coincident(g266,g267)
    c: Coincident(g267,g268)
    c: Coincident(g268,g269)
    c: Coincident(g269,g270)
    c: Coincident(g270,g271)
    c: Coincident(g271,g272)
    c: Coincident(g272,g273)
    c: Coincident(g273,g274)
    c: Coincident(g274,g275)
    c: Coincident(g275,g276)
    c: Coincident(g276,g277)
    c: Coincident(g277,g278)
    c: Coincident(g278,g279)
    c: Coincident(g279,g280)
    c: Coincident(g280,g281)
    c: Coincident(g281,g282)
    c: Coincident(g282,g283)
    c: Coincident(g283,g284)
    c: Coincident(g284,g285)
    c: Coincident(g285,g286)
    c: Coincident(g286,g287)
    c: Coincident(g287,g240)
    c: Coincident(g288,g289)
    c: Coincident(g289,g290)
    c: Coincident(g290,g291)
    c: Coincident(g291,g292)
    c: Coincident(g292,g293)
    c: Coincident(g293,g294)
    c: Coincident(g294,g295)
    c: Coincident(g295,g296)
    c: Coincident(g296,g297)
    c: Coincident(g297,g298)
    c: Coincident(g298,g299)
    c: Coincident(g299,g300)
    c: Coincident(g300,g301)
    c: Coincident(g301,g302)
    c: Coincident(g302,g303)
    c: Coincident(g303,g304)
    c: Coincident(g304,g305)
    c: Coincident(g305,g306)
    c: Coincident(g306,g307)
    c: Coincident(g307,g308)
    c: Coincident(g308,g309)
    c: Coincident(g309,g310)
    c: Coincident(g310,g311)
    c: Coincident(g311,g288)
    c: Coincident(g312,g313)
    c: Coincident(g313,g314)
    c: Coincident(g314,g315)
    c: Coincident(g315,g316)
    c: Coincident(g316,g317)
    c: Coincident(g317,g318)
    c: Coincident(g318,g319)
    c: Coincident(g319,g320)
    c: Coincident(g320,g321)
    c: Coincident(g321,g322)
    c: Coincident(g322,g323)
    c: Coincident(g323,g324)
    c: Coincident(g324,g325)
    c: Coincident(g325,g326)
    c: Coincident(g326,g327)
    c: Coincident(g327,g312)
    c: Coincident(g328,g329)
    c: Coincident(g329,g330)
    c: Coincident(g330,g331)
    c: Coincident(g331,g332)
    c: Coincident(g332,g333)
    c: Coincident(g333,g334)
    c: Coincident(g334,g335)
    c: Coincident(g335,g336)
    c: Coincident(g336,g337)
    c: Coincident(g337,g338)
    c: Coincident(g338,g339)
    c: Coincident(g339,g340)
    c: Coincident(g340,g341)
    c: Coincident(g341,g342)
    c: Coincident(g342,g343)
    c: Coincident(g343,g344)
    c: Coincident(g344,g345)
    c: Coincident(g345,g346)
    c: Coincident(g346,g347)
    c: Coincident(g347,g348)
    c: Coincident(g348,g349)
    c: Coincident(g349,g350)
    c: Coincident(g350,g351)
    c: Coincident(g351,g352)
    c: Coincident(g352,g353)
    c: Coincident(g353,g354)
    c: Coincident(g354,g355)
    c: Coincident(g355,g356)
    c: Coincident(g356,g357)
    c: Coincident(g357,g358)
    c: Coincident(g358,g359)
    c: Coincident(g359,g360)
    c: Coincident(g360,g361)
    c: Coincident(g361,g362)
    c: Coincident(g362,g363)
    c: Coincident(g363,g364)
    c: Coincident(g364,g365)
    c: Coincident(g365,g366)
    c: Coincident(g366,g367)
    c: Coincident(g367,g368)
    c: Coincident(g368,g369)
    c: Coincident(g369,g370)
    c: Coincident(g370,g371)
    c: Coincident(g371,g372)
    c: Coincident(g372,g373)
    c: Coincident(g373,g374)
    c: Coincident(g374,g375)
    c: Coincident(g375,g376)
    c: Coincident(g376,g377)
    c: Coincident(g377,g378)
    c: Coincident(g378,g379)
    c: Coincident(g379,g380)
    c: Coincident(g380,g381)
    c: Coincident(g381,g382)
    c: Coincident(g382,g383)
    c: Coincident(g383,g384)
    c: Coincident(g384,g385)
    c: Coincident(g385,g386)
    c: Coincident(g386,g387)
    c: Coincident(g387,g388)
    c: Coincident(g388,g389)
    c: Coincident(g389,g390)
    c: Coincident(g390,g391)
    c: Coincident(g391,g392)
    c: Coincident(g392,g393)
    c: Coincident(g393,g394)
    c: Coincident(g394,g395)
    c: Coincident(g395,g396)
    c: Coincident(g396,g397)
    c: Coincident(g397,g398)
    c: Coincident(g398,g399)
    c: Coincident(g399,g328)
    c: Coincident(g400,g401)
    c: Coincident(g401,g402)
    c: Coincident(g402,g403)
    c: Coincident(g403,g404)
    c: Coincident(g404,g405)
    c: Coincident(g405,g406)
    c: Coincident(g406,g407)
    c: Coincident(g407,g408)
    c: Coincident(g408,g409)
    c: Coincident(g409,g410)
    c: Coincident(g410,g411)
    c: Coincident(g411,g412)
    c: Coincident(g412,g413)
    c: Coincident(g413,g414)
    c: Coincident(g414,g415)
    c: Coincident(g415,g416)
    c: Coincident(g416,g417)
    c: Coincident(g417,g418)
    c: Coincident(g418,g419)
    c: Coincident(g419,g420)
    c: Coincident(g420,g421)
    c: Coincident(g421,g422)
    c: Coincident(g422,g423)
    c: Coincident(g423,g400)
    c: Coincident(g424,g425)
    c: Coincident(g425,g426)
    c: Coincident(g426,g427)
    c: Coincident(g427,g428)
    c: Coincident(g428,g429)
    c: Coincident(g429,g430)
    c: Coincident(g430,g431)
    c: Coincident(g431,g432)
    c: Coincident(g432,g433)
    c: Coincident(g433,g434)
    c: Coincident(g434,g435)
    c: Coincident(g435,g436)
    c: Coincident(g436,g437)
    c: Coincident(g437,g438)
    c: Coincident(g438,g439)
    c: Coincident(g439,g440)
    c: Coincident(g440,g441)
    c: Coincident(g441,g442)
    c: Coincident(g442,g443)
    c: Coincident(g443,g444)
    c: Coincident(g444,g445)
    c: Coincident(g445,g446)
    c: Coincident(g446,g447)
    c: Coincident(g447,g448)
    c: Coincident(g448,g449)
    c: Coincident(g449,g450)
    c: Coincident(g450,g451)
    c: Coincident(g451,g452)
    c: Coincident(g452,g453)
    c: Coincident(g453,g454)
    c: Coincident(g454,g455)
    c: Coincident(g455,g456)
    c: Coincident(g456,g457)
    c: Coincident(g457,g458)
    c: Coincident(g458,g459)
    c: Coincident(g459,g460)
    c: Coincident(g460,g461)
    c: Coincident(g461,g462)
    c: Coincident(g462,g463)
    c: Coincident(g463,g464)
    c: Coincident(g464,g465)
    c: Coincident(g465,g466)
    c: Coincident(g466,g467)
    c: Coincident(g467,g468)
    c: Coincident(g468,g469)
    c: Coincident(g469,g470)
    c: Coincident(g470,g471)
    c: Coincident(g471,g472)
    c: Coincident(g472,g473)
    c: Coincident(g473,g474)
    c: Coincident(g474,g475)
    c: Coincident(g475,g476)
    c: Coincident(g476,g477)
    c: Coincident(g477,g478)
    c: Coincident(g478,g479)
    c: Coincident(g479,g424)
    c: Coincident(g480,g481)
    c: Coincident(g481,g482)
    c: Coincident(g482,g483)
    c: Coincident(g483,g484)
    c: Coincident(g484,g485)
    c: Coincident(g485,g486)
    c: Coincident(g486,g487)
    c: Coincident(g487,g488)
    c: Coincident(g488,g489)
    c: Coincident(g489,g490)
    c: Coincident(g490,g491)
    c: Coincident(g491,g492)
    c: Coincident(g492,g493)
    c: Coincident(g493,g494)
    c: Coincident(g494,g495)
    c: Coincident(g495,g480)
    c: Coincident(g496,g497)
    c: Coincident(g497,g498)
    c: Coincident(g498,g499)
    c: Coincident(g499,g500)
    c: Coincident(g500,g501)
    c: Coincident(g501,g502)
    c: Coincident(g502,g503)
    c: Coincident(g503,g504)
    c: Coincident(g504,g505)
    c: Coincident(g505,g506)
    c: Coincident(g506,g507)
    c: Coincident(g507,g508)
    c: Coincident(g508,g509)
    c: Coincident(g509,g510)
    c: Coincident(g510,g511)
    c: Coincident(g511,g512)
    c: Coincident(g512,g513)
    c: Coincident(g513,g514)
    c: Coincident(g514,g515)
    c: Coincident(g515,g516)
    c: Coincident(g516,g517)
    c: Coincident(g517,g518)
    c: Coincident(g518,g519)
    c: Coincident(g519,g520)
    c: Coincident(g520,g521)
    c: Coincident(g521,g522)
    c: Coincident(g522,g523)
    c: Coincident(g523,g524)
    c: Coincident(g524,g525)
    c: Coincident(g525,g526)
    c: Coincident(g526,g527)
    c: Coincident(g527,g528)
    c: Coincident(g528,g529)
    c: Coincident(g529,g530)
    c: Coincident(g530,g531)
    c: Coincident(g531,g532)
    c: Coincident(g532,g533)
    c: Coincident(g533,g534)
    c: Coincident(g534,g535)
    c: Coincident(g535,g496)
    c: Coincident(g536,g537)
    c: Coincident(g537,g538)
    c: Coincident(g538,g539)
    c: Coincident(g539,g540)
    c: Coincident(g540,g541)
    c: Coincident(g541,g542)
    c: Coincident(g542,g543)
    c: Coincident(g543,g544)
    c: Coincident(g544,g545)
    c: Coincident(g545,g546)
    c: Coincident(g546,g547)
    c: Coincident(g547,g548)
    c: Coincident(g548,g549)
    c: Coincident(g549,g550)
    c: Coincident(g550,g551)
    c: Coincident(g551,g552)
    c: Coincident(g552,g553)
    c: Coincident(g553,g554)
    c: Coincident(g554,g555)
    c: Coincident(g555,g556)
    c: Coincident(g556,g557)
    c: Coincident(g557,g558)
    c: Coincident(g558,g559)
    c: Coincident(g559,g560)
    c: Coincident(g560,g561)
    c: Coincident(g561,g562)
    c: Coincident(g562,g563)
    c: Coincident(g563,g564)
    c: Coincident(g564,g565)
    c: Coincident(g565,g566)
    c: Coincident(g566,g567)
    c: Coincident(g567,g568)
    c: Coincident(g568,g569)
    c: Coincident(g569,g570)
    c: Coincident(g570,g571)
    c: Coincident(g571,g572)
    c: Coincident(g572,g573)
    c: Coincident(g573,g574)
    c: Coincident(g574,g575)
    c: Coincident(g575,g536)
    c: Coincident(g576,g577)
    c: Coincident(g577,g578)
    c: Coincident(g578,g579)
    c: Coincident(g579,g580)
    c: Coincident(g580,g581)
    c: Coincident(g581,g582)
    c: Coincident(g582,g583)
    c: Coincident(g583,g584)
    c: Coincident(g584,g585)
    c: Coincident(g585,g586)
    c: Coincident(g586,g587)
    c: Coincident(g587,g576)
    c: Coincident(g588,g589)
    c: Coincident(g589,g590)
    c: Coincident(g590,g591)
    c: Coincident(g591,g592)
    c: Coincident(g592,g593)
    c: Coincident(g593,g594)
    c: Coincident(g594,g595)
    c: Coincident(g595,g596)
    c: Coincident(g596,g597)
    c: Coincident(g597,g598)
    c: Coincident(g598,g599)
    c: Coincident(g599,g600)
    c: Coincident(g600,g601)
    c: Coincident(g601,g602)
    c: Coincident(g602,g603)
    c: Coincident(g603,g604)
    c: Coincident(g604,g605)
    c: Coincident(g605,g606)
    c: Coincident(g606,g607)
    c: Coincident(g607,g608)
    c: Coincident(g608,g609)
    c: Coincident(g609,g610)
    c: Coincident(g610,g611)
    c: Coincident(g611,g612)
    c: Coincident(g612,g613)
    c: Coincident(g613,g614)
    c: Coincident(g614,g615)
    c: Coincident(g615,g616)
    c: Coincident(g616,g617)
    c: Coincident(g617,g618)
    c: Coincident(g618,g619)
    c: Coincident(g619,g620)
    c: Coincident(g620,g621)
    c: Coincident(g621,g622)
    c: Coincident(g622,g623)
    c: Coincident(g623,g624)
    c: Coincident(g624,g625)
    c: Coincident(g625,g626)
    c: Coincident(g626,g627)
    c: Coincident(g627,g628)
    c: Coincident(g628,g629)
    c: Coincident(g629,g630)
    c: Coincident(g630,g631)
    c: Coincident(g631,g632)
    c: Coincident(g632,g633)
    c: Coincident(g633,g634)
    c: Coincident(g634,g635)
    c: Coincident(g635,g636)
    c: Coincident(g636,g637)
    c: Coincident(g637,g638)
    c: Coincident(g638,g639)
    c: Coincident(g639,g640)
    c: Coincident(g640,g641)
    c: Coincident(g641,g642)
    c: Coincident(g642,g643)
    c: Coincident(g643,g644)
    c: Coincident(g644,g645)
    c: Coincident(g645,g646)
    c: Coincident(g646,g647)
    c: Coincident(g647,g648)
    c: Coincident(g648,g649)
    c: Coincident(g649,g650)
    c: Coincident(g650,g651)
    c: Coincident(g651,g652)
    c: Coincident(g652,g653)
    c: Coincident(g653,g654)
    c: Coincident(g654,g655)
    c: Coincident(g655,g656)
    c: Coincident(g656,g657)
    c: Coincident(g657,g658)
    c: Coincident(g658,g659)
    c: Coincident(g659,g660)
    c: Coincident(g660,g661)
    c: Coincident(g661,g662)
    c: Coincident(g662,g663)
    c: Coincident(g663,g664)
    c: Coincident(g664,g665)
    c: Coincident(g665,g666)
    c: Coincident(g666,g667)
    c: Coincident(g667,g668)
    c: Coincident(g668,g669)
    c: Coincident(g669,g670)
    c: Coincident(g670,g671)
    c: Coincident(g671,g672)
    c: Coincident(g672,g673)
    c: Coincident(g673,g674)
    c: Coincident(g674,g675)
    c: Coincident(g675,g588)
    c: Coincident(g676,g677)
    c: Coincident(g677,g678)
    c: Coincident(g678,g679)
    c: Coincident(g679,g680)
    c: Coincident(g680,g681)
    c: Coincident(g681,g682)
    c: Coincident(g682,g683)
    c: Coincident(g683,g684)
    c: Coincident(g684,g685)
    c: Coincident(g685,g686)
    c: Coincident(g686,g687)
    c: Coincident(g687,g688)
    c: Coincident(g688,g689)
    c: Coincident(g689,g690)
    c: Coincident(g690,g691)
    c: Coincident(g691,g676)
    c: Coincident(g692,g693)
    c: Coincident(g693,g694)
    c: Coincident(g694,g695)
    c: Coincident(g695,g696)
    c: Coincident(g696,g697)
    c: Coincident(g697,g698)
    c: Coincident(g698,g699)
    c: Coincident(g699,g700)
    c: Coincident(g700,g701)
    c: Coincident(g701,g702)
    c: Coincident(g702,g703)
    c: Coincident(g703,g704)
    c: Coincident(g704,g705)
    c: Coincident(g705,g706)
    c: Coincident(g706,g707)
    c: Coincident(g707,g708)
    c: Coincident(g708,g709)
    c: Coincident(g709,g710)
    c: Coincident(g710,g711)
    c: Coincident(g711,g712)
    c: Coincident(g712,g713)
    c: Coincident(g713,g714)
    c: Coincident(g714,g715)
    c: Coincident(g715,g716)
    c: Coincident(g716,g717)
    c: Coincident(g717,g718)
    c: Coincident(g718,g719)
    c: Coincident(g719,g720)
    c: Coincident(g720,g721)
    c: Coincident(g721,g722)
    c: Coincident(g722,g723)
    c: Coincident(g723,g724)
    c: Coincident(g724,g725)
    c: Coincident(g725,g726)
    c: Coincident(g726,g727)
    c: Coincident(g727,g728)
    c: Coincident(g728,g729)
    c: Coincident(g729,g730)
    c: Coincident(g730,g731)
    c: Coincident(g731,g692)
    c: Coincident(g732,g733)
    c: Coincident(g733,g734)
    c: Coincident(g734,g735)
    c: Coincident(g735,g736)
    c: Coincident(g736,g737)
    c: Coincident(g737,g738)
    c: Coincident(g738,g739)
    c: Coincident(g739,g740)
    c: Coincident(g740,g741)
    c: Coincident(g741,g742)
    c: Coincident(g742,g743)
    c: Coincident(g743,g744)
    c: Coincident(g744,g745)
    c: Coincident(g745,g746)
    c: Coincident(g746,g747)
    c: Coincident(g747,g748)
    c: Coincident(g748,g749)
    c: Coincident(g749,g750)
    c: Coincident(g750,g751)
    c: Coincident(g751,g752)
    c: Coincident(g752,g753)
    c: Coincident(g753,g754)
    c: Coincident(g754,g755)
    c: Coincident(g755,g756)
    c: Coincident(g756,g757)
    c: Coincident(g757,g758)
    c: Coincident(g758,g759)
    c: Coincident(g759,g760)
    c: Coincident(g760,g761)
    c: Coincident(g761,g762)
    c: Coincident(g762,g763)
    c: Coincident(g763,g732)
    c: Coincident(g764,g765)
    c: Coincident(g765,g766)
    c: Coincident(g766,g767)
    c: Coincident(g767,g768)
    c: Coincident(g768,g769)
    c: Coincident(g769,g770)
    c: Coincident(g770,g771)
    c: Coincident(g771,g772)
    c: Coincident(g772,g773)
    c: Coincident(g773,g774)
    c: Coincident(g774,g775)
    c: Coincident(g775,g776)
    c: Coincident(g776,g777)
    c: Coincident(g777,g778)
    c: Coincident(g778,g779)
    c: Coincident(g779,g780)
    c: Coincident(g780,g781)
    c: Coincident(g781,g782)
    c: Coincident(g782,g783)
    c: Coincident(g783,g784)
    c: Coincident(g784,g785)
    c: Coincident(g785,g786)
    c: Coincident(g786,g787)
    c: Coincident(g787,g764)
    c: Coincident(g788,g789)
    c: Coincident(g789,g790)
    c: Coincident(g790,g791)
    c: Coincident(g791,g792)
    c: Coincident(g792,g793)
    c: Coincident(g793,g794)
    c: Coincident(g794,g795)
    c: Coincident(g795,g796)
    c: Coincident(g796,g797)
    c: Coincident(g797,g798)
    c: Coincident(g798,g799)
    c: Coincident(g799,g800)
    c: Coincident(g800,g801)
    c: Coincident(g801,g802)
    c: Coincident(g802,g803)
    c: Coincident(g803,g804)
    c: Coincident(g804,g805)
    c: Coincident(g805,g806)
    c: Coincident(g806,g807)
    c: Coincident(g807,g808)
    c: Coincident(g808,g809)
    c: Coincident(g809,g810)
    c: Coincident(g810,g811)
    c: Coincident(g811,g812)
    c: Coincident(g812,g813)
    c: Coincident(g813,g814)
    c: Coincident(g814,g815)
    c: Coincident(g815,g816)
    c: Coincident(g816,g817)
    c: Coincident(g817,g818)
    c: Coincident(g818,g819)
    c: Coincident(g819,g820)
    c: Coincident(g820,g821)
    c: Coincident(g821,g822)
    c: Coincident(g822,g823)
    c: Coincident(g823,g824)
    c: Coincident(g824,g825)
    c: Coincident(g825,g826)
    c: Coincident(g826,g827)
    c: Coincident(g827,g828)
    c: Coincident(g828,g829)
    c: Coincident(g829,g830)
    c: Coincident(g830,g831)
    c: Coincident(g831,g832)
    c: Coincident(g832,g833)
    c: Coincident(g833,g834)
    c: Coincident(g834,g835)
    c: Coincident(g835,g836)
    c: Coincident(g836,g837)
    c: Coincident(g837,g838)
    c: Coincident(g838,g839)
    c: Coincident(g839,g840)
    c: Coincident(g840,g841)
    c: Coincident(g841,g842)
    c: Coincident(g842,g843)
    c: Coincident(g843,g844)
    c: Coincident(g844,g845)
    c: Coincident(g845,g846)
    c: Coincident(g846,g847)
    c: Coincident(g847,g848)
    c: Coincident(g848,g849)
    c: Coincident(g849,g850)
    c: Coincident(g850,g851)
    c: Coincident(g851,g852)
    c: Coincident(g852,g853)
    c: Coincident(g853,g854)
    c: Coincident(g854,g855)
    c: Coincident(g855,g856)
    c: Coincident(g856,g857)
    c: Coincident(g857,g858)
    c: Coincident(g858,g859)
    c: Coincident(g859,g788)
FEATURE [Sketcher::SketchObject] Sketch035  label="VS004"
  ArcFitTolerance = 1e-06
  FullyConstrained = false
  MakeInternals = false
  Placement = pos=(48.725,7,55.85) rot=(0,1,1;3.14159rad)
  sketch-geometry (860):
    g0: BSplineCurve PolesCount=2 KnotsCount=2 Degree=1 IsPeriodic=0
    g1: BSplineCurve PolesCount=2 KnotsCount=2 Degree=1 IsPeriodic=0
    g2: BSplineCurve PolesCount=2 KnotsCount=2 Degree=1 IsPeriodic=0
    g3: BSplineCurve PolesCount=2 KnotsCount=2 Degree=1 IsPeriodic=0
    g4: BSplineCurve PolesCount=2 KnotsCount=2 Degree=1 IsPeriodic=0
    g5: BSplineCurve PolesCount=2 KnotsCount=2 Degree=1 IsPeriodic=0
    g6: BSplineCurve PolesCount=2 KnotsCount=2 Degree=1 IsPeriodic=0
    g7: BSplineCurve PolesCount=2 KnotsCount=2 Degree=1 IsPeriodic=0
    g8: BSplineCurve PolesCount=2 KnotsCount=2 Degree=1 IsPeriodic=0
    g9: BSplineCurve PolesCount=2 KnotsCount=2 Degree=1 IsPeriodic=0
    g10: BSplineCurve PolesCount=2 KnotsCount=2 Degree=1 IsPeriodic=0
    g11: BSplineCurve PolesCount=2 KnotsCount=2 Degree=1 IsPeriodic=0
    g12: BSplineCurve PolesCount=2 KnotsCount=2 Degree=1 IsPeriodic=0
    g13: BSplineCurve PolesCount=2 KnotsCount=2 Degree=1 IsPeriodic=0
    g14: BSplineCurve PolesCount=2 KnotsCount=2 Degree=1 IsPeriodic=0
    g15: BSplineCurve PolesCount=2 KnotsCount=2 Degree=1 IsPeriodic=0
    g16: BSplineCurve PolesCount=2 KnotsCount=2 Degree=1 IsPeriodic=0
    g17: BSplineCurve PolesCount=2 KnotsCount=2 Degree=1 IsPeriodic=0
    g18: BSplineCurve PolesCount=2 KnotsCount=2 Degree=1 IsPeriodic=0
    g19: BSplineCurve PolesCount=2 KnotsCount=2 Degree=1 IsPeriodic=0
    g20: BSplineCurve PolesCount=2 KnotsCount=2 Degree=1 IsPeriodic=0
    g21: BSplineCurve PolesCount=2 KnotsCount=2 Degree=1 IsPeriodic=0
    g22: BSplineCurve PolesCount=2 KnotsCount=2 Degree=1 IsPeriodic=0
    g23: BSplineCurve PolesCount=2 KnotsCount=2 Degree=1 IsPeriodic=0
    g24: BSplineCurve PolesCount=2 KnotsCount=2 Degree=1 IsPeriodic=0
    g25: BSplineCurve PolesCount=2 KnotsCount=2 Degree=1 IsPeriodic=0
    g26: BSplineCurve PolesCount=2 KnotsCount=2 Degree=1 IsPeriodic=0
    g27: BSplineCurve PolesCount=2 KnotsCount=2 Degree=1 IsPeriodic=0
    g28: BSplineCurve PolesCount=2 KnotsCount=2 Degree=1 IsPeriodic=0
    g29: BSplineCurve PolesCount=2 KnotsCount=2 Degree=1 IsPeriodic=0
    g30: BSplineCurve PolesCount=2 KnotsCount=2 Degree=1 IsPeriodic=0
    g31: BSplineCurve PolesCount=2 KnotsCount=2 Degree=1 IsPeriodic=0
    g32: BSplineCurve PolesCount=2 KnotsCount=2 Degree=1 IsPeriodic=0
    g33: BSplineCurve PolesCount=2 KnotsCount=2 Degree=1 IsPeriodic=0
    g34: BSplineCurve PolesCount=2 KnotsCount=2 Degree=1 IsPeriodic=0
    g35: BSplineCurve PolesCount=2 KnotsCount=2 Degree=1 IsPeriodic=0
    g36: BSplineCurve PolesCount=2 KnotsCount=2 Degree=1 IsPeriodic=0
    g37: BSplineCurve PolesCount=2 KnotsCount=2 Degree=1 IsPeriodic=0
    g38: BSplineCurve PolesCount=2 KnotsCount=2 Degree=1 IsPeriodic=0
    g39: BSplineCurve PolesCount=2 KnotsCount=2 Degree=1 IsPeriodic=0
    g40: BSplineCurve PolesCount=2 KnotsCount=2 Degree=1 IsPeriodic=0
    g41: BSplineCurve PolesCount=2 KnotsCount=2 Degree=1 IsPeriodic=0
    g42: BSplineCurve PolesCount=2 KnotsCount=2 Degree=1 IsPeriodic=0
    g43: BSplineCurve PolesCount=2 KnotsCount=2 Degree=1 IsPeriodic=0
    g44: BSplineCurve PolesCount=2 KnotsCount=2 Degree=1 IsPeriodic=0
    g45: BSplineCurve PolesCount=2 KnotsCount=2 Degree=1 IsPeriodic=0
    g46: BSplineCurve PolesCount=2 KnotsCount=2 Degree=1 IsPeriodic=0
    g47: BSplineCurve PolesCount=2 KnotsCount=2 Degree=1 IsPeriodic=0
    g48: BSplineCurve PolesCount=2 KnotsCount=2 Degree=1 IsPeriodic=0
    g49: BSplineCurve PolesCount=2 KnotsCount=2 Degree=1 IsPeriodic=0
    g50: BSplineCurve PolesCount=2 KnotsCount=2 Degree=1 IsPeriodic=0
    g51: BSplineCurve PolesCount=2 KnotsCount=2 Degree=1 IsPeriodic=0
    g52: BSplineCurve PolesCount=2 KnotsCount=2 Degree=1 IsPeriodic=0
    g53: BSplineCurve PolesCount=2 KnotsCount=2 Degree=1 IsPeriodic=0
    g54: BSplineCurve PolesCount=2 KnotsCount=2 Degree=1 IsPeriodic=0
    g55: BSplineCurve PolesCount=2 KnotsCount=2 Degree=1 IsPeriodic=0
    g56: BSplineCurve PolesCount=2 KnotsCount=2 Degree=1 IsPeriodic=0
    g57: BSplineCurve PolesCount=2 KnotsCount=2 Degree=1 IsPeriodic=0
    g58: BSplineCurve PolesCount=2 KnotsCount=2 Degree=1 IsPeriodic=0
    g59: BSplineCurve PolesCount=2 KnotsCount=2 Degree=1 IsPeriodic=0
    g60: BSplineCurve PolesCount=2 KnotsCount=2 Degree=1 IsPeriodic=0
    g61: BSplineCurve PolesCount=2 KnotsCount=2 Degree=1 IsPeriodic=0
    g62: BSplineCurve PolesCount=2 KnotsCount=2 Degree=1 IsPeriodic=0
    g63: BSplineCurve PolesCount=2 KnotsCount=2 Degree=1 IsPeriodic=0
    g64: BSplineCurve PolesCount=2 KnotsCount=2 Degree=1 IsPeriodic=0
    g65: BSplineCurve PolesCount=2 KnotsCount=2 Degree=1 IsPeriodic=0
    g66: BSplineCurve PolesCount=2 KnotsCount=2 Degree=1 IsPeriodic=0
    g67: BSplineCurve PolesCount=2 KnotsCount=2 Degree=1 IsPeriodic=0
    g68: BSplineCurve PolesCount=2 KnotsCount=2 Degree=1 IsPeriodic=0
    g69: BSplineCurve PolesCount=2 KnotsCount=2 Degree=1 IsPeriodic=0
    g70: BSplineCurve PolesCount=2 KnotsCount=2 Degree=1 IsPeriodic=0
    g71: BSplineCurve PolesCount=2 KnotsCount=2 Degree=1 IsPeriodic=0
    g72: BSplineCurve PolesCount=2 KnotsCount=2 Degree=1 IsPeriodic=0
    g73: BSplineCurve PolesCount=2 KnotsCount=2 Degree=1 IsPeriodic=0
    g74: BSplineCurve PolesCount=2 KnotsCount=2 Degree=1 IsPeriodic=0
    g75: BSplineCurve PolesCount=2 KnotsCount=2 Degree=1 IsPeriodic=0
    g76: BSplineCurve PolesCount=2 KnotsCount=2 Degree=1 IsPeriodic=0
    g77: BSplineCurve PolesCount=2 KnotsCount=2 Degree=1 IsPeriodic=0
    g78: BSplineCurve PolesCount=2 KnotsCount=2 Degree=1 IsPeriodic=0
    g79: BSplineCurve PolesCount=2 KnotsCount=2 Degree=1 IsPeriodic=0
    g80: BSplineCurve PolesCount=2 KnotsCount=2 Degree=1 IsPeriodic=0
    g81: BSplineCurve PolesCount=2 KnotsCount=2 Degree=1 IsPeriodic=0
    g82: BSplineCurve PolesCount=2 KnotsCount=2 Degree=1 IsPeriodic=0
    g83: BSplineCurve PolesCount=2 KnotsCount=2 Degree=1 IsPeriodic=0
    g84: BSplineCurve PolesCount=2 KnotsCount=2 Degree=1 IsPeriodic=0
    g85: BSplineCurve PolesCount=2 KnotsCount=2 Degree=1 IsPeriodic=0
    g86: BSplineCurve PolesCount=2 KnotsCount=2 Degree=1 IsPeriodic=0
    g87: BSplineCurve PolesCount=2 KnotsCount=2 Degree=1 IsPeriodic=0
    g88: BSplineCurve PolesCount=2 KnotsCount=2 Degree=1 IsPeriodic=0
    g89: BSplineCurve PolesCount=2 KnotsCount=2 Degree=1 IsPeriodic=0
    g90: BSplineCurve PolesCount=2 KnotsCount=2 Degree=1 IsPeriodic=0
    g91: BSplineCurve PolesCount=2 KnotsCount=2 Degree=1 IsPeriodic=0
    g92: BSplineCurve PolesCount=2 KnotsCount=2 Degree=1 IsPeriodic=0
    g93: BSplineCurve PolesCount=2 KnotsCount=2 Degree=1 IsPeriodic=0
    g94: BSplineCurve PolesCount=2 KnotsCount=2 Degree=1 IsPeriodic=0
    g95: BSplineCurve PolesCount=2 KnotsCount=2 Degree=1 IsPeriodic=0
    g96: BSplineCurve PolesCount=2 KnotsCount=2 Degree=1 IsPeriodic=0
    g97: BSplineCurve PolesCount=2 KnotsCount=2 Degree=1 IsPeriodic=0
    g98: BSplineCurve PolesCount=2 KnotsCount=2 Degree=1 IsPeriodic=0
    g99: BSplineCurve PolesCount=2 KnotsCount=2 Degree=1 IsPeriodic=0
    g100: BSplineCurve PolesCount=2 KnotsCount=2 Degree=1 IsPeriodic=0
    g101: BSplineCurve PolesCount=2 KnotsCount=2 Degree=1 IsPeriodic=0
    g102: BSplineCurve PolesCount=2 KnotsCount=2 Degree=1 IsPeriodic=0
    g103: BSplineCurve PolesCount=2 KnotsCount=2 Degree=1 IsPeriodic=0
    g104: BSplineCurve PolesCount=2 KnotsCount=2 Degree=1 IsPeriodic=0
    g105: BSplineCurve PolesCount=2 KnotsCount=2 Degree=1 IsPeriodic=0
    g106: BSplineCurve PolesCount=2 KnotsCount=2 Degree=1 IsPeriodic=0
    g107: BSplineCurve PolesCount=2 KnotsCount=2 Degree=1 IsPeriodic=0
    g108: BSplineCurve PolesCount=2 KnotsCount=2 Degree=1 IsPeriodic=0
    g109: BSplineCurve PolesCount=2 KnotsCount=2 Degree=1 IsPeriodic=0
    g110: BSplineCurve PolesCount=2 KnotsCount=2 Degree=1 IsPeriodic=0
    g111: BSplineCurve PolesCount=2 KnotsCount=2 Degree=1 IsPeriodic=0
    g112: BSplineCurve PolesCount=2 KnotsCount=2 Degree=1 IsPeriodic=0
    g113: BSplineCurve PolesCount=2 KnotsCount=2 Degree=1 IsPeriodic=0
    g114: BSplineCurve PolesCount=2 KnotsCount=2 Degree=1 IsPeriodic=0
    g115: BSplineCurve PolesCount=2 KnotsCount=2 Degree=1 IsPeriodic=0
    g116: BSplineCurve PolesCount=2 KnotsCount=2 Degree=1 IsPeriodic=0
    g117: BSplineCurve PolesCount=2 KnotsCount=2 Degree=1 IsPeriodic=0
    g118: BSplineCurve PolesCount=2 KnotsCount=2 Degree=1 IsPeriodic=0
    g119: BSplineCurve PolesCount=2 KnotsCount=2 Degree=1 IsPeriodic=0
    g120: BSplineCurve PolesCount=2 KnotsCount=2 Degree=1 IsPeriodic=0
    g121: BSplineCurve PolesCount=2 KnotsCount=2 Degree=1 IsPeriodic=0
    g122: BSplineCurve PolesCount=2 KnotsCount=2 Degree=1 IsPeriodic=0
    g123: BSplineCurve PolesCount=2 KnotsCount=2 Degree=1 IsPeriodic=0
    g124: BSplineCurve PolesCount=2 KnotsCount=2 Degree=1 IsPeriodic=0
    g125: BSplineCurve PolesCount=2 KnotsCount=2 Degree=1 IsPeriodic=0
    g126: BSplineCurve PolesCount=2 KnotsCount=2 Degree=1 IsPeriodic=0
    g127: BSplineCurve PolesCount=2 KnotsCount=2 Degree=1 IsPeriodic=0
    g128: BSplineCurve PolesCount=2 KnotsCount=2 Degree=1 IsPeriodic=0
    g129: BSplineCurve PolesCount=2 KnotsCount=2 Degree=1 IsPeriodic=0
    g130: BSplineCurve PolesCount=2 KnotsCount=2 Degree=1 IsPeriodic=0
    g131: BSplineCurve PolesCount=2 KnotsCount=2 Degree=1 IsPeriodic=0
    g132: BSplineCurve PolesCount=2 KnotsCount=2 Degree=1 IsPeriodic=0
    g133: BSplineCurve PolesCount=2 KnotsCount=2 Degree=1 IsPeriodic=0
    g134: BSplineCurve PolesCount=2 KnotsCount=2 Degree=1 IsPeriodic=0
    g135: BSplineCurve PolesCount=2 KnotsCount=2 Degree=1 IsPeriodic=0
    g136: BSplineCurve PolesCount=2 KnotsCount=2 Degree=1 IsPeriodic=0
    g137: BSplineCurve PolesCount=2 KnotsCount=2 Degree=1 IsPeriodic=0
    g138: BSplineCurve PolesCount=2 KnotsCount=2 Degree=1 IsPeriodic=0
    g139: BSplineCurve PolesCount=2 KnotsCount=2 Degree=1 IsPeriodic=0
    g140: BSplineCurve PolesCount=2 KnotsCount=2 Degree=1 IsPeriodic=0
    g141: BSplineCurve PolesCount=2 KnotsCount=2 Degree=1 IsPeriodic=0
    g142: BSplineCurve PolesCount=2 KnotsCount=2 Degree=1 IsPeriodic=0
    g143: BSplineCurve PolesCount=2 KnotsCount=2 Degree=1 IsPeriodic=0
    g144: BSplineCurve PolesCount=2 KnotsCount=2 Degree=1 IsPeriodic=0
    g145: BSplineCurve PolesCount=2 KnotsCount=2 Degree=1 IsPeriodic=0
    g146: BSplineCurve PolesCount=2 KnotsCount=2 Degree=1 IsPeriodic=0
    g147: BSplineCurve PolesCount=2 KnotsCount=2 Degree=1 IsPeriodic=0
    g148: BSplineCurve PolesCount=2 KnotsCount=2 Degree=1 IsPeriodic=0
    g149: BSplineCurve PolesCount=2 KnotsCount=2 Degree=1 IsPeriodic=0
    g150: BSplineCurve PolesCount=2 KnotsCount=2 Degree=1 IsPeriodic=0
    g151: BSplineCurve PolesCount=2 KnotsCount=2 Degree=1 IsPeriodic=0
    g152: BSplineCurve PolesCount=2 KnotsCount=2 Degree=1 IsPeriodic=0
    g153: BSplineCurve PolesCount=2 KnotsCount=2 Degree=1 IsPeriodic=0
    g154: BSplineCurve PolesCount=2 KnotsCount=2 Degree=1 IsPeriodic=0
    g155: BSplineCurve PolesCount=2 KnotsCount=2 Degree=1 IsPeriodic=0
    g156: BSplineCurve PolesCount=2 KnotsCount=2 Degree=1 IsPeriodic=0
    g157: BSplineCurve PolesCount=2 KnotsCount=2 Degree=1 IsPeriodic=0
    g158: BSplineCurve PolesCount=2 KnotsCount=2 Degree=1 IsPeriodic=0
    g159: BSplineCurve PolesCount=2 KnotsCount=2 Degree=1 IsPeriodic=0
    g160: BSplineCurve PolesCount=2 KnotsCount=2 Degree=1 IsPeriodic=0
    g161: BSplineCurve PolesCount=2 KnotsCount=2 Degree=1 IsPeriodic=0
    g162: BSplineCurve PolesCount=2 KnotsCount=2 Degree=1 IsPeriodic=0
    g163: BSplineCurve PolesCount=2 KnotsCount=2 Degree=1 IsPeriodic=0
    g164: BSplineCurve PolesCount=2 KnotsCount=2 Degree=1 IsPeriodic=0
    g165: BSplineCurve PolesCount=2 KnotsCount=2 Degree=1 IsPeriodic=0
    g166: BSplineCurve PolesCount=2 KnotsCount=2 Degree=1 IsPeriodic=0
    g167: BSplineCurve PolesCount=2 KnotsCount=2 Degree=1 IsPeriodic=0
    g168: BSplineCurve PolesCount=2 KnotsCount=2 Degree=1 IsPeriodic=0
    g169: BSplineCurve PolesCount=2 KnotsCount=2 Degree=1 IsPeriodic=0
    g170: BSplineCurve PolesCount=2 KnotsCount=2 Degree=1 IsPeriodic=0
    g171: BSplineCurve PolesCount=2 KnotsCount=2 Degree=1 IsPeriodic=0
    g172: BSplineCurve PolesCount=2 KnotsCount=2 Degree=1 IsPeriodic=0
    g173: BSplineCurve PolesCount=2 KnotsCount=2 Degree=1 IsPeriodic=0
    g174: BSplineCurve PolesCount=2 KnotsCount=2 Degree=1 IsPeriodic=0
    g175: BSplineCurve PolesCount=2 KnotsCount=2 Degree=1 IsPeriodic=0
    g176: BSplineCurve PolesCount=2 KnotsCount=2 Degree=1 IsPeriodic=0
    g177: BSplineCurve PolesCount=2 KnotsCount=2 Degree=1 IsPeriodic=0
    g178: BSplineCurve PolesCount=2 KnotsCount=2 Degree=1 IsPeriodic=0
    g179: BSplineCurve PolesCount=2 KnotsCount=2 Degree=1 IsPeriodic=0
    g180: BSplineCurve PolesCount=2 KnotsCount=2 Degree=1 IsPeriodic=0
    g181: BSplineCurve PolesCount=2 KnotsCount=2 Degree=1 IsPeriodic=0
    g182: BSplineCurve PolesCount=2 KnotsCount=2 Degree=1 IsPeriodic=0
    g183: BSplineCurve PolesCount=2 KnotsCount=2 Degree=1 IsPeriodic=0
    g184: BSplineCurve PolesCount=2 KnotsCount=2 Degree=1 IsPeriodic=0
    g185: BSplineCurve PolesCount=2 KnotsCount=2 Degree=1 IsPeriodic=0
    g186: BSplineCurve PolesCount=2 KnotsCount=2 Degree=1 IsPeriodic=0
    g187: BSplineCurve PolesCount=2 KnotsCount=2 Degree=1 IsPeriodic=0
    g188: BSplineCurve PolesCount=2 KnotsCount=2 Degree=1 IsPeriodic=0
    g189: BSplineCurve PolesCount=2 KnotsCount=2 Degree=1 IsPeriodic=0
    g190: BSplineCurve PolesCount=2 KnotsCount=2 Degree=1 IsPeriodic=0
    g191: BSplineCurve PolesCount=2 KnotsCount=2 Degree=1 IsPeriodic=0
    g192: BSplineCurve PolesCount=2 KnotsCount=2 Degree=1 IsPeriodic=0
    g193: BSplineCurve PolesCount=2 KnotsCount=2 Degree=1 IsPeriodic=0
    g194: BSplineCurve PolesCount=2 KnotsCount=2 Degree=1 IsPeriodic=0
    g195: BSplineCurve PolesCount=2 KnotsCount=2 Degree=1 IsPeriodic=0
    g196: BSplineCurve PolesCount=2 KnotsCount=2 Degree=1 IsPeriodic=0
    g197: BSplineCurve PolesCount=2 KnotsCount=2 Degree=1 IsPeriodic=0
    g198: BSplineCurve PolesCount=2 KnotsCount=2 Degree=1 IsPeriodic=0
    g199: BSplineCurve PolesCount=2 KnotsCount=2 Degree=1 IsPeriodic=0
    g200: BSplineCurve PolesCount=2 KnotsCount=2 Degree=1 IsPeriodic=0
    g201: BSplineCurve PolesCount=2 KnotsCount=2 Degree=1 IsPeriodic=0
    g202: BSplineCurve PolesCount=2 KnotsCount=2 Degree=1 IsPeriodic=0
    g203: BSplineCurve PolesCount=2 KnotsCount=2 Degree=1 IsPeriodic=0
    g204: BSplineCurve PolesCount=2 KnotsCount=2 Degree=1 IsPeriodic=0
    g205: BSplineCurve PolesCount=2 KnotsCount=2 Degree=1 IsPeriodic=0
    g206: BSplineCurve PolesCount=2 KnotsCount=2 Degree=1 IsPeriodic=0
    g207: BSplineCurve PolesCount=2 KnotsCount=2 Degree=1 IsPeriodic=0
    g208: BSplineCurve PolesCount=2 KnotsCount=2 Degree=1 IsPeriodic=0
    g209: BSplineCurve PolesCount=2 KnotsCount=2 Degree=1 IsPeriodic=0
    g210: BSplineCurve PolesCount=2 KnotsCount=2 Degree=1 IsPeriodic=0
    g211: BSplineCurve PolesCount=2 KnotsCount=2 Degree=1 IsPeriodic=0
    g212: BSplineCurve PolesCount=2 KnotsCount=2 Degree=1 IsPeriodic=0
    g213: BSplineCurve PolesCount=2 KnotsCount=2 Degree=1 IsPeriodic=0
    g214: BSplineCurve PolesCount=2 KnotsCount=2 Degree=1 IsPeriodic=0
    g215: BSplineCurve PolesCount=2 KnotsCount=2 Degree=1 IsPeriodic=0
    g216: BSplineCurve PolesCount=2 KnotsCount=2 Degree=1 IsPeriodic=0
    g217: BSplineCurve PolesCount=2 KnotsCount=2 Degree=1 IsPeriodic=0
    g218: BSplineCurve PolesCount=2 KnotsCount=2 Degree=1 IsPeriodic=0
    g219: BSplineCurve PolesCount=2 KnotsCount=2 Degree=1 IsPeriodic=0
    g220: BSplineCurve PolesCount=2 KnotsCount=2 Degree=1 IsPeriodic=0
    g221: BSplineCurve PolesCount=2 KnotsCount=2 Degree=1 IsPeriodic=0
    g222: BSplineCurve PolesCount=2 KnotsCount=2 Degree=1 IsPeriodic=0
    g223: BSplineCurve PolesCount=2 KnotsCount=2 Degree=1 IsPeriodic=0
    g224: BSplineCurve PolesCount=2 KnotsCount=2 Degree=1 IsPeriodic=0
    g225: BSplineCurve PolesCount=2 KnotsCount=2 Degree=1 IsPeriodic=0
    g226: BSplineCurve PolesCount=2 KnotsCount=2 Degree=1 IsPeriodic=0
    g227: BSplineCurve PolesCount=2 KnotsCount=2 Degree=1 IsPeriodic=0
    g228: BSplineCurve PolesCount=2 KnotsCount=2 Degree=1 IsPeriodic=0
    g229: BSplineCurve PolesCount=2 KnotsCount=2 Degree=1 IsPeriodic=0
    g230: BSplineCurve PolesCount=2 KnotsCount=2 Degree=1 IsPeriodic=0
    g231: BSplineCurve PolesCount=2 KnotsCount=2 Degree=1 IsPeriodic=0
    g232: BSplineCurve PolesCount=2 KnotsCount=2 Degree=1 IsPeriodic=0
    g233: BSplineCurve PolesCount=2 KnotsCount=2 Degree=1 IsPeriodic=0
    g234: BSplineCurve PolesCount=2 KnotsCount=2 Degree=1 IsPeriodic=0
    g235: BSplineCurve PolesCount=2 KnotsCount=2 Degree=1 IsPeriodic=0
    g236: BSplineCurve PolesCount=2 KnotsCount=2 Degree=1 IsPeriodic=0
    g237: BSplineCurve PolesCount=2 KnotsCount=2 Degree=1 IsPeriodic=0
    g238: BSplineCurve PolesCount=2 KnotsCount=2 Degree=1 IsPeriodic=0
    g239: BSplineCurve PolesCount=2 KnotsCount=2 Degree=1 IsPeriodic=0
    g240: BSplineCurve PolesCount=2 KnotsCount=2 Degree=1 IsPeriodic=0
    g241: BSplineCurve PolesCount=2 KnotsCount=2 Degree=1 IsPeriodic=0
    g242: BSplineCurve PolesCount=2 KnotsCount=2 Degree=1 IsPeriodic=0
    g243: BSplineCurve PolesCount=2 KnotsCount=2 Degree=1 IsPeriodic=0
    g244: BSplineCurve PolesCount=2 KnotsCount=2 Degree=1 IsPeriodic=0
    g245: BSplineCurve PolesCount=2 KnotsCount=2 Degree=1 IsPeriodic=0
    g246: BSplineCurve PolesCount=2 KnotsCount=2 Degree=1 IsPeriodic=0
    g247: BSplineCurve PolesCount=2 KnotsCount=2 Degree=1 IsPeriodic=0
    g248: BSplineCurve PolesCount=2 KnotsCount=2 Degree=1 IsPeriodic=0
    g249: BSplineCurve PolesCount=2 KnotsCount=2 Degree=1 IsPeriodic=0
    g250: BSplineCurve PolesCount=2 KnotsCount=2 Degree=1 IsPeriodic=0
    g251: BSplineCurve PolesCount=2 KnotsCount=2 Degree=1 IsPeriodic=0
    g252: BSplineCurve PolesCount=2 KnotsCount=2 Degree=1 IsPeriodic=0
    g253: BSplineCurve PolesCount=2 KnotsCount=2 Degree=1 IsPeriodic=0
    g254: BSplineCurve PolesCount=2 KnotsCount=2 Degree=1 IsPeriodic=0
    g255: BSplineCurve PolesCount=2 KnotsCount=2 Degree=1 IsPeriodic=0
    g256: BSplineCurve PolesCount=2 KnotsCount=2 Degree=1 IsPeriodic=0
    g257: BSplineCurve PolesCount=2 KnotsCount=2 Degree=1 IsPeriodic=0
    g258: BSplineCurve PolesCount=2 KnotsCount=2 Degree=1 IsPeriodic=0
    g259: BSplineCurve PolesCount=2 KnotsCount=2 Degree=1 IsPeriodic=0
    g260: BSplineCurve PolesCount=2 KnotsCount=2 Degree=1 IsPeriodic=0
    g261: BSplineCurve PolesCount=2 KnotsCount=2 Degree=1 IsPeriodic=0
    g262: BSplineCurve PolesCount=2 KnotsCount=2 Degree=1 IsPeriodic=0
    g263: BSplineCurve PolesCount=2 KnotsCount=2 Degree=1 IsPeriodic=0
    g264: BSplineCurve PolesCount=2 KnotsCount=2 Degree=1 IsPeriodic=0
    g265: BSplineCurve PolesCount=2 KnotsCount=2 Degree=1 IsPeriodic=0
    g266: BSplineCurve PolesCount=2 KnotsCount=2 Degree=1 IsPeriodic=0
    g267: BSplineCurve PolesCount=2 KnotsCount=2 Degree=1 IsPeriodic=0
    g268: BSplineCurve PolesCount=2 KnotsCount=2 Degree=1 IsPeriodic=0
    g269: BSplineCurve PolesCount=2 KnotsCount=2 Degree=1 IsPeriodic=0
    g270: BSplineCurve PolesCount=2 KnotsCount=2 Degree=1 IsPeriodic=0
    g271: BSplineCurve PolesCount=2 KnotsCount=2 Degree=1 IsPeriodic=0
    g272: BSplineCurve PolesCount=2 KnotsCount=2 Degree=1 IsPeriodic=0
    g273: BSplineCurve PolesCount=2 KnotsCount=2 Degree=1 IsPeriodic=0
    g274: BSplineCurve PolesCount=2 KnotsCount=2 Degree=1 IsPeriodic=0
    g275: BSplineCurve PolesCount=2 KnotsCount=2 Degree=1 IsPeriodic=0
    g276: BSplineCurve PolesCount=2 KnotsCount=2 Degree=1 IsPeriodic=0
    g277: BSplineCurve PolesCount=2 KnotsCount=2 Degree=1 IsPeriodic=0
    g278: BSplineCurve PolesCount=2 KnotsCount=2 Degree=1 IsPeriodic=0
    g279: BSplineCurve PolesCount=2 KnotsCount=2 Degree=1 IsPeriodic=0
    g280: BSplineCurve PolesCount=2 KnotsCount=2 Degree=1 IsPeriodic=0
    g281: BSplineCurve PolesCount=2 KnotsCount=2 Degree=1 IsPeriodic=0
    g282: BSplineCurve PolesCount=2 KnotsCount=2 Degree=1 IsPeriodic=0
    g283: BSplineCurve PolesCount=2 KnotsCount=2 Degree=1 IsPeriodic=0
    g284: BSplineCurve PolesCount=2 KnotsCount=2 Degree=1 IsPeriodic=0
    g285: BSplineCurve PolesCount=2 KnotsCount=2 Degree=1 IsPeriodic=0
    g286: BSplineCurve PolesCount=2 KnotsCount=2 Degree=1 IsPeriodic=0
    g287: BSplineCurve PolesCount=2 KnotsCount=2 Degree=1 IsPeriodic=0
    g288: BSplineCurve PolesCount=2 KnotsCount=2 Degree=1 IsPeriodic=0
    g289: BSplineCurve PolesCount=2 KnotsCount=2 Degree=1 IsPeriodic=0
    g290: BSplineCurve PolesCount=2 KnotsCount=2 Degree=1 IsPeriodic=0
    g291: BSplineCurve PolesCount=2 KnotsCount=2 Degree=1 IsPeriodic=0
    g292: BSplineCurve PolesCount=2 KnotsCount=2 Degree=1 IsPeriodic=0
    g293: BSplineCurve PolesCount=2 KnotsCount=2 Degree=1 IsPeriodic=0
    g294: BSplineCurve PolesCount=2 KnotsCount=2 Degree=1 IsPeriodic=0
    g295: BSplineCurve PolesCount=2 KnotsCount=2 Degree=1 IsPeriodic=0
    g296: BSplineCurve PolesCount=2 KnotsCount=2 Degree=1 IsPeriodic=0
    g297: BSplineCurve PolesCount=2 KnotsCount=2 Degree=1 IsPeriodic=0
    g298: BSplineCurve PolesCount=2 KnotsCount=2 Degree=1 IsPeriodic=0
    g299: BSplineCurve PolesCount=2 KnotsCount=2 Degree=1 IsPeriodic=0
    g300: BSplineCurve PolesCount=2 KnotsCount=2 Degree=1 IsPeriodic=0
    g301: BSplineCurve PolesCount=2 KnotsCount=2 Degree=1 IsPeriodic=0
    g302: BSplineCurve PolesCount=2 KnotsCount=2 Degree=1 IsPeriodic=0
    g303: BSplineCurve PolesCount=2 KnotsCount=2 Degree=1 IsPeriodic=0
    g304: BSplineCurve PolesCount=2 KnotsCount=2 Degree=1 IsPeriodic=0
    g305: BSplineCurve PolesCount=2 KnotsCount=2 Degree=1 IsPeriodic=0
    g306: BSplineCurve PolesCount=2 KnotsCount=2 Degree=1 IsPeriodic=0
    g307: BSplineCurve PolesCount=2 KnotsCount=2 Degree=1 IsPeriodic=0
    g308: BSplineCurve PolesCount=2 KnotsCount=2 Degree=1 IsPeriodic=0
    g309: BSplineCurve PolesCount=2 KnotsCount=2 Degree=1 IsPeriodic=0
    g310: BSplineCurve PolesCount=2 KnotsCount=2 Degree=1 IsPeriodic=0
    g311: BSplineCurve PolesCount=2 KnotsCount=2 Degree=1 IsPeriodic=0
    g312: BSplineCurve PolesCount=2 KnotsCount=2 Degree=1 IsPeriodic=0
    g313: BSplineCurve PolesCount=2 KnotsCount=2 Degree=1 IsPeriodic=0
    g314: BSplineCurve PolesCount=2 KnotsCount=2 Degree=1 IsPeriodic=0
    g315: BSplineCurve PolesCount=2 KnotsCount=2 Degree=1 IsPeriodic=0
    g316: BSplineCurve PolesCount=2 KnotsCount=2 Degree=1 IsPeriodic=0
    g317: BSplineCurve PolesCount=2 KnotsCount=2 Degree=1 IsPeriodic=0
    g318: BSplineCurve PolesCount=2 KnotsCount=2 Degree=1 IsPeriodic=0
    g319: BSplineCurve PolesCount=2 KnotsCount=2 Degree=1 IsPeriodic=0
    g320: BSplineCurve PolesCount=2 KnotsCount=2 Degree=1 IsPeriodic=0
    g321: BSplineCurve PolesCount=2 KnotsCount=2 Degree=1 IsPeriodic=0
    g322: BSplineCurve PolesCount=2 KnotsCount=2 Degree=1 IsPeriodic=0
    g323: BSplineCurve PolesCount=2 KnotsCount=2 Degree=1 IsPeriodic=0
    g324: BSplineCurve PolesCount=2 KnotsCount=2 Degree=1 IsPeriodic=0
    g325: BSplineCurve PolesCount=2 KnotsCount=2 Degree=1 IsPeriodic=0
    g326: BSplineCurve PolesCount=2 KnotsCount=2 Degree=1 IsPeriodic=0
    g327: BSplineCurve PolesCount=2 KnotsCount=2 Degree=1 IsPeriodic=0
    g328: BSplineCurve PolesCount=2 KnotsCount=2 Degree=1 IsPeriodic=0
    g329: BSplineCurve PolesCount=2 KnotsCount=2 Degree=1 IsPeriodic=0
    g330: BSplineCurve PolesCount=2 KnotsCount=2 Degree=1 IsPeriodic=0
    g331: BSplineCurve PolesCount=2 KnotsCount=2 Degree=1 IsPeriodic=0
    g332: BSplineCurve PolesCount=2 KnotsCount=2 Degree=1 IsPeriodic=0
    g333: BSplineCurve PolesCount=2 KnotsCount=2 Degree=1 IsPeriodic=0
    g334: BSplineCurve PolesCount=2 KnotsCount=2 Degree=1 IsPeriodic=0
    g335: BSplineCurve PolesCount=2 KnotsCount=2 Degree=1 IsPeriodic=0
    g336: BSplineCurve PolesCount=2 KnotsCount=2 Degree=1 IsPeriodic=0
    g337: BSplineCurve PolesCount=2 KnotsCount=2 Degree=1 IsPeriodic=0
    g338: BSplineCurve PolesCount=2 KnotsCount=2 Degree=1 IsPeriodic=0
    g339: BSplineCurve PolesCount=2 KnotsCount=2 Degree=1 IsPeriodic=0
    g340: BSplineCurve PolesCount=2 KnotsCount=2 Degree=1 IsPeriodic=0
    g341: BSplineCurve PolesCount=2 KnotsCount=2 Degree=1 IsPeriodic=0
    g342: BSplineCurve PolesCount=2 KnotsCount=2 Degree=1 IsPeriodic=0
    g343: BSplineCurve PolesCount=2 KnotsCount=2 Degree=1 IsPeriodic=0
    g344: BSplineCurve PolesCount=2 KnotsCount=2 Degree=1 IsPeriodic=0
    g345: BSplineCurve PolesCount=2 KnotsCount=2 Degree=1 IsPeriodic=0
    g346: BSplineCurve PolesCount=2 KnotsCount=2 Degree=1 IsPeriodic=0
    g347: BSplineCurve PolesCount=2 KnotsCount=2 Degree=1 IsPeriodic=0
    g348: BSplineCurve PolesCount=2 KnotsCount=2 Degree=1 IsPeriodic=0
    g349: BSplineCurve PolesCount=2 KnotsCount=2 Degree=1 IsPeriodic=0
    g350: BSplineCurve PolesCount=2 KnotsCount=2 Degree=1 IsPeriodic=0
    g351: BSplineCurve PolesCount=2 KnotsCount=2 Degree=1 IsPeriodic=0
    g352: BSplineCurve PolesCount=2 KnotsCount=2 Degree=1 IsPeriodic=0
    g353: BSplineCurve PolesCount=2 KnotsCount=2 Degree=1 IsPeriodic=0
    g354: BSplineCurve PolesCount=2 KnotsCount=2 Degree=1 IsPeriodic=0
    g355: BSplineCurve PolesCount=2 KnotsCount=2 Degree=1 IsPeriodic=0
    g356: BSplineCurve PolesCount=2 KnotsCount=2 Degree=1 IsPeriodic=0
    g357: BSplineCurve PolesCount=2 KnotsCount=2 Degree=1 IsPeriodic=0
    g358: BSplineCurve PolesCount=2 KnotsCount=2 Degree=1 IsPeriodic=0
    g359: BSplineCurve PolesCount=2 KnotsCount=2 Degree=1 IsPeriodic=0
    g360: BSplineCurve PolesCount=2 KnotsCount=2 Degree=1 IsPeriodic=0
    g361: BSplineCurve PolesCount=2 KnotsCount=2 Degree=1 IsPeriodic=0
    g362: BSplineCurve PolesCount=2 KnotsCount=2 Degree=1 IsPeriodic=0
    g363: BSplineCurve PolesCount=2 KnotsCount=2 Degree=1 IsPeriodic=0
    g364: BSplineCurve PolesCount=2 KnotsCount=2 Degree=1 IsPeriodic=0
    g365: BSplineCurve PolesCount=2 KnotsCount=2 Degree=1 IsPeriodic=0
    g366: BSplineCurve PolesCount=2 KnotsCount=2 Degree=1 IsPeriodic=0
    g367: BSplineCurve PolesCount=2 KnotsCount=2 Degree=1 IsPeriodic=0
    g368: BSplineCurve PolesCount=2 KnotsCount=2 Degree=1 IsPeriodic=0
    g369: BSplineCurve PolesCount=2 KnotsCount=2 Degree=1 IsPeriodic=0
    g370: BSplineCurve PolesCount=2 KnotsCount=2 Degree=1 IsPeriodic=0
    g371: BSplineCurve PolesCount=2 KnotsCount=2 Degree=1 IsPeriodic=0
    g372: BSplineCurve PolesCount=2 KnotsCount=2 Degree=1 IsPeriodic=0
    g373: BSplineCurve PolesCount=2 KnotsCount=2 Degree=1 IsPeriodic=0
    g374: BSplineCurve PolesCount=2 KnotsCount=2 Degree=1 IsPeriodic=0
    g375: BSplineCurve PolesCount=2 KnotsCount=2 Degree=1 IsPeriodic=0
    g376: BSplineCurve PolesCount=2 KnotsCount=2 Degree=1 IsPeriodic=0
    g377: BSplineCurve PolesCount=2 KnotsCount=2 Degree=1 IsPeriodic=0
    g378: BSplineCurve PolesCount=2 KnotsCount=2 Degree=1 IsPeriodic=0
    g379: BSplineCurve PolesCount=2 KnotsCount=2 Degree=1 IsPeriodic=0
    g380: BSplineCurve PolesCount=2 KnotsCount=2 Degree=1 IsPeriodic=0
    g381: BSplineCurve PolesCount=2 KnotsCount=2 Degree=1 IsPeriodic=0
    g382: BSplineCurve PolesCount=2 KnotsCount=2 Degree=1 IsPeriodic=0
    g383: BSplineCurve PolesCount=2 KnotsCount=2 Degree=1 IsPeriodic=0
    g384: BSplineCurve PolesCount=2 KnotsCount=2 Degree=1 IsPeriodic=0
    g385: BSplineCurve PolesCount=2 KnotsCount=2 Degree=1 IsPeriodic=0
    g386: BSplineCurve PolesCount=2 KnotsCount=2 Degree=1 IsPeriodic=0
    g387: BSplineCurve PolesCount=2 KnotsCount=2 Degree=1 IsPeriodic=0
    g388: BSplineCurve PolesCount=2 KnotsCount=2 Degree=1 IsPeriodic=0
    g389: BSplineCurve PolesCount=2 KnotsCount=2 Degree=1 IsPeriodic=0
    g390: BSplineCurve PolesCount=2 KnotsCount=2 Degree=1 IsPeriodic=0
    g391: BSplineCurve PolesCount=2 KnotsCount=2 Degree=1 IsPeriodic=0
    g392: BSplineCurve PolesCount=2 KnotsCount=2 Degree=1 IsPeriodic=0
    g393: BSplineCurve PolesCount=2 KnotsCount=2 Degree=1 IsPeriodic=0
    g394: BSplineCurve PolesCount=2 KnotsCount=2 Degree=1 IsPeriodic=0
    g395: BSplineCurve PolesCount=2 KnotsCount=2 Degree=1 IsPeriodic=0
    g396: BSplineCurve PolesCount=2 KnotsCount=2 Degree=1 IsPeriodic=0
    g397: BSplineCurve PolesCount=2 KnotsCount=2 Degree=1 IsPeriodic=0
    g398: BSplineCurve PolesCount=2 KnotsCount=2 Degree=1 IsPeriodic=0
    g399: BSplineCurve PolesCount=2 KnotsCount=2 Degree=1 IsPeriodic=0
    ... +460 more geometry lines
  constraints (860):
    c: Coincident(g0,g1)
    c: Coincident(g1,g2)
    c: Coincident(g2,g3)
    c: Coincident(g3,g4)
    c: Coincident(g4,g5)
    c: Coincident(g5,g6)
    c: Coincident(g6,g7)
    c: Coincident(g7,g8)
    c: Coincident(g8,g9)
    c: Coincident(g9,g10)
    c: Coincident(g10,g11)
    c: Coincident(g11,g12)
    c: Coincident(g12,g13)
    c: Coincident(g13,g14)
    c: Coincident(g14,g15)
    c: Coincident(g15,g16)
    c: Coincident(g16,g17)
    c: Coincident(g17,g18)
    c: Coincident(g18,g19)
    c: Coincident(g19,g20)
    c: Coincident(g20,g21)
    c: Coincident(g21,g22)
    c: Coincident(g22,g23)
    c: Coincident(g23,g24)
    c: Coincident(g24,g25)
    c: Coincident(g25,g26)
    c: Coincident(g26,g27)
    c: Coincident(g27,g28)
    c: Coincident(g28,g29)
    c: Coincident(g29,g30)
    c: Coincident(g30,g31)
    c: Coincident(g31,g32)
    c: Coincident(g32,g33)
    c: Coincident(g33,g34)
    c: Coincident(g34,g35)
    c: Coincident(g35,g36)
    c: Coincident(g36,g37)
    c: Coincident(g37,g38)
    c: Coincident(g38,g39)
    c: Coincident(g39,g40)
    c: Coincident(g40,g41)
    c: Coincident(g41,g42)
    c: Coincident(g42,g43)
    c: Coincident(g43,g44)
    c: Coincident(g44,g45)
    c: Coincident(g45,g46)
    c: Coincident(g46,g47)
    c: Coincident(g47,g48)
    c: Coincident(g48,g49)
    c: Coincident(g49,g50)
    c: Coincident(g50,g51)
    c: Coincident(g51,g52)
    c: Coincident(g52,g53)
    c: Coincident(g53,g54)
    c: Coincident(g54,g55)
    c: Coincident(g55,g56)
    c: Coincident(g56,g57)
    c: Coincident(g57,g58)
    c: Coincident(g58,g59)
    c: Coincident(g59,g60)
    c: Coincident(g60,g61)
    c: Coincident(g61,g62)
    c: Coincident(g62,g63)
    c: Coincident(g63,g64)
    c: Coincident(g64,g65)
    c: Coincident(g65,g66)
    c: Coincident(g66,g67)
    c: Coincident(g67,g68)
    c: Coincident(g68,g69)
    c: Coincident(g69,g70)
    c: Coincident(g70,g71)
    c: Coincident(g71,g72)
    c: Coincident(g72,g73)
    c: Coincident(g73,g74)
    c: Coincident(g74,g75)
    c: Coincident(g75,g76)
    c: Coincident(g76,g77)
    c: Coincident(g77,g78)
    c: Coincident(g78,g79)
    c: Coincident(g79,g80)
    c: Coincident(g80,g81)
    c: Coincident(g81,g82)
    c: Coincident(g82,g83)
    c: Coincident(g83,g84)
    c: Coincident(g84,g85)
    c: Coincident(g85,g86)
    c: Coincident(g86,g87)
    c: Coincident(g87,g0)
    c: Coincident(g88,g89)
    c: Coincident(g89,g90)
    c: Coincident(g90,g91)
    c: Coincident(g91,g92)
    c: Coincident(g92,g93)
    c: Coincident(g93,g94)
    c: Coincident(g94,g95)
    c: Coincident(g95,g96)
    c: Coincident(g96,g97)
    c: Coincident(g97,g98)
    c: Coincident(g98,g99)
    c: Coincident(g99,g100)
    c: Coincident(g100,g101)
    c: Coincident(g101,g102)
    c: Coincident(g102,g103)
    c: Coincident(g103,g104)
    c: Coincident(g104,g105)
    c: Coincident(g105,g106)
    c: Coincident(g106,g107)
    c: Coincident(g107,g108)
    c: Coincident(g108,g109)
    c: Coincident(g109,g110)
    c: Coincident(g110,g111)
    c: Coincident(g111,g112)
    c: Coincident(g112,g113)
    c: Coincident(g113,g114)
    c: Coincident(g114,g115)
    c: Coincident(g115,g116)
    c: Coincident(g116,g117)
    c: Coincident(g117,g118)
    c: Coincident(g118,g119)
    c: Coincident(g119,g120)
    c: Coincident(g120,g121)
    c: Coincident(g121,g122)
    c: Coincident(g122,g123)
    c: Coincident(g123,g124)
    c: Coincident(g124,g125)
    c: Coincident(g125,g126)
    c: Coincident(g126,g127)
    c: Coincident(g127,g88)
    c: Coincident(g128,g129)
    c: Coincident(g129,g130)
    c: Coincident(g130,g131)
    c: Coincident(g131,g132)
    c: Coincident(g132,g133)
    c: Coincident(g133,g134)
    c: Coincident(g134,g135)
    c: Coincident(g135,g136)
    c: Coincident(g136,g137)
    c: Coincident(g137,g138)
    c: Coincident(g138,g139)
    c: Coincident(g139,g140)
    c: Coincident(g140,g141)
    c: Coincident(g141,g142)
    c: Coincident(g142,g143)
    c: Coincident(g143,g144)
    c: Coincident(g144,g145)
    c: Coincident(g145,g146)
    c: Coincident(g146,g147)
    c: Coincident(g147,g148)
    c: Coincident(g148,g149)
    c: Coincident(g149,g150)
    c: Coincident(g150,g151)
    c: Coincident(g151,g152)
    c: Coincident(g152,g153)
    c: Coincident(g153,g154)
    c: Coincident(g154,g155)
    c: Coincident(g155,g156)
    c: Coincident(g156,g157)
    c: Coincident(g157,g158)
    c: Coincident(g158,g159)
    c: Coincident(g159,g160)
    c: Coincident(g160,g161)
    c: Coincident(g161,g162)
    c: Coincident(g162,g163)
    c: Coincident(g163,g164)
    c: Coincident(g164,g165)
    c: Coincident(g165,g166)
    c: Coincident(g166,g167)
    c: Coincident(g167,g168)
    c: Coincident(g168,g169)
    c: Coincident(g169,g170)
    c: Coincident(g170,g171)
    c: Coincident(g171,g172)
    c: Coincident(g172,g173)
    c: Coincident(g173,g174)
    c: Coincident(g174,g175)
    c: Coincident(g175,g176)
    c: Coincident(g176,g177)
    c: Coincident(g177,g178)
    c: Coincident(g178,g179)
    c: Coincident(g179,g180)
    c: Coincident(g180,g181)
    c: Coincident(g181,g182)
    c: Coincident(g182,g183)
    c: Coincident(g183,g184)
    c: Coincident(g184,g185)
    c: Coincident(g185,g186)
    c: Coincident(g186,g187)
    c: Coincident(g187,g188)
    c: Coincident(g188,g189)
    c: Coincident(g189,g190)
    c: Coincident(g190,g191)
    c: Coincident(g191,g192)
    c: Coincident(g192,g193)
    c: Coincident(g193,g194)
    c: Coincident(g194,g195)
    c: Coincident(g195,g196)
    c: Coincident(g196,g197)
    c: Coincident(g197,g198)
    c: Coincident(g198,g199)
    c: Coincident(g199,g200)
    c: Coincident(g200,g201)
    c: Coincident(g201,g202)
    c: Coincident(g202,g203)
    c: Coincident(g203,g204)
    c: Coincident(g204,g205)
    c: Coincident(g205,g206)
    c: Coincident(g206,g207)
    c: Coincident(g207,g208)
    c: Coincident(g208,g209)
    c: Coincident(g209,g210)
    c: Coincident(g210,g211)
    c: Coincident(g211,g212)
    c: Coincident(g212,g213)
    c: Coincident(g213,g214)
    c: Coincident(g214,g215)
    c: Coincident(g215,g216)
    c: Coincident(g216,g217)
    c: Coincident(g217,g218)
    c: Coincident(g218,g219)
    c: Coincident(g219,g220)
    c: Coincident(g220,g221)
    c: Coincident(g221,g222)
    c: Coincident(g222,g223)
    c: Coincident(g223,g224)
    c: Coincident(g224,g225)
    c: Coincident(g225,g226)
    c: Coincident(g226,g227)
    c: Coincident(g227,g228)
    c: Coincident(g228,g229)
    c: Coincident(g229,g230)
    c: Coincident(g230,g231)
    c: Coincident(g231,g232)
    c: Coincident(g232,g233)
    c: Coincident(g233,g234)
    c: Coincident(g234,g235)
    c: Coincident(g235,g236)
    c: Coincident(g236,g237)
    c: Coincident(g237,g238)
    c: Coincident(g238,g239)
    c: Coincident(g239,g128)
    c: Coincident(g240,g241)
    c: Coincident(g241,g242)
    c: Coincident(g242,g243)
    c: Coincident(g243,g244)
    c: Coincident(g244,g245)
    c: Coincident(g245,g246)
    c: Coincident(g246,g247)
    c: Coincident(g247,g248)
    c: Coincident(g248,g249)
    c: Coincident(g249,g250)
    c: Coincident(g250,g251)
    c: Coincident(g251,g252)
    c: Coincident(g252,g253)
    c: Coincident(g253,g254)
    c: Coincident(g254,g255)
    c: Coincident(g255,g256)
    c: Coincident(g256,g257)
    c: Coincident(g257,g258)
    c: Coincident(g258,g259)
    c: Coincident(g259,g260)
    c: Coincident(g260,g261)
    c: Coincident(g261,g262)
    c: Coincident(g262,g263)
    c: Coincident(g263,g264)
    c: Coincident(g264,g265)
    c: Coincident(g265,g266)
    c: Coincident(g266,g267)
    c: Coincident(g267,g268)
    c: Coincident(g268,g269)
    c: Coincident(g269,g270)
    c: Coincident(g270,g271)
    c: Coincident(g271,g272)
    c: Coincident(g272,g273)
    c: Coincident(g273,g274)
    c: Coincident(g274,g275)
    c: Coincident(g275,g276)
    c: Coincident(g276,g277)
    c: Coincident(g277,g278)
    c: Coincident(g278,g279)
    c: Coincident(g279,g280)
    c: Coincident(g280,g281)
    c: Coincident(g281,g282)
    c: Coincident(g282,g283)
    c: Coincident(g283,g284)
    c: Coincident(g284,g285)
    c: Coincident(g285,g286)
    c: Coincident(g286,g287)
    c: Coincident(g287,g240)
    c: Coincident(g288,g289)
    c: Coincident(g289,g290)
    c: Coincident(g290,g291)
    c: Coincident(g291,g292)
    c: Coincident(g292,g293)
    c: Coincident(g293,g294)
    c: Coincident(g294,g295)
    c: Coincident(g295,g296)
    c: Coincident(g296,g297)
    c: Coincident(g297,g298)
    c: Coincident(g298,g299)
    c: Coincident(g299,g300)
    c: Coincident(g300,g301)
    c: Coincident(g301,g302)
    c: Coincident(g302,g303)
    c: Coincident(g303,g304)
    c: Coincident(g304,g305)
    c: Coincident(g305,g306)
    c: Coincident(g306,g307)
    c: Coincident(g307,g308)
    c: Coincident(g308,g309)
    c: Coincident(g309,g310)
    c: Coincident(g310,g311)
    c: Coincident(g311,g288)
    c: Coincident(g312,g313)
    c: Coincident(g313,g314)
    c: Coincident(g314,g315)
    c: Coincident(g315,g316)
    c: Coincident(g316,g317)
    c: Coincident(g317,g318)
    c: Coincident(g318,g319)
    c: Coincident(g319,g320)
    c: Coincident(g320,g321)
    c: Coincident(g321,g322)
    c: Coincident(g322,g323)
    c: Coincident(g323,g324)
    c: Coincident(g324,g325)
    c: Coincident(g325,g326)
    c: Coincident(g326,g327)
    c: Coincident(g327,g312)
    c: Coincident(g328,g329)
    c: Coincident(g329,g330)
    c: Coincident(g330,g331)
    c: Coincident(g331,g332)
    c: Coincident(g332,g333)
    c: Coincident(g333,g334)
    c: Coincident(g334,g335)
    c: Coincident(g335,g336)
    c: Coincident(g336,g337)
    c: Coincident(g337,g338)
    c: Coincident(g338,g339)
    c: Coincident(g339,g340)
    c: Coincident(g340,g341)
    c: Coincident(g341,g342)
    c: Coincident(g342,g343)
    c: Coincident(g343,g344)
    c: Coincident(g344,g345)
    c: Coincident(g345,g346)
    c: Coincident(g346,g347)
    c: Coincident(g347,g348)
    c: Coincident(g348,g349)
    c: Coincident(g349,g350)
    c: Coincident(g350,g351)
    c: Coincident(g351,g352)
    c: Coincident(g352,g353)
    c: Coincident(g353,g354)
    c: Coincident(g354,g355)
    c: Coincident(g355,g356)
    c: Coincident(g356,g357)
    c: Coincident(g357,g358)
    c: Coincident(g358,g359)
    c: Coincident(g359,g360)
    c: Coincident(g360,g361)
    c: Coincident(g361,g362)
    c: Coincident(g362,g363)
    c: Coincident(g363,g364)
    c: Coincident(g364,g365)
    c: Coincident(g365,g366)
    c: Coincident(g366,g367)
    c: Coincident(g367,g368)
    c: Coincident(g368,g369)
    c: Coincident(g369,g370)
    c: Coincident(g370,g371)
    c: Coincident(g371,g372)
    c: Coincident(g372,g373)
    c: Coincident(g373,g374)
    c: Coincident(g374,g375)
    c: Coincident(g375,g376)
    c: Coincident(g376,g377)
    c: Coincident(g377,g378)
    c: Coincident(g378,g379)
    c: Coincident(g379,g380)
    c: Coincident(g380,g381)
    c: Coincident(g381,g382)
    c: Coincident(g382,g383)
    c: Coincident(g383,g384)
    c: Coincident(g384,g385)
    c: Coincident(g385,g386)
    c: Coincident(g386,g387)
    c: Coincident(g387,g388)
    c: Coincident(g388,g389)
    c: Coincident(g389,g390)
    c: Coincident(g390,g391)
    c: Coincident(g391,g392)
    c: Coincident(g392,g393)
    c: Coincident(g393,g394)
    c: Coincident(g394,g395)
    c: Coincident(g395,g396)
    c: Coincident(g396,g397)
    c: Coincident(g397,g398)
    c: Coincident(g398,g399)
    c: Coincident(g399,g328)
    c: Coincident(g400,g401)
    c: Coincident(g401,g402)
    c: Coincident(g402,g403)
    c: Coincident(g403,g404)
    c: Coincident(g404,g405)
    c: Coincident(g405,g406)
    c: Coincident(g406,g407)
    c: Coincident(g407,g408)
    c: Coincident(g408,g409)
    c: Coincident(g409,g410)
    c: Coincident(g410,g411)
    c: Coincident(g411,g412)
    c: Coincident(g412,g413)
    c: Coincident(g413,g414)
    c: Coincident(g414,g415)
    c: Coincident(g415,g416)
    c: Coincident(g416,g417)
    c: Coincident(g417,g418)
    c: Coincident(g418,g419)
    c: Coincident(g419,g420)
    c: Coincident(g420,g421)
    c: Coincident(g421,g422)
    c: Coincident(g422,g423)
    c: Coincident(g423,g400)
    c: Coincident(g424,g425)
    c: Coincident(g425,g426)
    c: Coincident(g426,g427)
    c: Coincident(g427,g428)
    c: Coincident(g428,g429)
    c: Coincident(g429,g430)
    c: Coincident(g430,g431)
    c: Coincident(g431,g432)
    c: Coincident(g432,g433)
    c: Coincident(g433,g434)
    c: Coincident(g434,g435)
    c: Coincident(g435,g436)
    c: Coincident(g436,g437)
    c: Coincident(g437,g438)
    c: Coincident(g438,g439)
    c: Coincident(g439,g440)
    c: Coincident(g440,g441)
    c: Coincident(g441,g442)
    c: Coincident(g442,g443)
    c: Coincident(g443,g444)
    c: Coincident(g444,g445)
    c: Coincident(g445,g446)
    c: Coincident(g446,g447)
    c: Coincident(g447,g448)
    c: Coincident(g448,g449)
    c: Coincident(g449,g450)
    c: Coincident(g450,g451)
    c: Coincident(g451,g452)
    c: Coincident(g452,g453)
    c: Coincident(g453,g454)
    c: Coincident(g454,g455)
    c: Coincident(g455,g456)
    c: Coincident(g456,g457)
    c: Coincident(g457,g458)
    c: Coincident(g458,g459)
    c: Coincident(g459,g460)
    c: Coincident(g460,g461)
    c: Coincident(g461,g462)
    c: Coincident(g462,g463)
    c: Coincident(g463,g464)
    c: Coincident(g464,g465)
    c: Coincident(g465,g466)
    c: Coincident(g466,g467)
    c: Coincident(g467,g468)
    c: Coincident(g468,g469)
    c: Coincident(g469,g470)
    c: Coincident(g470,g471)
    c: Coincident(g471,g472)
    c: Coincident(g472,g473)
    c: Coincident(g473,g474)
    c: Coincident(g474,g475)
    c: Coincident(g475,g476)
    c: Coincident(g476,g477)
    c: Coincident(g477,g478)
    c: Coincident(g478,g479)
    c: Coincident(g479,g424)
    c: Coincident(g480,g481)
    c: Coincident(g481,g482)
    c: Coincident(g482,g483)
    c: Coincident(g483,g484)
    c: Coincident(g484,g485)
    c: Coincident(g485,g486)
    c: Coincident(g486,g487)
    c: Coincident(g487,g488)
    c: Coincident(g488,g489)
    c: Coincident(g489,g490)
    c: Coincident(g490,g491)
    c: Coincident(g491,g492)
    c: Coincident(g492,g493)
    c: Coincident(g493,g494)
    c: Coincident(g494,g495)
    c: Coincident(g495,g480)
    c: Coincident(g496,g497)
    c: Coincident(g497,g498)
    c: Coincident(g498,g499)
    c: Coincident(g499,g500)
    c: Coincident(g500,g501)
    c: Coincident(g501,g502)
    c: Coincident(g502,g503)
    c: Coincident(g503,g504)
    c: Coincident(g504,g505)
    c: Coincident(g505,g506)
    c: Coincident(g506,g507)
    c: Coincident(g507,g508)
    c: Coincident(g508,g509)
    c: Coincident(g509,g510)
    c: Coincident(g510,g511)
    c: Coincident(g511,g512)
    c: Coincident(g512,g513)
    c: Coincident(g513,g514)
    c: Coincident(g514,g515)
    c: Coincident(g515,g516)
    c: Coincident(g516,g517)
    c: Coincident(g517,g518)
    c: Coincident(g518,g519)
    c: Coincident(g519,g520)
    c: Coincident(g520,g521)
    c: Coincident(g521,g522)
    c: Coincident(g522,g523)
    c: Coincident(g523,g524)
    c: Coincident(g524,g525)
    c: Coincident(g525,g526)
    c: Coincident(g526,g527)
    c: Coincident(g527,g528)
    c: Coincident(g528,g529)
    c: Coincident(g529,g530)
    c: Coincident(g530,g531)
    c: Coincident(g531,g532)
    c: Coincident(g532,g533)
    c: Coincident(g533,g534)
    c: Coincident(g534,g535)
    c: Coincident(g535,g496)
    c: Coincident(g536,g537)
    c: Coincident(g537,g538)
    c: Coincident(g538,g539)
    c: Coincident(g539,g540)
    c: Coincident(g540,g541)
    c: Coincident(g541,g542)
    c: Coincident(g542,g543)
    c: Coincident(g543,g544)
    c: Coincident(g544,g545)
    c: Coincident(g545,g546)
    c: Coincident(g546,g547)
    c: Coincident(g547,g548)
    c: Coincident(g548,g549)
    c: Coincident(g549,g550)
    c: Coincident(g550,g551)
    c: Coincident(g551,g552)
    c: Coincident(g552,g553)
    c: Coincident(g553,g554)
    c: Coincident(g554,g555)
    c: Coincident(g555,g556)
    c: Coincident(g556,g557)
    c: Coincident(g557,g558)
    c: Coincident(g558,g559)
    c: Coincident(g559,g560)
    c: Coincident(g560,g561)
    c: Coincident(g561,g562)
    c: Coincident(g562,g563)
    c: Coincident(g563,g564)
    c: Coincident(g564,g565)
    c: Coincident(g565,g566)
    c: Coincident(g566,g567)
    c: Coincident(g567,g568)
    c: Coincident(g568,g569)
    c: Coincident(g569,g570)
    c: Coincident(g570,g571)
    c: Coincident(g571,g572)
    c: Coincident(g572,g573)
    c: Coincident(g573,g574)
    c: Coincident(g574,g575)
    c: Coincident(g575,g536)
    c: Coincident(g576,g577)
    c: Coincident(g577,g578)
    c: Coincident(g578,g579)
    c: Coincident(g579,g580)
    c: Coincident(g580,g581)
    c: Coincident(g581,g582)
    c: Coincident(g582,g583)
    c: Coincident(g583,g584)
    c: Coincident(g584,g585)
    c: Coincident(g585,g586)
    c: Coincident(g586,g587)
    c: Coincident(g587,g576)
    c: Coincident(g588,g589)
    c: Coincident(g589,g590)
    c: Coincident(g590,g591)
    c: Coincident(g591,g592)
    c: Coincident(g592,g593)
    c: Coincident(g593,g594)
    c: Coincident(g594,g595)
    c: Coincident(g595,g596)
    c: Coincident(g596,g597)
    c: Coincident(g597,g598)
    c: Coincident(g598,g599)
    c: Coincident(g599,g600)
    c: Coincident(g600,g601)
    c: Coincident(g601,g602)
    c: Coincident(g602,g603)
    c: Coincident(g603,g604)
    c: Coincident(g604,g605)
    c: Coincident(g605,g606)
    c: Coincident(g606,g607)
    c: Coincident(g607,g608)
    c: Coincident(g608,g609)
    c: Coincident(g609,g610)
    c: Coincident(g610,g611)
    c: Coincident(g611,g612)
    c: Coincident(g612,g613)
    c: Coincident(g613,g614)
    c: Coincident(g614,g615)
    c: Coincident(g615,g616)
    c: Coincident(g616,g617)
    c: Coincident(g617,g618)
    c: Coincident(g618,g619)
    c: Coincident(g619,g620)
    c: Coincident(g620,g621)
    c: Coincident(g621,g622)
    c: Coincident(g622,g623)
    c: Coincident(g623,g624)
    c: Coincident(g624,g625)
    c: Coincident(g625,g626)
    c: Coincident(g626,g627)
    c: Coincident(g627,g628)
    c: Coincident(g628,g629)
    c: Coincident(g629,g630)
    c: Coincident(g630,g631)
    c: Coincident(g631,g632)
    c: Coincident(g632,g633)
    c: Coincident(g633,g634)
    c: Coincident(g634,g635)
    c: Coincident(g635,g636)
    c: Coincident(g636,g637)
    c: Coincident(g637,g638)
    c: Coincident(g638,g639)
    c: Coincident(g639,g640)
    c: Coincident(g640,g641)
    c: Coincident(g641,g642)
    c: Coincident(g642,g643)
    c: Coincident(g643,g644)
    c: Coincident(g644,g645)
    c: Coincident(g645,g646)
    c: Coincident(g646,g647)
    c: Coincident(g647,g648)
    c: Coincident(g648,g649)
    c: Coincident(g649,g650)
    c: Coincident(g650,g651)
    c: Coincident(g651,g652)
    c: Coincident(g652,g653)
    c: Coincident(g653,g654)
    c: Coincident(g654,g655)
    c: Coincident(g655,g656)
    c: Coincident(g656,g657)
    c: Coincident(g657,g658)
    c: Coincident(g658,g659)
    c: Coincident(g659,g660)
    c: Coincident(g660,g661)
    c: Coincident(g661,g662)
    c: Coincident(g662,g663)
    c: Coincident(g663,g664)
    c: Coincident(g664,g665)
    c: Coincident(g665,g666)
    c: Coincident(g666,g667)
    c: Coincident(g667,g668)
    c: Coincident(g668,g669)
    c: Coincident(g669,g670)
    c: Coincident(g670,g671)
    c: Coincident(g671,g672)
    c: Coincident(g672,g673)
    c: Coincident(g673,g674)
    c: Coincident(g674,g675)
    c: Coincident(g675,g588)
    c: Coincident(g676,g677)
    c: Coincident(g677,g678)
    c: Coincident(g678,g679)
    c: Coincident(g679,g680)
    c: Coincident(g680,g681)
    c: Coincident(g681,g682)
    c: Coincident(g682,g683)
    c: Coincident(g683,g684)
    c: Coincident(g684,g685)
    c: Coincident(g685,g686)
    c: Coincident(g686,g687)
    c: Coincident(g687,g688)
    c: Coincident(g688,g689)
    c: Coincident(g689,g690)
    c: Coincident(g690,g691)
    c: Coincident(g691,g676)
    c: Coincident(g692,g693)
    c: Coincident(g693,g694)
    c: Coincident(g694,g695)
    c: Coincident(g695,g696)
    c: Coincident(g696,g697)
    c: Coincident(g697,g698)
    c: Coincident(g698,g699)
    c: Coincident(g699,g700)
    c: Coincident(g700,g701)
    c: Coincident(g701,g702)
    c: Coincident(g702,g703)
    c: Coincident(g703,g704)
    c: Coincident(g704,g705)
    c: Coincident(g705,g706)
    c: Coincident(g706,g707)
    c: Coincident(g707,g708)
    c: Coincident(g708,g709)
    c: Coincident(g709,g710)
    c: Coincident(g710,g711)
    c: Coincident(g711,g712)
    c: Coincident(g712,g713)
    c: Coincident(g713,g714)
    c: Coincident(g714,g715)
    c: Coincident(g715,g716)
    c: Coincident(g716,g717)
    c: Coincident(g717,g718)
    c: Coincident(g718,g719)
    c: Coincident(g719,g720)
    c: Coincident(g720,g721)
    c: Coincident(g721,g722)
    c: Coincident(g722,g723)
    c: Coincident(g723,g724)
    c: Coincident(g724,g725)
    c: Coincident(g725,g726)
    c: Coincident(g726,g727)
    c: Coincident(g727,g728)
    c: Coincident(g728,g729)
    c: Coincident(g729,g730)
    c: Coincident(g730,g731)
    c: Coincident(g731,g692)
    c: Coincident(g732,g733)
    c: Coincident(g733,g734)
    c: Coincident(g734,g735)
    c: Coincident(g735,g736)
    c: Coincident(g736,g737)
    c: Coincident(g737,g738)
    c: Coincident(g738,g739)
    c: Coincident(g739,g740)
    c: Coincident(g740,g741)
    c: Coincident(g741,g742)
    c: Coincident(g742,g743)
    c: Coincident(g743,g744)
    c: Coincident(g744,g745)
    c: Coincident(g745,g746)
    c: Coincident(g746,g747)
    c: Coincident(g747,g748)
    c: Coincident(g748,g749)
    c: Coincident(g749,g750)
    c: Coincident(g750,g751)
    c: Coincident(g751,g752)
    c: Coincident(g752,g753)
    c: Coincident(g753,g754)
    c: Coincident(g754,g755)
    c: Coincident(g755,g756)
    c: Coincident(g756,g757)
    c: Coincident(g757,g758)
    c: Coincident(g758,g759)
    c: Coincident(g759,g760)
    c: Coincident(g760,g761)
    c: Coincident(g761,g762)
    c: Coincident(g762,g763)
    c: Coincident(g763,g732)
    c: Coincident(g764,g765)
    c: Coincident(g765,g766)
    c: Coincident(g766,g767)
    c: Coincident(g767,g768)
    c: Coincident(g768,g769)
    c: Coincident(g769,g770)
    c: Coincident(g770,g771)
    c: Coincident(g771,g772)
    c: Coincident(g772,g773)
    c: Coincident(g773,g774)
    c: Coincident(g774,g775)
    c: Coincident(g775,g776)
    c: Coincident(g776,g777)
    c: Coincident(g777,g778)
    c: Coincident(g778,g779)
    c: Coincident(g779,g780)
    c: Coincident(g780,g781)
    c: Coincident(g781,g782)
    c: Coincident(g782,g783)
    c: Coincident(g783,g784)
    c: Coincident(g784,g785)
    c: Coincident(g785,g786)
    c: Coincident(g786,g787)
    c: Coincident(g787,g764)
    c: Coincident(g788,g789)
    c: Coincident(g789,g790)
    c: Coincident(g790,g791)
    c: Coincident(g791,g792)
    c: Coincident(g792,g793)
    c: Coincident(g793,g794)
    c: Coincident(g794,g795)
    c: Coincident(g795,g796)
    c: Coincident(g796,g797)
    c: Coincident(g797,g798)
    c: Coincident(g798,g799)
    c: Coincident(g799,g800)
    c: Coincident(g800,g801)
    c: Coincident(g801,g802)
    c: Coincident(g802,g803)
    c: Coincident(g803,g804)
    c: Coincident(g804,g805)
    c: Coincident(g805,g806)
    c: Coincident(g806,g807)
    c: Coincident(g807,g808)
    c: Coincident(g808,g809)
    c: Coincident(g809,g810)
    c: Coincident(g810,g811)
    c: Coincident(g811,g812)
    c: Coincident(g812,g813)
    c: Coincident(g813,g814)
    c: Coincident(g814,g815)
    c: Coincident(g815,g816)
    c: Coincident(g816,g817)
    c: Coincident(g817,g818)
    c: Coincident(g818,g819)
    c: Coincident(g819,g820)
    c: Coincident(g820,g821)
    c: Coincident(g821,g822)
    c: Coincident(g822,g823)
    c: Coincident(g823,g824)
    c: Coincident(g824,g825)
    c: Coincident(g825,g826)
    c: Coincident(g826,g827)
    c: Coincident(g827,g828)
    c: Coincident(g828,g829)
    c: Coincident(g829,g830)
    c: Coincident(g830,g831)
    c: Coincident(g831,g832)
    c: Coincident(g832,g833)
    c: Coincident(g833,g834)
    c: Coincident(g834,g835)
    c: Coincident(g835,g836)
    c: Coincident(g836,g837)
    c: Coincident(g837,g838)
    c: Coincident(g838,g839)
    c: Coincident(g839,g840)
    c: Coincident(g840,g841)
    c: Coincident(g841,g842)
    c: Coincident(g842,g843)
    c: Coincident(g843,g844)
    c: Coincident(g844,g845)
    c: Coincident(g845,g846)
    c: Coincident(g846,g847)
    c: Coincident(g847,g848)
    c: Coincident(g848,g849)
    c: Coincident(g849,g850)
    c: Coincident(g850,g851)
    c: Coincident(g851,g852)
    c: Coincident(g852,g853)
    c: Coincident(g853,g854)
    c: Coincident(g854,g855)
    c: Coincident(g855,g856)
    c: Coincident(g856,g857)
    c: Coincident(g857,g858)
    c: Coincident(g858,g859)
    c: Coincident(g859,g788)
FEATURE [PartDesign::Pocket] Pocket034
  BaseFeature = -> Pocket024
  Direction = (-1e-16,-1,0)
  Length = 0
  Length2 = 5
  Offset = 0.4
  Profile = -> Sketch032
  ReferenceAxis = -> Sketch032 [N_Axis]
  Refine = true
  Suppressed = false
  Type = 3
  UpToFace = -> Pocket024 [Face8]
FEATURE [PartDesign::Body] Body004  label="GameCube DOL-001 IO Full w SD"
  AllowCompound = false
  Group = -> [Clone003,ShapeString003,Pocket022,ShapeString004,Pocket023,ShapeString005,Pocket024,Sketch032,Pocket034]
  Origin = -> Origin004
  Tip = -> Pocket034
FEATURE [PartDesign::Pocket] Pocket035
  BaseFeature = -> Pocket028
  Direction = (-1e-16,-1,0)
  Length = 0
  Length2 = 5
  Offset = 0.4
  Profile = -> Sketch033
  ReferenceAxis = -> Sketch033 [N_Axis]
  Refine = true
  Suppressed = false
  Type = 3
  UpToFace = -> Pocket028 [Face73]
FEATURE [PartDesign::Body] Body005  label="GameCube DOL-001 Full"
  AllowCompound = false
  Group = -> [Clone004,ShapeString006,ShapeString007,ShapeString008,Pocket026,Pocket027,Pocket028,Sketch033,Pocket035]
  Origin = -> Origin005
  Tip = -> Pocket035
FEATURE [PartDesign::Pocket] Pocket036
  BaseFeature = -> Pocket031
  Direction = (-1e-16,-1,0)
  Length = 0
  Length2 = 5
  Offset = 0.4
  Profile = -> Sketch034
  ReferenceAxis = -> Sketch034 [N_Axis]
  Refine = true
  Suppressed = false
  Type = 3
  UpToFace = -> Pocket031 [Face3]
FEATURE [PartDesign::Body] Body006  label="GameCube DOL-101 Full w SD"
  AllowCompound = false
  Group = -> [Clone005,ShapeString009,ShapeString011,Pocket029,Pocket031,Sketch034,Pocket036]
  Origin = -> Origin006
  Tip = -> Pocket036
FEATURE [PartDesign::Pocket] Pocket037
  BaseFeature = -> Pocket033
  Direction = (-1e-16,-1,0)
  Length = 0
  Length2 = 5
  Offset = 0.4
  Profile = -> Sketch035
  ReferenceAxis = -> Sketch035 [N_Axis]
  Refine = true
  Suppressed = false
  Type = 3
  UpToFace = -> Pocket033 [Face3]
FEATURE [PartDesign::Body] Body007  label="GameCube DOL-101 Full"
  AllowCompound = false
  Group = -> [Clone006,ShapeString012,ShapeString014,Pocket032,Pocket033,Sketch035,Pocket037]
  Origin = -> Origin007
  Tip = -> Pocket037
FEATURE [App::DocumentObjectGroup] Group001  label="With Labels"
  Group = -> [Body004,Body005,Body006,Body007]
